annotation { "Feature Type Name" : "Feature", "Feature Type Description" : "" }
export const myFeature = defineFeature(function(context is Context, id is Id, definition is map)
    precondition{}
    {
        {
            var Q0;
            Q0=qCreatedBy(makeId("Top.planeOp"),FACE);
            var sketch = newSketch(context, id + "F0", { "sketchPlane" : qUnion([Q0])});
            skLineSegment(sketch, "E0.bottom", {"start": v(-100, -37.5) * mm, "end": v(100, -37.5) * mm, "construction": true});
            skLineSegment(sketch, "E0.top", {"start": v(-100, 37.5) * mm, "end": v(100, 37.5) * mm, "construction": true});
            skLineSegment(sketch, "E0.left", {"start": v(-100, -37.5) * mm, "end": v(-100, 37.5) * mm, "construction": true});
            skLineSegment(sketch, "E0.right", {"start": v(100, -37.5) * mm, "end": v(100, 37.5) * mm, "construction": true});
            skPoint(sketch, "E0.middle", {"position": v(0, 0) * mm});
            skLineSegment(sketch, "E1.bottom", {"start": v(-70, -15.23) * mm, "end": v(70, -15.23) * mm});
            skLineSegment(sketch, "E1.top", {"start": v(-70, 15.23) * mm, "end": v(70, 15.23) * mm});
            skLineSegment(sketch, "E1.left", {"start": v(-70, -15.23) * mm, "end": v(-70, 15.23) * mm});
            skLineSegment(sketch, "E1.right", {"start": v(70, -15.23) * mm, "end": v(70, 15.23) * mm});
            skLineSegment(sketch, "E2", {"start": v(-70, 0) * mm, "end": v(-95, 0) * mm, "construction": true});
            skLineSegment(sketch, "E3", {"start": v(-95, 0) * mm, "end": v(-70, 15.23) * mm});
            skLineSegment(sketch, "E4", {"start": v(-95, 0) * mm, "end": v(-70, -15.23) * mm});
            skLineSegment(sketch, "E5", {"start": v(70, 15.23) * mm, "end": v(95, 0) * mm});
            skLineSegment(sketch, "E6", {"start": v(95, 0) * mm, "end": v(70, -15.23) * mm});
            skLineSegment(sketch, "E7", {"start": v(70, 0) * mm, "end": v(95, 0) * mm, "construction": true});
            skSolve(sketch);
        }
        {
            var Q0;
            Q0=qSketchRegion(id+"F0",true);
            extrude(context, id + "F1", {"entities" : qUnion([Q0]), "depth" : 5 * mm, "offsetDistance" : 25 * mm});
        }
        {
            var Q0;
            Q0=makeQuery(id+"F1.opExtrude","SWEPT_EDGE",EDGE,{"disambiguationData":[OSD([sQuery(id+"F0.wireOp",EDGE,"E3"),sQuery(id+"F0.wireOp",EDGE,"E4")])]});
            var Q1;
            Q1=makeQuery(id+"F1.opExtrude","SWEPT_EDGE",EDGE,{"disambiguationData":[OSD([sQuery(id+"F0.wireOp",EDGE,"E5"),sQuery(id+"F0.wireOp",EDGE,"E6")])]});
            fillet(context, id + "F2", {"entities" : qUnion([Q0, Q1]), "radius" : 10 * mm, "tangentPropagation" : true, "allowEdgeOverflow" : false});
        }
        {
            var Q0;
            Q0=makeQuery(id+"F1.opExtrude","SWEPT_EDGE",EDGE,{"disambiguationData":[OSD([sQuery(id+"F0.wireOp",EDGE,"E1.bottom"),sQuery(id+"F0.wireOp",EDGE,"E1.right"),sQuery(id+"F0.wireOp",EDGE,"E6")])]});
            var Q1;
            Q1=makeQuery(id+"F1.opExtrude","SWEPT_EDGE",EDGE,{"disambiguationData":[OSD([sQuery(id+"F0.wireOp",EDGE,"E1.bottom"),sQuery(id+"F0.wireOp",EDGE,"E1.left"),sQuery(id+"F0.wireOp",EDGE,"E4")])]});
            var Q2;
            Q2=makeQuery(id+"F1.opExtrude","SWEPT_EDGE",EDGE,{"disambiguationData":[OSD([sQuery(id+"F0.wireOp",EDGE,"E1.top"),sQuery(id+"F0.wireOp",EDGE,"E1.left"),sQuery(id+"F0.wireOp",EDGE,"E3")])]});
            var Q3;
            Q3=makeQuery(id+"F1.opExtrude","SWEPT_EDGE",EDGE,{"disambiguationData":[OSD([sQuery(id+"F0.wireOp",EDGE,"E1.top"),sQuery(id+"F0.wireOp",EDGE,"E1.right"),sQuery(id+"F0.wireOp",EDGE,"E5")])]});
            fillet(context, id + "F3", {"entities" : qUnion([Q0, Q1, Q2, Q3]), "radius" : 10 * mm, "tangentPropagation" : true, "allowEdgeOverflow" : false});
        }
        {
            var Q0;
            Q0=makeQuery(id+"F1.opExtrude","CAP_FACE",FACE,{"disambiguationData":[OSD([sQuery(id+"F0.wireOp",EDGE,"E1.bottom"),sQuery(id+"F0.wireOp",EDGE,"E1.top"),sQuery(id+"F0.wireOp",EDGE,"E3"),sQuery(id+"F0.wireOp",EDGE,"E4"),sQuery(id+"F0.wireOp",EDGE,"E5"),sQuery(id+"F0.wireOp",EDGE,"E6")])],"isStart":false});
            var sketch = newSketch(context, id + "F4", { "sketchPlane" : qUnion([Q0])});
            skText(sketch, "E8", { "text": "Miss Loveday", "fontName": "OpenSans-BoldItalic.ttf"});
            const initialGuessF4  = {"E8": [-0.05, -0.00564, 1, 0, 0.01129]};
            skSetInitialGuess(sketch, initialGuessF4);
            skSolve(sketch);
        }
        {
            var Q0;
            Q0=qSketchRegion(id+"F4",true);
            extrude(context, id + "F5", {"entities" : qUnion([Q0]), "operationType" : NewBodyOperationType.ADD, "depth" : 3 * mm, "offsetDistance" : 25 * mm});
        }
        {
            var Q0;
            {var subQ0=sQuery(id+"F0.wireOp",EDGE,"E5");var subQ2=sQuery(id+"F0.wireOp",EDGE,"E1.top");var subQ3=sQuery(id+"F0.wireOp",EDGE,"E3");var subQ5=sQuery(id+"F0.wireOp",EDGE,"E4");var subQ6=sQuery(id+"F0.wireOp",EDGE,"E6");var subQ7=sQuery(id+"F0.wireOp",EDGE,"E1.bottom");Q0=makeQuery(id+"F5.boolean.opBoolean","SPLIT",FACE,{"disambiguationData":[TD([makeQuery(id+"F1.opExtrude","SWEPT_FACE",FACE,{"disambiguationData":[OSD([subQ7])]})])],"derivedFrom":makeQuery(id+"F1.opExtrude","CAP_FACE",FACE,{"disambiguationData":[OSD([subQ7,subQ2,subQ3,subQ5,subQ0,subQ6])],"isStart":false})});}
            var sketch = newSketch(context, id + "F6", { "sketchPlane" : qUnion([Q0])});
            skPoint(sketch, "E9", {"position": v(-75.78, 0) * mm});
            skPoint(sketch, "E10", {"position": v(75.78, 0) * mm});
            skSolve(sketch);
        }
        {
            var Q0;
            Q0=sQuery(id+"F6.wireOp",VERTEX,"E10");
            var Q1;
            Q1=sQuery(id+"F6.wireOp",VERTEX,"E9");
            var Q2;
            Q2=makeQuery(id+"F1.opExtrude","SWEPT_BODY",BODY,{"disambiguationData":[OSD([sQuery(id+"F0.wireOp",EDGE,"E1.bottom"),sQuery(id+"F0.wireOp",EDGE,"E1.top"),sQuery(id+"F0.wireOp",EDGE,"E3"),sQuery(id+"F0.wireOp",EDGE,"E4"),sQuery(id+"F0.wireOp",EDGE,"E5"),sQuery(id+"F0.wireOp",EDGE,"E6")])]});
            hole(context, id + "F7", {"style" : HoleStyle.SIMPLE, "endStyle" : HoleEndStyle.THROUGH, "standardTappedOrClearance" : lookupTablePath({ "fit" : "Normal", "standard" : "ISO", "size" : "M5", "type" : "Clearance" }), "standardBlindInLast" : lookupTablePath({ "fit" : "Normal", "standard" : "ISO", "size" : "M5", "type" : "Clearance" }), "holeDiameter" : 5.5 * mm, "majorDiameter" : 5 * mm, "isTappedThrough" : true, "tappedDepth" : 12 * mm, "tapClearance" : 3, "locations" : qUnion([Q0, Q1]), "scope" : qUnion([Q2])});
        }
        {
            var Q0;
            {var subQ0=sQuery(id+"F0.wireOp",EDGE,"E5");var subQ2=sQuery(id+"F0.wireOp",EDGE,"E1.top");var subQ3=sQuery(id+"F0.wireOp",EDGE,"E3");var subQ5=sQuery(id+"F0.wireOp",EDGE,"E4");var subQ6=sQuery(id+"F0.wireOp",EDGE,"E6");var subQ7=sQuery(id+"F0.wireOp",EDGE,"E1.bottom");Q0=makeQuery(id+"F5.boolean.opBoolean","SPLIT",FACE,{"disambiguationData":[TD([makeQuery(id+"F1.opExtrude","SWEPT_FACE",FACE,{"disambiguationData":[OSD([subQ7])]})])],"derivedFrom":makeQuery(id+"F1.opExtrude","CAP_FACE",FACE,{"disambiguationData":[OSD([subQ7,subQ2,subQ3,subQ5,subQ0,subQ6])],"isStart":false})});}
            var sketch = newSketch(context, id + "F8", { "sketchPlane" : qUnion([Q0])});
            skLineSegment(sketch, "E11.bottom", {"start": v(-69.8, 10) * mm, "end": v(-49.8, 10) * mm, "construction": true});
            skLineSegment(sketch, "E11.top", {"start": v(-69.8, -10) * mm, "end": v(-49.8, -10) * mm, "construction": true});
            skLineSegment(sketch, "E11.left", {"start": v(-69.8, 10) * mm, "end": v(-69.8, -10) * mm, "construction": true});
            skLineSegment(sketch, "E11.right", {"start": v(-49.8, 10) * mm, "end": v(-49.8, -10) * mm, "construction": true});
            skLineSegment(sketch, "E12", {"start": v(-69.8, -10) * mm, "end": v(-49.8, 10) * mm, "construction": true});
            skLineSegment(sketch, "E13", {"start": v(-75.78, 0) * mm, "end": v(-59.8, 0) * mm, "construction": true});
            skLineSegment(sketch, "E14", {"start": v(-64.45, -8.4) * mm, "end": v(-65.16, -7.74) * mm});
            skLineSegment(sketch, "E15", {"start": v(-65.16, -7.74) * mm, "end": v(-65.7, -7.23) * mm});
            skLineSegment(sketch, "E16", {"start": v(-65.7, -7.23) * mm, "end": v(-66.13, -6.83) * mm});
            skLineSegment(sketch, "E17", {"start": v(-66.13, -6.83) * mm, "end": v(-66.45, -6.52) * mm});
            skLineSegment(sketch, "E18", {"start": v(-66.45, -6.52) * mm, "end": v(-66.69, -6.26) * mm});
            skLineSegment(sketch, "E19", {"start": v(-66.69, -6.26) * mm, "end": v(-66.87, -6.05) * mm});
            skLineSegment(sketch, "E20", {"start": v(-66.87, -6.05) * mm, "end": v(-67.03, -5.85) * mm});
            skLineSegment(sketch, "E21", {"start": v(-67.03, -5.85) * mm, "end": v(-67.17, -5.64) * mm});
            skLineSegment(sketch, "E22", {"start": v(-67.17, -5.64) * mm, "end": v(-67.67, -4.76) * mm});
            skLineSegment(sketch, "E23", {"start": v(-67.67, -4.76) * mm, "end": v(-67.96, -3.88) * mm});
            skLineSegment(sketch, "E24", {"start": v(-67.96, -3.88) * mm, "end": v(-68.07, -3.03) * mm});
            skLineSegment(sketch, "E25", {"start": v(-68.07, -3.03) * mm, "end": v(-67.98, -2.23) * mm});
            skLineSegment(sketch, "E26", {"start": v(-67.98, -2.23) * mm, "end": v(-67.72, -1.5) * mm});
            skLineSegment(sketch, "E27", {"start": v(-67.72, -1.5) * mm, "end": v(-67.28, -0.88) * mm});
            skLineSegment(sketch, "E28", {"start": v(-67.28, -0.88) * mm, "end": v(-66.67, -0.38) * mm});
            skLineSegment(sketch, "E29", {"start": v(-66.67, -0.38) * mm, "end": v(-65.9, -0.02) * mm});
            skLineSegment(sketch, "E30", {"start": v(-65.9, -0.02) * mm, "end": v(-65.77, 0.01) * mm});
            skLineSegment(sketch, "E31", {"start": v(-65.77, 0.01) * mm, "end": v(-65.52, 0.08) * mm});
            skLineSegment(sketch, "E32", {"start": v(-65.52, 0.08) * mm, "end": v(-65.16, 0.17) * mm});
            skLineSegment(sketch, "E33", {"start": v(-65.16, 0.17) * mm, "end": v(-64.71, 0.27) * mm});
            skLineSegment(sketch, "E34", {"start": v(-64.71, 0.27) * mm, "end": v(-64.18, 0.4) * mm});
            skLineSegment(sketch, "E35", {"start": v(-64.18, 0.4) * mm, "end": v(-63.6, 0.54) * mm});
            skLineSegment(sketch, "E36", {"start": v(-63.6, 0.54) * mm, "end": v(-62.95, 0.7) * mm});
            skLineSegment(sketch, "E37", {"start": v(-62.95, 0.7) * mm, "end": v(-62.28, 0.85) * mm});
            skLineSegment(sketch, "E38", {"start": v(-62.28, 0.85) * mm, "end": v(-58.96, 1.63) * mm});
            skLineSegment(sketch, "E39", {"start": v(-58.96, 1.63) * mm, "end": v(-57.57, 4.57) * mm});
            skLineSegment(sketch, "E40", {"start": v(-57.57, 4.57) * mm, "end": v(-57.23, 5.28) * mm});
            skLineSegment(sketch, "E41", {"start": v(-57.23, 5.28) * mm, "end": v(-56.93, 5.9) * mm});
            skLineSegment(sketch, "E42", {"start": v(-56.93, 5.9) * mm, "end": v(-56.68, 6.43) * mm});
            skLineSegment(sketch, "E43", {"start": v(-56.68, 6.43) * mm, "end": v(-56.46, 6.87) * mm});
            skLineSegment(sketch, "E44", {"start": v(-56.46, 6.87) * mm, "end": v(-56.28, 7.21) * mm});
            skLineSegment(sketch, "E45", {"start": v(-56.28, 7.21) * mm, "end": v(-56.14, 7.48) * mm});
            skLineSegment(sketch, "E46", {"start": v(-56.14, 7.48) * mm, "end": v(-56.03, 7.67) * mm});
            skLineSegment(sketch, "E47", {"start": v(-56.03, 7.67) * mm, "end": v(-55.96, 7.77) * mm});
            skLineSegment(sketch, "E48", {"start": v(-55.96, 7.77) * mm, "end": v(-55.72, 8) * mm});
            skLineSegment(sketch, "E49", {"start": v(-55.72, 8) * mm, "end": v(-55.44, 8.21) * mm});
            skLineSegment(sketch, "E50", {"start": v(-55.44, 8.21) * mm, "end": v(-55.13, 8.38) * mm});
            skLineSegment(sketch, "E51", {"start": v(-55.13, 8.38) * mm, "end": v(-54.82, 8.49) * mm});
            skLineSegment(sketch, "E52", {"start": v(-54.82, 8.49) * mm, "end": v(-54.42, 8.52) * mm});
            skLineSegment(sketch, "E53", {"start": v(-54.42, 8.52) * mm, "end": v(-53.98, 8.45) * mm});
            skLineSegment(sketch, "E54", {"start": v(-53.98, 8.45) * mm, "end": v(-53.56, 8.28) * mm});
            skLineSegment(sketch, "E55", {"start": v(-53.56, 8.28) * mm, "end": v(-53.2, 8.03) * mm});
            skLineSegment(sketch, "E56", {"start": v(-53.2, 8.03) * mm, "end": v(-52.9, 7.87) * mm});
            skLineSegment(sketch, "E57", {"start": v(-52.9, 7.87) * mm, "end": v(-52.3, 7.7) * mm});
            skLineSegment(sketch, "E58", {"start": v(-52.3, 7.7) * mm, "end": v(-52.01, 7.62) * mm});
            skLineSegment(sketch, "E59", {"start": v(-52.01, 7.62) * mm, "end": v(-51.76, 7.55) * mm});
            skLineSegment(sketch, "E60", {"start": v(-51.76, 7.55) * mm, "end": v(-51.58, 7.48) * mm});
            skLineSegment(sketch, "E61", {"start": v(-51.58, 7.48) * mm, "end": v(-51.5, 7.43) * mm});
            skLineSegment(sketch, "E62", {"start": v(-51.5, 7.43) * mm, "end": v(-51.45, 7.33) * mm});
            skLineSegment(sketch, "E63", {"start": v(-51.45, 7.33) * mm, "end": v(-51.45, 7.18) * mm});
            skLineSegment(sketch, "E64", {"start": v(-51.45, 7.18) * mm, "end": v(-51.5, 6.96) * mm});
            skLineSegment(sketch, "E65", {"start": v(-51.5, 6.96) * mm, "end": v(-51.58, 6.65) * mm});
            skLineSegment(sketch, "E66", {"start": v(-51.58, 6.65) * mm, "end": v(-51.67, 6.36) * mm});
            skLineSegment(sketch, "E67", {"start": v(-51.67, 6.36) * mm, "end": v(-52.71, 5.74) * mm});
            skLineSegment(sketch, "E68", {"start": v(-52.71, 5.74) * mm, "end": v(-53.76, 5.12) * mm});
            skLineSegment(sketch, "E69", {"start": v(-53.76, 5.12) * mm, "end": v(-53.76, 2.41) * mm});
            skLineSegment(sketch, "E70", {"start": v(-53.76, 2.41) * mm, "end": v(-53.77, 1.3) * mm});
            skLineSegment(sketch, "E71", {"start": v(-53.77, 1.3) * mm, "end": v(-53.78, 0.33) * mm});
            skLineSegment(sketch, "E72", {"start": v(-53.78, 0.33) * mm, "end": v(-53.8, -0.39) * mm});
            skLineSegment(sketch, "E73", {"start": v(-53.8, -0.39) * mm, "end": v(-53.82, -0.79) * mm});
            skLineSegment(sketch, "E74", {"start": v(-53.82, -0.79) * mm, "end": v(-53.9, -1.32) * mm});
            skLineSegment(sketch, "E75", {"start": v(-53.9, -1.32) * mm, "end": v(-54.05, -1.87) * mm});
            skLineSegment(sketch, "E76", {"start": v(-54.05, -1.87) * mm, "end": v(-54.22, -2.41) * mm});
            skLineSegment(sketch, "E77", {"start": v(-54.22, -2.41) * mm, "end": v(-54.42, -2.88) * mm});
            skLineSegment(sketch, "E78", {"start": v(-54.42, -2.88) * mm, "end": v(-54.5, -3.02) * mm});
            skLineSegment(sketch, "E79", {"start": v(-54.5, -3.02) * mm, "end": v(-54.54, -3.13) * mm});
            skLineSegment(sketch, "E80", {"start": v(-54.54, -3.13) * mm, "end": v(-54.58, -3.22) * mm});
            skLineSegment(sketch, "E81", {"start": v(-54.58, -3.22) * mm, "end": v(-54.6, -3.29) * mm});
            skLineSegment(sketch, "E82", {"start": v(-54.6, -3.29) * mm, "end": v(-54.6, -3.34) * mm});
            skLineSegment(sketch, "E83", {"start": v(-54.6, -3.34) * mm, "end": v(-54.6, -3.39) * mm});
            skLineSegment(sketch, "E84", {"start": v(-54.6, -3.39) * mm, "end": v(-54.58, -3.43) * mm});
            skLineSegment(sketch, "E85", {"start": v(-54.58, -3.43) * mm, "end": v(-54.55, -3.49) * mm});
            skLineSegment(sketch, "E86", {"start": v(-54.55, -3.49) * mm, "end": v(-54.4, -3.8) * mm});
            skLineSegment(sketch, "E87", {"start": v(-54.4, -3.8) * mm, "end": v(-54.3, -4.08) * mm});
            skLineSegment(sketch, "E88", {"start": v(-54.3, -4.08) * mm, "end": v(-54.24, -4.37) * mm});
            skLineSegment(sketch, "E89", {"start": v(-54.24, -4.37) * mm, "end": v(-54.23, -4.7) * mm});
            skLineSegment(sketch, "E90", {"start": v(-54.23, -4.7) * mm, "end": v(-54.23, -4.96) * mm});
            skLineSegment(sketch, "E91", {"start": v(-54.23, -4.96) * mm, "end": v(-54.26, -5.2) * mm});
            skLineSegment(sketch, "E92", {"start": v(-54.26, -5.2) * mm, "end": v(-54.34, -5.42) * mm});
            skLineSegment(sketch, "E93", {"start": v(-54.34, -5.42) * mm, "end": v(-54.46, -5.67) * mm});
            skLineSegment(sketch, "E94", {"start": v(-54.46, -5.67) * mm, "end": v(-54.65, -5.97) * mm});
            skLineSegment(sketch, "E95", {"start": v(-54.65, -5.97) * mm, "end": v(-54.92, -6.33) * mm});
            skLineSegment(sketch, "E96", {"start": v(-54.92, -6.33) * mm, "end": v(-55.29, -6.8) * mm});
            skLineSegment(sketch, "E97", {"start": v(-55.29, -6.8) * mm, "end": v(-55.77, -7.37) * mm});
            skLineSegment(sketch, "E98", {"start": v(-55.77, -7.37) * mm, "end": v(-56.09, -7.76) * mm});
            skLineSegment(sketch, "E99", {"start": v(-56.09, -7.76) * mm, "end": v(-56.35, -8.07) * mm});
            skLineSegment(sketch, "E100", {"start": v(-56.35, -8.07) * mm, "end": v(-56.57, -8.33) * mm});
            skLineSegment(sketch, "E101", {"start": v(-56.57, -8.33) * mm, "end": v(-56.75, -8.53) * mm});
            skLineSegment(sketch, "E102", {"start": v(-56.75, -8.53) * mm, "end": v(-56.89, -8.67) * mm});
            skLineSegment(sketch, "E103", {"start": v(-56.89, -8.67) * mm, "end": v(-57, -8.77) * mm});
            skLineSegment(sketch, "E104", {"start": v(-57, -8.77) * mm, "end": v(-57.07, -8.82) * mm});
            skLineSegment(sketch, "E105", {"start": v(-57.07, -8.82) * mm, "end": v(-57.11, -8.84) * mm});
            skLineSegment(sketch, "E106", {"start": v(-57.11, -8.84) * mm, "end": v(-57.23, -8.8) * mm});
            skLineSegment(sketch, "E107", {"start": v(-57.23, -8.8) * mm, "end": v(-57.34, -8.72) * mm});
            skLineSegment(sketch, "E108", {"start": v(-57.34, -8.72) * mm, "end": v(-57.43, -8.61) * mm});
            skLineSegment(sketch, "E109", {"start": v(-57.43, -8.61) * mm, "end": v(-57.46, -8.5) * mm});
            skLineSegment(sketch, "E110", {"start": v(-57.46, -8.5) * mm, "end": v(-57.44, -8.36) * mm});
            skLineSegment(sketch, "E111", {"start": v(-57.44, -8.36) * mm, "end": v(-57.4, -8.04) * mm});
            skLineSegment(sketch, "E112", {"start": v(-57.4, -8.04) * mm, "end": v(-57.32, -7.58) * mm});
            skLineSegment(sketch, "E113", {"start": v(-57.32, -7.58) * mm, "end": v(-57.22, -7.02) * mm});
            skLineSegment(sketch, "E114", {"start": v(-57.22, -7.02) * mm, "end": v(-57.13, -6.48) * mm});
            skLineSegment(sketch, "E115", {"start": v(-57.13, -6.48) * mm, "end": v(-57.07, -6.03) * mm});
            skLineSegment(sketch, "E116", {"start": v(-57.07, -6.03) * mm, "end": v(-57.03, -5.72) * mm});
            skLineSegment(sketch, "E117", {"start": v(-57.03, -5.72) * mm, "end": v(-57.03, -5.6) * mm});
            skLineSegment(sketch, "E118", {"start": v(-57.03, -5.6) * mm, "end": v(-57.08, -5.6) * mm});
            skLineSegment(sketch, "E119", {"start": v(-57.08, -5.6) * mm, "end": v(-57.17, -5.63) * mm});
            skLineSegment(sketch, "E120", {"start": v(-57.17, -5.63) * mm, "end": v(-57.3, -5.66) * mm});
            skLineSegment(sketch, "E121", {"start": v(-57.3, -5.66) * mm, "end": v(-57.44, -5.71) * mm});
            skLineSegment(sketch, "E122", {"start": v(-57.44, -5.71) * mm, "end": v(-57.69, -5.8) * mm});
            skLineSegment(sketch, "E123", {"start": v(-57.69, -5.8) * mm, "end": v(-57.93, -5.85) * mm});
            skLineSegment(sketch, "E124", {"start": v(-57.93, -5.85) * mm, "end": v(-58.2, -5.9) * mm});
            skLineSegment(sketch, "E125", {"start": v(-58.2, -5.9) * mm, "end": v(-58.55, -5.93) * mm});
            skLineSegment(sketch, "E126", {"start": v(-58.55, -5.93) * mm, "end": v(-58.99, -5.95) * mm});
            skLineSegment(sketch, "E127", {"start": v(-58.99, -5.95) * mm, "end": v(-59.55, -5.96) * mm});
            skLineSegment(sketch, "E128", {"start": v(-59.55, -5.96) * mm, "end": v(-60.28, -5.97) * mm});
            skLineSegment(sketch, "E129", {"start": v(-60.28, -5.97) * mm, "end": v(-61.2, -5.97) * mm});
            skLineSegment(sketch, "E130", {"start": v(-61.2, -5.97) * mm, "end": v(-63.87, -5.97) * mm});
            skLineSegment(sketch, "E131", {"start": v(-63.87, -5.97) * mm, "end": v(-63.5, -6.4) * mm});
            skLineSegment(sketch, "E132", {"start": v(-63.5, -6.4) * mm, "end": v(-63.12, -6.96) * mm});
            skLineSegment(sketch, "E133", {"start": v(-63.12, -6.96) * mm, "end": v(-62.83, -7.61) * mm});
            skLineSegment(sketch, "E134", {"start": v(-62.83, -7.61) * mm, "end": v(-62.64, -8.31) * mm});
            skLineSegment(sketch, "E135", {"start": v(-62.64, -8.31) * mm, "end": v(-62.58, -9.03) * mm});
            skLineSegment(sketch, "E136", {"start": v(-62.58, -9.03) * mm, "end": v(-62.6, -9.34) * mm});
            skLineSegment(sketch, "E137", {"start": v(-62.6, -9.34) * mm, "end": v(-62.64, -9.57) * mm});
            skLineSegment(sketch, "E138", {"start": v(-62.64, -9.57) * mm, "end": v(-62.72, -9.72) * mm});
            skLineSegment(sketch, "E139", {"start": v(-62.72, -9.72) * mm, "end": v(-62.82, -9.78) * mm});
            skLineSegment(sketch, "E140", {"start": v(-62.82, -9.78) * mm, "end": v(-62.97, -9.7) * mm});
            skLineSegment(sketch, "E141", {"start": v(-62.97, -9.7) * mm, "end": v(-63.3, -9.42) * mm});
            skLineSegment(sketch, "E142", {"start": v(-63.3, -9.42) * mm, "end": v(-63.8, -8.98) * mm});
            skLineSegment(sketch, "E143", {"start": v(-63.8, -8.98) * mm, "end": v(-64.45, -8.4) * mm});
            skCircle(sketch, "E144", {"center": v(-54.26, 7.57) * mm, "radius": 0.28 * mm});
            skSolve(sketch);
        }
        {
            var Q0;
            Q0=makeQuery(id+"F8.imprint","IMPRINT",FACE,{"disambiguationData":[TD([[makeQuery(id+"F8.imprint","IMPRINT",EDGE,{"derivedFrom":sQuery(id+"F8.wireOp",EDGE,"E14")}),-1.0]])]});
            extrude(context, id + "F9", {"entities" : qUnion([Q0]), "operationType" : NewBodyOperationType.ADD, "depth" : 3 * mm, "offsetDistance" : 25 * mm});
        }
        {
            var Q0;
            {var subQ44=sQuery(id+"F0.wireOp",EDGE,"E5");var subQ46=sQuery(id+"F0.wireOp",EDGE,"E1.top");var subQ49=sQuery(id+"F0.wireOp",EDGE,"E3");var subQ55=sQuery(id+"F0.wireOp",EDGE,"E6");var subQ56=sQuery(id+"F0.wireOp",EDGE,"E1.bottom");var subQ63=sQuery(id+"F0.wireOp",EDGE,"E4");var subQ74=makeQuery(id+"F1.opExtrude","SWEPT_FACE",FACE,{"disambiguationData":[OSD([subQ56])]});Q0=makeQuery(id+"F9.boolean.opBoolean","SPLIT",FACE,{"disambiguationData":[TD([subQ74])],"derivedFrom":makeQuery(id+"F5.boolean.opBoolean","SPLIT",FACE,{"disambiguationData":[TD([subQ74])],"derivedFrom":makeQuery(id+"F1.opExtrude","CAP_FACE",FACE,{"disambiguationData":[OSD([subQ56,subQ46,subQ49,subQ63,subQ44,subQ55])],"isStart":false})})});}
            var sketch = newSketch(context, id + "F10", { "sketchPlane" : qUnion([Q0])});
            skLineSegment(sketch, "E145", {"start": v(59.13, -6.81) * mm, "end": v(59.15, -6.82) * mm});
            skLineSegment(sketch, "E146", {"start": v(59.15, -6.82) * mm, "end": v(59.17, -6.84) * mm});
            skLineSegment(sketch, "E147", {"start": v(59.17, -6.84) * mm, "end": v(59.2, -6.85) * mm});
            skLineSegment(sketch, "E148", {"start": v(59.2, -6.85) * mm, "end": v(59.25, -6.86) * mm});
            skLineSegment(sketch, "E149", {"start": v(59.25, -6.86) * mm, "end": v(59.3, -6.87) * mm});
            skLineSegment(sketch, "E150", {"start": v(59.3, -6.87) * mm, "end": v(59.61, -6.87) * mm});
            skLineSegment(sketch, "E151", {"start": v(59.61, -6.87) * mm, "end": v(59.92, -6.87) * mm});
            skLineSegment(sketch, "E152", {"start": v(59.92, -6.87) * mm, "end": v(59.96, -6.85) * mm});
            skLineSegment(sketch, "E153", {"start": v(59.96, -6.85) * mm, "end": v(59.98, -6.83) * mm});
            skLineSegment(sketch, "E154", {"start": v(59.98, -6.83) * mm, "end": v(60.01, -6.8) * mm});
            skLineSegment(sketch, "E155", {"start": v(60.01, -6.8) * mm, "end": v(60.04, -6.77) * mm});
            skLineSegment(sketch, "E156", {"start": v(60.04, -6.77) * mm, "end": v(60.07, -6.71) * mm});
            skLineSegment(sketch, "E157", {"start": v(60.07, -6.71) * mm, "end": v(60.22, -6.46) * mm});
            skLineSegment(sketch, "E158", {"start": v(60.22, -6.46) * mm, "end": v(60.25, -6.42) * mm});
            skLineSegment(sketch, "E159", {"start": v(60.25, -6.42) * mm, "end": v(60.27, -6.4) * mm});
            skLineSegment(sketch, "E160", {"start": v(60.27, -6.4) * mm, "end": v(60.3, -6.38) * mm});
            skLineSegment(sketch, "E161", {"start": v(60.3, -6.38) * mm, "end": v(60.3, -6.4) * mm});
            skLineSegment(sketch, "E162", {"start": v(60.3, -6.4) * mm, "end": v(60.33, -6.41) * mm});
            skLineSegment(sketch, "E163", {"start": v(60.33, -6.41) * mm, "end": v(60.34, -6.42) * mm});
            skLineSegment(sketch, "E164", {"start": v(60.34, -6.42) * mm, "end": v(60.35, -6.42) * mm});
            skLineSegment(sketch, "E165", {"start": v(60.35, -6.42) * mm, "end": v(60.35, -6.43) * mm});
            skLineSegment(sketch, "E166", {"start": v(60.35, -6.43) * mm, "end": v(60.36, -6.43) * mm});
            skLineSegment(sketch, "E167", {"start": v(60.36, -6.43) * mm, "end": v(60.37, -6.43) * mm});
            skLineSegment(sketch, "E168", {"start": v(60.37, -6.43) * mm, "end": v(60.37, -6.43) * mm});
            skLineSegment(sketch, "E169", {"start": v(60.37, -6.43) * mm, "end": v(60.38, -6.43) * mm});
            skLineSegment(sketch, "E170", {"start": v(60.38, -6.43) * mm, "end": v(60.38, -6.43) * mm});
            skLineSegment(sketch, "E171", {"start": v(60.38, -6.43) * mm, "end": v(60.39, -6.42) * mm});
            skLineSegment(sketch, "E172", {"start": v(60.39, -6.42) * mm, "end": v(60.4, -6.42) * mm});
            skLineSegment(sketch, "E173", {"start": v(60.4, -6.42) * mm, "end": v(60.41, -6.41) * mm});
            skLineSegment(sketch, "E174", {"start": v(60.41, -6.41) * mm, "end": v(60.43, -6.4) * mm});
            skLineSegment(sketch, "E175", {"start": v(60.43, -6.4) * mm, "end": v(60.48, -6.35) * mm});
            skLineSegment(sketch, "E176", {"start": v(60.48, -6.35) * mm, "end": v(60.5, -6.34) * mm});
            skLineSegment(sketch, "E177", {"start": v(60.5, -6.34) * mm, "end": v(60.5, -6.34) * mm});
            skLineSegment(sketch, "E178", {"start": v(60.5, -6.34) * mm, "end": v(60.51, -6.33) * mm});
            skLineSegment(sketch, "E179", {"start": v(60.51, -6.33) * mm, "end": v(60.52, -6.33) * mm});
            skLineSegment(sketch, "E180", {"start": v(60.52, -6.33) * mm, "end": v(60.53, -6.33) * mm});
            skLineSegment(sketch, "E181", {"start": v(60.53, -6.33) * mm, "end": v(60.53, -6.34) * mm});
            skLineSegment(sketch, "E182", {"start": v(60.53, -6.34) * mm, "end": v(60.54, -6.34) * mm});
            skLineSegment(sketch, "E183", {"start": v(60.54, -6.34) * mm, "end": v(60.55, -6.34) * mm});
            skLineSegment(sketch, "E184", {"start": v(60.55, -6.34) * mm, "end": v(60.55, -6.34) * mm});
            skLineSegment(sketch, "E185", {"start": v(60.55, -6.34) * mm, "end": v(60.57, -6.35) * mm});
            skLineSegment(sketch, "E186", {"start": v(60.57, -6.35) * mm, "end": v(60.58, -6.36) * mm});
            skLineSegment(sketch, "E187", {"start": v(60.58, -6.36) * mm, "end": v(60.6, -6.38) * mm});
            skLineSegment(sketch, "E188", {"start": v(60.6, -6.38) * mm, "end": v(60.6, -6.33) * mm});
            skLineSegment(sketch, "E189", {"start": v(60.6, -6.33) * mm, "end": v(60.6, -6.29) * mm});
            skLineSegment(sketch, "E190", {"start": v(60.6, -6.29) * mm, "end": v(60.62, -6.25) * mm});
            skLineSegment(sketch, "E191", {"start": v(60.62, -6.25) * mm, "end": v(60.64, -6.2) * mm});
            skLineSegment(sketch, "E192", {"start": v(60.64, -6.2) * mm, "end": v(60.67, -6.14) * mm});
            skLineSegment(sketch, "E193", {"start": v(60.67, -6.14) * mm, "end": v(60.75, -5.98) * mm});
            skLineSegment(sketch, "E194", {"start": v(60.75, -5.98) * mm, "end": v(60.77, -5.93) * mm});
            skLineSegment(sketch, "E195", {"start": v(60.77, -5.93) * mm, "end": v(60.78, -5.9) * mm});
            skLineSegment(sketch, "E196", {"start": v(60.78, -5.9) * mm, "end": v(60.79, -5.85) * mm});
            skLineSegment(sketch, "E197", {"start": v(60.79, -5.85) * mm, "end": v(60.8, -5.8) * mm});
            skLineSegment(sketch, "E198", {"start": v(60.8, -5.8) * mm, "end": v(60.8, -5.76) * mm});
            skLineSegment(sketch, "E199", {"start": v(60.8, -5.76) * mm, "end": v(60.78, -5.7) * mm});
            skLineSegment(sketch, "E200", {"start": v(60.78, -5.7) * mm, "end": v(60.82, -5.7) * mm});
            skLineSegment(sketch, "E201", {"start": v(60.82, -5.7) * mm, "end": v(60.85, -5.68) * mm});
            skLineSegment(sketch, "E202", {"start": v(60.85, -5.68) * mm, "end": v(60.88, -5.66) * mm});
            skLineSegment(sketch, "E203", {"start": v(60.88, -5.66) * mm, "end": v(60.9, -5.64) * mm});
            skLineSegment(sketch, "E204", {"start": v(60.9, -5.64) * mm, "end": v(60.94, -5.6) * mm});
            skLineSegment(sketch, "E205", {"start": v(60.94, -5.6) * mm, "end": v(61.08, -5.44) * mm});
            skLineSegment(sketch, "E206", {"start": v(61.08, -5.44) * mm, "end": v(61.21, -5.28) * mm});
            skLineSegment(sketch, "E207", {"start": v(61.21, -5.28) * mm, "end": v(61.22, -5.27) * mm});
            skLineSegment(sketch, "E208", {"start": v(61.22, -5.27) * mm, "end": v(61.22, -5.27) * mm});
            skLineSegment(sketch, "E209", {"start": v(61.22, -5.27) * mm, "end": v(61.23, -5.26) * mm});
            skLineSegment(sketch, "E210", {"start": v(61.23, -5.26) * mm, "end": v(61.25, -5.26) * mm});
            skLineSegment(sketch, "E211", {"start": v(61.25, -5.26) * mm, "end": v(61.27, -5.25) * mm});
            skLineSegment(sketch, "E212", {"start": v(61.27, -5.25) * mm, "end": v(61.38, -5.23) * mm});
            skLineSegment(sketch, "E213", {"start": v(61.38, -5.23) * mm, "end": v(61.39, -5.22) * mm});
            skLineSegment(sketch, "E214", {"start": v(61.39, -5.22) * mm, "end": v(61.4, -5.22) * mm});
            skLineSegment(sketch, "E215", {"start": v(61.4, -5.22) * mm, "end": v(61.4, -5.21) * mm});
            skLineSegment(sketch, "E216", {"start": v(61.4, -5.21) * mm, "end": v(61.46, -5.16) * mm});
            skLineSegment(sketch, "E217", {"start": v(61.46, -5.16) * mm, "end": v(61.52, -5.1) * mm});
            skLineSegment(sketch, "E218", {"start": v(61.52, -5.1) * mm, "end": v(61.57, -5.03) * mm});
            skLineSegment(sketch, "E219", {"start": v(61.57, -5.03) * mm, "end": v(61.61, -4.97) * mm});
            skLineSegment(sketch, "E220", {"start": v(61.61, -4.97) * mm, "end": v(61.64, -4.9) * mm});
            skLineSegment(sketch, "E221", {"start": v(61.64, -4.9) * mm, "end": v(61.66, -4.85) * mm});
            skLineSegment(sketch, "E222", {"start": v(61.66, -4.85) * mm, "end": v(61.67, -4.8) * mm});
            skLineSegment(sketch, "E223", {"start": v(61.67, -4.8) * mm, "end": v(61.68, -4.73) * mm});
            skLineSegment(sketch, "E224", {"start": v(61.68, -4.73) * mm, "end": v(61.68, -4.65) * mm});
            skLineSegment(sketch, "E225", {"start": v(61.68, -4.65) * mm, "end": v(61.63, -4.2) * mm});
            skLineSegment(sketch, "E226", {"start": v(61.63, -4.2) * mm, "end": v(61.63, -4.12) * mm});
            skLineSegment(sketch, "E227", {"start": v(61.63, -4.12) * mm, "end": v(61.64, -4.05) * mm});
            skLineSegment(sketch, "E228", {"start": v(61.64, -4.05) * mm, "end": v(61.7, -4.15) * mm});
            skLineSegment(sketch, "E229", {"start": v(61.7, -4.15) * mm, "end": v(61.75, -4.25) * mm});
            skLineSegment(sketch, "E230", {"start": v(61.75, -4.25) * mm, "end": v(61.79, -4.37) * mm});
            skLineSegment(sketch, "E231", {"start": v(61.79, -4.37) * mm, "end": v(61.81, -4.5) * mm});
            skLineSegment(sketch, "E232", {"start": v(61.81, -4.5) * mm, "end": v(61.83, -4.63) * mm});
            skLineSegment(sketch, "E233", {"start": v(61.83, -4.63) * mm, "end": v(61.84, -4.78) * mm});
            skLineSegment(sketch, "E234", {"start": v(61.84, -4.78) * mm, "end": v(61.83, -4.97) * mm});
            skLineSegment(sketch, "E235", {"start": v(61.83, -4.97) * mm, "end": v(61.7, -5.08) * mm});
            skLineSegment(sketch, "E236", {"start": v(61.7, -5.08) * mm, "end": v(61.54, -5.27) * mm});
            skLineSegment(sketch, "E237", {"start": v(61.54, -5.27) * mm, "end": v(61.25, -5.64) * mm});
            skLineSegment(sketch, "E238", {"start": v(61.25, -5.64) * mm, "end": v(60.9, -6.01) * mm});
            skLineSegment(sketch, "E239", {"start": v(60.9, -6.01) * mm, "end": v(60.92, -6.1) * mm});
            skLineSegment(sketch, "E240", {"start": v(60.92, -6.1) * mm, "end": v(60.92, -6.18) * mm});
            skLineSegment(sketch, "E241", {"start": v(60.92, -6.18) * mm, "end": v(60.92, -6.24) * mm});
            skLineSegment(sketch, "E242", {"start": v(60.92, -6.24) * mm, "end": v(60.9, -6.3) * mm});
            skLineSegment(sketch, "E243", {"start": v(60.9, -6.3) * mm, "end": v(60.89, -6.38) * mm});
            skLineSegment(sketch, "E244", {"start": v(60.89, -6.38) * mm, "end": v(60.8, -6.64) * mm});
            skLineSegment(sketch, "E245", {"start": v(60.8, -6.64) * mm, "end": v(60.79, -6.7) * mm});
            skLineSegment(sketch, "E246", {"start": v(60.79, -6.7) * mm, "end": v(60.78, -6.76) * mm});
            skLineSegment(sketch, "E247", {"start": v(60.78, -6.76) * mm, "end": v(60.78, -6.81) * mm});
            skLineSegment(sketch, "E248", {"start": v(60.78, -6.81) * mm, "end": v(60.8, -6.82) * mm});
            skLineSegment(sketch, "E249", {"start": v(60.8, -6.82) * mm, "end": v(60.82, -6.84) * mm});
            skLineSegment(sketch, "E250", {"start": v(60.82, -6.84) * mm, "end": v(60.84, -6.84) * mm});
            skLineSegment(sketch, "E251", {"start": v(60.84, -6.84) * mm, "end": v(60.87, -6.86) * mm});
            skLineSegment(sketch, "E252", {"start": v(60.87, -6.86) * mm, "end": v(60.9, -6.86) * mm});
            skLineSegment(sketch, "E253", {"start": v(60.9, -6.86) * mm, "end": v(60.96, -6.87) * mm});
            skLineSegment(sketch, "E254", {"start": v(60.96, -6.87) * mm, "end": v(61.2, -6.87) * mm});
            skLineSegment(sketch, "E255", {"start": v(61.2, -6.87) * mm, "end": v(61.46, -6.87) * mm});
            skLineSegment(sketch, "E256", {"start": v(61.46, -6.87) * mm, "end": v(61.46, -6.86) * mm});
            skLineSegment(sketch, "E257", {"start": v(61.46, -6.86) * mm, "end": v(61.47, -6.85) * mm});
            skLineSegment(sketch, "E258", {"start": v(61.47, -6.85) * mm, "end": v(61.47, -6.84) * mm});
            skLineSegment(sketch, "E259", {"start": v(61.47, -6.84) * mm, "end": v(61.48, -6.84) * mm});
            skLineSegment(sketch, "E260", {"start": v(61.48, -6.84) * mm, "end": v(61.48, -6.83) * mm});
            skLineSegment(sketch, "E261", {"start": v(61.48, -6.83) * mm, "end": v(61.49, -6.83) * mm});
            skLineSegment(sketch, "E262", {"start": v(61.49, -6.83) * mm, "end": v(61.5, -6.82) * mm});
            skLineSegment(sketch, "E263", {"start": v(61.5, -6.82) * mm, "end": v(61.5, -6.82) * mm});
            skLineSegment(sketch, "E264", {"start": v(61.5, -6.82) * mm, "end": v(61.51, -6.82) * mm});
            skLineSegment(sketch, "E265", {"start": v(61.51, -6.82) * mm, "end": v(61.52, -6.81) * mm});
            skLineSegment(sketch, "E266", {"start": v(61.52, -6.81) * mm, "end": v(61.53, -6.81) * mm});
            skLineSegment(sketch, "E267", {"start": v(61.53, -6.81) * mm, "end": v(61.54, -6.8) * mm});
            skLineSegment(sketch, "E268", {"start": v(61.54, -6.8) * mm, "end": v(61.56, -6.8) * mm});
            skLineSegment(sketch, "E269", {"start": v(61.56, -6.8) * mm, "end": v(61.58, -6.81) * mm});
            skLineSegment(sketch, "E270", {"start": v(61.58, -6.81) * mm, "end": v(61.6, -6.76) * mm});
            skLineSegment(sketch, "E271", {"start": v(61.6, -6.76) * mm, "end": v(61.61, -6.7) * mm});
            skLineSegment(sketch, "E272", {"start": v(61.61, -6.7) * mm, "end": v(61.64, -6.67) * mm});
            skLineSegment(sketch, "E273", {"start": v(61.64, -6.67) * mm, "end": v(61.66, -6.63) * mm});
            skLineSegment(sketch, "E274", {"start": v(61.66, -6.63) * mm, "end": v(61.7, -6.58) * mm});
            skLineSegment(sketch, "E275", {"start": v(61.7, -6.58) * mm, "end": v(61.93, -6.36) * mm});
            skLineSegment(sketch, "E276", {"start": v(61.93, -6.36) * mm, "end": v(61.95, -6.32) * mm});
            skLineSegment(sketch, "E277", {"start": v(61.95, -6.32) * mm, "end": v(61.98, -6.28) * mm});
            skLineSegment(sketch, "E278", {"start": v(61.98, -6.28) * mm, "end": v(62, -6.23) * mm});
            skLineSegment(sketch, "E279", {"start": v(62, -6.23) * mm, "end": v(62, -6.2) * mm});
            skLineSegment(sketch, "E280", {"start": v(62, -6.2) * mm, "end": v(62.01, -6.14) * mm});
            skLineSegment(sketch, "E281", {"start": v(62.01, -6.14) * mm, "end": v(62.2, -6.14) * mm});
            skLineSegment(sketch, "E282", {"start": v(62.2, -6.14) * mm, "end": v(62.2, -6) * mm});
            skLineSegment(sketch, "E283", {"start": v(62.2, -6) * mm, "end": v(62.23, -5.75) * mm});
            skLineSegment(sketch, "E284", {"start": v(62.23, -5.75) * mm, "end": v(62.27, -5.43) * mm});
            skLineSegment(sketch, "E285", {"start": v(62.27, -5.43) * mm, "end": v(62.27, -5.3) * mm});
            skLineSegment(sketch, "E286", {"start": v(62.27, -5.3) * mm, "end": v(62.26, -5.15) * mm});
            skLineSegment(sketch, "E287", {"start": v(62.26, -5.15) * mm, "end": v(62.3, -5.11) * mm});
            skLineSegment(sketch, "E288", {"start": v(62.3, -5.11) * mm, "end": v(62.34, -5.07) * mm});
            skLineSegment(sketch, "E289", {"start": v(62.34, -5.07) * mm, "end": v(62.41, -5.01) * mm});
            skLineSegment(sketch, "E290", {"start": v(62.41, -5.01) * mm, "end": v(62.65, -4.84) * mm});
            skLineSegment(sketch, "E291", {"start": v(62.65, -4.84) * mm, "end": v(62.7, -4.8) * mm});
            skLineSegment(sketch, "E292", {"start": v(62.7, -4.8) * mm, "end": v(62.72, -4.77) * mm});
            skLineSegment(sketch, "E293", {"start": v(62.72, -4.77) * mm, "end": v(62.75, -4.72) * mm});
            skLineSegment(sketch, "E294", {"start": v(62.75, -4.72) * mm, "end": v(62.75, -4.7) * mm});
            skLineSegment(sketch, "E295", {"start": v(62.75, -4.7) * mm, "end": v(62.74, -4.66) * mm});
            skLineSegment(sketch, "E296", {"start": v(62.74, -4.66) * mm, "end": v(62.73, -4.62) * mm});
            skLineSegment(sketch, "E297", {"start": v(62.73, -4.62) * mm, "end": v(62.71, -4.56) * mm});
            skLineSegment(sketch, "E298", {"start": v(62.71, -4.56) * mm, "end": v(62.58, -4.25) * mm});
            skLineSegment(sketch, "E299", {"start": v(62.58, -4.25) * mm, "end": v(62.57, -4.22) * mm});
            skLineSegment(sketch, "E300", {"start": v(62.57, -4.22) * mm, "end": v(62.57, -4.17) * mm});
            skLineSegment(sketch, "E301", {"start": v(62.57, -4.17) * mm, "end": v(62.56, -4.05) * mm});
            skLineSegment(sketch, "E302", {"start": v(62.56, -4.05) * mm, "end": v(62.56, -3.94) * mm});
            skLineSegment(sketch, "E303", {"start": v(62.56, -3.94) * mm, "end": v(62.58, -3.83) * mm});
            skLineSegment(sketch, "E304", {"start": v(62.58, -3.83) * mm, "end": v(62.6, -3.74) * mm});
            skLineSegment(sketch, "E305", {"start": v(62.6, -3.74) * mm, "end": v(62.64, -3.62) * mm});
            skLineSegment(sketch, "E306", {"start": v(62.64, -3.62) * mm, "end": v(62.7, -3.5) * mm});
            skLineSegment(sketch, "E307", {"start": v(62.7, -3.5) * mm, "end": v(62.82, -3.3) * mm});
            skLineSegment(sketch, "E308", {"start": v(62.82, -3.3) * mm, "end": v(62.93, -3.13) * mm});
            skLineSegment(sketch, "E309", {"start": v(62.93, -3.13) * mm, "end": v(63.13, -2.75) * mm});
            skLineSegment(sketch, "E310", {"start": v(63.13, -2.75) * mm, "end": v(63.23, -2.5) * mm});
            skLineSegment(sketch, "E311", {"start": v(63.23, -2.5) * mm, "end": v(63.27, -2.39) * mm});
            skLineSegment(sketch, "E312", {"start": v(63.27, -2.39) * mm, "end": v(63.3, -2.27) * mm});
            skLineSegment(sketch, "E313", {"start": v(63.3, -2.27) * mm, "end": v(63.32, -2.17) * mm});
            skLineSegment(sketch, "E314", {"start": v(63.32, -2.17) * mm, "end": v(63.33, -2.01) * mm});
            skLineSegment(sketch, "E315", {"start": v(63.33, -2.01) * mm, "end": v(63.34, -1.63) * mm});
            skLineSegment(sketch, "E316", {"start": v(63.34, -1.63) * mm, "end": v(63.35, -1.58) * mm});
            skLineSegment(sketch, "E317", {"start": v(63.35, -1.58) * mm, "end": v(63.35, -1.56) * mm});
            skLineSegment(sketch, "E318", {"start": v(63.35, -1.56) * mm, "end": v(63.36, -1.53) * mm});
            skLineSegment(sketch, "E319", {"start": v(63.36, -1.53) * mm, "end": v(63.39, -1.48) * mm});
            skLineSegment(sketch, "E320", {"start": v(63.39, -1.48) * mm, "end": v(63.43, -1.4) * mm});
            skLineSegment(sketch, "E321", {"start": v(63.43, -1.4) * mm, "end": v(63.48, -1.34) * mm});
            skLineSegment(sketch, "E322", {"start": v(63.48, -1.34) * mm, "end": v(63.54, -1.27) * mm});
            skLineSegment(sketch, "E323", {"start": v(63.54, -1.27) * mm, "end": v(63.62, -1.2) * mm});
            skLineSegment(sketch, "E324", {"start": v(63.62, -1.2) * mm, "end": v(63.72, -1.12) * mm});
            skLineSegment(sketch, "E325", {"start": v(63.72, -1.12) * mm, "end": v(63.83, -1.04) * mm});
            skLineSegment(sketch, "E326", {"start": v(63.83, -1.04) * mm, "end": v(63.97, -0.97) * mm});
            skLineSegment(sketch, "E327", {"start": v(63.97, -0.97) * mm, "end": v(64.1, -0.92) * mm});
            skLineSegment(sketch, "E328", {"start": v(64.1, -0.92) * mm, "end": v(64.15, -0.93) * mm});
            skLineSegment(sketch, "E329", {"start": v(64.15, -0.93) * mm, "end": v(64.19, -0.95) * mm});
            skLineSegment(sketch, "E330", {"start": v(64.19, -0.95) * mm, "end": v(64.22, -0.98) * mm});
            skLineSegment(sketch, "E331", {"start": v(64.22, -0.98) * mm, "end": v(64.26, -1) * mm});
            skLineSegment(sketch, "E332", {"start": v(64.26, -1) * mm, "end": v(64.29, -1.04) * mm});
            skLineSegment(sketch, "E333", {"start": v(64.29, -1.04) * mm, "end": v(64.32, -1.1) * mm});
            skLineSegment(sketch, "E334", {"start": v(64.32, -1.1) * mm, "end": v(64.36, -1.16) * mm});
            skLineSegment(sketch, "E335", {"start": v(64.36, -1.16) * mm, "end": v(64.43, -1.3) * mm});
            skLineSegment(sketch, "E336", {"start": v(64.43, -1.3) * mm, "end": v(64.48, -1.42) * mm});
            skLineSegment(sketch, "E337", {"start": v(64.48, -1.42) * mm, "end": v(64.53, -1.53) * mm});
            skLineSegment(sketch, "E338", {"start": v(64.53, -1.53) * mm, "end": v(64.55, -1.46) * mm});
            skLineSegment(sketch, "E339", {"start": v(64.55, -1.46) * mm, "end": v(64.58, -1.34) * mm});
            skLineSegment(sketch, "E340", {"start": v(64.58, -1.34) * mm, "end": v(64.65, -0.95) * mm});
            skLineSegment(sketch, "E341", {"start": v(64.65, -0.95) * mm, "end": v(64.67, -0.88) * mm});
            skLineSegment(sketch, "E342", {"start": v(64.67, -0.88) * mm, "end": v(64.69, -0.84) * mm});
            skLineSegment(sketch, "E343", {"start": v(64.69, -0.84) * mm, "end": v(64.72, -0.8) * mm});
            skLineSegment(sketch, "E344", {"start": v(64.72, -0.8) * mm, "end": v(65.15, -0.8) * mm});
            skLineSegment(sketch, "E345", {"start": v(65.15, -0.8) * mm, "end": v(65.27, -0.91) * mm});
            skLineSegment(sketch, "E346", {"start": v(65.27, -0.91) * mm, "end": v(65.6, -1.23) * mm});
            skLineSegment(sketch, "E347", {"start": v(65.6, -1.23) * mm, "end": v(65.65, -1.28) * mm});
            skLineSegment(sketch, "E348", {"start": v(65.65, -1.28) * mm, "end": v(65.7, -1.34) * mm});
            skLineSegment(sketch, "E349", {"start": v(65.7, -1.34) * mm, "end": v(65.75, -1.35) * mm});
            skLineSegment(sketch, "E350", {"start": v(65.75, -1.35) * mm, "end": v(66.13, -1.41) * mm});
            skLineSegment(sketch, "E351", {"start": v(66.13, -1.41) * mm, "end": v(66.19, -1.41) * mm});
            skLineSegment(sketch, "E352", {"start": v(66.19, -1.41) * mm, "end": v(66.23, -1.4) * mm});
            skLineSegment(sketch, "E353", {"start": v(66.23, -1.4) * mm, "end": v(66.26, -1.4) * mm});
            skLineSegment(sketch, "E354", {"start": v(66.26, -1.4) * mm, "end": v(66.28, -1.4) * mm});
            skLineSegment(sketch, "E355", {"start": v(66.28, -1.4) * mm, "end": v(66.3, -1.38) * mm});
            skLineSegment(sketch, "E356", {"start": v(66.3, -1.38) * mm, "end": v(66.32, -1.36) * mm});
            skLineSegment(sketch, "E357", {"start": v(66.32, -1.36) * mm, "end": v(66.34, -1.35) * mm});
            skLineSegment(sketch, "E358", {"start": v(66.34, -1.35) * mm, "end": v(66.36, -1.32) * mm});
            skLineSegment(sketch, "E359", {"start": v(66.36, -1.32) * mm, "end": v(66.36, -1.31) * mm});
            skLineSegment(sketch, "E360", {"start": v(66.36, -1.31) * mm, "end": v(66.37, -1.28) * mm});
            skLineSegment(sketch, "E361", {"start": v(66.37, -1.28) * mm, "end": v(66.23, -1.28) * mm});
            skLineSegment(sketch, "E362", {"start": v(66.23, -1.28) * mm, "end": v(66.14, -1.27) * mm});
            skLineSegment(sketch, "E363", {"start": v(66.14, -1.27) * mm, "end": v(66.08, -1.26) * mm});
            skLineSegment(sketch, "E364", {"start": v(66.08, -1.26) * mm, "end": v(66.03, -1.24) * mm});
            skLineSegment(sketch, "E365", {"start": v(66.03, -1.24) * mm, "end": v(65.99, -1.23) * mm});
            skLineSegment(sketch, "E366", {"start": v(65.99, -1.23) * mm, "end": v(65.95, -1.2) * mm});
            skLineSegment(sketch, "E367", {"start": v(65.95, -1.2) * mm, "end": v(65.93, -1.2) * mm});
            skLineSegment(sketch, "E368", {"start": v(65.93, -1.2) * mm, "end": v(65.91, -1.17) * mm});
            skLineSegment(sketch, "E369", {"start": v(65.91, -1.17) * mm, "end": v(65.9, -1.16) * mm});
            skLineSegment(sketch, "E370", {"start": v(65.9, -1.16) * mm, "end": v(65.88, -1.14) * mm});
            skLineSegment(sketch, "E371", {"start": v(65.88, -1.14) * mm, "end": v(65.86, -1.11) * mm});
            skLineSegment(sketch, "E372", {"start": v(65.86, -1.11) * mm, "end": v(65.85, -1.09) * mm});
            skLineSegment(sketch, "E373", {"start": v(65.85, -1.09) * mm, "end": v(65.84, -1.06) * mm});
            skLineSegment(sketch, "E374", {"start": v(65.84, -1.06) * mm, "end": v(65.83, -1.03) * mm});
            skLineSegment(sketch, "E375", {"start": v(65.83, -1.03) * mm, "end": v(65.82, -0.99) * mm});
            skLineSegment(sketch, "E376", {"start": v(65.82, -0.99) * mm, "end": v(65.82, -0.95) * mm});
            skLineSegment(sketch, "E377", {"start": v(65.82, -0.95) * mm, "end": v(65.82, -0.92) * mm});
            skLineSegment(sketch, "E378", {"start": v(65.82, -0.92) * mm, "end": v(65.88, -0.92) * mm});
            skLineSegment(sketch, "E379", {"start": v(65.88, -0.92) * mm, "end": v(65.93, -0.93) * mm});
            skLineSegment(sketch, "E380", {"start": v(65.93, -0.93) * mm, "end": v(66, -0.95) * mm});
            skLineSegment(sketch, "E381", {"start": v(66, -0.95) * mm, "end": v(66.05, -0.98) * mm});
            skLineSegment(sketch, "E382", {"start": v(66.05, -0.98) * mm, "end": v(66.13, -1.02) * mm});
            skLineSegment(sketch, "E383", {"start": v(66.13, -1.02) * mm, "end": v(66.35, -1.16) * mm});
            skLineSegment(sketch, "E384", {"start": v(66.35, -1.16) * mm, "end": v(66.4, -1.19) * mm});
            skLineSegment(sketch, "E385", {"start": v(66.4, -1.19) * mm, "end": v(66.47, -1.2) * mm});
            skLineSegment(sketch, "E386", {"start": v(66.47, -1.2) * mm, "end": v(66.5, -1.21) * mm});
            skLineSegment(sketch, "E387", {"start": v(66.5, -1.21) * mm, "end": v(66.56, -1.22) * mm});
            skLineSegment(sketch, "E388", {"start": v(66.56, -1.22) * mm, "end": v(66.57, -1.22) * mm});
            skLineSegment(sketch, "E389", {"start": v(66.57, -1.22) * mm, "end": v(66.57, -1.22) * mm});
            skLineSegment(sketch, "E390", {"start": v(66.57, -1.22) * mm, "end": v(66.58, -1.22) * mm});
            skLineSegment(sketch, "E391", {"start": v(66.58, -1.22) * mm, "end": v(66.58, -1.21) * mm});
            skLineSegment(sketch, "E392", {"start": v(66.58, -1.21) * mm, "end": v(66.59, -1.21) * mm});
            skLineSegment(sketch, "E393", {"start": v(66.59, -1.21) * mm, "end": v(66.6, -1.2) * mm});
            skLineSegment(sketch, "E394", {"start": v(66.6, -1.2) * mm, "end": v(66.6, -1.2) * mm});
            skLineSegment(sketch, "E395", {"start": v(66.6, -1.2) * mm, "end": v(66.6, -1.19) * mm});
            skLineSegment(sketch, "E396", {"start": v(66.6, -1.19) * mm, "end": v(66.61, -1.18) * mm});
            skLineSegment(sketch, "E397", {"start": v(66.61, -1.18) * mm, "end": v(66.62, -1.16) * mm});
            skLineSegment(sketch, "E398", {"start": v(66.62, -1.16) * mm, "end": v(66.62, -1.14) * mm});
            skLineSegment(sketch, "E399", {"start": v(66.62, -1.14) * mm, "end": v(66.64, -1.03) * mm});
            skLineSegment(sketch, "E400", {"start": v(66.64, -1.03) * mm, "end": v(66.65, -1.02) * mm});
            skLineSegment(sketch, "E401", {"start": v(66.65, -1.02) * mm, "end": v(66.65, -1) * mm});
            skLineSegment(sketch, "E402", {"start": v(66.65, -1) * mm, "end": v(66.66, -1) * mm});
            skLineSegment(sketch, "E403", {"start": v(66.66, -1) * mm, "end": v(66.67, -1) * mm});
            skLineSegment(sketch, "E404", {"start": v(66.67, -1) * mm, "end": v(66.67, -1) * mm});
            skLineSegment(sketch, "E405", {"start": v(66.67, -1) * mm, "end": v(66.67, -0.99) * mm});
            skLineSegment(sketch, "E406", {"start": v(66.67, -0.99) * mm, "end": v(66.68, -0.98) * mm});
            skLineSegment(sketch, "E407", {"start": v(66.68, -0.98) * mm, "end": v(66.69, -0.98) * mm});
            skLineSegment(sketch, "E408", {"start": v(66.69, -0.98) * mm, "end": v(66.7, -0.98) * mm});
            skLineSegment(sketch, "E409", {"start": v(66.7, -0.98) * mm, "end": v(66.7, -0.98) * mm});
            skLineSegment(sketch, "E410", {"start": v(66.7, -0.98) * mm, "end": v(66.71, -0.97) * mm});
            skLineSegment(sketch, "E411", {"start": v(66.71, -0.97) * mm, "end": v(66.72, -0.97) * mm});
            skLineSegment(sketch, "E412", {"start": v(66.72, -0.97) * mm, "end": v(66.74, -0.98) * mm});
            skLineSegment(sketch, "E413", {"start": v(66.74, -0.98) * mm, "end": v(67.42, -0.55) * mm});
            skLineSegment(sketch, "E414", {"start": v(67.42, -0.55) * mm, "end": v(67.84, -0.31) * mm});
            skLineSegment(sketch, "E415", {"start": v(67.84, -0.31) * mm, "end": v(67.89, -0.27) * mm});
            skLineSegment(sketch, "E416", {"start": v(67.89, -0.27) * mm, "end": v(67.93, -0.23) * mm});
            skLineSegment(sketch, "E417", {"start": v(67.93, -0.23) * mm, "end": v(67.96, -0.19) * mm});
            skLineSegment(sketch, "E418", {"start": v(67.96, -0.19) * mm, "end": v(67.98, -0.15) * mm});
            skLineSegment(sketch, "E419", {"start": v(67.98, -0.15) * mm, "end": v(68, -0.1) * mm});
            skLineSegment(sketch, "E420", {"start": v(68, -0.1) * mm, "end": v(68.02, -0.07) * mm});
            skLineSegment(sketch, "E421", {"start": v(68.02, -0.07) * mm, "end": v(68.03, -0.03) * mm});
            skLineSegment(sketch, "E422", {"start": v(68.03, -0.03) * mm, "end": v(68.03, 0) * mm});
            skLineSegment(sketch, "E423", {"start": v(68.03, 0) * mm, "end": v(67.98, 0.03) * mm});
            skLineSegment(sketch, "E424", {"start": v(67.98, 0.03) * mm, "end": v(67.92, 0.05) * mm});
            skLineSegment(sketch, "E425", {"start": v(67.92, 0.05) * mm, "end": v(67.86, 0.07) * mm});
            skLineSegment(sketch, "E426", {"start": v(67.86, 0.07) * mm, "end": v(67.76, 0.08) * mm});
            skLineSegment(sketch, "E427", {"start": v(67.76, 0.08) * mm, "end": v(67.62, 0.08) * mm});
            skLineSegment(sketch, "E428", {"start": v(67.62, 0.08) * mm, "end": v(67.38, 0.05) * mm});
            skLineSegment(sketch, "E429", {"start": v(67.38, 0.05) * mm, "end": v(66.89, 0) * mm});
            skLineSegment(sketch, "E430", {"start": v(66.89, 0) * mm, "end": v(66.76, 0) * mm});
            skLineSegment(sketch, "E431", {"start": v(66.76, 0) * mm, "end": v(66.67, 0.01) * mm});
            skLineSegment(sketch, "E432", {"start": v(66.67, 0.01) * mm, "end": v(66.6, 0.03) * mm});
            skLineSegment(sketch, "E433", {"start": v(66.6, 0.03) * mm, "end": v(66.56, 0.05) * mm});
            skLineSegment(sketch, "E434", {"start": v(66.56, 0.05) * mm, "end": v(66.5, 0.08) * mm});
            skLineSegment(sketch, "E435", {"start": v(66.5, 0.08) * mm, "end": v(66.48, 0.1) * mm});
            skLineSegment(sketch, "E436", {"start": v(66.48, 0.1) * mm, "end": v(66.43, 0.13) * mm});
            skLineSegment(sketch, "E437", {"start": v(66.43, 0.13) * mm, "end": v(66.46, 0.16) * mm});
            skLineSegment(sketch, "E438", {"start": v(66.46, 0.16) * mm, "end": v(66.48, 0.2) * mm});
            skLineSegment(sketch, "E439", {"start": v(66.48, 0.2) * mm, "end": v(66.52, 0.23) * mm});
            skLineSegment(sketch, "E440", {"start": v(66.52, 0.23) * mm, "end": v(66.57, 0.27) * mm});
            skLineSegment(sketch, "E441", {"start": v(66.57, 0.27) * mm, "end": v(66.84, 0.46) * mm});
            skLineSegment(sketch, "E442", {"start": v(66.84, 0.46) * mm, "end": v(66.88, 0.5) * mm});
            skLineSegment(sketch, "E443", {"start": v(66.88, 0.5) * mm, "end": v(66.9, 0.53) * mm});
            skLineSegment(sketch, "E444", {"start": v(66.9, 0.53) * mm, "end": v(66.93, 0.56) * mm});
            skLineSegment(sketch, "E445", {"start": v(66.93, 0.56) * mm, "end": v(66.63, 0.52) * mm});
            skLineSegment(sketch, "E446", {"start": v(66.63, 0.52) * mm, "end": v(66.3, 0.51) * mm});
            skLineSegment(sketch, "E447", {"start": v(66.3, 0.51) * mm, "end": v(64.9, 0.57) * mm});
            skLineSegment(sketch, "E448", {"start": v(64.9, 0.57) * mm, "end": v(64.72, 0.55) * mm});
            skLineSegment(sketch, "E449", {"start": v(64.72, 0.55) * mm, "end": v(64.6, 0.52) * mm});
            skLineSegment(sketch, "E450", {"start": v(64.6, 0.52) * mm, "end": v(64.52, 0.5) * mm});
            skLineSegment(sketch, "E451", {"start": v(64.52, 0.5) * mm, "end": v(64.4, 0.44) * mm});
            skLineSegment(sketch, "E452", {"start": v(64.4, 0.44) * mm, "end": v(64.29, 0.36) * mm});
            skLineSegment(sketch, "E453", {"start": v(64.29, 0.36) * mm, "end": v(64.15, 0.25) * mm});
            skLineSegment(sketch, "E454", {"start": v(64.15, 0.25) * mm, "end": v(63.53, -0.32) * mm});
            skLineSegment(sketch, "E455", {"start": v(63.53, -0.32) * mm, "end": v(63.46, -0.37) * mm});
            skLineSegment(sketch, "E456", {"start": v(63.46, -0.37) * mm, "end": v(63.36, -0.42) * mm});
            skLineSegment(sketch, "E457", {"start": v(63.36, -0.42) * mm, "end": v(63.3, -0.28) * mm});
            skLineSegment(sketch, "E458", {"start": v(63.3, -0.28) * mm, "end": v(63.24, -0.16) * mm});
            skLineSegment(sketch, "E459", {"start": v(63.24, -0.16) * mm, "end": v(63.16, -0.04) * mm});
            skLineSegment(sketch, "E460", {"start": v(63.16, -0.04) * mm, "end": v(63.06, 0.06) * mm});
            skLineSegment(sketch, "E461", {"start": v(63.06, 0.06) * mm, "end": v(62.91, 0.2) * mm});
            skLineSegment(sketch, "E462", {"start": v(62.91, 0.2) * mm, "end": v(62.74, 0.33) * mm});
            skLineSegment(sketch, "E463", {"start": v(62.74, 0.33) * mm, "end": v(62.43, 0.51) * mm});
            skLineSegment(sketch, "E464", {"start": v(62.43, 0.51) * mm, "end": v(61.54, 1) * mm});
            skLineSegment(sketch, "E465", {"start": v(61.54, 1) * mm, "end": v(61.37, 1.12) * mm});
            skLineSegment(sketch, "E466", {"start": v(61.37, 1.12) * mm, "end": v(61.21, 1.26) * mm});
            skLineSegment(sketch, "E467", {"start": v(61.21, 1.26) * mm, "end": v(61.12, 1.36) * mm});
            skLineSegment(sketch, "E468", {"start": v(61.12, 1.36) * mm, "end": v(61.04, 1.48) * mm});
            skLineSegment(sketch, "E469", {"start": v(61.04, 1.48) * mm, "end": v(60.97, 1.6) * mm});
            skLineSegment(sketch, "E470", {"start": v(60.97, 1.6) * mm, "end": v(60.9, 1.74) * mm});
            skLineSegment(sketch, "E471", {"start": v(60.9, 1.74) * mm, "end": v(60.88, 1.81) * mm});
            skLineSegment(sketch, "E472", {"start": v(60.88, 1.81) * mm, "end": v(60.85, 1.97) * mm});
            skLineSegment(sketch, "E473", {"start": v(60.85, 1.97) * mm, "end": v(60.89, 2.05) * mm});
            skLineSegment(sketch, "E474", {"start": v(60.89, 2.05) * mm, "end": v(60.9, 2.08) * mm});
            skLineSegment(sketch, "E475", {"start": v(60.9, 2.08) * mm, "end": v(60.93, 2.1) * mm});
            skLineSegment(sketch, "E476", {"start": v(60.93, 2.1) * mm, "end": v(60.94, 2.11) * mm});
            skLineSegment(sketch, "E477", {"start": v(60.94, 2.11) * mm, "end": v(60.96, 2.12) * mm});
            skLineSegment(sketch, "E478", {"start": v(60.96, 2.12) * mm, "end": v(60.98, 2.13) * mm});
            skLineSegment(sketch, "E479", {"start": v(60.98, 2.13) * mm, "end": v(61, 2.14) * mm});
            skLineSegment(sketch, "E480", {"start": v(61, 2.14) * mm, "end": v(61.02, 2.15) * mm});
            skLineSegment(sketch, "E481", {"start": v(61.02, 2.15) * mm, "end": v(61.04, 2.16) * mm});
            skLineSegment(sketch, "E482", {"start": v(61.04, 2.16) * mm, "end": v(61.07, 2.16) * mm});
            skLineSegment(sketch, "E483", {"start": v(61.07, 2.16) * mm, "end": v(61.1, 2.16) * mm});
            skLineSegment(sketch, "E484", {"start": v(61.1, 2.16) * mm, "end": v(61.12, 2.16) * mm});
            skLineSegment(sketch, "E485", {"start": v(61.12, 2.16) * mm, "end": v(61.15, 2.16) * mm});
            skLineSegment(sketch, "E486", {"start": v(61.15, 2.16) * mm, "end": v(61.16, 2.17) * mm});
            skLineSegment(sketch, "E487", {"start": v(61.16, 2.17) * mm, "end": v(61.17, 2.2) * mm});
            skLineSegment(sketch, "E488", {"start": v(61.17, 2.2) * mm, "end": v(61.17, 2.21) * mm});
            skLineSegment(sketch, "E489", {"start": v(61.17, 2.21) * mm, "end": v(61.17, 2.23) * mm});
            skLineSegment(sketch, "E490", {"start": v(61.17, 2.23) * mm, "end": v(61.17, 2.25) * mm});
            skLineSegment(sketch, "E491", {"start": v(61.17, 2.25) * mm, "end": v(61.17, 2.27) * mm});
            skLineSegment(sketch, "E492", {"start": v(61.17, 2.27) * mm, "end": v(61.16, 2.3) * mm});
            skLineSegment(sketch, "E493", {"start": v(61.16, 2.3) * mm, "end": v(61.15, 2.33) * mm});
            skLineSegment(sketch, "E494", {"start": v(61.15, 2.33) * mm, "end": v(61.1, 2.42) * mm});
            skLineSegment(sketch, "E495", {"start": v(61.1, 2.42) * mm, "end": v(61.1, 2.43) * mm});
            skLineSegment(sketch, "E496", {"start": v(61.1, 2.43) * mm, "end": v(61.1, 2.43) * mm});
            skLineSegment(sketch, "E497", {"start": v(61.1, 2.43) * mm, "end": v(61.1, 2.44) * mm});
            skLineSegment(sketch, "E498", {"start": v(61.1, 2.44) * mm, "end": v(61.1, 2.44) * mm});
            skLineSegment(sketch, "E499", {"start": v(61.1, 2.44) * mm, "end": v(61.1, 2.45) * mm});
            skLineSegment(sketch, "E500", {"start": v(61.1, 2.45) * mm, "end": v(61.11, 2.45) * mm});
            skLineSegment(sketch, "E501", {"start": v(61.11, 2.45) * mm, "end": v(61.11, 2.45) * mm});
            skLineSegment(sketch, "E502", {"start": v(61.11, 2.45) * mm, "end": v(61.12, 2.45) * mm});
            skLineSegment(sketch, "E503", {"start": v(61.12, 2.45) * mm, "end": v(61.12, 2.46) * mm});
            skLineSegment(sketch, "E504", {"start": v(61.12, 2.46) * mm, "end": v(61.13, 2.46) * mm});
            skLineSegment(sketch, "E505", {"start": v(61.13, 2.46) * mm, "end": v(61.13, 2.46) * mm});
            skLineSegment(sketch, "E506", {"start": v(61.13, 2.46) * mm, "end": v(61.14, 2.46) * mm});
            skLineSegment(sketch, "E507", {"start": v(61.14, 2.46) * mm, "end": v(61.15, 2.46) * mm});
            skLineSegment(sketch, "E508", {"start": v(61.15, 2.46) * mm, "end": v(61.17, 2.46) * mm});
            skLineSegment(sketch, "E509", {"start": v(61.17, 2.46) * mm, "end": v(61.2, 2.46) * mm});
            skLineSegment(sketch, "E510", {"start": v(61.2, 2.46) * mm, "end": v(61.2, 2.46) * mm});
            skLineSegment(sketch, "E511", {"start": v(61.2, 2.46) * mm, "end": v(61.22, 2.46) * mm});
            skLineSegment(sketch, "E512", {"start": v(61.22, 2.46) * mm, "end": v(61.24, 2.45) * mm});
            skLineSegment(sketch, "E513", {"start": v(61.24, 2.45) * mm, "end": v(61.26, 2.44) * mm});
            skLineSegment(sketch, "E514", {"start": v(61.26, 2.44) * mm, "end": v(61.32, 2.41) * mm});
            skLineSegment(sketch, "E515", {"start": v(61.32, 2.41) * mm, "end": v(61.34, 2.4) * mm});
            skLineSegment(sketch, "E516", {"start": v(61.34, 2.4) * mm, "end": v(61.36, 2.4) * mm});
            skLineSegment(sketch, "E517", {"start": v(61.36, 2.4) * mm, "end": v(61.37, 2.4) * mm});
            skLineSegment(sketch, "E518", {"start": v(61.37, 2.4) * mm, "end": v(61.39, 2.4) * mm});
            skLineSegment(sketch, "E519", {"start": v(61.39, 2.4) * mm, "end": v(61.4, 2.4) * mm});
            skLineSegment(sketch, "E520", {"start": v(61.4, 2.4) * mm, "end": v(61.47, 2.66) * mm});
            skLineSegment(sketch, "E521", {"start": v(61.47, 2.66) * mm, "end": v(61.49, 2.7) * mm});
            skLineSegment(sketch, "E522", {"start": v(61.49, 2.7) * mm, "end": v(61.5, 2.73) * mm});
            skLineSegment(sketch, "E523", {"start": v(61.5, 2.73) * mm, "end": v(61.52, 2.75) * mm});
            skLineSegment(sketch, "E524", {"start": v(61.52, 2.75) * mm, "end": v(61.53, 2.77) * mm});
            skLineSegment(sketch, "E525", {"start": v(61.53, 2.77) * mm, "end": v(61.55, 2.78) * mm});
            skLineSegment(sketch, "E526", {"start": v(61.55, 2.78) * mm, "end": v(61.57, 2.8) * mm});
            skLineSegment(sketch, "E527", {"start": v(61.57, 2.8) * mm, "end": v(61.59, 2.8) * mm});
            skLineSegment(sketch, "E528", {"start": v(61.59, 2.8) * mm, "end": v(61.6, 2.81) * mm});
            skLineSegment(sketch, "E529", {"start": v(61.6, 2.81) * mm, "end": v(61.63, 2.82) * mm});
            skLineSegment(sketch, "E530", {"start": v(61.63, 2.82) * mm, "end": v(61.65, 2.83) * mm});
            skLineSegment(sketch, "E531", {"start": v(61.65, 2.83) * mm, "end": v(61.68, 2.83) * mm});
            skLineSegment(sketch, "E532", {"start": v(61.68, 2.83) * mm, "end": v(61.7, 2.83) * mm});
            skLineSegment(sketch, "E533", {"start": v(61.7, 2.83) * mm, "end": v(61.67, 2.97) * mm});
            skLineSegment(sketch, "E534", {"start": v(61.67, 2.97) * mm, "end": v(61.67, 2.98) * mm});
            skLineSegment(sketch, "E535", {"start": v(61.67, 2.98) * mm, "end": v(61.67, 3) * mm});
            skLineSegment(sketch, "E536", {"start": v(61.67, 3) * mm, "end": v(61.68, 3.05) * mm});
            skLineSegment(sketch, "E537", {"start": v(61.68, 3.05) * mm, "end": v(61.7, 3.14) * mm});
            skLineSegment(sketch, "E538", {"start": v(61.7, 3.14) * mm, "end": v(61.73, 3.14) * mm});
            skLineSegment(sketch, "E539", {"start": v(61.73, 3.14) * mm, "end": v(61.74, 3.14) * mm});
            skLineSegment(sketch, "E540", {"start": v(61.74, 3.14) * mm, "end": v(61.76, 3.14) * mm});
            skLineSegment(sketch, "E541", {"start": v(61.76, 3.14) * mm, "end": v(61.78, 3.13) * mm});
            skLineSegment(sketch, "E542", {"start": v(61.78, 3.13) * mm, "end": v(61.8, 3.13) * mm});
            skLineSegment(sketch, "E543", {"start": v(61.8, 3.13) * mm, "end": v(61.81, 3.12) * mm});
            skLineSegment(sketch, "E544", {"start": v(61.81, 3.12) * mm, "end": v(61.88, 3.09) * mm});
            skLineSegment(sketch, "E545", {"start": v(61.88, 3.09) * mm, "end": v(61.9, 3.08) * mm});
            skLineSegment(sketch, "E546", {"start": v(61.9, 3.08) * mm, "end": v(61.9, 3.08) * mm});
            skLineSegment(sketch, "E547", {"start": v(61.9, 3.08) * mm, "end": v(61.93, 3.08) * mm});
            skLineSegment(sketch, "E548", {"start": v(61.93, 3.08) * mm, "end": v(61.94, 3.08) * mm});
            skLineSegment(sketch, "E549", {"start": v(61.94, 3.08) * mm, "end": v(61.95, 3.08) * mm});
            skLineSegment(sketch, "E550", {"start": v(61.95, 3.08) * mm, "end": v(61.96, 3.14) * mm});
            skLineSegment(sketch, "E551", {"start": v(61.96, 3.14) * mm, "end": v(61.97, 3.2) * mm});
            skLineSegment(sketch, "E552", {"start": v(61.97, 3.2) * mm, "end": v(61.97, 3.25) * mm});
            skLineSegment(sketch, "E553", {"start": v(61.97, 3.25) * mm, "end": v(61.96, 3.3) * mm});
            skLineSegment(sketch, "E554", {"start": v(61.96, 3.3) * mm, "end": v(61.94, 3.36) * mm});
            skLineSegment(sketch, "E555", {"start": v(61.94, 3.36) * mm, "end": v(61.9, 3.47) * mm});
            skLineSegment(sketch, "E556", {"start": v(61.9, 3.47) * mm, "end": v(61.86, 3.6) * mm});
            skLineSegment(sketch, "E557", {"start": v(61.86, 3.6) * mm, "end": v(61.85, 3.64) * mm});
            skLineSegment(sketch, "E558", {"start": v(61.85, 3.64) * mm, "end": v(61.85, 3.68) * mm});
            skLineSegment(sketch, "E559", {"start": v(61.85, 3.68) * mm, "end": v(61.85, 3.7) * mm});
            skLineSegment(sketch, "E560", {"start": v(61.85, 3.7) * mm, "end": v(61.85, 3.73) * mm});
            skLineSegment(sketch, "E561", {"start": v(61.85, 3.73) * mm, "end": v(61.86, 3.75) * mm});
            skLineSegment(sketch, "E562", {"start": v(61.86, 3.75) * mm, "end": v(61.87, 3.78) * mm});
            skLineSegment(sketch, "E563", {"start": v(61.87, 3.78) * mm, "end": v(61.87, 3.79) * mm});
            skLineSegment(sketch, "E564", {"start": v(61.87, 3.79) * mm, "end": v(61.9, 3.81) * mm});
            skLineSegment(sketch, "E565", {"start": v(61.9, 3.81) * mm, "end": v(61.93, 3.81) * mm});
            skLineSegment(sketch, "E566", {"start": v(61.93, 3.81) * mm, "end": v(61.98, 3.8) * mm});
            skLineSegment(sketch, "E567", {"start": v(61.98, 3.8) * mm, "end": v(62.03, 3.79) * mm});
            skLineSegment(sketch, "E568", {"start": v(62.03, 3.79) * mm, "end": v(62.23, 3.7) * mm});
            skLineSegment(sketch, "E569", {"start": v(62.23, 3.7) * mm, "end": v(62.27, 3.7) * mm});
            skLineSegment(sketch, "E570", {"start": v(62.27, 3.7) * mm, "end": v(62.32, 3.7) * mm});
            skLineSegment(sketch, "E571", {"start": v(62.32, 3.7) * mm, "end": v(62.3, 3.8) * mm});
            skLineSegment(sketch, "E572", {"start": v(62.3, 3.8) * mm, "end": v(62.3, 3.9) * mm});
            skLineSegment(sketch, "E573", {"start": v(62.3, 3.9) * mm, "end": v(62.26, 4.02) * mm});
            skLineSegment(sketch, "E574", {"start": v(62.26, 4.02) * mm, "end": v(62.2, 4.18) * mm});
            skLineSegment(sketch, "E575", {"start": v(62.2, 4.18) * mm, "end": v(62.1, 4.38) * mm});
            skLineSegment(sketch, "E576", {"start": v(62.1, 4.38) * mm, "end": v(62.01, 4.61) * mm});
            skLineSegment(sketch, "E577", {"start": v(62.01, 4.61) * mm, "end": v(62.1, 4.67) * mm});
            skLineSegment(sketch, "E578", {"start": v(62.1, 4.67) * mm, "end": v(62.12, 4.7) * mm});
            skLineSegment(sketch, "E579", {"start": v(62.12, 4.7) * mm, "end": v(62.14, 4.7) * mm});
            skLineSegment(sketch, "E580", {"start": v(62.14, 4.7) * mm, "end": v(62.14, 4.72) * mm});
            skLineSegment(sketch, "E581", {"start": v(62.14, 4.72) * mm, "end": v(62.15, 4.73) * mm});
            skLineSegment(sketch, "E582", {"start": v(62.15, 4.73) * mm, "end": v(62.15, 4.74) * mm});
            skLineSegment(sketch, "E583", {"start": v(62.15, 4.74) * mm, "end": v(62.15, 4.75) * mm});
            skLineSegment(sketch, "E584", {"start": v(62.15, 4.75) * mm, "end": v(62.16, 4.76) * mm});
            skLineSegment(sketch, "E585", {"start": v(62.16, 4.76) * mm, "end": v(62.15, 4.77) * mm});
            skLineSegment(sketch, "E586", {"start": v(62.15, 4.77) * mm, "end": v(62.15, 4.79) * mm});
            skLineSegment(sketch, "E587", {"start": v(62.15, 4.79) * mm, "end": v(62.15, 4.8) * mm});
            skLineSegment(sketch, "E588", {"start": v(62.15, 4.8) * mm, "end": v(62.12, 4.88) * mm});
            skLineSegment(sketch, "E589", {"start": v(62.12, 4.88) * mm, "end": v(62.07, 4.98) * mm});
            skLineSegment(sketch, "E590", {"start": v(62.07, 4.98) * mm, "end": v(62.16, 5.01) * mm});
            skLineSegment(sketch, "E591", {"start": v(62.16, 5.01) * mm, "end": v(62.22, 5.04) * mm});
            skLineSegment(sketch, "E592", {"start": v(62.22, 5.04) * mm, "end": v(62.27, 5.07) * mm});
            skLineSegment(sketch, "E593", {"start": v(62.27, 5.07) * mm, "end": v(62.3, 5.1) * mm});
            skLineSegment(sketch, "E594", {"start": v(62.3, 5.1) * mm, "end": v(62.34, 5.13) * mm});
            skLineSegment(sketch, "E595", {"start": v(62.34, 5.13) * mm, "end": v(62.36, 5.16) * mm});
            skLineSegment(sketch, "E596", {"start": v(62.36, 5.16) * mm, "end": v(62.38, 5.18) * mm});
            skLineSegment(sketch, "E597", {"start": v(62.38, 5.18) * mm, "end": v(62.4, 5.22) * mm});
            skLineSegment(sketch, "E598", {"start": v(62.4, 5.22) * mm, "end": v(62.41, 5.25) * mm});
            skLineSegment(sketch, "E599", {"start": v(62.41, 5.25) * mm, "end": v(62.43, 5.29) * mm});
            skLineSegment(sketch, "E600", {"start": v(62.43, 5.29) * mm, "end": v(62.43, 5.32) * mm});
            skLineSegment(sketch, "E601", {"start": v(62.43, 5.32) * mm, "end": v(62.44, 5.37) * mm});
            skLineSegment(sketch, "E602", {"start": v(62.44, 5.37) * mm, "end": v(62.44, 5.41) * mm});
            skLineSegment(sketch, "E603", {"start": v(62.44, 5.41) * mm, "end": v(62.2, 5.41) * mm});
            skLineSegment(sketch, "E604", {"start": v(62.2, 5.41) * mm, "end": v(62.13, 5.42) * mm});
            skLineSegment(sketch, "E605", {"start": v(62.13, 5.42) * mm, "end": v(62.1, 5.43) * mm});
            skLineSegment(sketch, "E606", {"start": v(62.1, 5.43) * mm, "end": v(62.06, 5.44) * mm});
            skLineSegment(sketch, "E607", {"start": v(62.06, 5.44) * mm, "end": v(62.04, 5.45) * mm});
            skLineSegment(sketch, "E608", {"start": v(62.04, 5.45) * mm, "end": v(62.01, 5.46) * mm});
            skLineSegment(sketch, "E609", {"start": v(62.01, 5.46) * mm, "end": v(62, 5.47) * mm});
            skLineSegment(sketch, "E610", {"start": v(62, 5.47) * mm, "end": v(61.99, 5.48) * mm});
            skLineSegment(sketch, "E611", {"start": v(61.99, 5.48) * mm, "end": v(61.97, 5.5) * mm});
            skLineSegment(sketch, "E612", {"start": v(61.97, 5.5) * mm, "end": v(61.96, 5.51) * mm});
            skLineSegment(sketch, "E613", {"start": v(61.96, 5.51) * mm, "end": v(61.96, 5.52) * mm});
            skLineSegment(sketch, "E614", {"start": v(61.96, 5.52) * mm, "end": v(61.95, 5.53) * mm});
            skLineSegment(sketch, "E615", {"start": v(61.95, 5.53) * mm, "end": v(61.97, 5.72) * mm});
            skLineSegment(sketch, "E616", {"start": v(61.97, 5.72) * mm, "end": v(61.98, 5.82) * mm});
            skLineSegment(sketch, "E617", {"start": v(61.98, 5.82) * mm, "end": v(61.98, 5.87) * mm});
            skLineSegment(sketch, "E618", {"start": v(61.98, 5.87) * mm, "end": v(61.97, 5.94) * mm});
            skLineSegment(sketch, "E619", {"start": v(61.97, 5.94) * mm, "end": v(61.95, 6.03) * mm});
            skLineSegment(sketch, "E620", {"start": v(61.95, 6.03) * mm, "end": v(62.01, 6.03) * mm});
            skLineSegment(sketch, "E621", {"start": v(62.01, 6.03) * mm, "end": v(62.05, 6.04) * mm});
            skLineSegment(sketch, "E622", {"start": v(62.05, 6.04) * mm, "end": v(62.09, 6.05) * mm});
            skLineSegment(sketch, "E623", {"start": v(62.09, 6.05) * mm, "end": v(62.11, 6.06) * mm});
            skLineSegment(sketch, "E624", {"start": v(62.11, 6.06) * mm, "end": v(62.13, 6.07) * mm});
            skLineSegment(sketch, "E625", {"start": v(62.13, 6.07) * mm, "end": v(62.15, 6.09) * mm});
            skLineSegment(sketch, "E626", {"start": v(62.15, 6.09) * mm, "end": v(62.16, 6.1) * mm});
            skLineSegment(sketch, "E627", {"start": v(62.16, 6.1) * mm, "end": v(62.17, 6.11) * mm});
            skLineSegment(sketch, "E628", {"start": v(62.17, 6.11) * mm, "end": v(62.18, 6.12) * mm});
            skLineSegment(sketch, "E629", {"start": v(62.18, 6.12) * mm, "end": v(62.19, 6.13) * mm});
            skLineSegment(sketch, "E630", {"start": v(62.19, 6.13) * mm, "end": v(62.2, 6.15) * mm});
            skLineSegment(sketch, "E631", {"start": v(62.2, 6.15) * mm, "end": v(62.14, 6.17) * mm});
            skLineSegment(sketch, "E632", {"start": v(62.14, 6.17) * mm, "end": v(62.06, 6.2) * mm});
            skLineSegment(sketch, "E633", {"start": v(62.06, 6.2) * mm, "end": v(61.91, 6.24) * mm});
            skLineSegment(sketch, "E634", {"start": v(61.91, 6.24) * mm, "end": v(61.56, 6.32) * mm});
            skLineSegment(sketch, "E635", {"start": v(61.56, 6.32) * mm, "end": v(61.48, 6.35) * mm});
            skLineSegment(sketch, "E636", {"start": v(61.48, 6.35) * mm, "end": v(61.44, 6.37) * mm});
            skLineSegment(sketch, "E637", {"start": v(61.44, 6.37) * mm, "end": v(61.4, 6.4) * mm});
            skLineSegment(sketch, "E638", {"start": v(61.4, 6.4) * mm, "end": v(61.4, 6.42) * mm});
            skLineSegment(sketch, "E639", {"start": v(61.4, 6.42) * mm, "end": v(61.39, 6.44) * mm});
            skLineSegment(sketch, "E640", {"start": v(61.39, 6.44) * mm, "end": v(61.39, 6.46) * mm});
            skLineSegment(sketch, "E641", {"start": v(61.39, 6.46) * mm, "end": v(61.39, 6.49) * mm});
            skLineSegment(sketch, "E642", {"start": v(61.39, 6.49) * mm, "end": v(61.4, 6.52) * mm});
            skLineSegment(sketch, "E643", {"start": v(61.4, 6.52) * mm, "end": v(61.4, 6.57) * mm});
            skLineSegment(sketch, "E644", {"start": v(61.4, 6.57) * mm, "end": v(61.46, 6.74) * mm});
            skLineSegment(sketch, "E645", {"start": v(61.46, 6.74) * mm, "end": v(61.47, 6.76) * mm});
            skLineSegment(sketch, "E646", {"start": v(61.47, 6.76) * mm, "end": v(61.47, 6.78) * mm});
            skLineSegment(sketch, "E647", {"start": v(61.47, 6.78) * mm, "end": v(61.47, 6.8) * mm});
            skLineSegment(sketch, "E648", {"start": v(61.47, 6.8) * mm, "end": v(61.46, 6.8) * mm});
            skLineSegment(sketch, "E649", {"start": v(61.46, 6.8) * mm, "end": v(61.46, 6.83) * mm});
            skLineSegment(sketch, "E650", {"start": v(61.46, 6.83) * mm, "end": v(61.45, 6.84) * mm});
            skLineSegment(sketch, "E651", {"start": v(61.45, 6.84) * mm, "end": v(61.44, 6.86) * mm});
            skLineSegment(sketch, "E652", {"start": v(61.44, 6.86) * mm, "end": v(61.42, 6.87) * mm});
            skLineSegment(sketch, "E653", {"start": v(61.42, 6.87) * mm, "end": v(61.4, 6.89) * mm});
            skLineSegment(sketch, "E654", {"start": v(61.4, 6.89) * mm, "end": v(61.37, 6.87) * mm});
            skLineSegment(sketch, "E655", {"start": v(61.37, 6.87) * mm, "end": v(61.24, 6.75) * mm});
            skLineSegment(sketch, "E656", {"start": v(61.24, 6.75) * mm, "end": v(61.23, 6.74) * mm});
            skLineSegment(sketch, "E657", {"start": v(61.23, 6.74) * mm, "end": v(61.2, 6.73) * mm});
            skLineSegment(sketch, "E658", {"start": v(61.2, 6.73) * mm, "end": v(61.2, 6.72) * mm});
            skLineSegment(sketch, "E659", {"start": v(61.2, 6.72) * mm, "end": v(61.18, 6.72) * mm});
            skLineSegment(sketch, "E660", {"start": v(61.18, 6.72) * mm, "end": v(61.17, 6.72) * mm});
            skLineSegment(sketch, "E661", {"start": v(61.17, 6.72) * mm, "end": v(61.16, 6.72) * mm});
            skLineSegment(sketch, "E662", {"start": v(61.16, 6.72) * mm, "end": v(61.14, 6.73) * mm});
            skLineSegment(sketch, "E663", {"start": v(61.14, 6.73) * mm, "end": v(61.13, 6.73) * mm});
            skLineSegment(sketch, "E664", {"start": v(61.13, 6.73) * mm, "end": v(61.12, 6.74) * mm});
            skLineSegment(sketch, "E665", {"start": v(61.12, 6.74) * mm, "end": v(61.1, 6.75) * mm});
            skLineSegment(sketch, "E666", {"start": v(61.1, 6.75) * mm, "end": v(61.1, 6.76) * mm});
            skLineSegment(sketch, "E667", {"start": v(61.1, 6.76) * mm, "end": v(61.09, 6.83) * mm});
            skLineSegment(sketch, "E668", {"start": v(61.09, 6.83) * mm, "end": v(61.08, 6.9) * mm});
            skLineSegment(sketch, "E669", {"start": v(61.08, 6.9) * mm, "end": v(61.06, 6.98) * mm});
            skLineSegment(sketch, "E670", {"start": v(61.06, 6.98) * mm, "end": v(60.98, 7.24) * mm});
            skLineSegment(sketch, "E671", {"start": v(60.98, 7.24) * mm, "end": v(60.97, 7.3) * mm});
            skLineSegment(sketch, "E672", {"start": v(60.97, 7.3) * mm, "end": v(60.97, 7.38) * mm});
            skLineSegment(sketch, "E673", {"start": v(60.97, 7.38) * mm, "end": v(60.95, 7.38) * mm});
            skLineSegment(sketch, "E674", {"start": v(60.95, 7.38) * mm, "end": v(60.93, 7.38) * mm});
            skLineSegment(sketch, "E675", {"start": v(60.93, 7.38) * mm, "end": v(60.91, 7.38) * mm});
            skLineSegment(sketch, "E676", {"start": v(60.91, 7.38) * mm, "end": v(60.9, 7.38) * mm});
            skLineSegment(sketch, "E677", {"start": v(60.9, 7.38) * mm, "end": v(60.89, 7.38) * mm});
            skLineSegment(sketch, "E678", {"start": v(60.89, 7.38) * mm, "end": v(60.88, 7.38) * mm});
            skLineSegment(sketch, "E679", {"start": v(60.88, 7.38) * mm, "end": v(60.88, 7.37) * mm});
            skLineSegment(sketch, "E680", {"start": v(60.88, 7.37) * mm, "end": v(60.87, 7.37) * mm});
            skLineSegment(sketch, "E681", {"start": v(60.87, 7.37) * mm, "end": v(60.87, 7.37) * mm});
            skLineSegment(sketch, "E682", {"start": v(60.87, 7.37) * mm, "end": v(60.86, 7.36) * mm});
            skLineSegment(sketch, "E683", {"start": v(60.86, 7.36) * mm, "end": v(60.85, 7.35) * mm});
            skLineSegment(sketch, "E684", {"start": v(60.85, 7.35) * mm, "end": v(60.85, 7.34) * mm});
            skLineSegment(sketch, "E685", {"start": v(60.85, 7.34) * mm, "end": v(60.84, 7.32) * mm});
            skLineSegment(sketch, "E686", {"start": v(60.84, 7.32) * mm, "end": v(60.81, 7.24) * mm});
            skLineSegment(sketch, "E687", {"start": v(60.81, 7.24) * mm, "end": v(60.8, 7.23) * mm});
            skLineSegment(sketch, "E688", {"start": v(60.8, 7.23) * mm, "end": v(60.8, 7.22) * mm});
            skLineSegment(sketch, "E689", {"start": v(60.8, 7.22) * mm, "end": v(60.8, 7.2) * mm});
            skLineSegment(sketch, "E690", {"start": v(60.8, 7.2) * mm, "end": v(60.79, 7.2) * mm});
            skLineSegment(sketch, "E691", {"start": v(60.79, 7.2) * mm, "end": v(60.78, 7.2) * mm});
            skLineSegment(sketch, "E692", {"start": v(60.78, 7.2) * mm, "end": v(60.78, 7.2) * mm});
            skLineSegment(sketch, "E693", {"start": v(60.78, 7.2) * mm, "end": v(60.77, 7.2) * mm});
            skLineSegment(sketch, "E694", {"start": v(60.77, 7.2) * mm, "end": v(60.76, 7.2) * mm});
            skLineSegment(sketch, "E695", {"start": v(60.76, 7.2) * mm, "end": v(60.76, 7.2) * mm});
            skLineSegment(sketch, "E696", {"start": v(60.76, 7.2) * mm, "end": v(60.74, 7.2) * mm});
            skLineSegment(sketch, "E697", {"start": v(60.74, 7.2) * mm, "end": v(60.72, 7.2) * mm});
            skLineSegment(sketch, "E698", {"start": v(60.72, 7.2) * mm, "end": v(60.5, 7.2) * mm});
            skLineSegment(sketch, "E699", {"start": v(60.5, 7.2) * mm, "end": v(60.46, 7.2) * mm});
            skLineSegment(sketch, "E700", {"start": v(60.46, 7.2) * mm, "end": v(60.44, 7.2) * mm});
            skLineSegment(sketch, "E701", {"start": v(60.44, 7.2) * mm, "end": v(60.42, 7.21) * mm});
            skLineSegment(sketch, "E702", {"start": v(60.42, 7.21) * mm, "end": v(60.4, 7.22) * mm});
            skLineSegment(sketch, "E703", {"start": v(60.4, 7.22) * mm, "end": v(60.4, 7.23) * mm});
            skLineSegment(sketch, "E704", {"start": v(60.4, 7.23) * mm, "end": v(60.38, 7.24) * mm});
            skLineSegment(sketch, "E705", {"start": v(60.38, 7.24) * mm, "end": v(60.38, 7.25) * mm});
            skLineSegment(sketch, "E706", {"start": v(60.38, 7.25) * mm, "end": v(60.37, 7.26) * mm});
            skLineSegment(sketch, "E707", {"start": v(60.37, 7.26) * mm, "end": v(60.36, 7.27) * mm});
            skLineSegment(sketch, "E708", {"start": v(60.36, 7.27) * mm, "end": v(60.36, 7.29) * mm});
            skLineSegment(sketch, "E709", {"start": v(60.36, 7.29) * mm, "end": v(60.36, 7.3) * mm});
            skLineSegment(sketch, "E710", {"start": v(60.36, 7.3) * mm, "end": v(60.35, 7.32) * mm});
            skLineSegment(sketch, "E711", {"start": v(60.35, 7.32) * mm, "end": v(60.35, 7.34) * mm});
            skLineSegment(sketch, "E712", {"start": v(60.35, 7.34) * mm, "end": v(60.34, 7.36) * mm});
            skLineSegment(sketch, "E713", {"start": v(60.34, 7.36) * mm, "end": v(60.34, 7.38) * mm});
            skLineSegment(sketch, "E714", {"start": v(60.34, 7.38) * mm, "end": v(60.34, 7.39) * mm});
            skLineSegment(sketch, "E715", {"start": v(60.34, 7.39) * mm, "end": v(60.34, 7.4) * mm});
            skLineSegment(sketch, "E716", {"start": v(60.34, 7.4) * mm, "end": v(60.34, 7.4) * mm});
            skLineSegment(sketch, "E717", {"start": v(60.34, 7.4) * mm, "end": v(60.35, 7.4) * mm});
            skLineSegment(sketch, "E718", {"start": v(60.35, 7.4) * mm, "end": v(60.35, 7.41) * mm});
            skLineSegment(sketch, "E719", {"start": v(60.35, 7.41) * mm, "end": v(60.36, 7.42) * mm});
            skLineSegment(sketch, "E720", {"start": v(60.36, 7.42) * mm, "end": v(60.36, 7.42) * mm});
            skLineSegment(sketch, "E721", {"start": v(60.36, 7.42) * mm, "end": v(60.37, 7.42) * mm});
            skLineSegment(sketch, "E722", {"start": v(60.37, 7.42) * mm, "end": v(60.37, 7.43) * mm});
            skLineSegment(sketch, "E723", {"start": v(60.37, 7.43) * mm, "end": v(60.38, 7.43) * mm});
            skLineSegment(sketch, "E724", {"start": v(60.38, 7.43) * mm, "end": v(60.4, 7.43) * mm});
            skLineSegment(sketch, "E725", {"start": v(60.4, 7.43) * mm, "end": v(60.43, 7.44) * mm});
            skLineSegment(sketch, "E726", {"start": v(60.43, 7.44) * mm, "end": v(60.5, 7.44) * mm});
            skLineSegment(sketch, "E727", {"start": v(60.5, 7.44) * mm, "end": v(60.5, 7.44) * mm});
            skLineSegment(sketch, "E728", {"start": v(60.5, 7.44) * mm, "end": v(60.52, 7.45) * mm});
            skLineSegment(sketch, "E729", {"start": v(60.52, 7.45) * mm, "end": v(60.53, 7.45) * mm});
            skLineSegment(sketch, "E730", {"start": v(60.53, 7.45) * mm, "end": v(60.53, 7.45) * mm});
            skLineSegment(sketch, "E731", {"start": v(60.53, 7.45) * mm, "end": v(60.54, 7.46) * mm});
            skLineSegment(sketch, "E732", {"start": v(60.54, 7.46) * mm, "end": v(60.54, 7.46) * mm});
            skLineSegment(sketch, "E733", {"start": v(60.54, 7.46) * mm, "end": v(60.55, 7.47) * mm});
            skLineSegment(sketch, "E734", {"start": v(60.55, 7.47) * mm, "end": v(60.55, 7.47) * mm});
            skLineSegment(sketch, "E735", {"start": v(60.55, 7.47) * mm, "end": v(60.55, 7.48) * mm});
            skLineSegment(sketch, "E736", {"start": v(60.55, 7.48) * mm, "end": v(60.55, 7.49) * mm});
            skLineSegment(sketch, "E737", {"start": v(60.55, 7.49) * mm, "end": v(60.55, 7.5) * mm});
            skLineSegment(sketch, "E738", {"start": v(60.55, 7.5) * mm, "end": v(60.55, 7.5) * mm});
            skLineSegment(sketch, "E739", {"start": v(60.55, 7.5) * mm, "end": v(60.55, 7.52) * mm});
            skLineSegment(sketch, "E740", {"start": v(60.55, 7.52) * mm, "end": v(60.55, 7.53) * mm});
            skLineSegment(sketch, "E741", {"start": v(60.55, 7.53) * mm, "end": v(60.54, 7.56) * mm});
            skLineSegment(sketch, "E742", {"start": v(60.54, 7.56) * mm, "end": v(60.53, 7.57) * mm});
            skLineSegment(sketch, "E743", {"start": v(60.53, 7.57) * mm, "end": v(60.53, 7.58) * mm});
            skLineSegment(sketch, "E744", {"start": v(60.53, 7.58) * mm, "end": v(60.52, 7.59) * mm});
            skLineSegment(sketch, "E745", {"start": v(60.52, 7.59) * mm, "end": v(60.51, 7.6) * mm});
            skLineSegment(sketch, "E746", {"start": v(60.51, 7.6) * mm, "end": v(60.5, 7.6) * mm});
            skLineSegment(sketch, "E747", {"start": v(60.5, 7.6) * mm, "end": v(60.5, 7.6) * mm});
            skLineSegment(sketch, "E748", {"start": v(60.5, 7.6) * mm, "end": v(60.47, 7.61) * mm});
            skLineSegment(sketch, "E749", {"start": v(60.47, 7.61) * mm, "end": v(60.45, 7.62) * mm});
            skLineSegment(sketch, "E750", {"start": v(60.45, 7.62) * mm, "end": v(60.4, 7.62) * mm});
            skLineSegment(sketch, "E751", {"start": v(60.4, 7.62) * mm, "end": v(60.33, 7.62) * mm});
            skLineSegment(sketch, "E752", {"start": v(60.33, 7.62) * mm, "end": v(60.17, 7.62) * mm});
            skLineSegment(sketch, "E753", {"start": v(60.17, 7.62) * mm, "end": v(60.13, 7.62) * mm});
            skLineSegment(sketch, "E754", {"start": v(60.13, 7.62) * mm, "end": v(60.1, 7.63) * mm});
            skLineSegment(sketch, "E755", {"start": v(60.1, 7.63) * mm, "end": v(60.08, 7.64) * mm});
            skLineSegment(sketch, "E756", {"start": v(60.08, 7.64) * mm, "end": v(60.07, 7.64) * mm});
            skLineSegment(sketch, "E757", {"start": v(60.07, 7.64) * mm, "end": v(60.07, 7.65) * mm});
            skLineSegment(sketch, "E758", {"start": v(60.07, 7.65) * mm, "end": v(60.06, 7.66) * mm});
            skLineSegment(sketch, "E759", {"start": v(60.06, 7.66) * mm, "end": v(60.05, 7.66) * mm});
            skLineSegment(sketch, "E760", {"start": v(60.05, 7.66) * mm, "end": v(60.05, 7.67) * mm});
            skLineSegment(sketch, "E761", {"start": v(60.05, 7.67) * mm, "end": v(60.04, 7.68) * mm});
            skLineSegment(sketch, "E762", {"start": v(60.04, 7.68) * mm, "end": v(60.04, 7.7) * mm});
            skLineSegment(sketch, "E763", {"start": v(60.04, 7.7) * mm, "end": v(60.04, 7.7) * mm});
            skLineSegment(sketch, "E764", {"start": v(60.04, 7.7) * mm, "end": v(60.03, 7.72) * mm});
            skLineSegment(sketch, "E765", {"start": v(60.03, 7.72) * mm, "end": v(60.04, 7.75) * mm});
            skLineSegment(sketch, "E766", {"start": v(60.04, 7.75) * mm, "end": v(60.04, 7.77) * mm});
            skLineSegment(sketch, "E767", {"start": v(60.04, 7.77) * mm, "end": v(60.05, 7.8) * mm});
            skLineSegment(sketch, "E768", {"start": v(60.05, 7.8) * mm, "end": v(60.02, 7.8) * mm});
            skLineSegment(sketch, "E769", {"start": v(60.02, 7.8) * mm, "end": v(60, 7.8) * mm});
            skLineSegment(sketch, "E770", {"start": v(60, 7.8) * mm, "end": v(59.98, 7.8) * mm});
            skLineSegment(sketch, "E771", {"start": v(59.98, 7.8) * mm, "end": v(59.96, 7.8) * mm});
            skLineSegment(sketch, "E772", {"start": v(59.96, 7.8) * mm, "end": v(59.94, 7.8) * mm});
            skLineSegment(sketch, "E773", {"start": v(59.94, 7.8) * mm, "end": v(59.93, 7.78) * mm});
            skLineSegment(sketch, "E774", {"start": v(59.93, 7.78) * mm, "end": v(59.91, 7.77) * mm});
            skLineSegment(sketch, "E775", {"start": v(59.91, 7.77) * mm, "end": v(59.9, 7.75) * mm});
            skLineSegment(sketch, "E776", {"start": v(59.9, 7.75) * mm, "end": v(59.86, 7.72) * mm});
            skLineSegment(sketch, "E777", {"start": v(59.86, 7.72) * mm, "end": v(59.82, 7.67) * mm});
            skLineSegment(sketch, "E778", {"start": v(59.82, 7.67) * mm, "end": v(59.8, 7.65) * mm});
            skLineSegment(sketch, "E779", {"start": v(59.8, 7.65) * mm, "end": v(59.79, 7.64) * mm});
            skLineSegment(sketch, "E780", {"start": v(59.79, 7.64) * mm, "end": v(59.77, 7.63) * mm});
            skLineSegment(sketch, "E781", {"start": v(59.77, 7.63) * mm, "end": v(59.75, 7.62) * mm});
            skLineSegment(sketch, "E782", {"start": v(59.75, 7.62) * mm, "end": v(59.73, 7.62) * mm});
            skLineSegment(sketch, "E783", {"start": v(59.73, 7.62) * mm, "end": v(59.71, 7.61) * mm});
            skLineSegment(sketch, "E784", {"start": v(59.71, 7.61) * mm, "end": v(59.69, 7.61) * mm});
            skLineSegment(sketch, "E785", {"start": v(59.69, 7.61) * mm, "end": v(59.66, 7.61) * mm});
            skLineSegment(sketch, "E786", {"start": v(59.66, 7.61) * mm, "end": v(59.62, 7.62) * mm});
            skLineSegment(sketch, "E787", {"start": v(59.62, 7.62) * mm, "end": v(59.61, 7.64) * mm});
            skLineSegment(sketch, "E788", {"start": v(59.61, 7.64) * mm, "end": v(59.6, 7.65) * mm});
            skLineSegment(sketch, "E789", {"start": v(59.6, 7.65) * mm, "end": v(59.6, 7.66) * mm});
            skLineSegment(sketch, "E790", {"start": v(59.6, 7.66) * mm, "end": v(59.6, 7.67) * mm});
            skLineSegment(sketch, "E791", {"start": v(59.6, 7.67) * mm, "end": v(59.59, 7.69) * mm});
            skLineSegment(sketch, "E792", {"start": v(59.59, 7.69) * mm, "end": v(59.57, 7.7) * mm});
            skLineSegment(sketch, "E793", {"start": v(59.57, 7.7) * mm, "end": v(59.52, 7.75) * mm});
            skLineSegment(sketch, "E794", {"start": v(59.52, 7.75) * mm, "end": v(59.51, 7.77) * mm});
            skLineSegment(sketch, "E795", {"start": v(59.51, 7.77) * mm, "end": v(59.5, 7.78) * mm});
            skLineSegment(sketch, "E796", {"start": v(59.5, 7.78) * mm, "end": v(59.5, 7.8) * mm});
            skLineSegment(sketch, "E797", {"start": v(59.5, 7.8) * mm, "end": v(59.5, 7.8) * mm});
            skLineSegment(sketch, "E798", {"start": v(59.5, 7.8) * mm, "end": v(59.5, 7.84) * mm});
            skLineSegment(sketch, "E799", {"start": v(59.5, 7.84) * mm, "end": v(59.5, 7.87) * mm});
            skLineSegment(sketch, "E800", {"start": v(59.5, 7.87) * mm, "end": v(59.51, 7.9) * mm});
            skLineSegment(sketch, "E801", {"start": v(59.51, 7.9) * mm, "end": v(59.52, 7.93) * mm});
            skLineSegment(sketch, "E802", {"start": v(59.52, 7.93) * mm, "end": v(59.54, 7.95) * mm});
            skLineSegment(sketch, "E803", {"start": v(59.54, 7.95) * mm, "end": v(59.56, 7.98) * mm});
            skLineSegment(sketch, "E804", {"start": v(59.56, 7.98) * mm, "end": v(59.64, 8.08) * mm});
            skLineSegment(sketch, "E805", {"start": v(59.64, 8.08) * mm, "end": v(59.65, 8.1) * mm});
            skLineSegment(sketch, "E806", {"start": v(59.65, 8.1) * mm, "end": v(59.67, 8.13) * mm});
            skLineSegment(sketch, "E807", {"start": v(59.67, 8.13) * mm, "end": v(59.67, 8.16) * mm});
            skLineSegment(sketch, "E808", {"start": v(59.67, 8.16) * mm, "end": v(59.68, 8.19) * mm});
            skLineSegment(sketch, "E809", {"start": v(59.68, 8.19) * mm, "end": v(59.68, 8.21) * mm});
            skLineSegment(sketch, "E810", {"start": v(59.68, 8.21) * mm, "end": v(59.68, 8.24) * mm});
            skLineSegment(sketch, "E811", {"start": v(59.68, 8.24) * mm, "end": v(59.6, 8.22) * mm});
            skLineSegment(sketch, "E812", {"start": v(59.6, 8.22) * mm, "end": v(59.52, 8.2) * mm});
            skLineSegment(sketch, "E813", {"start": v(59.52, 8.2) * mm, "end": v(59.45, 8.16) * mm});
            skLineSegment(sketch, "E814", {"start": v(59.45, 8.16) * mm, "end": v(59.36, 8.1) * mm});
            skLineSegment(sketch, "E815", {"start": v(59.36, 8.1) * mm, "end": v(59.26, 8.03) * mm});
            skLineSegment(sketch, "E816", {"start": v(59.26, 8.03) * mm, "end": v(58.92, 7.76) * mm});
            skLineSegment(sketch, "E817", {"start": v(58.92, 7.76) * mm, "end": v(58.83, 7.7) * mm});
            skLineSegment(sketch, "E818", {"start": v(58.83, 7.7) * mm, "end": v(58.76, 7.67) * mm});
            skLineSegment(sketch, "E819", {"start": v(58.76, 7.67) * mm, "end": v(58.69, 7.65) * mm});
            skLineSegment(sketch, "E820", {"start": v(58.69, 7.65) * mm, "end": v(58.63, 7.63) * mm});
            skLineSegment(sketch, "E821", {"start": v(58.63, 7.63) * mm, "end": v(58.57, 7.62) * mm});
            skLineSegment(sketch, "E822", {"start": v(58.57, 7.62) * mm, "end": v(58.57, 7.9) * mm});
            skLineSegment(sketch, "E823", {"start": v(58.57, 7.9) * mm, "end": v(58.58, 7.94) * mm});
            skLineSegment(sketch, "E824", {"start": v(58.58, 7.94) * mm, "end": v(58.59, 7.97) * mm});
            skLineSegment(sketch, "E825", {"start": v(58.59, 7.97) * mm, "end": v(58.6, 8) * mm});
            skLineSegment(sketch, "E826", {"start": v(58.6, 8) * mm, "end": v(58.6, 8.01) * mm});
            skLineSegment(sketch, "E827", {"start": v(58.6, 8.01) * mm, "end": v(58.62, 8.03) * mm});
            skLineSegment(sketch, "E828", {"start": v(58.62, 8.03) * mm, "end": v(58.63, 8.04) * mm});
            skLineSegment(sketch, "E829", {"start": v(58.63, 8.04) * mm, "end": v(58.63, 8.05) * mm});
            skLineSegment(sketch, "E830", {"start": v(58.63, 8.05) * mm, "end": v(58.6, 8.05) * mm});
            skLineSegment(sketch, "E831", {"start": v(58.6, 8.05) * mm, "end": v(58.58, 8.04) * mm});
            skLineSegment(sketch, "E832", {"start": v(58.58, 8.04) * mm, "end": v(58.55, 8.04) * mm});
            skLineSegment(sketch, "E833", {"start": v(58.55, 8.04) * mm, "end": v(58.53, 8.03) * mm});
            skLineSegment(sketch, "E834", {"start": v(58.53, 8.03) * mm, "end": v(58.5, 8.01) * mm});
            skLineSegment(sketch, "E835", {"start": v(58.5, 8.01) * mm, "end": v(58.48, 8) * mm});
            skLineSegment(sketch, "E836", {"start": v(58.48, 8) * mm, "end": v(58.45, 7.97) * mm});
            skLineSegment(sketch, "E837", {"start": v(58.45, 7.97) * mm, "end": v(58.4, 7.92) * mm});
            skLineSegment(sketch, "E838", {"start": v(58.4, 7.92) * mm, "end": v(58.31, 7.81) * mm});
            skLineSegment(sketch, "E839", {"start": v(58.31, 7.81) * mm, "end": v(58.3, 7.8) * mm});
            skLineSegment(sketch, "E840", {"start": v(58.3, 7.8) * mm, "end": v(58.28, 7.8) * mm});
            skLineSegment(sketch, "E841", {"start": v(58.28, 7.8) * mm, "end": v(58.27, 7.79) * mm});
            skLineSegment(sketch, "E842", {"start": v(58.27, 7.79) * mm, "end": v(58.27, 7.78) * mm});
            skLineSegment(sketch, "E843", {"start": v(58.27, 7.78) * mm, "end": v(58.26, 7.78) * mm});
            skLineSegment(sketch, "E844", {"start": v(58.26, 7.78) * mm, "end": v(58.25, 7.78) * mm});
            skLineSegment(sketch, "E845", {"start": v(58.25, 7.78) * mm, "end": v(58.25, 7.78) * mm});
            skLineSegment(sketch, "E846", {"start": v(58.25, 7.78) * mm, "end": v(58.24, 7.78) * mm});
            skLineSegment(sketch, "E847", {"start": v(58.24, 7.78) * mm, "end": v(58.23, 7.79) * mm});
            skLineSegment(sketch, "E848", {"start": v(58.23, 7.79) * mm, "end": v(58.23, 7.79) * mm});
            skLineSegment(sketch, "E849", {"start": v(58.23, 7.79) * mm, "end": v(58.22, 7.8) * mm});
            skLineSegment(sketch, "E850", {"start": v(58.22, 7.8) * mm, "end": v(58.21, 7.8) * mm});
            skLineSegment(sketch, "E851", {"start": v(58.21, 7.8) * mm, "end": v(58.2, 7.8) * mm});
            skLineSegment(sketch, "E852", {"start": v(58.2, 7.8) * mm, "end": v(58.16, 7.85) * mm});
            skLineSegment(sketch, "E853", {"start": v(58.16, 7.85) * mm, "end": v(58.1, 7.9) * mm});
            skLineSegment(sketch, "E854", {"start": v(58.1, 7.9) * mm, "end": v(58, 7.95) * mm});
            skLineSegment(sketch, "E855", {"start": v(58, 7.95) * mm, "end": v(57.88, 8.02) * mm});
            skLineSegment(sketch, "E856", {"start": v(57.88, 8.02) * mm, "end": v(57.86, 8.03) * mm});
            skLineSegment(sketch, "E857", {"start": v(57.86, 8.03) * mm, "end": v(57.84, 8.05) * mm});
            skLineSegment(sketch, "E858", {"start": v(57.84, 8.05) * mm, "end": v(57.63, 8.25) * mm});
            skLineSegment(sketch, "E859", {"start": v(57.63, 8.25) * mm, "end": v(57.2, 8.74) * mm});
            skLineSegment(sketch, "E860", {"start": v(57.2, 8.74) * mm, "end": v(56.85, 9.1) * mm});
            skLineSegment(sketch, "E861", {"start": v(56.85, 9.1) * mm, "end": v(56.84, 9.1) * mm});
            skLineSegment(sketch, "E862", {"start": v(56.84, 9.1) * mm, "end": v(56.8, 9.12) * mm});
            skLineSegment(sketch, "E863", {"start": v(56.8, 9.12) * mm, "end": v(56.75, 9.15) * mm});
            skLineSegment(sketch, "E864", {"start": v(56.75, 9.15) * mm, "end": v(56.7, 9.17) * mm});
            skLineSegment(sketch, "E865", {"start": v(56.7, 9.17) * mm, "end": v(56.68, 9.17) * mm});
            skLineSegment(sketch, "E866", {"start": v(56.68, 9.17) * mm, "end": v(56.66, 9.17) * mm});
            skLineSegment(sketch, "E867", {"start": v(56.66, 9.17) * mm, "end": v(56.64, 9.17) * mm});
            skLineSegment(sketch, "E868", {"start": v(56.64, 9.17) * mm, "end": v(56.63, 9.17) * mm});
            skLineSegment(sketch, "E869", {"start": v(56.63, 9.17) * mm, "end": v(56.63, 9.17) * mm});
            skLineSegment(sketch, "E870", {"start": v(56.63, 9.17) * mm, "end": v(56.62, 9.17) * mm});
            skLineSegment(sketch, "E871", {"start": v(56.62, 9.17) * mm, "end": v(56.62, 9.17) * mm});
            skLineSegment(sketch, "E872", {"start": v(56.62, 9.17) * mm, "end": v(56.61, 9.16) * mm});
            skLineSegment(sketch, "E873", {"start": v(56.61, 9.16) * mm, "end": v(56.61, 9.16) * mm});
            skLineSegment(sketch, "E874", {"start": v(56.61, 9.16) * mm, "end": v(56.6, 9.16) * mm});
            skLineSegment(sketch, "E875", {"start": v(56.6, 9.16) * mm, "end": v(57.24, 8.29) * mm});
            skLineSegment(sketch, "E876", {"start": v(57.24, 8.29) * mm, "end": v(57.84, 7.38) * mm});
            skLineSegment(sketch, "E877", {"start": v(57.84, 7.38) * mm, "end": v(57.82, 7.35) * mm});
            skLineSegment(sketch, "E878", {"start": v(57.82, 7.35) * mm, "end": v(57.8, 7.32) * mm});
            skLineSegment(sketch, "E879", {"start": v(57.8, 7.32) * mm, "end": v(57.79, 7.3) * mm});
            skLineSegment(sketch, "E880", {"start": v(57.79, 7.3) * mm, "end": v(57.77, 7.27) * mm});
            skLineSegment(sketch, "E881", {"start": v(57.77, 7.27) * mm, "end": v(57.75, 7.25) * mm});
            skLineSegment(sketch, "E882", {"start": v(57.75, 7.25) * mm, "end": v(57.73, 7.23) * mm});
            skLineSegment(sketch, "E883", {"start": v(57.73, 7.23) * mm, "end": v(57.7, 7.22) * mm});
            skLineSegment(sketch, "E884", {"start": v(57.7, 7.22) * mm, "end": v(57.68, 7.2) * mm});
            skLineSegment(sketch, "E885", {"start": v(57.68, 7.2) * mm, "end": v(57.65, 7.2) * mm});
            skLineSegment(sketch, "E886", {"start": v(57.65, 7.2) * mm, "end": v(57.67, 7.17) * mm});
            skLineSegment(sketch, "E887", {"start": v(57.67, 7.17) * mm, "end": v(57.69, 7.14) * mm});
            skLineSegment(sketch, "E888", {"start": v(57.69, 7.14) * mm, "end": v(57.7, 7.12) * mm});
            skLineSegment(sketch, "E889", {"start": v(57.7, 7.12) * mm, "end": v(57.7, 7.1) * mm});
            skLineSegment(sketch, "E890", {"start": v(57.7, 7.1) * mm, "end": v(57.7, 7.07) * mm});
            skLineSegment(sketch, "E891", {"start": v(57.7, 7.07) * mm, "end": v(57.7, 7.05) * mm});
            skLineSegment(sketch, "E892", {"start": v(57.7, 7.05) * mm, "end": v(57.7, 7.03) * mm});
            skLineSegment(sketch, "E893", {"start": v(57.7, 7.03) * mm, "end": v(57.69, 7.01) * mm});
            skLineSegment(sketch, "E894", {"start": v(57.69, 7.01) * mm, "end": v(57.67, 6.98) * mm});
            skLineSegment(sketch, "E895", {"start": v(57.67, 6.98) * mm, "end": v(57.64, 6.94) * mm});
            skLineSegment(sketch, "E896", {"start": v(57.64, 6.94) * mm, "end": v(57.57, 6.84) * mm});
            skLineSegment(sketch, "E897", {"start": v(57.57, 6.84) * mm, "end": v(57.56, 6.82) * mm});
            skLineSegment(sketch, "E898", {"start": v(57.56, 6.82) * mm, "end": v(57.56, 6.8) * mm});
            skLineSegment(sketch, "E899", {"start": v(57.56, 6.8) * mm, "end": v(57.55, 6.79) * mm});
            skLineSegment(sketch, "E900", {"start": v(57.55, 6.79) * mm, "end": v(57.55, 6.78) * mm});
            skLineSegment(sketch, "E901", {"start": v(57.55, 6.78) * mm, "end": v(57.55, 6.77) * mm});
            skLineSegment(sketch, "E902", {"start": v(57.55, 6.77) * mm, "end": v(57.55, 6.76) * mm});
            skLineSegment(sketch, "E903", {"start": v(57.55, 6.76) * mm, "end": v(57.55, 6.75) * mm});
            skLineSegment(sketch, "E904", {"start": v(57.55, 6.75) * mm, "end": v(57.56, 6.75) * mm});
            skLineSegment(sketch, "E905", {"start": v(57.56, 6.75) * mm, "end": v(57.56, 6.74) * mm});
            skLineSegment(sketch, "E906", {"start": v(57.56, 6.74) * mm, "end": v(57.57, 6.73) * mm});
            skLineSegment(sketch, "E907", {"start": v(57.57, 6.73) * mm, "end": v(57.57, 6.72) * mm});
            skLineSegment(sketch, "E908", {"start": v(57.57, 6.72) * mm, "end": v(57.6, 6.7) * mm});
            skLineSegment(sketch, "E909", {"start": v(57.6, 6.7) * mm, "end": v(57.6, 6.7) * mm});
            skLineSegment(sketch, "E910", {"start": v(57.6, 6.7) * mm, "end": v(57.6, 6.72) * mm});
            skLineSegment(sketch, "E911", {"start": v(57.6, 6.72) * mm, "end": v(57.6, 6.72) * mm});
            skLineSegment(sketch, "E912", {"start": v(57.6, 6.72) * mm, "end": v(57.6, 6.73) * mm});
            skLineSegment(sketch, "E913", {"start": v(57.6, 6.73) * mm, "end": v(57.6, 6.74) * mm});
            skLineSegment(sketch, "E914", {"start": v(57.6, 6.74) * mm, "end": v(57.61, 6.74) * mm});
            skLineSegment(sketch, "E915", {"start": v(57.61, 6.74) * mm, "end": v(57.62, 6.74) * mm});
            skLineSegment(sketch, "E916", {"start": v(57.62, 6.74) * mm, "end": v(57.62, 6.75) * mm});
            skLineSegment(sketch, "E917", {"start": v(57.62, 6.75) * mm, "end": v(57.63, 6.75) * mm});
            skLineSegment(sketch, "E918", {"start": v(57.63, 6.75) * mm, "end": v(57.64, 6.76) * mm});
            skLineSegment(sketch, "E919", {"start": v(57.64, 6.76) * mm, "end": v(57.65, 6.76) * mm});
            skLineSegment(sketch, "E920", {"start": v(57.65, 6.76) * mm, "end": v(57.67, 6.76) * mm});
            skLineSegment(sketch, "E921", {"start": v(57.67, 6.76) * mm, "end": v(57.7, 6.76) * mm});
            skLineSegment(sketch, "E922", {"start": v(57.7, 6.76) * mm, "end": v(57.73, 6.76) * mm});
            skLineSegment(sketch, "E923", {"start": v(57.73, 6.76) * mm, "end": v(57.77, 6.76) * mm});
            skLineSegment(sketch, "E924", {"start": v(57.77, 6.76) * mm, "end": v(57.73, 6.7) * mm});
            skLineSegment(sketch, "E925", {"start": v(57.73, 6.7) * mm, "end": v(57.72, 6.67) * mm});
            skLineSegment(sketch, "E926", {"start": v(57.72, 6.67) * mm, "end": v(57.72, 6.65) * mm});
            skLineSegment(sketch, "E927", {"start": v(57.72, 6.65) * mm, "end": v(57.72, 6.64) * mm});
            skLineSegment(sketch, "E928", {"start": v(57.72, 6.64) * mm, "end": v(57.72, 6.64) * mm});
            skLineSegment(sketch, "E929", {"start": v(57.72, 6.64) * mm, "end": v(57.72, 6.63) * mm});
            skLineSegment(sketch, "E930", {"start": v(57.72, 6.63) * mm, "end": v(57.72, 6.63) * mm});
            skLineSegment(sketch, "E931", {"start": v(57.72, 6.63) * mm, "end": v(57.73, 6.62) * mm});
            skLineSegment(sketch, "E932", {"start": v(57.73, 6.62) * mm, "end": v(57.73, 6.62) * mm});
            skLineSegment(sketch, "E933", {"start": v(57.73, 6.62) * mm, "end": v(57.74, 6.62) * mm});
            skLineSegment(sketch, "E934", {"start": v(57.74, 6.62) * mm, "end": v(57.76, 6.62) * mm});
            skLineSegment(sketch, "E935", {"start": v(57.76, 6.62) * mm, "end": v(57.81, 6.62) * mm});
            skLineSegment(sketch, "E936", {"start": v(57.81, 6.62) * mm, "end": v(57.83, 6.62) * mm});
            skLineSegment(sketch, "E937", {"start": v(57.83, 6.62) * mm, "end": v(57.85, 6.62) * mm});
            skLineSegment(sketch, "E938", {"start": v(57.85, 6.62) * mm, "end": v(57.86, 6.61) * mm});
            skLineSegment(sketch, "E939", {"start": v(57.86, 6.61) * mm, "end": v(57.87, 6.6) * mm});
            skLineSegment(sketch, "E940", {"start": v(57.87, 6.6) * mm, "end": v(57.88, 6.6) * mm});
            skLineSegment(sketch, "E941", {"start": v(57.88, 6.6) * mm, "end": v(57.89, 6.6) * mm});
            skLineSegment(sketch, "E942", {"start": v(57.89, 6.6) * mm, "end": v(57.9, 6.58) * mm});
            skLineSegment(sketch, "E943", {"start": v(57.9, 6.58) * mm, "end": v(57.88, 6.48) * mm});
            skLineSegment(sketch, "E944", {"start": v(57.88, 6.48) * mm, "end": v(57.85, 6.39) * mm});
            skLineSegment(sketch, "E945", {"start": v(57.85, 6.39) * mm, "end": v(57.82, 6.3) * mm});
            skLineSegment(sketch, "E946", {"start": v(57.82, 6.3) * mm, "end": v(57.76, 6.2) * mm});
            skLineSegment(sketch, "E947", {"start": v(57.76, 6.2) * mm, "end": v(57.67, 6.06) * mm});
            skLineSegment(sketch, "E948", {"start": v(57.67, 6.06) * mm, "end": v(57.42, 5.72) * mm});
            skLineSegment(sketch, "E949", {"start": v(57.42, 5.72) * mm, "end": v(57.37, 5.61) * mm});
            skLineSegment(sketch, "E950", {"start": v(57.37, 5.61) * mm, "end": v(57.34, 5.53) * mm});
            skLineSegment(sketch, "E951", {"start": v(57.34, 5.53) * mm, "end": v(57.31, 5.44) * mm});
            skLineSegment(sketch, "E952", {"start": v(57.31, 5.44) * mm, "end": v(57.3, 5.34) * mm});
            skLineSegment(sketch, "E953", {"start": v(57.3, 5.34) * mm, "end": v(57.28, 5.23) * mm});
            skLineSegment(sketch, "E954", {"start": v(57.28, 5.23) * mm, "end": v(57.36, 5.14) * mm});
            skLineSegment(sketch, "E955", {"start": v(57.36, 5.14) * mm, "end": v(57.6, 4.86) * mm});
            skLineSegment(sketch, "E956", {"start": v(57.6, 4.86) * mm, "end": v(57.66, 4.81) * mm});
            skLineSegment(sketch, "E957", {"start": v(57.66, 4.81) * mm, "end": v(57.7, 4.77) * mm});
            skLineSegment(sketch, "E958", {"start": v(57.7, 4.77) * mm, "end": v(57.76, 4.74) * mm});
            skLineSegment(sketch, "E959", {"start": v(57.76, 4.74) * mm, "end": v(57.82, 4.72) * mm});
            skLineSegment(sketch, "E960", {"start": v(57.82, 4.72) * mm, "end": v(57.88, 4.7) * mm});
            skLineSegment(sketch, "E961", {"start": v(57.88, 4.7) * mm, "end": v(57.95, 4.68) * mm});
            skLineSegment(sketch, "E962", {"start": v(57.95, 4.68) * mm, "end": v(58.03, 4.67) * mm});
            skLineSegment(sketch, "E963", {"start": v(58.03, 4.67) * mm, "end": v(58.08, 4.67) * mm});
            skLineSegment(sketch, "E964", {"start": v(58.08, 4.67) * mm, "end": v(58.14, 4.67) * mm});
            skLineSegment(sketch, "E965", {"start": v(58.14, 4.67) * mm, "end": v(58.14, 4.64) * mm});
            skLineSegment(sketch, "E966", {"start": v(58.14, 4.64) * mm, "end": v(58.14, 4.6) * mm});
            skLineSegment(sketch, "E967", {"start": v(58.14, 4.6) * mm, "end": v(58.14, 4.58) * mm});
            skLineSegment(sketch, "E968", {"start": v(58.14, 4.58) * mm, "end": v(58.14, 4.56) * mm});
            skLineSegment(sketch, "E969", {"start": v(58.14, 4.56) * mm, "end": v(58.15, 4.55) * mm});
            skLineSegment(sketch, "E970", {"start": v(58.15, 4.55) * mm, "end": v(58.15, 4.53) * mm});
            skLineSegment(sketch, "E971", {"start": v(58.15, 4.53) * mm, "end": v(58.16, 4.52) * mm});
            skLineSegment(sketch, "E972", {"start": v(58.16, 4.52) * mm, "end": v(58.17, 4.51) * mm});
            skLineSegment(sketch, "E973", {"start": v(58.17, 4.51) * mm, "end": v(58.18, 4.5) * mm});
            skLineSegment(sketch, "E974", {"start": v(58.18, 4.5) * mm, "end": v(58.19, 4.5) * mm});
            skLineSegment(sketch, "E975", {"start": v(58.19, 4.5) * mm, "end": v(58.2, 4.48) * mm});
            skLineSegment(sketch, "E976", {"start": v(58.2, 4.48) * mm, "end": v(58.22, 4.47) * mm});
            skLineSegment(sketch, "E977", {"start": v(58.22, 4.47) * mm, "end": v(58.24, 4.46) * mm});
            skLineSegment(sketch, "E978", {"start": v(58.24, 4.46) * mm, "end": v(58.27, 4.45) * mm});
            skLineSegment(sketch, "E979", {"start": v(58.27, 4.45) * mm, "end": v(58.32, 4.44) * mm});
            skLineSegment(sketch, "E980", {"start": v(58.32, 4.44) * mm, "end": v(58.39, 4.43) * mm});
            skLineSegment(sketch, "E981", {"start": v(58.39, 4.43) * mm, "end": v(58.4, 4.61) * mm});
            skLineSegment(sketch, "E982", {"start": v(58.4, 4.61) * mm, "end": v(58.37, 4.9) * mm});
            skLineSegment(sketch, "E983", {"start": v(58.37, 4.9) * mm, "end": v(58.33, 5.17) * mm});
            skLineSegment(sketch, "E984", {"start": v(58.33, 5.17) * mm, "end": v(58.34, 5.19) * mm});
            skLineSegment(sketch, "E985", {"start": v(58.34, 5.19) * mm, "end": v(58.36, 5.2) * mm});
            skLineSegment(sketch, "E986", {"start": v(58.36, 5.2) * mm, "end": v(58.38, 5.23) * mm});
            skLineSegment(sketch, "E987", {"start": v(58.38, 5.23) * mm, "end": v(58.4, 5.24) * mm});
            skLineSegment(sketch, "E988", {"start": v(58.4, 5.24) * mm, "end": v(58.45, 5.27) * mm});
            skLineSegment(sketch, "E989", {"start": v(58.45, 5.27) * mm, "end": v(58.52, 5.3) * mm});
            skLineSegment(sketch, "E990", {"start": v(58.52, 5.3) * mm, "end": v(58.62, 5.32) * mm});
            skLineSegment(sketch, "E991", {"start": v(58.62, 5.32) * mm, "end": v(58.74, 5.35) * mm});
            skLineSegment(sketch, "E992", {"start": v(58.74, 5.35) * mm, "end": v(58.88, 5.36) * mm});
            skLineSegment(sketch, "E993", {"start": v(58.88, 5.36) * mm, "end": v(59, 5.37) * mm});
            skLineSegment(sketch, "E994", {"start": v(59, 5.37) * mm, "end": v(59.07, 5.36) * mm});
            skLineSegment(sketch, "E995", {"start": v(59.07, 5.36) * mm, "end": v(59.1, 5.36) * mm});
            skLineSegment(sketch, "E996", {"start": v(59.1, 5.36) * mm, "end": v(59.13, 5.35) * mm});
            skLineSegment(sketch, "E997", {"start": v(59.13, 5.35) * mm, "end": v(59, 5.1) * mm});
            skLineSegment(sketch, "E998", {"start": v(59, 5.1) * mm, "end": v(58.75, 4.72) * mm});
            skLineSegment(sketch, "E999", {"start": v(58.75, 4.72) * mm, "end": v(58.3, 4.05) * mm});
            skLineSegment(sketch, "E1000", {"start": v(58.3, 4.05) * mm, "end": v(58.17, 3.8) * mm});
            skLineSegment(sketch, "E1001", {"start": v(58.17, 3.8) * mm, "end": v(58.09, 3.57) * mm});
            skLineSegment(sketch, "E1002", {"start": v(58.09, 3.57) * mm, "end": v(58.06, 3.47) * mm});
            skLineSegment(sketch, "E1003", {"start": v(58.06, 3.47) * mm, "end": v(58.02, 3.32) * mm});
            skLineSegment(sketch, "E1004", {"start": v(58.02, 3.32) * mm, "end": v(57.96, 3.28) * mm});
            skLineSegment(sketch, "E1005", {"start": v(57.96, 3.28) * mm, "end": v(57.9, 3.23) * mm});
            skLineSegment(sketch, "E1006", {"start": v(57.9, 3.23) * mm, "end": v(57.84, 3.16) * mm});
            skLineSegment(sketch, "E1007", {"start": v(57.84, 3.16) * mm, "end": v(57.78, 3.08) * mm});
            skLineSegment(sketch, "E1008", {"start": v(57.78, 3.08) * mm, "end": v(57.7, 2.96) * mm});
            skLineSegment(sketch, "E1009", {"start": v(57.7, 2.96) * mm, "end": v(57.53, 2.63) * mm});
            skLineSegment(sketch, "E1010", {"start": v(57.53, 2.63) * mm, "end": v(57.34, 2.34) * mm});
            skLineSegment(sketch, "E1011", {"start": v(57.34, 2.34) * mm, "end": v(56.17, 3.18) * mm});
            skLineSegment(sketch, "E1012", {"start": v(56.17, 3.18) * mm, "end": v(56.04, 3.25) * mm});
            skLineSegment(sketch, "E1013", {"start": v(56.04, 3.25) * mm, "end": v(55.87, 3.32) * mm});
            skLineSegment(sketch, "E1014", {"start": v(55.87, 3.32) * mm, "end": v(55.83, 3.31) * mm});
            skLineSegment(sketch, "E1015", {"start": v(55.83, 3.31) * mm, "end": v(55.8, 3.3) * mm});
            skLineSegment(sketch, "E1016", {"start": v(55.8, 3.3) * mm, "end": v(55.77, 3.28) * mm});
            skLineSegment(sketch, "E1017", {"start": v(55.77, 3.28) * mm, "end": v(55.73, 3.26) * mm});
            skLineSegment(sketch, "E1018", {"start": v(55.73, 3.26) * mm, "end": v(55.67, 3.2) * mm});
            skLineSegment(sketch, "E1019", {"start": v(55.67, 3.2) * mm, "end": v(55.56, 3.12) * mm});
            skLineSegment(sketch, "E1020", {"start": v(55.56, 3.12) * mm, "end": v(55.53, 3.1) * mm});
            skLineSegment(sketch, "E1021", {"start": v(55.53, 3.1) * mm, "end": v(55.5, 3.08) * mm});
            skLineSegment(sketch, "E1022", {"start": v(55.5, 3.08) * mm, "end": v(55.53, 1.66) * mm});
            skLineSegment(sketch, "E1023", {"start": v(55.53, 1.66) * mm, "end": v(55.63, 0.31) * mm});
            skLineSegment(sketch, "E1024", {"start": v(55.63, 0.31) * mm, "end": v(55.73, 0.27) * mm});
            skLineSegment(sketch, "E1025", {"start": v(55.73, 0.27) * mm, "end": v(55.82, 0.21) * mm});
            skLineSegment(sketch, "E1026", {"start": v(55.82, 0.21) * mm, "end": v(55.9, 0.15) * mm});
            skLineSegment(sketch, "E1027", {"start": v(55.9, 0.15) * mm, "end": v(55.98, 0.08) * mm});
            skLineSegment(sketch, "E1028", {"start": v(55.98, 0.08) * mm, "end": v(56.05, 0) * mm});
            skLineSegment(sketch, "E1029", {"start": v(56.05, 0) * mm, "end": v(56.12, -0.08) * mm});
            skLineSegment(sketch, "E1030", {"start": v(56.12, -0.08) * mm, "end": v(56.17, -0.17) * mm});
            skLineSegment(sketch, "E1031", {"start": v(56.17, -0.17) * mm, "end": v(56.23, -0.29) * mm});
            skLineSegment(sketch, "E1032", {"start": v(56.23, -0.29) * mm, "end": v(56.26, -0.37) * mm});
            skLineSegment(sketch, "E1033", {"start": v(56.26, -0.37) * mm, "end": v(56.3, -0.49) * mm});
            skLineSegment(sketch, "E1034", {"start": v(56.3, -0.49) * mm, "end": v(56.36, -0.48) * mm});
            skLineSegment(sketch, "E1035", {"start": v(56.36, -0.48) * mm, "end": v(56.42, -0.46) * mm});
            skLineSegment(sketch, "E1036", {"start": v(56.42, -0.46) * mm, "end": v(56.48, -0.43) * mm});
            skLineSegment(sketch, "E1037", {"start": v(56.48, -0.43) * mm, "end": v(56.53, -0.4) * mm});
            skLineSegment(sketch, "E1038", {"start": v(56.53, -0.4) * mm, "end": v(56.57, -0.36) * mm});
            skLineSegment(sketch, "E1039", {"start": v(56.57, -0.36) * mm, "end": v(56.61, -0.31) * mm});
            skLineSegment(sketch, "E1040", {"start": v(56.61, -0.31) * mm, "end": v(56.64, -0.26) * mm});
            skLineSegment(sketch, "E1041", {"start": v(56.64, -0.26) * mm, "end": v(56.68, -0.2) * mm});
            skLineSegment(sketch, "E1042", {"start": v(56.68, -0.2) * mm, "end": v(56.71, -0.11) * mm});
            skLineSegment(sketch, "E1043", {"start": v(56.71, -0.11) * mm, "end": v(56.74, -0.01) * mm});
            skLineSegment(sketch, "E1044", {"start": v(56.74, -0.01) * mm, "end": v(56.76, 0.1) * mm});
            skLineSegment(sketch, "E1045", {"start": v(56.76, 0.1) * mm, "end": v(56.76, 0.2) * mm});
            skLineSegment(sketch, "E1046", {"start": v(56.76, 0.2) * mm, "end": v(56.76, 0.3) * mm});
            skLineSegment(sketch, "E1047", {"start": v(56.76, 0.3) * mm, "end": v(56.75, 0.4) * mm});
            skLineSegment(sketch, "E1048", {"start": v(56.75, 0.4) * mm, "end": v(56.73, 0.5) * mm});
            skLineSegment(sketch, "E1049", {"start": v(56.73, 0.5) * mm, "end": v(56.7, 0.6) * mm});
            skLineSegment(sketch, "E1050", {"start": v(56.7, 0.6) * mm, "end": v(56.68, 0.64) * mm});
            skLineSegment(sketch, "E1051", {"start": v(56.68, 0.64) * mm, "end": v(56.65, 0.7) * mm});
            skLineSegment(sketch, "E1052", {"start": v(56.65, 0.7) * mm, "end": v(56.62, 0.74) * mm});
            skLineSegment(sketch, "E1053", {"start": v(56.62, 0.74) * mm, "end": v(56.58, 0.77) * mm});
            skLineSegment(sketch, "E1054", {"start": v(56.58, 0.77) * mm, "end": v(56.55, 0.8) * mm});
            skLineSegment(sketch, "E1055", {"start": v(56.55, 0.8) * mm, "end": v(56.6, 0.81) * mm});
            skLineSegment(sketch, "E1056", {"start": v(56.6, 0.81) * mm, "end": v(56.65, 0.82) * mm});
            skLineSegment(sketch, "E1057", {"start": v(56.65, 0.82) * mm, "end": v(56.68, 0.83) * mm});
            skLineSegment(sketch, "E1058", {"start": v(56.68, 0.83) * mm, "end": v(56.7, 0.84) * mm});
            skLineSegment(sketch, "E1059", {"start": v(56.7, 0.84) * mm, "end": v(56.73, 0.85) * mm});
            skLineSegment(sketch, "E1060", {"start": v(56.73, 0.85) * mm, "end": v(56.74, 0.87) * mm});
            skLineSegment(sketch, "E1061", {"start": v(56.74, 0.87) * mm, "end": v(56.76, 0.88) * mm});
            skLineSegment(sketch, "E1062", {"start": v(56.76, 0.88) * mm, "end": v(56.77, 0.9) * mm});
            skLineSegment(sketch, "E1063", {"start": v(56.77, 0.9) * mm, "end": v(56.78, 0.9) * mm});
            skLineSegment(sketch, "E1064", {"start": v(56.78, 0.9) * mm, "end": v(56.78, 0.91) * mm});
            skLineSegment(sketch, "E1065", {"start": v(56.78, 0.91) * mm, "end": v(56.8, 0.93) * mm});
            skLineSegment(sketch, "E1066", {"start": v(56.8, 0.93) * mm, "end": v(56.72, 0.96) * mm});
            skLineSegment(sketch, "E1067", {"start": v(56.72, 0.96) * mm, "end": v(56.67, 1) * mm});
            skLineSegment(sketch, "E1068", {"start": v(56.67, 1) * mm, "end": v(56.64, 1.02) * mm});
            skLineSegment(sketch, "E1069", {"start": v(56.64, 1.02) * mm, "end": v(56.62, 1.04) * mm});
            skLineSegment(sketch, "E1070", {"start": v(56.62, 1.04) * mm, "end": v(56.6, 1.06) * mm});
            skLineSegment(sketch, "E1071", {"start": v(56.6, 1.06) * mm, "end": v(56.58, 1.09) * mm});
            skLineSegment(sketch, "E1072", {"start": v(56.58, 1.09) * mm, "end": v(56.57, 1.1) * mm});
            skLineSegment(sketch, "E1073", {"start": v(56.57, 1.1) * mm, "end": v(56.57, 1.12) * mm});
            skLineSegment(sketch, "E1074", {"start": v(56.57, 1.12) * mm, "end": v(56.56, 1.14) * mm});
            skLineSegment(sketch, "E1075", {"start": v(56.56, 1.14) * mm, "end": v(56.56, 1.16) * mm});
            skLineSegment(sketch, "E1076", {"start": v(56.56, 1.16) * mm, "end": v(56.56, 1.18) * mm});
            skLineSegment(sketch, "E1077", {"start": v(56.56, 1.18) * mm, "end": v(56.56, 1.2) * mm});
            skLineSegment(sketch, "E1078", {"start": v(56.56, 1.2) * mm, "end": v(56.56, 1.22) * mm});
            skLineSegment(sketch, "E1079", {"start": v(56.56, 1.22) * mm, "end": v(56.56, 1.25) * mm});
            skLineSegment(sketch, "E1080", {"start": v(56.56, 1.25) * mm, "end": v(56.58, 1.3) * mm});
            skLineSegment(sketch, "E1081", {"start": v(56.58, 1.3) * mm, "end": v(56.59, 1.32) * mm});
            skLineSegment(sketch, "E1082", {"start": v(56.59, 1.32) * mm, "end": v(56.6, 1.36) * mm});
            skLineSegment(sketch, "E1083", {"start": v(56.6, 1.36) * mm, "end": v(56.55, 1.35) * mm});
            skLineSegment(sketch, "E1084", {"start": v(56.55, 1.35) * mm, "end": v(56.5, 1.35) * mm});
            skLineSegment(sketch, "E1085", {"start": v(56.5, 1.35) * mm, "end": v(56.45, 1.35) * mm});
            skLineSegment(sketch, "E1086", {"start": v(56.45, 1.35) * mm, "end": v(56.4, 1.36) * mm});
            skLineSegment(sketch, "E1087", {"start": v(56.4, 1.36) * mm, "end": v(56.36, 1.38) * mm});
            skLineSegment(sketch, "E1088", {"start": v(56.36, 1.38) * mm, "end": v(56.32, 1.4) * mm});
            skLineSegment(sketch, "E1089", {"start": v(56.32, 1.4) * mm, "end": v(56.28, 1.41) * mm});
            skLineSegment(sketch, "E1090", {"start": v(56.28, 1.41) * mm, "end": v(56.24, 1.44) * mm});
            skLineSegment(sketch, "E1091", {"start": v(56.24, 1.44) * mm, "end": v(56.21, 1.47) * mm});
            skLineSegment(sketch, "E1092", {"start": v(56.21, 1.47) * mm, "end": v(56.18, 1.5) * mm});
            skLineSegment(sketch, "E1093", {"start": v(56.18, 1.5) * mm, "end": v(56.15, 1.53) * mm});
            skLineSegment(sketch, "E1094", {"start": v(56.15, 1.53) * mm, "end": v(56.13, 1.57) * mm});
            skLineSegment(sketch, "E1095", {"start": v(56.13, 1.57) * mm, "end": v(56.1, 1.63) * mm});
            skLineSegment(sketch, "E1096", {"start": v(56.1, 1.63) * mm, "end": v(56.07, 1.7) * mm});
            skLineSegment(sketch, "E1097", {"start": v(56.07, 1.7) * mm, "end": v(56.06, 1.76) * mm});
            skLineSegment(sketch, "E1098", {"start": v(56.06, 1.76) * mm, "end": v(56.05, 1.83) * mm});
            skLineSegment(sketch, "E1099", {"start": v(56.05, 1.83) * mm, "end": v(56.05, 1.9) * mm});
            skLineSegment(sketch, "E1100", {"start": v(56.05, 1.9) * mm, "end": v(56.06, 1.97) * mm});
            skLineSegment(sketch, "E1101", {"start": v(56.06, 1.97) * mm, "end": v(56.07, 2.04) * mm});
            skLineSegment(sketch, "E1102", {"start": v(56.07, 2.04) * mm, "end": v(56.09, 2.09) * mm});
            skLineSegment(sketch, "E1103", {"start": v(56.09, 2.09) * mm, "end": v(56.12, 2.16) * mm});
            skLineSegment(sketch, "E1104", {"start": v(56.12, 2.16) * mm, "end": v(56.17, 2.13) * mm});
            skLineSegment(sketch, "E1105", {"start": v(56.17, 2.13) * mm, "end": v(56.21, 2.1) * mm});
            skLineSegment(sketch, "E1106", {"start": v(56.21, 2.1) * mm, "end": v(56.28, 2.06) * mm});
            skLineSegment(sketch, "E1107", {"start": v(56.28, 2.06) * mm, "end": v(56.35, 2) * mm});
            skLineSegment(sketch, "E1108", {"start": v(56.35, 2) * mm, "end": v(56.44, 1.9) * mm});
            skLineSegment(sketch, "E1109", {"start": v(56.44, 1.9) * mm, "end": v(56.54, 1.76) * mm});
            skLineSegment(sketch, "E1110", {"start": v(56.54, 1.76) * mm, "end": v(56.65, 1.58) * mm});
            skLineSegment(sketch, "E1111", {"start": v(56.65, 1.58) * mm, "end": v(56.73, 1.42) * mm});
            skLineSegment(sketch, "E1112", {"start": v(56.73, 1.42) * mm, "end": v(56.74, 1.4) * mm});
            skLineSegment(sketch, "E1113", {"start": v(56.74, 1.4) * mm, "end": v(56.75, 1.4) * mm});
            skLineSegment(sketch, "E1114", {"start": v(56.75, 1.4) * mm, "end": v(56.76, 1.37) * mm});
            skLineSegment(sketch, "E1115", {"start": v(56.76, 1.37) * mm, "end": v(56.8, 1.34) * mm});
            skLineSegment(sketch, "E1116", {"start": v(56.8, 1.34) * mm, "end": v(56.9, 1.25) * mm});
            skLineSegment(sketch, "E1117", {"start": v(56.9, 1.25) * mm, "end": v(56.98, 1.17) * mm});
            skLineSegment(sketch, "E1118", {"start": v(56.98, 1.17) * mm, "end": v(57.06, 1.04) * mm});
            skLineSegment(sketch, "E1119", {"start": v(57.06, 1.04) * mm, "end": v(57.12, 0.92) * mm});
            skLineSegment(sketch, "E1120", {"start": v(57.12, 0.92) * mm, "end": v(57.16, 0.82) * mm});
            skLineSegment(sketch, "E1121", {"start": v(57.16, 0.82) * mm, "end": v(57.2, 0.71) * mm});
            skLineSegment(sketch, "E1122", {"start": v(57.2, 0.71) * mm, "end": v(57.22, 0.59) * mm});
            skLineSegment(sketch, "E1123", {"start": v(57.22, 0.59) * mm, "end": v(57.23, 0.44) * mm});
            skLineSegment(sketch, "E1124", {"start": v(57.23, 0.44) * mm, "end": v(57.23, 0.27) * mm});
            skLineSegment(sketch, "E1125", {"start": v(57.23, 0.27) * mm, "end": v(57.22, 0.07) * mm});
            skLineSegment(sketch, "E1126", {"start": v(57.22, 0.07) * mm, "end": v(57.22, -0.42) * mm});
            skLineSegment(sketch, "E1127", {"start": v(57.22, -0.42) * mm, "end": v(57.33, -0.46) * mm});
            skLineSegment(sketch, "E1128", {"start": v(57.33, -0.46) * mm, "end": v(57.44, -0.5) * mm});
            skLineSegment(sketch, "E1129", {"start": v(57.44, -0.5) * mm, "end": v(57.55, -0.57) * mm});
            skLineSegment(sketch, "E1130", {"start": v(57.55, -0.57) * mm, "end": v(57.74, -0.7) * mm});
            skLineSegment(sketch, "E1131", {"start": v(57.74, -0.7) * mm, "end": v(57.92, -0.84) * mm});
            skLineSegment(sketch, "E1132", {"start": v(57.92, -0.84) * mm, "end": v(58.14, -0.98) * mm});
            skLineSegment(sketch, "E1133", {"start": v(58.14, -0.98) * mm, "end": v(58.2, -0.9) * mm});
            skLineSegment(sketch, "E1134", {"start": v(58.2, -0.9) * mm, "end": v(58.23, -0.82) * mm});
            skLineSegment(sketch, "E1135", {"start": v(58.23, -0.82) * mm, "end": v(58.25, -0.74) * mm});
            skLineSegment(sketch, "E1136", {"start": v(58.25, -0.74) * mm, "end": v(58.27, -0.67) * mm});
            skLineSegment(sketch, "E1137", {"start": v(58.27, -0.67) * mm, "end": v(58.27, -0.6) * mm});
            skLineSegment(sketch, "E1138", {"start": v(58.27, -0.6) * mm, "end": v(58.27, -0.52) * mm});
            skLineSegment(sketch, "E1139", {"start": v(58.27, -0.52) * mm, "end": v(58.26, -0.45) * mm});
            skLineSegment(sketch, "E1140", {"start": v(58.26, -0.45) * mm, "end": v(58.23, -0.34) * mm});
            skLineSegment(sketch, "E1141", {"start": v(58.23, -0.34) * mm, "end": v(58.19, -0.24) * mm});
            skLineSegment(sketch, "E1142", {"start": v(58.19, -0.24) * mm, "end": v(58.1, -0.07) * mm});
            skLineSegment(sketch, "E1143", {"start": v(58.1, -0.07) * mm, "end": v(57.88, 0.36) * mm});
            skLineSegment(sketch, "E1144", {"start": v(57.88, 0.36) * mm, "end": v(57.85, 0.45) * mm});
            skLineSegment(sketch, "E1145", {"start": v(57.85, 0.45) * mm, "end": v(57.83, 0.52) * mm});
            skLineSegment(sketch, "E1146", {"start": v(57.83, 0.52) * mm, "end": v(57.82, 0.58) * mm});
            skLineSegment(sketch, "E1147", {"start": v(57.82, 0.58) * mm, "end": v(57.82, 0.65) * mm});
            skLineSegment(sketch, "E1148", {"start": v(57.82, 0.65) * mm, "end": v(57.82, 0.68) * mm});
            skLineSegment(sketch, "E1149", {"start": v(57.82, 0.68) * mm, "end": v(57.84, 0.74) * mm});
            skLineSegment(sketch, "E1150", {"start": v(57.84, 0.74) * mm, "end": v(57.9, 0.58) * mm});
            skLineSegment(sketch, "E1151", {"start": v(57.9, 0.58) * mm, "end": v(58.01, 0.35) * mm});
            skLineSegment(sketch, "E1152", {"start": v(58.01, 0.35) * mm, "end": v(58.14, 0.13) * mm});
            skLineSegment(sketch, "E1153", {"start": v(58.14, 0.13) * mm, "end": v(58.36, -0.2) * mm});
            skLineSegment(sketch, "E1154", {"start": v(58.36, -0.2) * mm, "end": v(58.47, -0.33) * mm});
            skLineSegment(sketch, "E1155", {"start": v(58.47, -0.33) * mm, "end": v(58.52, -0.38) * mm});
            skLineSegment(sketch, "E1156", {"start": v(58.52, -0.38) * mm, "end": v(58.57, -0.42) * mm});
            skLineSegment(sketch, "E1157", {"start": v(58.57, -0.42) * mm, "end": v(58.66, -0.5) * mm});
            skLineSegment(sketch, "E1158", {"start": v(58.66, -0.5) * mm, "end": v(58.78, -0.57) * mm});
            skLineSegment(sketch, "E1159", {"start": v(58.78, -0.57) * mm, "end": v(59.1, -0.72) * mm});
            skLineSegment(sketch, "E1160", {"start": v(59.1, -0.72) * mm, "end": v(59.43, -0.85) * mm});
            skLineSegment(sketch, "E1161", {"start": v(59.43, -0.85) * mm, "end": v(60.1, -1.08) * mm});
            skLineSegment(sketch, "E1162", {"start": v(60.1, -1.08) * mm, "end": v(60.18, -1.13) * mm});
            skLineSegment(sketch, "E1163", {"start": v(60.18, -1.13) * mm, "end": v(60.25, -1.18) * mm});
            skLineSegment(sketch, "E1164", {"start": v(60.25, -1.18) * mm, "end": v(60.3, -1.22) * mm});
            skLineSegment(sketch, "E1165", {"start": v(60.3, -1.22) * mm, "end": v(60.35, -1.28) * mm});
            skLineSegment(sketch, "E1166", {"start": v(60.35, -1.28) * mm, "end": v(60.33, -1.6) * mm});
            skLineSegment(sketch, "E1167", {"start": v(60.33, -1.6) * mm, "end": v(60.22, -2.4) * mm});
            skLineSegment(sketch, "E1168", {"start": v(60.22, -2.4) * mm, "end": v(60.22, -2.55) * mm});
            skLineSegment(sketch, "E1169", {"start": v(60.22, -2.55) * mm, "end": v(60.23, -2.7) * mm});
            skLineSegment(sketch, "E1170", {"start": v(60.23, -2.7) * mm, "end": v(60.25, -2.78) * mm});
            skLineSegment(sketch, "E1171", {"start": v(60.25, -2.78) * mm, "end": v(60.28, -2.9) * mm});
            skLineSegment(sketch, "E1172", {"start": v(60.28, -2.9) * mm, "end": v(60.41, -3.24) * mm});
            skLineSegment(sketch, "E1173", {"start": v(60.41, -3.24) * mm, "end": v(60.54, -3.56) * mm});
            skLineSegment(sketch, "E1174", {"start": v(60.54, -3.56) * mm, "end": v(60.76, -4.26) * mm});
            skLineSegment(sketch, "E1175", {"start": v(60.76, -4.26) * mm, "end": v(60.78, -4.38) * mm});
            skLineSegment(sketch, "E1176", {"start": v(60.78, -4.38) * mm, "end": v(60.78, -4.42) * mm});
            skLineSegment(sketch, "E1177", {"start": v(60.78, -4.42) * mm, "end": v(60.78, -4.48) * mm});
            skLineSegment(sketch, "E1178", {"start": v(60.78, -4.48) * mm, "end": v(60.78, -4.52) * mm});
            skLineSegment(sketch, "E1179", {"start": v(60.78, -4.52) * mm, "end": v(60.76, -4.6) * mm});
            skLineSegment(sketch, "E1180", {"start": v(60.76, -4.6) * mm, "end": v(60.72, -4.72) * mm});
            skLineSegment(sketch, "E1181", {"start": v(60.72, -4.72) * mm, "end": v(60.66, -4.86) * mm});
            skLineSegment(sketch, "E1182", {"start": v(60.66, -4.86) * mm, "end": v(60.63, -4.92) * mm});
            skLineSegment(sketch, "E1183", {"start": v(60.63, -4.92) * mm, "end": v(60.6, -4.97) * mm});
            skLineSegment(sketch, "E1184", {"start": v(60.6, -4.97) * mm, "end": v(60.55, -5.03) * mm});
            skLineSegment(sketch, "E1185", {"start": v(60.55, -5.03) * mm, "end": v(60.47, -5.12) * mm});
            skLineSegment(sketch, "E1186", {"start": v(60.47, -5.12) * mm, "end": v(60.36, -5.22) * mm});
            skLineSegment(sketch, "E1187", {"start": v(60.36, -5.22) * mm, "end": v(60.16, -5.37) * mm});
            skLineSegment(sketch, "E1188", {"start": v(60.16, -5.37) * mm, "end": v(59.55, -5.78) * mm});
            skLineSegment(sketch, "E1189", {"start": v(59.55, -5.78) * mm, "end": v(59.49, -5.84) * mm});
            skLineSegment(sketch, "E1190", {"start": v(59.49, -5.84) * mm, "end": v(59.43, -5.89) * mm});
            skLineSegment(sketch, "E1191", {"start": v(59.43, -5.89) * mm, "end": v(59.42, -6) * mm});
            skLineSegment(sketch, "E1192", {"start": v(59.42, -6) * mm, "end": v(59.39, -6.12) * mm});
            skLineSegment(sketch, "E1193", {"start": v(59.39, -6.12) * mm, "end": v(59.34, -6.26) * mm});
            skLineSegment(sketch, "E1194", {"start": v(59.34, -6.26) * mm, "end": v(59.23, -6.52) * mm});
            skLineSegment(sketch, "E1195", {"start": v(59.23, -6.52) * mm, "end": v(59.13, -6.81) * mm});
            skSolve(sketch);
        }
        {
            var Q0;
            Q0=makeQuery(id+"F10.imprint","IMPRINT",FACE,{"disambiguationData":[TD([[makeQuery(id+"F10.imprint","IMPRINT",EDGE,{"derivedFrom":sQuery(id+"F10.wireOp",EDGE,"E145")}),1.0]])]});
            var Q1;
            Q1=sQuery(id+"F10.wireOp",EDGE,"8e4e5431-f8d2-4023-bee8-b95039230f97");
            var Q2;
            Q2=sQuery(id+"F10.wireOp",EDGE,"ab72fa93-f650-4509-ac39-0ba806a802c3");
            var Q3;
            Q3=sQuery(id+"F10.wireOp",EDGE,"5d2e7a00-d2c2-4943-82e7-4c8edd39c4cb");
            var Q4;
            Q4=sQuery(id+"F10.wireOp",EDGE,"d968dc84-f706-4830-9098-9e71a2a2a60e");
            var Q5;
            Q5=sQuery(id+"F10.wireOp",EDGE,"adc0322b-878a-4190-a961-88d0935b0660");
            var Q6;
            Q6=sQuery(id+"F10.wireOp",EDGE,"0e7581b4-b756-45fc-9b37-be6843159f94");
            var Q7;
            Q7=sQuery(id+"F10.wireOp",EDGE,"872ca489-3ef3-4481-a2d8-15d1c51bd90b");
            var Q8;
            Q8=sQuery(id+"F10.wireOp",EDGE,"05e501d0-bc73-4acf-8a99-4546b8ad142f");
            var Q9;
            Q9=sQuery(id+"F10.wireOp",EDGE,"3cec0d86-5d45-43ce-b60b-efd9a6d69a5a");
            var Q10;
            Q10=sQuery(id+"F10.wireOp",EDGE,"333f57c5-1dc9-4cee-88d1-507dcf75618c");
            var Q11;
            Q11=sQuery(id+"F10.wireOp",EDGE,"41789a6e-0bb8-41f5-ae9a-325a359c9ba1");
            var Q12;
            Q12=sQuery(id+"F10.wireOp",EDGE,"c7a9d51f-852c-47c6-bbc3-3ad18ec7f413");
            var Q13;
            Q13=sQuery(id+"F10.wireOp",EDGE,"53cad540-78ac-479d-87ef-069fe5849c7e");
            var Q14;
            Q14=sQuery(id+"F10.wireOp",EDGE,"4f748325-43bf-4a79-9f2c-453bdb2e8d04");
            var Q15;
            Q15=sQuery(id+"F10.wireOp",EDGE,"80e42732-c1a3-4011-806f-fab01faeac49");
            var Q16;
            Q16=sQuery(id+"F10.wireOp",EDGE,"540a2608-c707-4028-abc5-a3cdbf899040");
            var Q17;
            Q17=sQuery(id+"F10.wireOp",EDGE,"c901a314-a0b1-4305-8a6d-ba4c44a41dad");
            var Q18;
            Q18=sQuery(id+"F10.wireOp",EDGE,"747ba557-2df8-4450-9e39-173084c475dc");
            var Q19;
            Q19=sQuery(id+"F10.wireOp",EDGE,"e704e5fe-c659-4ab7-b0bd-e81cfb20a1aa");
            var Q20;
            Q20=sQuery(id+"F10.wireOp",EDGE,"771351dd-ebb4-433c-82bb-0a2f5a09a761");
            var Q21;
            Q21=sQuery(id+"F10.wireOp",EDGE,"b3d7c7d0-f799-41b9-b137-0f30f89db80f");
            var Q22;
            Q22=sQuery(id+"F10.wireOp",EDGE,"f70cc862-8381-4b29-9f98-5f1c955f15ea");
            var Q23;
            Q23=sQuery(id+"F10.wireOp",EDGE,"ddc90e05-4ebf-41b4-9c78-a38d3836cac9");
            var Q24;
            Q24=sQuery(id+"F10.wireOp",EDGE,"2286e44a-e15b-487d-b206-34e6be17992b");
            var Q25;
            Q25=sQuery(id+"F10.wireOp",EDGE,"ecf1efde-72e6-4029-abb1-3af63ddc83b6");
            var Q26;
            Q26=sQuery(id+"F10.wireOp",EDGE,"859345e8-0000-43ee-a01a-5d281e56bc84");
            var Q27;
            Q27=sQuery(id+"F10.wireOp",EDGE,"7133f735-2c2a-4bf2-869e-e52457fc8506");
            var Q28;
            Q28=sQuery(id+"F10.wireOp",EDGE,"8c1121ce-8f17-45ce-9840-3f93d3e384c0");
            var Q29;
            Q29=sQuery(id+"F10.wireOp",EDGE,"6822f5d9-39ab-4b21-b631-57b945214bd9");
            var Q30;
            Q30=sQuery(id+"F10.wireOp",EDGE,"e4bf4873-92e7-4184-83ad-42399ced9a52");
            var Q31;
            Q31=sQuery(id+"F10.wireOp",EDGE,"1f4b7e6a-9402-4acf-a2b5-474194112e71");
            var Q32;
            Q32=sQuery(id+"F10.wireOp",EDGE,"a635440b-1e59-47f5-82f0-770e72fc72f8");
            var Q33;
            Q33=sQuery(id+"F10.wireOp",EDGE,"da865da9-e1ea-4b24-b354-4a9b052335ca");
            var Q34;
            Q34=sQuery(id+"F10.wireOp",EDGE,"c1a7a7e4-6e07-4a3a-9456-95d5e6b36e5d");
            var Q35;
            Q35=sQuery(id+"F10.wireOp",EDGE,"bd0f6de0-2f41-437c-acba-cacd5b54fdd9");
            var Q36;
            Q36=sQuery(id+"F10.wireOp",EDGE,"4829f5d4-eb10-49ae-94c0-45313b92bbc0");
            var Q37;
            Q37=sQuery(id+"F10.wireOp",EDGE,"1256b4a6-a41b-44d4-908a-052cba6ff704");
            var Q38;
            Q38=sQuery(id+"F10.wireOp",EDGE,"49b54d45-e4ec-4cc0-8638-c4932b677709");
            var Q39;
            Q39=sQuery(id+"F10.wireOp",EDGE,"9a4702de-283e-49b6-a0c6-f9e28f472279");
            var Q40;
            Q40=sQuery(id+"F10.wireOp",EDGE,"362212b9-132a-4a19-8706-0bb9b06c6703");
            var Q41;
            Q41=sQuery(id+"F10.wireOp",EDGE,"e860148f-0e36-4989-8c0f-d29b0c0da08e");
            var Q42;
            Q42=sQuery(id+"F10.wireOp",EDGE,"15c5c5c1-4ea5-4200-a0b9-a7cf0adfdbb4");
            var Q43;
            Q43=sQuery(id+"F10.wireOp",EDGE,"93e3ac35-a3df-42f2-806f-7a66388cc4d2");
            var Q44;
            Q44=sQuery(id+"F10.wireOp",EDGE,"c9337dcd-4292-4be2-9ad8-dfab00d9c7ab");
            var Q45;
            Q45=sQuery(id+"F10.wireOp",EDGE,"465d7a40-e906-4674-b980-e08c829995c2");
            var Q46;
            Q46=sQuery(id+"F10.wireOp",EDGE,"bbc6056a-c67d-461f-a608-9f48f56e241d");
            var Q47;
            Q47=sQuery(id+"F10.wireOp",EDGE,"62148e4a-db8c-4cfb-9a55-87dccfd902ef");
            var Q48;
            Q48=sQuery(id+"F10.wireOp",EDGE,"dcd0120a-b709-4abd-8bb6-949866050a87");
            var Q49;
            Q49=sQuery(id+"F10.wireOp",EDGE,"1aa76a1e-0b1f-4f0c-89ab-f6031d2bab15");
            var Q50;
            Q50=sQuery(id+"F10.wireOp",EDGE,"1af50b88-ef53-4302-833d-f8b6bc233df2");
            var Q51;
            Q51=sQuery(id+"F10.wireOp",EDGE,"7d1d5136-c233-4f18-8e53-2afcf1cf18f1");
            var Q52;
            Q52=sQuery(id+"F10.wireOp",EDGE,"5d989545-deb0-4df7-a7ca-958f89815fba");
            var Q53;
            Q53=sQuery(id+"F10.wireOp",EDGE,"def644b2-3144-4a55-9adb-edb23288e5bc");
            var Q54;
            Q54=sQuery(id+"F10.wireOp",EDGE,"7f45f4cf-c448-4340-8326-c93af037868a");
            var Q55;
            Q55=sQuery(id+"F10.wireOp",EDGE,"b75f04e2-f7df-44d8-9112-2a2bfc8f97fd");
            var Q56;
            Q56=sQuery(id+"F10.wireOp",EDGE,"7496e540-2947-4971-af14-463123bd32de");
            var Q57;
            Q57=sQuery(id+"F10.wireOp",EDGE,"36fb7368-6702-4131-91e6-f28674ad2f9e");
            var Q58;
            Q58=sQuery(id+"F10.wireOp",EDGE,"5ea34a65-9529-4e34-b46e-9ede96d20ef2");
            var Q59;
            Q59=sQuery(id+"F10.wireOp",EDGE,"af786843-99ac-42cc-a5de-cc6555baf7fe");
            var Q60;
            Q60=sQuery(id+"F10.wireOp",EDGE,"63d0d69e-e67d-4a42-a483-4697770cd02e");
            var Q61;
            Q61=sQuery(id+"F10.wireOp",EDGE,"801f5fd5-5193-4fc6-9d95-5cf1ec6b917e");
            var Q62;
            Q62=sQuery(id+"F10.wireOp",EDGE,"dc60a863-6383-4dcc-bb79-d9fb9e29e59a");
            var Q63;
            Q63=sQuery(id+"F10.wireOp",EDGE,"06213f49-a35d-47dc-8d20-29493abd8a44");
            var Q64;
            Q64=sQuery(id+"F10.wireOp",EDGE,"fdc7bd6d-5b95-43ea-8489-3cc0c5b1cb8f");
            var Q65;
            Q65=sQuery(id+"F10.wireOp",EDGE,"167d71c4-c801-4a36-874c-eba8d89a4e9c");
            var Q66;
            Q66=sQuery(id+"F10.wireOp",EDGE,"b17c9adc-8b5e-416d-a6ee-419ce2417faf");
            var Q67;
            Q67=sQuery(id+"F10.wireOp",EDGE,"b3e8bf2a-caa8-4cae-b91a-e252a554e4b2");
            var Q68;
            Q68=sQuery(id+"F10.wireOp",EDGE,"8b307e6c-b7ec-4ddd-b5b7-5718b4b01d22");
            var Q69;
            Q69=sQuery(id+"F10.wireOp",EDGE,"d1d138f3-a35e-4bab-ab8f-9da51a903f6c");
            var Q70;
            Q70=sQuery(id+"F10.wireOp",EDGE,"6906728f-2b21-425f-b5b4-4f4c7bd0e452");
            var Q71;
            Q71=sQuery(id+"F10.wireOp",EDGE,"7961dc34-8381-4476-9c3c-9cfbfb3fc3e9");
            var Q72;
            Q72=sQuery(id+"F10.wireOp",EDGE,"8bdb1d70-e543-49ce-8066-2739fb9c41ed");
            var Q73;
            Q73=sQuery(id+"F10.wireOp",EDGE,"4fc12161-1949-4bfb-b348-101ab7cc1331");
            var Q74;
            Q74=sQuery(id+"F10.wireOp",EDGE,"e8a0f6d2-2e2d-4d3b-9765-e252bbff16b0");
            var Q75;
            Q75=sQuery(id+"F10.wireOp",EDGE,"e32151ff-2fd4-42e8-a85c-7714f6f8be1b");
            var Q76;
            Q76=sQuery(id+"F10.wireOp",EDGE,"a5710c31-5450-4be6-bfc9-ca40c8cb1581");
            var Q77;
            Q77=sQuery(id+"F10.wireOp",EDGE,"9932f6cd-d8d4-4cb4-bd57-465ab2729135");
            var Q78;
            Q78=sQuery(id+"F10.wireOp",EDGE,"424c79f2-c4a6-4150-a711-495e4acff88e");
            var Q79;
            Q79=sQuery(id+"F10.wireOp",EDGE,"5834b6eb-c1ed-4fb3-a100-05dc2ad4d203");
            var Q80;
            Q80=sQuery(id+"F10.wireOp",EDGE,"9e81256c-863c-49f1-b3e2-d1da7b0ee2a4");
            var Q81;
            Q81=sQuery(id+"F10.wireOp",EDGE,"0690bb8e-710e-4a7b-b886-fbbe730fb5af");
            var Q82;
            Q82=sQuery(id+"F10.wireOp",EDGE,"4e19d80c-979f-4865-872c-3f15c1acfaab");
            var Q83;
            Q83=sQuery(id+"F10.wireOp",EDGE,"d111022e-d9aa-4b87-b3b1-a30a169ec3c3");
            var Q84;
            Q84=sQuery(id+"F10.wireOp",EDGE,"c81f3d32-dda4-4215-aaa1-b8e753175237");
            var Q85;
            Q85=sQuery(id+"F10.wireOp",EDGE,"783faa28-b73b-4fe4-93bf-6d977c636946");
            var Q86;
            Q86=sQuery(id+"F10.wireOp",EDGE,"425f1696-9423-4919-ae23-f874082948e8");
            var Q87;
            Q87=sQuery(id+"F10.wireOp",EDGE,"a7674ac2-0c4a-4899-95d2-af5af0f01331");
            var Q88;
            Q88=sQuery(id+"F10.wireOp",EDGE,"adc5fe5e-21a4-48ba-b540-5fdcaa80fc2e");
            var Q89;
            Q89=sQuery(id+"F10.wireOp",EDGE,"e3d32dd6-1282-41c6-b482-bdd502d7e8e3");
            var Q90;
            Q90=sQuery(id+"F10.wireOp",EDGE,"1d79bf30-f4e2-46ff-8589-c7637c90ca8e");
            var Q91;
            Q91=sQuery(id+"F10.wireOp",EDGE,"6869e9b2-a25e-4e53-bcd8-866756cd547d");
            var Q92;
            Q92=sQuery(id+"F10.wireOp",EDGE,"7cde27e3-0c8a-433e-9dce-c1825596bdc1");
            var Q93;
            Q93=sQuery(id+"F10.wireOp",EDGE,"d124b733-b52f-448d-8465-d3d1446c08ad");
            var Q94;
            Q94=sQuery(id+"F10.wireOp",EDGE,"d4eef421-5af4-47e1-9591-3a32616117ad");
            var Q95;
            Q95=sQuery(id+"F10.wireOp",EDGE,"09bbea71-1eed-4fae-9de6-56c898a2824a");
            var Q96;
            Q96=sQuery(id+"F10.wireOp",EDGE,"0ad23445-4993-485f-be41-5853c68f9add");
            var Q97;
            Q97=sQuery(id+"F10.wireOp",EDGE,"28bfbc76-301d-418c-a8d7-7eef57d6606a");
            var Q98;
            Q98=sQuery(id+"F10.wireOp",EDGE,"adfeb4ad-03a3-49de-b64b-cb6ecb8a4a0c");
            var Q99;
            Q99=sQuery(id+"F10.wireOp",EDGE,"0948c2e0-31bc-4f89-8d69-7a0332ff2310");
            var Q100;
            Q100=sQuery(id+"F10.wireOp",EDGE,"e132f9a6-6db1-406a-a19a-84b3f290ae47");
            var Q101;
            Q101=sQuery(id+"F10.wireOp",EDGE,"c394e027-42cf-45f3-b150-be49d81c8938");
            var Q102;
            Q102=sQuery(id+"F10.wireOp",EDGE,"dc8c3157-b07c-4465-8590-d5f1cc2d8d76");
            var Q103;
            Q103=sQuery(id+"F10.wireOp",EDGE,"749ed87b-479e-4971-9984-371c755362c2");
            var Q104;
            Q104=sQuery(id+"F10.wireOp",EDGE,"50cb4559-859f-4b43-a9a7-eb72ee1dc82d");
            var Q105;
            Q105=sQuery(id+"F10.wireOp",EDGE,"249d6574-bc11-48c0-991c-357709547216");
            var Q106;
            Q106=sQuery(id+"F10.wireOp",EDGE,"2d3feac5-6682-47f6-8b99-efb20688d24f");
            var Q107;
            Q107=sQuery(id+"F10.wireOp",EDGE,"90623c3d-53f9-4fd5-86de-ff987234d853");
            var Q108;
            Q108=sQuery(id+"F10.wireOp",EDGE,"c3e57d6f-8bb4-4f77-bf76-892181773ac1");
            var Q109;
            Q109=sQuery(id+"F10.wireOp",EDGE,"0ad358c8-1f94-4756-875f-7bf0cd9fd3df");
            var Q110;
            Q110=sQuery(id+"F10.wireOp",EDGE,"c40075be-d8ed-43cd-aae6-b9651dbaaa6b");
            var Q111;
            Q111=sQuery(id+"F10.wireOp",EDGE,"cfe18def-6381-495e-ab42-29ec9349a4eb");
            var Q112;
            Q112=sQuery(id+"F10.wireOp",EDGE,"a4617b18-76a1-489b-a0eb-e8a9dd9229a6");
            var Q113;
            Q113=sQuery(id+"F10.wireOp",EDGE,"7b596e2a-ffef-4e7e-a88f-fd8a09f0507d");
            var Q114;
            Q114=sQuery(id+"F10.wireOp",EDGE,"9a624597-d23b-4b2a-b0a3-758a82e16175");
            var Q115;
            Q115=sQuery(id+"F10.wireOp",EDGE,"c810709d-2833-4747-8146-436a168fe515");
            var Q116;
            Q116=sQuery(id+"F10.wireOp",EDGE,"cd6867b1-cffc-4bd7-85b0-ae9c42d78e00");
            var Q117;
            Q117=sQuery(id+"F10.wireOp",EDGE,"cab21d9a-e19b-41e9-8f61-907ef245c6ed");
            var Q118;
            Q118=sQuery(id+"F10.wireOp",EDGE,"61829a57-2e8d-4dc1-b4fe-84b8fd0eaebf");
            var Q119;
            Q119=sQuery(id+"F10.wireOp",EDGE,"806de329-c485-4bae-94c7-a49e3323ac69");
            var Q120;
            Q120=sQuery(id+"F10.wireOp",EDGE,"f97c77e4-91bb-447f-a265-ec96d8046f24");
            var Q121;
            Q121=sQuery(id+"F10.wireOp",EDGE,"d4b1330b-5431-46a0-8f3d-29abf992ec76");
            var Q122;
            Q122=sQuery(id+"F10.wireOp",EDGE,"870f9d06-4ba8-4ac7-94d8-936a90053384");
            var Q123;
            Q123=sQuery(id+"F10.wireOp",EDGE,"0965f9dd-e83d-48c3-ad16-f0117208cb55");
            var Q124;
            Q124=sQuery(id+"F10.wireOp",EDGE,"1d800abb-7a5c-4794-b9af-7f1aa996c91b");
            var Q125;
            Q125=sQuery(id+"F10.wireOp",EDGE,"c114ab53-469b-4555-93f5-bb030b770ef5");
            var Q126;
            Q126=sQuery(id+"F10.wireOp",EDGE,"413c1439-79c0-4cb3-bcc5-fd4351f496b1");
            var Q127;
            Q127=sQuery(id+"F10.wireOp",EDGE,"d2b34768-b4d6-4c93-90cd-fb03d719e45f");
            var Q128;
            Q128=sQuery(id+"F10.wireOp",EDGE,"052473a4-c8b8-479b-bced-d4feee30966a");
            var Q129;
            Q129=sQuery(id+"F10.wireOp",EDGE,"56b34cb0-d6b1-468e-9315-c3af8a8086d2");
            var Q130;
            Q130=sQuery(id+"F10.wireOp",EDGE,"dd1df144-a9e7-4224-83a7-1f087d43766b");
            var Q131;
            Q131=sQuery(id+"F10.wireOp",EDGE,"d30680d9-92d3-4708-b3ca-d0b59e179dee");
            var Q132;
            Q132=sQuery(id+"F10.wireOp",EDGE,"52785b89-3f6a-4297-9161-65f53cc09119");
            var Q133;
            Q133=sQuery(id+"F10.wireOp",EDGE,"d80efb84-ae5c-43f2-9c32-b0763d7e62b2");
            var Q134;
            Q134=sQuery(id+"F10.wireOp",EDGE,"9b4eabe2-30f1-4b4f-9b9e-6f0acc0c09be");
            var Q135;
            Q135=sQuery(id+"F10.wireOp",EDGE,"cf1d31b0-7cc4-47f4-80b7-5054c15d1ff4");
            var Q136;
            Q136=sQuery(id+"F10.wireOp",EDGE,"ebac276a-052d-4481-a70b-3e6cdb59f749");
            var Q137;
            Q137=sQuery(id+"F10.wireOp",EDGE,"ba90dc42-b860-41a1-9a54-c50c96dbc357");
            var Q138;
            Q138=sQuery(id+"F10.wireOp",EDGE,"69cff7fa-fec0-4619-b1e2-fd0dcd0dab27");
            var Q139;
            Q139=sQuery(id+"F10.wireOp",EDGE,"bf84317d-6375-4196-b3a2-4b85f70b5367");
            var Q140;
            Q140=sQuery(id+"F10.wireOp",EDGE,"1a3a63a1-71bb-4b02-a7a5-d7a267083d1e");
            var Q141;
            Q141=sQuery(id+"F10.wireOp",EDGE,"9063a531-0c9d-4897-8cfd-c7cb2c940646");
            var Q142;
            Q142=sQuery(id+"F10.wireOp",EDGE,"ad1955f0-aeb1-4dc6-91e7-428b67e91c39");
            var Q143;
            Q143=sQuery(id+"F10.wireOp",EDGE,"96e5c29e-4026-4c5f-bd03-6add21c7f127");
            var Q144;
            Q144=sQuery(id+"F10.wireOp",EDGE,"55bbeec8-313e-446a-9e3c-ae14eda242af");
            var Q145;
            Q145=sQuery(id+"F10.wireOp",EDGE,"edcd5124-60d0-4414-81dd-2b7a54e640f2");
            var Q146;
            Q146=sQuery(id+"F10.wireOp",EDGE,"a8931339-0f47-4184-aa64-b2c706108204");
            var Q147;
            Q147=sQuery(id+"F10.wireOp",EDGE,"e503c753-b8b8-4876-8040-911c36b0b044");
            var Q148;
            Q148=sQuery(id+"F10.wireOp",EDGE,"1f97d6b6-e2cc-477b-aeb3-8dd8c813d526");
            var Q149;
            Q149=sQuery(id+"F10.wireOp",EDGE,"98d3704e-a17b-4e45-8f87-ede134d574d4");
            var Q150;
            Q150=sQuery(id+"F10.wireOp",EDGE,"3d632d32-96ea-47aa-9aa6-41b2aaaa006c");
            var Q151;
            Q151=sQuery(id+"F10.wireOp",EDGE,"6e0a89a2-e50a-484c-81c7-d576482523fc");
            var Q152;
            Q152=sQuery(id+"F10.wireOp",EDGE,"25fdd307-845b-4d95-a226-b908d6fd6b70");
            var Q153;
            Q153=sQuery(id+"F10.wireOp",EDGE,"6498deb7-8ae7-466c-adf3-2883d758e9a8");
            var Q154;
            Q154=sQuery(id+"F10.wireOp",EDGE,"0edef9e7-944a-47f2-9adc-779749e835ff");
            var Q155;
            Q155=sQuery(id+"F10.wireOp",EDGE,"f222bd6a-4755-4869-9b46-d68b7df5ee5f");
            var Q156;
            Q156=sQuery(id+"F10.wireOp",EDGE,"e6998a49-b252-44d5-a286-9b745af8f78f");
            var Q157;
            Q157=sQuery(id+"F10.wireOp",EDGE,"7c58a330-e7c3-42b3-a9ab-8c2cef3c928a");
            var Q158;
            Q158=sQuery(id+"F10.wireOp",EDGE,"e8609150-9ca2-47d3-ac9e-fbbcc218d45c");
            var Q159;
            Q159=sQuery(id+"F10.wireOp",EDGE,"f7bf79c8-1c58-4234-a39e-fbe515a19918");
            var Q160;
            Q160=sQuery(id+"F10.wireOp",EDGE,"b3f8fdd5-4610-4474-b9d8-3dde55ced9cc");
            var Q161;
            Q161=sQuery(id+"F10.wireOp",EDGE,"9d4b348f-9ffb-4743-8355-04ee43b64a35");
            var Q162;
            Q162=sQuery(id+"F10.wireOp",EDGE,"43ed5d9f-947a-41ad-a216-2225dc6cb40f");
            var Q163;
            Q163=sQuery(id+"F10.wireOp",EDGE,"3a1a4591-f698-4ea8-baec-47b57df3e14f");
            var Q164;
            Q164=sQuery(id+"F10.wireOp",EDGE,"449447c3-45e5-4221-9aab-2fd6c18ba59a");
            var Q165;
            Q165=sQuery(id+"F10.wireOp",EDGE,"f5506bc0-5dc4-49cd-8008-422042e0d3cf");
            var Q166;
            Q166=sQuery(id+"F10.wireOp",EDGE,"acf381b9-2617-4d64-9826-8e1da1543149");
            var Q167;
            Q167=sQuery(id+"F10.wireOp",EDGE,"4a4d12ed-265a-4e73-87e7-ba8a0c389543");
            var Q168;
            Q168=sQuery(id+"F10.wireOp",EDGE,"594692c3-c775-46b3-b791-881fc877c07b");
            var Q169;
            Q169=sQuery(id+"F10.wireOp",EDGE,"763d8f59-a3d3-4d48-ab82-6f9e05e74e97");
            var Q170;
            Q170=sQuery(id+"F10.wireOp",EDGE,"77eb4318-fb7f-463d-98e2-19f80554e273");
            var Q171;
            Q171=sQuery(id+"F10.wireOp",EDGE,"370bb3d5-998a-4bd8-a486-226cef342585");
            var Q172;
            Q172=sQuery(id+"F10.wireOp",EDGE,"b2881d7f-931c-4c8f-933a-6a5c2123ef76");
            var Q173;
            Q173=sQuery(id+"F10.wireOp",EDGE,"fafd9d2e-7256-4496-886b-9e4f6e3798cb");
            var Q174;
            Q174=sQuery(id+"F10.wireOp",EDGE,"f9e7ac58-b3d5-4539-ac3d-3b3561b3a243");
            var Q175;
            Q175=sQuery(id+"F10.wireOp",EDGE,"f0e238f5-c269-41a1-8a84-f071f6061c50");
            var Q176;
            Q176=sQuery(id+"F10.wireOp",EDGE,"a560af03-c3d8-4147-acc2-2a7859bb7bd6");
            var Q177;
            Q177=sQuery(id+"F10.wireOp",EDGE,"63918ebc-1d3d-4878-a4e6-54a4db548b94");
            var Q178;
            Q178=sQuery(id+"F10.wireOp",EDGE,"14c695db-531c-422b-b705-8acf2cab01c0");
            var Q179;
            Q179=sQuery(id+"F10.wireOp",EDGE,"ce814141-6a7e-4dbe-ba96-7e7ee62932b8");
            var Q180;
            Q180=sQuery(id+"F10.wireOp",EDGE,"433b44f7-3698-49a7-a3b1-01b73ba0ea55");
            var Q181;
            Q181=sQuery(id+"F10.wireOp",EDGE,"8b360e2c-a9e5-4fb1-9db0-dcf21e2de09c");
            var Q182;
            Q182=sQuery(id+"F10.wireOp",EDGE,"42c10db8-db21-4382-b5ec-d3b3f05b6791");
            var Q183;
            Q183=sQuery(id+"F10.wireOp",EDGE,"6140afb1-7b83-4934-8b5e-e2b3ac70e168");
            var Q184;
            Q184=sQuery(id+"F10.wireOp",EDGE,"0de9f8e7-d94e-4324-8316-e5803bad7437");
            var Q185;
            Q185=sQuery(id+"F10.wireOp",EDGE,"d40396e8-ada2-4914-a31a-e5168066e89f");
            var Q186;
            Q186=sQuery(id+"F10.wireOp",EDGE,"7dd4e553-4bef-40ac-9d80-88974e0ad07c");
            var Q187;
            Q187=sQuery(id+"F10.wireOp",EDGE,"64a8e8fb-7d16-440d-9b7c-f0a489337029");
            var Q188;
            Q188=sQuery(id+"F10.wireOp",EDGE,"eb2c8c8d-0300-4350-818c-154fcc1c3cd2");
            var Q189;
            Q189=sQuery(id+"F10.wireOp",EDGE,"e7d547c6-8549-4c6c-87c4-e7c6e298a7a3");
            var Q190;
            Q190=sQuery(id+"F10.wireOp",EDGE,"1bb11957-115a-4ef5-bdc5-f7051ba36ea5");
            var Q191;
            Q191=sQuery(id+"F10.wireOp",EDGE,"b12918fe-add8-454d-b468-c17826e3f858");
            var Q192;
            Q192=sQuery(id+"F10.wireOp",EDGE,"c2583ff4-29d1-4fad-b934-5a86f1a2c097");
            var Q193;
            Q193=sQuery(id+"F10.wireOp",EDGE,"f2caff9b-8ca5-4ae8-b4e6-59a9b0c10ea8");
            var Q194;
            Q194=sQuery(id+"F10.wireOp",EDGE,"12bc12d8-e222-4746-82d5-38000534226a");
            var Q195;
            Q195=sQuery(id+"F10.wireOp",EDGE,"b4c40086-658d-4ccd-8940-04271687e46f");
            var Q196;
            Q196=sQuery(id+"F10.wireOp",EDGE,"4264d34e-db6f-4b13-8152-dcef5feb5e5c");
            var Q197;
            Q197=sQuery(id+"F10.wireOp",EDGE,"4149b607-aa2d-4a0c-94ce-07e30b7ec0f8");
            var Q198;
            Q198=sQuery(id+"F10.wireOp",EDGE,"8eb9ea9f-d74f-4669-b3bb-3bb7180f66df");
            var Q199;
            Q199=sQuery(id+"F10.wireOp",EDGE,"f73e7de1-a5bb-48ab-9c6e-69dcfd4ddb6a");
            var Q200;
            Q200=sQuery(id+"F10.wireOp",EDGE,"d7efe644-b619-4301-81ba-a347dd7873e4");
            var Q201;
            Q201=sQuery(id+"F10.wireOp",EDGE,"600c2983-0b4d-4209-a376-483386620958");
            var Q202;
            Q202=sQuery(id+"F10.wireOp",EDGE,"6d54e3d2-9f34-4eed-bfb4-650f7302f3d1");
            var Q203;
            Q203=sQuery(id+"F10.wireOp",EDGE,"a75faa4c-551c-4548-bc4f-ac8c7a0eb176");
            var Q204;
            Q204=sQuery(id+"F10.wireOp",EDGE,"abc1bf03-6883-4757-8d08-67587e35bd54");
            var Q205;
            Q205=sQuery(id+"F10.wireOp",EDGE,"4f2327ce-8560-4cc5-8e90-48cf511006d2");
            var Q206;
            Q206=sQuery(id+"F10.wireOp",EDGE,"5b6f2f5e-72f8-40eb-87fb-6658063f59fb");
            var Q207;
            Q207=sQuery(id+"F10.wireOp",EDGE,"201ab1d5-4dd1-4e2c-84ef-ad0991834a0e");
            var Q208;
            Q208=sQuery(id+"F10.wireOp",EDGE,"ebc79c7d-f340-490c-a758-9cba328a1c4a");
            var Q209;
            Q209=sQuery(id+"F10.wireOp",EDGE,"c675f6bd-d0e9-4799-b06b-dbc20d62dc6f");
            var Q210;
            Q210=sQuery(id+"F10.wireOp",EDGE,"357d4661-8363-4bb9-83bc-90006d1969f7");
            var Q211;
            Q211=sQuery(id+"F10.wireOp",EDGE,"e7a7cec2-a609-4c92-8db5-fcf3cfe969a6");
            var Q212;
            Q212=sQuery(id+"F10.wireOp",EDGE,"ef48feac-1de1-4515-b1fd-48302bb834cd");
            var Q213;
            Q213=sQuery(id+"F10.wireOp",EDGE,"92004bb4-2584-416e-9c3b-cb775e819b9e");
            var Q214;
            Q214=sQuery(id+"F10.wireOp",EDGE,"5cff063e-6fc7-4149-b24f-6bcf5bb2678e");
            var Q215;
            Q215=sQuery(id+"F10.wireOp",EDGE,"f7f37c24-776f-4184-b12d-69703fd858c6");
            var Q216;
            Q216=sQuery(id+"F10.wireOp",EDGE,"5fab448e-e901-44c9-b455-ebbe615f9ca2");
            var Q217;
            Q217=sQuery(id+"F10.wireOp",EDGE,"81d78491-d014-42ba-9ff9-2e39ae4933a4");
            var Q218;
            Q218=sQuery(id+"F10.wireOp",EDGE,"c317f2dd-1e7d-447f-b0a1-1ec63853239b");
            var Q219;
            Q219=sQuery(id+"F10.wireOp",EDGE,"0ef9ccb6-4f88-49ef-b60b-8231c8ec4ff8");
            var Q220;
            Q220=sQuery(id+"F10.wireOp",EDGE,"0490281a-3864-4a6c-a5cb-4a417a9d7d28");
            var Q221;
            Q221=sQuery(id+"F10.wireOp",EDGE,"2c64d125-0dfa-4ab1-8f9b-9531630f2dd2");
            var Q222;
            Q222=sQuery(id+"F10.wireOp",EDGE,"ca0651ef-7621-4754-aa6c-31bc3c2c2fb0");
            var Q223;
            Q223=sQuery(id+"F10.wireOp",EDGE,"9222e894-7f3b-450a-8ecb-764908a5bb7e");
            var Q224;
            Q224=sQuery(id+"F10.wireOp",EDGE,"4a960e95-b003-4d4e-a641-263445ca042b");
            var Q225;
            Q225=sQuery(id+"F10.wireOp",EDGE,"bae39d0a-e8db-472e-8e5b-c1138560a275");
            var Q226;
            Q226=sQuery(id+"F10.wireOp",EDGE,"37e401f9-5738-473a-b4c5-f04447d0c97c");
            var Q227;
            Q227=sQuery(id+"F10.wireOp",EDGE,"9536fc89-47c5-4584-b1ad-33ec0b079858");
            var Q228;
            Q228=sQuery(id+"F10.wireOp",EDGE,"93f45c14-8ca4-44e2-9116-9107ad0b130c");
            var Q229;
            Q229=sQuery(id+"F10.wireOp",EDGE,"0af8d037-e556-4376-8db1-431cd3994be3");
            var Q230;
            Q230=sQuery(id+"F10.wireOp",EDGE,"ff6949e9-5ac6-43ca-8aed-1cdeebfc163b");
            var Q231;
            Q231=sQuery(id+"F10.wireOp",EDGE,"922ccc5b-7931-468a-9f26-4680fc7d449d");
            var Q232;
            Q232=sQuery(id+"F10.wireOp",EDGE,"baf32c88-1bdd-4153-aab9-7232afb2c61d");
            var Q233;
            Q233=sQuery(id+"F10.wireOp",EDGE,"75c6c2e9-fdf5-4625-b61b-3e5dd6476779");
            var Q234;
            Q234=sQuery(id+"F10.wireOp",EDGE,"fce8e757-18f0-46b7-809f-85918f295b19");
            var Q235;
            Q235=sQuery(id+"F10.wireOp",EDGE,"eaeb66a0-76d4-4e79-a684-1732fe1080ef");
            var Q236;
            Q236=sQuery(id+"F10.wireOp",EDGE,"325bfc6a-66ec-4caa-80af-5b21d7dcab06");
            var Q237;
            Q237=sQuery(id+"F10.wireOp",EDGE,"989f6a73-6456-4efc-866e-187c4c93437b");
            var Q238;
            Q238=sQuery(id+"F10.wireOp",EDGE,"fd03001c-b3f8-4b76-b274-16c7c1853164");
            var Q239;
            Q239=sQuery(id+"F10.wireOp",EDGE,"4065e296-53a0-47b9-9627-97001e44fcd8");
            var Q240;
            Q240=sQuery(id+"F10.wireOp",EDGE,"5a579925-a4f7-4072-9b44-e18b79a29461");
            var Q241;
            Q241=sQuery(id+"F10.wireOp",EDGE,"56bda946-ecab-4b3c-a3c3-cbd43588cb84");
            var Q242;
            Q242=sQuery(id+"F10.wireOp",EDGE,"d293cff9-89c8-4e9e-b9bc-8d3ace1b5876");
            var Q243;
            Q243=sQuery(id+"F10.wireOp",EDGE,"c352def9-2813-46bb-aa75-e7978b8e400f");
            var Q244;
            Q244=sQuery(id+"F10.wireOp",EDGE,"41ce34ba-1661-4f14-887a-3bffa1f7fe48");
            var Q245;
            Q245=sQuery(id+"F10.wireOp",EDGE,"cdaf6552-f73b-4b51-9926-3658e6a8a44f");
            var Q246;
            Q246=sQuery(id+"F10.wireOp",EDGE,"4d3d2406-50ed-4cca-89af-da1742fe648c");
            var Q247;
            Q247=sQuery(id+"F10.wireOp",EDGE,"9258e09f-303d-4c2b-a0b1-14c479e2c8bf");
            var Q248;
            Q248=sQuery(id+"F10.wireOp",EDGE,"ef682d6c-415b-4b00-a706-6a7bd6d8850f");
            var Q249;
            Q249=sQuery(id+"F10.wireOp",EDGE,"79fbd732-5cd4-4a54-9184-646966937fa2");
            var Q250;
            Q250=sQuery(id+"F10.wireOp",EDGE,"a40b126d-cdf2-436c-b555-d4de2c43a8bd");
            var Q251;
            Q251=sQuery(id+"F10.wireOp",EDGE,"171dc26a-8079-4fb9-9cd2-8befca55b72d");
            var Q252;
            Q252=sQuery(id+"F10.wireOp",EDGE,"4828fc66-b8f6-477c-9089-8a971f6a542b");
            var Q253;
            Q253=sQuery(id+"F10.wireOp",EDGE,"69465d79-b5a8-4b98-839d-2f85f0c6f511");
            var Q254;
            Q254=sQuery(id+"F10.wireOp",EDGE,"0f8dbe6c-b3eb-42d8-b3e7-d7ea919dab65");
            var Q255;
            Q255=sQuery(id+"F10.wireOp",EDGE,"e5be2a1f-e2ba-4a99-96a9-82583312b343");
            var Q256;
            Q256=sQuery(id+"F10.wireOp",EDGE,"06b7239c-81ee-4ffd-89a3-b894e256d53e");
            var Q257;
            Q257=sQuery(id+"F10.wireOp",EDGE,"ecec0231-90eb-4a60-84fe-323a9f96261e");
            var Q258;
            Q258=sQuery(id+"F10.wireOp",EDGE,"9d85751b-f5f9-495d-bda4-a1e67b538856");
            var Q259;
            Q259=sQuery(id+"F10.wireOp",EDGE,"c6626306-1c9a-48f8-aa66-56fbe9b65e56");
            var Q260;
            Q260=sQuery(id+"F10.wireOp",EDGE,"e72b0cf1-bf0f-4c04-941c-7a3f0eda4ae5");
            var Q261;
            Q261=sQuery(id+"F10.wireOp",EDGE,"daa139e2-b514-44f3-988a-8c45856ffb56");
            var Q262;
            Q262=sQuery(id+"F10.wireOp",EDGE,"9d96ecb1-a4a3-4796-9766-885037c38970");
            var Q263;
            Q263=sQuery(id+"F10.wireOp",EDGE,"4f6bcf02-731c-4948-9184-b1e893aea509");
            var Q264;
            Q264=sQuery(id+"F10.wireOp",EDGE,"7f242780-def7-4159-81fd-7c50c7bdf879");
            var Q265;
            Q265=sQuery(id+"F10.wireOp",EDGE,"f5530c5c-db9b-4719-82bf-28eae5865c5a");
            var Q266;
            Q266=sQuery(id+"F10.wireOp",EDGE,"c177c0a8-4379-404d-aa86-5922abe98214");
            var Q267;
            Q267=sQuery(id+"F10.wireOp",EDGE,"6647b122-23a7-4ed4-b55e-4c25e97d7880");
            var Q268;
            Q268=sQuery(id+"F10.wireOp",EDGE,"4d488502-c593-40be-979e-b0a2439aad28");
            var Q269;
            Q269=sQuery(id+"F10.wireOp",EDGE,"28107bed-2a23-4293-94d3-57b8192512fb");
            var Q270;
            Q270=sQuery(id+"F10.wireOp",EDGE,"f91391b6-2764-4877-adb4-787cd9f235a7");
            var Q271;
            Q271=sQuery(id+"F10.wireOp",EDGE,"a9cfe6ba-e0a5-4400-b7de-30e679ee1e05");
            var Q272;
            Q272=sQuery(id+"F10.wireOp",EDGE,"744e0d3f-31db-420b-b525-4483caa94113");
            var Q273;
            Q273=sQuery(id+"F10.wireOp",EDGE,"f102ee0b-77fe-4cd0-ba9e-b8dbb8271450");
            var Q274;
            Q274=sQuery(id+"F10.wireOp",EDGE,"0553e309-3857-450a-8285-e3b4a7f73f1d");
            var Q275;
            Q275=sQuery(id+"F10.wireOp",EDGE,"8326a867-d5a4-4d4b-ba0e-f77b094d9ae2");
            var Q276;
            Q276=sQuery(id+"F10.wireOp",EDGE,"eea86504-28f0-45c0-9781-feac49c29b12");
            var Q277;
            Q277=sQuery(id+"F10.wireOp",EDGE,"82a3c5bf-1c22-4e74-b6ec-cfc26a98db7c");
            var Q278;
            Q278=sQuery(id+"F10.wireOp",EDGE,"50f0b073-56aa-4bd0-bc4c-cd426b3a5804");
            var Q279;
            Q279=sQuery(id+"F10.wireOp",EDGE,"188f0708-6ad8-4e30-931a-96a145b6c849");
            var Q280;
            Q280=sQuery(id+"F10.wireOp",EDGE,"b2dca776-e706-4c05-abd7-68dd6eeaecdb");
            var Q281;
            Q281=sQuery(id+"F10.wireOp",EDGE,"bde8624f-098a-4564-b4f3-34d068a0ad26");
            var Q282;
            Q282=sQuery(id+"F10.wireOp",EDGE,"ec938cd8-baf9-4008-b5bc-0227ece3a26f");
            var Q283;
            Q283=sQuery(id+"F10.wireOp",EDGE,"0d4d4185-c87f-4846-aefd-28a2f88c2eee");
            var Q284;
            Q284=sQuery(id+"F10.wireOp",EDGE,"f4d1f187-bfcb-4c0e-8270-ee2325faa733");
            var Q285;
            Q285=sQuery(id+"F10.wireOp",EDGE,"77c902b3-1739-4a92-976e-d9b9d5490fbe");
            var Q286;
            Q286=sQuery(id+"F10.wireOp",EDGE,"8d85dd64-1679-43cd-a910-9e901184b805");
            var Q287;
            Q287=sQuery(id+"F10.wireOp",EDGE,"06002bd8-afa3-4cb8-9823-788378265493");
            var Q288;
            Q288=sQuery(id+"F10.wireOp",EDGE,"7b7e0abb-43fe-4636-87f7-f57880e5c6f5");
            var Q289;
            Q289=sQuery(id+"F10.wireOp",EDGE,"768919d0-ccc2-477a-b931-476890e8288d");
            var Q290;
            Q290=sQuery(id+"F10.wireOp",EDGE,"a7d48b52-3375-4cbb-b5fc-3f6d16d4018c");
            var Q291;
            Q291=sQuery(id+"F10.wireOp",EDGE,"ee8244c1-cbdf-4ddb-87ab-55fa2a9bd2cd");
            var Q292;
            Q292=sQuery(id+"F10.wireOp",EDGE,"bdf2db43-151c-4855-ac61-faa3731f1614");
            var Q293;
            Q293=sQuery(id+"F10.wireOp",EDGE,"6ab1e1a4-f920-46fb-a885-df3c68f69326");
            var Q294;
            Q294=sQuery(id+"F10.wireOp",EDGE,"e27f17a5-a131-4cd1-9dd4-c60af44119a9");
            var Q295;
            Q295=sQuery(id+"F10.wireOp",EDGE,"3450fc02-30d8-4eb2-9f28-c7a162962873");
            var Q296;
            Q296=sQuery(id+"F10.wireOp",EDGE,"323ffac5-859e-4ac4-9c75-5d21f2c2fd5d");
            var Q297;
            Q297=sQuery(id+"F10.wireOp",EDGE,"133eec3e-25b0-4d98-9ccb-94d54d8ddee9");
            var Q298;
            Q298=sQuery(id+"F10.wireOp",EDGE,"a0561817-497a-4e0c-9e26-6bf5bd93801b");
            var Q299;
            Q299=sQuery(id+"F10.wireOp",EDGE,"187733ef-1fb7-45dc-a732-8d2a96c67adf");
            var Q300;
            Q300=sQuery(id+"F10.wireOp",EDGE,"17c68dda-2f9e-4577-aed1-77eae8fa3dad");
            var Q301;
            Q301=sQuery(id+"F10.wireOp",EDGE,"7e2d87f3-5ee9-4b5c-9b9d-63321f6194e6");
            var Q302;
            Q302=sQuery(id+"F10.wireOp",EDGE,"8dcf95ee-425a-4054-b676-73eb71b54908");
            var Q303;
            Q303=sQuery(id+"F10.wireOp",EDGE,"add453b1-8450-46cf-ab6d-14e63521945e");
            var Q304;
            Q304=sQuery(id+"F10.wireOp",EDGE,"92e718eb-6da6-46c3-83c0-2ec321db1d80");
            var Q305;
            Q305=sQuery(id+"F10.wireOp",EDGE,"3670785a-375b-4990-9d7f-e385ac92939c");
            var Q306;
            Q306=sQuery(id+"F10.wireOp",EDGE,"3196e757-25b3-4336-9c59-ac48378c6e83");
            var Q307;
            Q307=sQuery(id+"F10.wireOp",EDGE,"9dde04a4-482f-47a1-9ea0-4c67e3512b0a");
            var Q308;
            Q308=sQuery(id+"F10.wireOp",EDGE,"669f532a-daf0-4d90-93b5-8557eececab1");
            var Q309;
            Q309=sQuery(id+"F10.wireOp",EDGE,"1e268a40-daac-4403-9adf-5224eb5ebbb2");
            var Q310;
            Q310=sQuery(id+"F10.wireOp",EDGE,"cea8576b-32fc-41e3-b8d6-8557c24df543");
            var Q311;
            Q311=sQuery(id+"F10.wireOp",EDGE,"92ef1d87-7dfc-41f1-b87c-1c1a9d1b62d0");
            var Q312;
            Q312=sQuery(id+"F10.wireOp",EDGE,"8a273317-0ecd-4b06-9db8-5d3ed4a19800");
            var Q313;
            Q313=sQuery(id+"F10.wireOp",EDGE,"f37ec48c-ec8f-4e0f-ab99-a88cf8c2e57d");
            var Q314;
            Q314=sQuery(id+"F10.wireOp",EDGE,"d5c803c4-f679-4b01-81c6-de0f79854225");
            var Q315;
            Q315=sQuery(id+"F10.wireOp",EDGE,"fc07a523-e902-49bb-95ce-31ebfc07d100");
            var Q316;
            Q316=sQuery(id+"F10.wireOp",EDGE,"02083512-ad49-4e44-b06d-84debe068a44");
            var Q317;
            Q317=sQuery(id+"F10.wireOp",EDGE,"c1b25caf-9485-46d7-b384-fc14495f1107");
            var Q318;
            Q318=sQuery(id+"F10.wireOp",EDGE,"ca4ca1bd-9207-4cf5-9113-7cf25db9952d");
            var Q319;
            Q319=sQuery(id+"F10.wireOp",EDGE,"d733ccee-9211-4335-9fd5-42b7b9db6a31");
            var Q320;
            Q320=sQuery(id+"F10.wireOp",EDGE,"92f43523-86c6-452c-98a9-8ca573f780e7");
            var Q321;
            Q321=sQuery(id+"F10.wireOp",EDGE,"87880a3f-e635-4b5f-bce2-df5596e33566");
            var Q322;
            Q322=sQuery(id+"F10.wireOp",EDGE,"f2cf56fb-0ce4-4019-9b17-d73afc360a92");
            var Q323;
            Q323=sQuery(id+"F10.wireOp",EDGE,"1ac07c45-b79c-4772-9000-7849deba77be");
            var Q324;
            Q324=sQuery(id+"F10.wireOp",EDGE,"d243ca1e-3f59-4edb-84a0-dfdf2c45a8b6");
            var Q325;
            Q325=sQuery(id+"F10.wireOp",EDGE,"886673f9-2161-4555-a754-9497bed1ba93");
            var Q326;
            Q326=sQuery(id+"F10.wireOp",EDGE,"bf5d85fc-d9fc-41d9-91fb-0ae1b08e86fd");
            var Q327;
            Q327=sQuery(id+"F10.wireOp",EDGE,"6efb0b0f-50c5-434d-b7b7-ad9c1960964e");
            var Q328;
            Q328=sQuery(id+"F10.wireOp",EDGE,"6c16b9f6-05f9-456d-90a1-c3d62f790908");
            var Q329;
            Q329=sQuery(id+"F10.wireOp",EDGE,"24e3a223-6fdf-462d-9cb1-ca05091919fa");
            var Q330;
            Q330=sQuery(id+"F10.wireOp",EDGE,"140801d8-f5cc-4b6e-a31b-a8dc08e42335");
            var Q331;
            Q331=sQuery(id+"F10.wireOp",EDGE,"8a458559-c9c8-4ae5-8d62-6cec255c0677");
            var Q332;
            Q332=sQuery(id+"F10.wireOp",EDGE,"3ad68588-ea99-492d-bd76-f7d479b2ef21");
            var Q333;
            Q333=sQuery(id+"F10.wireOp",EDGE,"04169d78-04f6-40ad-9f7a-0d678ec870d6");
            var Q334;
            Q334=sQuery(id+"F10.wireOp",EDGE,"fe57fb12-963e-46f3-bf3b-0071c091ad67");
            var Q335;
            Q335=sQuery(id+"F10.wireOp",EDGE,"24a51efb-0265-46d9-9d12-0961e1406b4d");
            var Q336;
            Q336=sQuery(id+"F10.wireOp",EDGE,"6b937af4-f2a8-492c-ace8-9ae35967f598");
            var Q337;
            Q337=sQuery(id+"F10.wireOp",EDGE,"3d0e6a1f-8431-49f4-b0ea-4c89ac99083e");
            var Q338;
            Q338=sQuery(id+"F10.wireOp",EDGE,"fedad2d9-d42a-4daa-ab47-d48680bbf2b3");
            var Q339;
            Q339=sQuery(id+"F10.wireOp",EDGE,"e64c0731-0a73-445e-856f-3c27fd95678a");
            var Q340;
            Q340=sQuery(id+"F10.wireOp",EDGE,"d3669e0c-879d-4d8d-9f28-0fca23128e6a");
            var Q341;
            Q341=sQuery(id+"F10.wireOp",EDGE,"d9367b24-2e28-445b-b42f-837ae83b3121");
            var Q342;
            Q342=sQuery(id+"F10.wireOp",EDGE,"fb4021bc-fea9-4d77-9629-1cedee9978d9");
            var Q343;
            Q343=sQuery(id+"F10.wireOp",EDGE,"4eaccad3-42ad-4e16-aa55-17653e109192");
            var Q344;
            Q344=sQuery(id+"F10.wireOp",EDGE,"44daf0ca-2204-4766-9b82-30eb1613487c");
            var Q345;
            Q345=sQuery(id+"F10.wireOp",EDGE,"3f024ed0-2669-4504-aca3-8ba75f4e6e10");
            var Q346;
            Q346=sQuery(id+"F10.wireOp",EDGE,"fed6d351-2a99-48ec-ac91-0db49dc99d12");
            var Q347;
            Q347=sQuery(id+"F10.wireOp",EDGE,"a33a7eb8-fcea-4fca-b3f0-5816683bb590");
            var Q348;
            Q348=sQuery(id+"F10.wireOp",EDGE,"3207fc96-acdd-4b65-ae5c-f58f1cfa2694");
            var Q349;
            Q349=sQuery(id+"F10.wireOp",EDGE,"f9e5fa60-33e2-43c2-8f05-0e6c78ea18b5");
            var Q350;
            Q350=sQuery(id+"F10.wireOp",EDGE,"83bdca73-a8b9-4e99-a183-b77e11751452");
            var Q351;
            Q351=sQuery(id+"F10.wireOp",EDGE,"017d1f2a-9635-4ae4-9c6b-1e290e527e16");
            var Q352;
            Q352=sQuery(id+"F10.wireOp",EDGE,"cedeb50f-af90-4477-a2cb-7e9f001b2f06");
            var Q353;
            Q353=sQuery(id+"F10.wireOp",EDGE,"cd93dac9-6ecb-46e6-b692-76c3740377e7");
            var Q354;
            Q354=sQuery(id+"F10.wireOp",EDGE,"8fbf7be4-38ca-4928-a737-0e5b30e29719");
            var Q355;
            Q355=sQuery(id+"F10.wireOp",EDGE,"a3385c98-4899-45b9-8381-55da941e008b");
            var Q356;
            Q356=sQuery(id+"F10.wireOp",EDGE,"c5b2134c-e0fd-4935-adeb-c1dd7d159c5c");
            var Q357;
            Q357=sQuery(id+"F10.wireOp",EDGE,"8e88b1b4-505e-450b-9e56-d515fcce70f5");
            var Q358;
            Q358=sQuery(id+"F10.wireOp",EDGE,"a6814ad7-c5d8-4067-8081-cbb8e66138d7");
            var Q359;
            Q359=sQuery(id+"F10.wireOp",EDGE,"e8677ec1-0b38-4c38-9511-02945689fdf4");
            var Q360;
            Q360=sQuery(id+"F10.wireOp",EDGE,"050ee1f4-8f89-43ec-9a4a-46bb5842b5a2");
            var Q361;
            Q361=sQuery(id+"F10.wireOp",EDGE,"342a888a-383c-4efe-9a8e-63d59e0382ae");
            var Q362;
            Q362=sQuery(id+"F10.wireOp",EDGE,"ba765ed8-5e41-465e-bb04-aabbca1a7aa8");
            var Q363;
            Q363=sQuery(id+"F10.wireOp",EDGE,"fbfa58b2-0b16-4167-9173-a1b2853a2e0d");
            var Q364;
            Q364=sQuery(id+"F10.wireOp",EDGE,"1146dd6d-9a40-42f4-9534-474ac0f0e1a2");
            var Q365;
            Q365=sQuery(id+"F10.wireOp",EDGE,"212dd272-0022-4345-b280-96102cf2d792");
            var Q366;
            Q366=sQuery(id+"F10.wireOp",EDGE,"ee5b470a-6809-47c3-9e0f-d7149dbc5ad7");
            var Q367;
            Q367=sQuery(id+"F10.wireOp",EDGE,"50c89e37-9cd8-4f6b-a884-fede45cc7183");
            var Q368;
            Q368=sQuery(id+"F10.wireOp",EDGE,"bd1bc36e-e8d0-4bfd-99a2-395abce84660");
            var Q369;
            Q369=sQuery(id+"F10.wireOp",EDGE,"745d7747-bf22-4570-9f89-7d5f3f98ff07");
            var Q370;
            Q370=sQuery(id+"F10.wireOp",EDGE,"e4020101-c427-4c2f-9896-bd8c4e7eaf43");
            var Q371;
            Q371=sQuery(id+"F10.wireOp",EDGE,"6c90525c-2bf6-4d94-a79a-2301a0384f58");
            var Q372;
            Q372=sQuery(id+"F10.wireOp",EDGE,"fdeb39eb-33c3-4597-9b30-92b0b184539f");
            var Q373;
            Q373=sQuery(id+"F10.wireOp",EDGE,"734e00bf-02b5-48e7-a62c-b767f0b801c2");
            var Q374;
            Q374=sQuery(id+"F10.wireOp",EDGE,"19a6d2f1-233b-487f-b215-4553fe8709e9");
            var Q375;
            Q375=sQuery(id+"F10.wireOp",EDGE,"14d00903-1140-4bc2-918b-657ab8d0b296");
            var Q376;
            Q376=sQuery(id+"F10.wireOp",EDGE,"444f27a0-10ac-4c50-8ded-22c480a0e3c3");
            var Q377;
            Q377=sQuery(id+"F10.wireOp",EDGE,"35ffab4b-d44c-46d2-b4db-3e7ab0334283");
            var Q378;
            Q378=sQuery(id+"F10.wireOp",EDGE,"d5cf98af-0f0c-46e9-9837-027689de48bb");
            var Q379;
            Q379=sQuery(id+"F10.wireOp",EDGE,"05f733bd-bd4b-402d-8ccb-2ecd80c376d7");
            var Q380;
            Q380=sQuery(id+"F10.wireOp",EDGE,"fe7b308f-00d9-410c-83de-92af5b8e5805");
            var Q381;
            Q381=sQuery(id+"F10.wireOp",EDGE,"6d60d954-4926-4735-a49f-50943ea2754b");
            var Q382;
            Q382=sQuery(id+"F10.wireOp",EDGE,"3c35a9df-1e0b-4e9f-ab8b-83e7419e0223");
            var Q383;
            Q383=sQuery(id+"F10.wireOp",EDGE,"aa329298-48f6-4d55-8c67-4ab2ed07a6aa");
            var Q384;
            Q384=sQuery(id+"F10.wireOp",EDGE,"8d9d3e6e-e8d8-400e-a1a0-2b856044def8");
            var Q385;
            Q385=sQuery(id+"F10.wireOp",EDGE,"c07cedee-c5fb-4bb1-9314-330c55a67f83");
            var Q386;
            Q386=sQuery(id+"F10.wireOp",EDGE,"4e0f9a57-dd4d-411f-aab2-187ce7140778");
            var Q387;
            Q387=sQuery(id+"F10.wireOp",EDGE,"72803e55-9a51-4c9f-9e97-804dc99d3e41");
            var Q388;
            Q388=sQuery(id+"F10.wireOp",EDGE,"44b7fb8c-a0d7-48c3-afe5-c0065c54a8fc");
            var Q389;
            Q389=sQuery(id+"F10.wireOp",EDGE,"f1ee7729-0b19-45c2-9e71-127305813115");
            var Q390;
            Q390=sQuery(id+"F10.wireOp",EDGE,"90fac215-06b3-48f6-861d-4d5a7b06a3eb");
            var Q391;
            Q391=sQuery(id+"F10.wireOp",EDGE,"9374c129-08b7-4a67-b4ca-86c8eb717922");
            var Q392;
            Q392=sQuery(id+"F10.wireOp",EDGE,"887df852-74f6-4231-97df-9fee346d9997");
            var Q393;
            Q393=sQuery(id+"F10.wireOp",EDGE,"d2883814-a574-4c23-86d0-416d83a62767");
            var Q394;
            Q394=sQuery(id+"F10.wireOp",EDGE,"ae814763-e372-45af-bbe4-9f4ea7d3602d");
            var Q395;
            Q395=sQuery(id+"F10.wireOp",EDGE,"a3dd4515-b025-467e-b5c5-75f150bbb7aa");
            var Q396;
            Q396=sQuery(id+"F10.wireOp",EDGE,"f175e870-c9af-44fa-8377-23de070578fe");
            var Q397;
            Q397=sQuery(id+"F10.wireOp",EDGE,"98fb2fe6-2fe4-4f71-8c4d-18dc424215d5");
            var Q398;
            Q398=sQuery(id+"F10.wireOp",EDGE,"0fc870f9-85a3-4a2d-8024-5346f75dcb88");
            var Q399;
            Q399=sQuery(id+"F10.wireOp",EDGE,"ab56d1ab-7a5c-4874-9b7e-0dd770fd2ddc");
            var Q400;
            Q400=sQuery(id+"F10.wireOp",EDGE,"98520d4b-dcb3-4807-ba85-7b716b07b200");
            var Q401;
            Q401=sQuery(id+"F10.wireOp",EDGE,"097f315c-531d-401c-bb75-5b794e35bf87");
            var Q402;
            Q402=sQuery(id+"F10.wireOp",EDGE,"7dc22592-1523-4f82-a328-fe73836fd34a");
            var Q403;
            Q403=sQuery(id+"F10.wireOp",EDGE,"ff3edc13-1aa1-404d-9379-e389ecd9c192");
            var Q404;
            Q404=sQuery(id+"F10.wireOp",EDGE,"2dd27df7-de52-475e-9010-22efea48403a");
            var Q405;
            Q405=sQuery(id+"F10.wireOp",EDGE,"ce9c1b0c-c312-44a7-b5d2-8a107f880a89");
            var Q406;
            Q406=sQuery(id+"F10.wireOp",EDGE,"9e003363-b7ad-4da6-b84b-b34bd807ff4a");
            var Q407;
            Q407=sQuery(id+"F10.wireOp",EDGE,"7a2ad006-4a11-461e-92d9-7faa8caafc67");
            var Q408;
            Q408=sQuery(id+"F10.wireOp",EDGE,"6733319f-1bab-442b-a8a3-302b88c801f3");
            var Q409;
            Q409=sQuery(id+"F10.wireOp",EDGE,"3941893e-e339-4b9a-847c-4b1448e70a35");
            var Q410;
            Q410=sQuery(id+"F10.wireOp",EDGE,"89d098a1-0bf3-4925-af24-d5680b955b33");
            var Q411;
            Q411=sQuery(id+"F10.wireOp",EDGE,"0e80fba6-c32a-44ef-9b4c-396eb60450d0");
            var Q412;
            Q412=sQuery(id+"F10.wireOp",EDGE,"8caacf88-b0e3-4490-97e8-6d780c8970e5");
            var Q413;
            Q413=sQuery(id+"F10.wireOp",EDGE,"d2a79b87-e08c-49f0-95c6-4993f7d21589");
            var Q414;
            Q414=sQuery(id+"F10.wireOp",EDGE,"45d5e2ca-966b-49d1-8230-9571160739b1");
            var Q415;
            Q415=sQuery(id+"F10.wireOp",EDGE,"e21a6b60-c48d-4b56-a07f-892afac9f936");
            var Q416;
            Q416=sQuery(id+"F10.wireOp",EDGE,"f227e947-24b2-434d-92e8-0299b7705ba6");
            var Q417;
            Q417=sQuery(id+"F10.wireOp",EDGE,"6af10e55-1d79-4cc8-8e7a-8cab76354253");
            var Q418;
            Q418=sQuery(id+"F10.wireOp",EDGE,"4a67a7e1-8722-4b02-903f-205cc5169cc4");
            var Q419;
            Q419=sQuery(id+"F10.wireOp",EDGE,"3a223b0f-4003-47dd-99c1-2c45533b6a32");
            var Q420;
            Q420=sQuery(id+"F10.wireOp",EDGE,"edc42945-8484-4a13-855b-11083d5c4a83");
            var Q421;
            Q421=sQuery(id+"F10.wireOp",EDGE,"d1c65916-6ea8-4ea0-a44c-695fd622b66b");
            var Q422;
            Q422=sQuery(id+"F10.wireOp",EDGE,"57dd63d3-b9bb-4c99-a95b-c56d4cb7db9a");
            var Q423;
            Q423=sQuery(id+"F10.wireOp",EDGE,"c0c4d37d-1f9a-4f3c-b464-c580b808f560");
            var Q424;
            Q424=sQuery(id+"F10.wireOp",EDGE,"561110bc-f874-42cd-bcfc-71c71e742015");
            var Q425;
            Q425=sQuery(id+"F10.wireOp",EDGE,"f89e0d01-3019-4dc1-bfa2-2aaefa18b273");
            var Q426;
            Q426=sQuery(id+"F10.wireOp",EDGE,"b9c74ac3-d4f0-4f7b-80e0-4ab733864caa");
            var Q427;
            Q427=sQuery(id+"F10.wireOp",EDGE,"8ea4fe0c-72cd-45fd-aa3a-24b8c2d42119");
            var Q428;
            Q428=sQuery(id+"F10.wireOp",EDGE,"8a413f89-1700-44e7-9a41-2b375c2f9519");
            var Q429;
            Q429=sQuery(id+"F10.wireOp",EDGE,"9fe3aa70-75b4-45cf-9ee8-fd9a8fcaba0f");
            var Q430;
            Q430=sQuery(id+"F10.wireOp",EDGE,"0ac25600-4119-4479-a8ab-ff030470285b");
            var Q431;
            Q431=sQuery(id+"F10.wireOp",EDGE,"769f66e2-30ee-45eb-969c-49400e6a2773");
            var Q432;
            Q432=sQuery(id+"F10.wireOp",EDGE,"37d9bf25-5019-4d3b-8641-9467caaab803");
            var Q433;
            Q433=sQuery(id+"F10.wireOp",EDGE,"4b7776b5-c171-4935-bf04-07e0418e068c");
            var Q434;
            Q434=sQuery(id+"F10.wireOp",EDGE,"4c857365-473d-4796-b1af-d79ec3b2bc06");
            var Q435;
            Q435=sQuery(id+"F10.wireOp",EDGE,"7e186563-2aea-4fd1-b201-4c78b29eca4a");
            var Q436;
            Q436=sQuery(id+"F10.wireOp",EDGE,"be06c734-9cd3-4171-a66e-a151ca12c36f");
            var Q437;
            Q437=sQuery(id+"F10.wireOp",EDGE,"6e88ae0e-6917-4f7a-8394-3e8f769530e2");
            var Q438;
            Q438=sQuery(id+"F10.wireOp",EDGE,"edbea945-944c-47de-8f19-8f24bd748fcf");
            var Q439;
            Q439=sQuery(id+"F10.wireOp",EDGE,"5dc7a44c-bfbc-4f27-93a8-6b3637496290");
            var Q440;
            Q440=sQuery(id+"F10.wireOp",EDGE,"808e925b-5237-4a5b-8e0a-81e24db584c8");
            var Q441;
            Q441=sQuery(id+"F10.wireOp",EDGE,"67599923-2726-4d4e-8018-229450783f0d");
            var Q442;
            Q442=sQuery(id+"F10.wireOp",EDGE,"539ba450-512e-4192-8389-0c9da04558fa");
            var Q443;
            Q443=sQuery(id+"F10.wireOp",EDGE,"92c01da4-9cf6-4e71-b6d2-2aed74522fef");
            var Q444;
            Q444=sQuery(id+"F10.wireOp",EDGE,"f46d4d73-e88c-44df-a13d-d6324d479d13");
            var Q445;
            Q445=sQuery(id+"F10.wireOp",EDGE,"1959e4ef-63cb-44c2-80dd-ca40c382fe4b");
            var Q446;
            Q446=sQuery(id+"F10.wireOp",EDGE,"3a13b1b3-f30e-4865-9396-211ecbb8e657");
            var Q447;
            Q447=sQuery(id+"F10.wireOp",EDGE,"8b38b25c-1b40-4131-8868-0c9bee931546");
            var Q448;
            Q448=sQuery(id+"F10.wireOp",EDGE,"a86105e5-6b42-49a8-8c93-f6d76ff5f8a4");
            var Q449;
            Q449=sQuery(id+"F10.wireOp",EDGE,"5c679a3f-eec2-47c4-b9d2-d22a8eea774f");
            var Q450;
            Q450=sQuery(id+"F10.wireOp",EDGE,"797bcbc6-01dc-4dee-bbd7-c8fbcfcf9852");
            var Q451;
            Q451=sQuery(id+"F10.wireOp",EDGE,"a8d16118-51a8-4131-b966-9d8194ae7a4f");
            var Q452;
            Q452=sQuery(id+"F10.wireOp",EDGE,"78eafcbd-515c-4b5b-8efd-e21e29edfa96");
            var Q453;
            Q453=sQuery(id+"F10.wireOp",EDGE,"b38c62c2-242f-47b1-a2a1-20de4f7ddfce");
            var Q454;
            Q454=sQuery(id+"F10.wireOp",EDGE,"04357bc9-7271-4a1e-9246-cc127225abea");
            var Q455;
            Q455=sQuery(id+"F10.wireOp",EDGE,"00dac6db-ad86-4956-a77e-52c50cce11d3");
            var Q456;
            Q456=sQuery(id+"F10.wireOp",EDGE,"ae0dc8ff-973d-42b2-953f-a44f2a64f232");
            var Q457;
            Q457=sQuery(id+"F10.wireOp",EDGE,"d118b4a2-b8ca-40b6-9244-fdc618959c46");
            var Q458;
            Q458=sQuery(id+"F10.wireOp",EDGE,"b8d007da-6a2e-4652-9c36-4577451f37bb");
            var Q459;
            Q459=sQuery(id+"F10.wireOp",EDGE,"3a388336-8814-4360-8850-dad46675e3c6");
            var Q460;
            Q460=sQuery(id+"F10.wireOp",EDGE,"e54808ad-9ea6-4221-9a68-712acdcc5fc5");
            var Q461;
            Q461=sQuery(id+"F10.wireOp",EDGE,"3322df4e-b9e4-4965-9e45-2f8cd528d8ad");
            var Q462;
            Q462=sQuery(id+"F10.wireOp",EDGE,"49aeeb5f-2ee5-4fdb-96d2-8225cbc7592d");
            var Q463;
            Q463=sQuery(id+"F10.wireOp",EDGE,"87430017-35b2-46ea-85b2-c4b051a13365");
            var Q464;
            Q464=sQuery(id+"F10.wireOp",EDGE,"b0276a6f-22e2-4af0-b559-d13f2e3da09e");
            var Q465;
            Q465=sQuery(id+"F10.wireOp",EDGE,"78c626d3-8a59-413f-bf34-19102c3d151b");
            var Q466;
            Q466=sQuery(id+"F10.wireOp",EDGE,"6cb30f91-1cef-442e-9fde-63886b5c90ce");
            var Q467;
            Q467=sQuery(id+"F10.wireOp",EDGE,"8d3f5f22-5a8f-4189-8a90-267384b546ae");
            var Q468;
            Q468=sQuery(id+"F10.wireOp",EDGE,"44244e7a-2fcd-4b8d-afbc-4d6d491caebb");
            var Q469;
            Q469=sQuery(id+"F10.wireOp",EDGE,"eb7ce1f8-13d5-47e6-b1f4-5aef09e5c070");
            var Q470;
            Q470=sQuery(id+"F10.wireOp",EDGE,"bce7159f-9040-48d8-bcea-bb1d7d555c36");
            var Q471;
            Q471=sQuery(id+"F10.wireOp",EDGE,"df157309-5c80-4a7e-8c3d-52c4104fc144");
            var Q472;
            Q472=sQuery(id+"F10.wireOp",EDGE,"0f3cbd65-73c6-41e4-9c0a-7e6b7cc3c053");
            var Q473;
            Q473=sQuery(id+"F10.wireOp",EDGE,"4ac685f3-76ed-44ec-8971-6ec72e2ba44f");
            var Q474;
            Q474=sQuery(id+"F10.wireOp",EDGE,"2deb96f9-44a5-4048-89ea-8786315dd846");
            var Q475;
            Q475=sQuery(id+"F10.wireOp",EDGE,"949742c0-bd09-4031-a9c9-edbfd95d26c4");
            var Q476;
            Q476=sQuery(id+"F10.wireOp",EDGE,"86d1e86c-f8d4-4549-9348-0c294bc0450c");
            var Q477;
            Q477=sQuery(id+"F10.wireOp",EDGE,"4a8d7c50-9b3f-4ce7-8dcd-324521d0bd77");
            var Q478;
            Q478=sQuery(id+"F10.wireOp",EDGE,"c0ba8412-23cb-4784-93e3-f9b6bab65135");
            var Q479;
            Q479=sQuery(id+"F10.wireOp",EDGE,"896e5910-eb9c-46a9-87d6-135c30f6b168");
            var Q480;
            Q480=sQuery(id+"F10.wireOp",EDGE,"46a165b7-9643-4269-8a5a-a3ac62a990f5");
            var Q481;
            Q481=sQuery(id+"F10.wireOp",EDGE,"0355eed7-3d25-447d-b8e2-184633544540");
            var Q482;
            Q482=sQuery(id+"F10.wireOp",EDGE,"912cafba-7e76-4434-bf87-c8f612c9ab44");
            var Q483;
            Q483=sQuery(id+"F10.wireOp",EDGE,"900b5779-9751-4820-bf74-f911bf486511");
            var Q484;
            Q484=sQuery(id+"F10.wireOp",EDGE,"28c8d3cd-ddce-4ee1-b063-caac32d4bc14");
            var Q485;
            Q485=sQuery(id+"F10.wireOp",EDGE,"3ceb8b52-b1b8-451a-9082-193282b4f9fa");
            var Q486;
            Q486=sQuery(id+"F10.wireOp",EDGE,"808b1534-6217-47e2-8947-0fee40a0e753");
            var Q487;
            Q487=sQuery(id+"F10.wireOp",EDGE,"ac346088-ef35-4658-97c3-86f20733efad");
            var Q488;
            Q488=sQuery(id+"F10.wireOp",EDGE,"2f49fcaa-c157-42d4-91fd-a74b0dc54563");
            var Q489;
            Q489=sQuery(id+"F10.wireOp",EDGE,"1ec4b096-8808-48ec-a7c0-5b51fac3461d");
            var Q490;
            Q490=sQuery(id+"F10.wireOp",EDGE,"b664c184-9020-4e76-9054-7136c51e3f21");
            var Q491;
            Q491=sQuery(id+"F10.wireOp",EDGE,"fddacc92-c4a2-49dc-9008-cfcb68c98b2c");
            var Q492;
            Q492=sQuery(id+"F10.wireOp",EDGE,"f71d9185-7051-4a2b-80cd-90be0ff085ee");
            var Q493;
            Q493=sQuery(id+"F10.wireOp",EDGE,"bb07b7d6-33d2-42fa-a433-0f71a1df8b87");
            var Q494;
            Q494=sQuery(id+"F10.wireOp",EDGE,"41925e9c-b5a5-44cb-9fe9-206e22111a9d");
            var Q495;
            Q495=sQuery(id+"F10.wireOp",EDGE,"1047a54f-313b-4508-9767-1f64a28f939d");
            var Q496;
            Q496=sQuery(id+"F10.wireOp",EDGE,"c5f3759e-fd18-4a89-9c6e-6d9f02268b53");
            var Q497;
            Q497=sQuery(id+"F10.wireOp",EDGE,"d0225aa8-1c8a-4fc1-be64-3f7028a79f4d");
            var Q498;
            Q498=sQuery(id+"F10.wireOp",EDGE,"df1b9b17-b8a2-450e-aac6-6f1cbb81c998");
            var Q499;
            Q499=sQuery(id+"F10.wireOp",EDGE,"52aa3a6b-5a19-4dc5-964d-a3af1a87cfa3");
            var Q500;
            Q500=sQuery(id+"F10.wireOp",EDGE,"b0c66558-0346-4ac8-acb0-034374b17222");
            var Q501;
            Q501=sQuery(id+"F10.wireOp",EDGE,"55d172c5-cb63-412a-82a8-3707b50eb5e4");
            var Q502;
            Q502=sQuery(id+"F10.wireOp",EDGE,"8fb7bd9e-89cd-4d10-8c15-671cf83ac684");
            var Q503;
            Q503=sQuery(id+"F10.wireOp",EDGE,"1284f08e-73c2-4bd2-87ae-b1211d2358b9");
            var Q504;
            Q504=sQuery(id+"F10.wireOp",EDGE,"7d15bdf5-7531-4ddd-8892-264aeb4e5ede");
            var Q505;
            Q505=sQuery(id+"F10.wireOp",EDGE,"7fc2cfa5-d538-4f2a-9079-1ebe3c846ca4");
            var Q506;
            Q506=sQuery(id+"F10.wireOp",EDGE,"37a5801d-bcf9-4d90-9b9a-b3d9a221aeb5");
            var Q507;
            Q507=sQuery(id+"F10.wireOp",EDGE,"866d2c2a-f0c8-465d-9bc9-bb91aa5509e7");
            var Q508;
            Q508=sQuery(id+"F10.wireOp",EDGE,"09389697-1bf2-4768-b044-7954c4dacd78");
            var Q509;
            Q509=sQuery(id+"F10.wireOp",EDGE,"bfc6ab28-d19b-4f43-ae67-ad0fc0d3a546");
            var Q510;
            Q510=sQuery(id+"F10.wireOp",EDGE,"8ad338af-a7ae-4937-8c28-116c65de33e7");
            var Q511;
            Q511=sQuery(id+"F10.wireOp",EDGE,"257c31df-35e6-4f78-822d-8ad4f890f773");
            var Q512;
            Q512=sQuery(id+"F10.wireOp",EDGE,"d656eb35-d10f-4f73-8d7a-aa7b4c858496");
            var Q513;
            Q513=sQuery(id+"F10.wireOp",EDGE,"324b81ab-30b9-4cc8-9478-d9076053f654");
            var Q514;
            Q514=sQuery(id+"F10.wireOp",EDGE,"330ddb74-1b29-4aa5-80e4-4dd477cba626");
            var Q515;
            Q515=sQuery(id+"F10.wireOp",EDGE,"42d4b43c-a24d-400a-a199-ff66a46ca03a");
            var Q516;
            Q516=sQuery(id+"F10.wireOp",EDGE,"f83c3785-6142-42d8-8ee3-12d1380e1cd4");
            var Q517;
            Q517=sQuery(id+"F10.wireOp",EDGE,"6707ccb8-4768-48a7-9ef6-49a42e5356f2");
            var Q518;
            Q518=sQuery(id+"F10.wireOp",EDGE,"56804e22-4b9e-49ca-a564-e41bd4fcfdc8");
            var Q519;
            Q519=sQuery(id+"F10.wireOp",EDGE,"19e92a74-479b-47e5-953e-afa625b90239");
            var Q520;
            Q520=sQuery(id+"F10.wireOp",EDGE,"119c1e8d-e8ca-43d4-a17e-96a52e3885fe");
            var Q521;
            Q521=sQuery(id+"F10.wireOp",EDGE,"dd0c0625-a050-433f-9d24-5489f3401754");
            var Q522;
            Q522=sQuery(id+"F10.wireOp",EDGE,"8ec66915-354d-48dc-b7f6-15809a7d633e");
            var Q523;
            Q523=sQuery(id+"F10.wireOp",EDGE,"044ded7c-a733-482f-8846-a92c7ab35404");
            var Q524;
            Q524=sQuery(id+"F10.wireOp",EDGE,"58c40804-b805-43e1-8857-d80d70033e77");
            var Q525;
            Q525=sQuery(id+"F10.wireOp",EDGE,"ee050726-1398-4dbf-9110-d057c53f16e8");
            var Q526;
            Q526=sQuery(id+"F10.wireOp",EDGE,"5689c8b5-1a98-4093-ab6d-c3a30ca113e9");
            var Q527;
            Q527=sQuery(id+"F10.wireOp",EDGE,"ffa3e259-1c2f-4f7c-8fc4-b2c7639106c2");
            var Q528;
            Q528=sQuery(id+"F10.wireOp",EDGE,"cf996a4d-9ee7-434d-8d76-89a873d462ad");
            var Q529;
            Q529=sQuery(id+"F10.wireOp",EDGE,"dafe8af7-57e2-452d-a930-6fcd1af7097b");
            var Q530;
            Q530=sQuery(id+"F10.wireOp",EDGE,"c374576f-3e51-4000-90bf-b6b7d85a48e5");
            var Q531;
            Q531=sQuery(id+"F10.wireOp",EDGE,"276b85fc-f744-4e8a-8c31-a91ce78365b2");
            var Q532;
            Q532=sQuery(id+"F10.wireOp",EDGE,"5739a0c1-b25a-4e25-b48d-25319f5ea494");
            var Q533;
            Q533=sQuery(id+"F10.wireOp",EDGE,"7b6032c8-acf4-430a-abc3-98ddcb9b9978");
            var Q534;
            Q534=sQuery(id+"F10.wireOp",EDGE,"5b7d17a5-c0dc-44f7-adf0-c03a5c9fd558");
            var Q535;
            Q535=sQuery(id+"F10.wireOp",EDGE,"fd6eadeb-857b-4a2d-9a53-9c5a19799d77");
            var Q536;
            Q536=sQuery(id+"F10.wireOp",EDGE,"3060e947-43b9-41b8-bece-9583681855ae");
            var Q537;
            Q537=sQuery(id+"F10.wireOp",EDGE,"4f5650cc-7d01-4a26-bb42-42b345239fc7");
            var Q538;
            Q538=sQuery(id+"F10.wireOp",EDGE,"13c2ed3f-5e51-49cb-b6f9-cfded2d0c44f");
            var Q539;
            Q539=sQuery(id+"F10.wireOp",EDGE,"84ffbea2-cb14-44a2-a76f-20402e0213f2");
            var Q540;
            Q540=sQuery(id+"F10.wireOp",EDGE,"9c6f34d0-b25c-4240-ab5b-7810f64f2475");
            var Q541;
            Q541=sQuery(id+"F10.wireOp",EDGE,"8a093dcf-4efe-4c22-b05c-75140d92b263");
            var Q542;
            Q542=sQuery(id+"F10.wireOp",EDGE,"66d9c36c-41c6-4bff-87c6-cbab339a227e");
            var Q543;
            Q543=sQuery(id+"F10.wireOp",EDGE,"f87132b3-dac4-4eda-a514-0739513d947b");
            var Q544;
            Q544=sQuery(id+"F10.wireOp",EDGE,"5b61e5bf-ae60-4730-b209-401cbd0acec9");
            var Q545;
            Q545=sQuery(id+"F10.wireOp",EDGE,"a9f67a0b-e06e-456c-a1f6-c8f6c6983ffc");
            var Q546;
            Q546=sQuery(id+"F10.wireOp",EDGE,"15454a51-37d7-4607-ac63-4324172ed939");
            var Q547;
            Q547=sQuery(id+"F10.wireOp",EDGE,"fd0f134f-15eb-419d-85ae-c8182bd056f2");
            var Q548;
            Q548=sQuery(id+"F10.wireOp",EDGE,"c54f583a-9e3a-4c19-96ae-900cf75575d5");
            var Q549;
            Q549=sQuery(id+"F10.wireOp",EDGE,"1bfb64d6-47a5-42ac-89df-ed45d390221e");
            var Q550;
            Q550=sQuery(id+"F10.wireOp",EDGE,"2d167fbd-1fb7-415e-9645-b3f9f30d5ff4");
            var Q551;
            Q551=sQuery(id+"F10.wireOp",EDGE,"6d57964b-a673-4888-ac1d-b2cdd80b73ae");
            var Q552;
            Q552=sQuery(id+"F10.wireOp",EDGE,"b363502f-0179-42c2-ad97-bce162be25f6");
            var Q553;
            Q553=sQuery(id+"F10.wireOp",EDGE,"404d4d3f-4d20-47a8-8296-aab3e8e1fef1");
            var Q554;
            Q554=sQuery(id+"F10.wireOp",EDGE,"e91502b4-8121-4eab-a9d9-081f1cdecef8");
            var Q555;
            Q555=sQuery(id+"F10.wireOp",EDGE,"dc0d9109-d5b8-42d5-b2d7-152964318875");
            var Q556;
            Q556=sQuery(id+"F10.wireOp",EDGE,"411f37c2-bc93-4f0c-8a59-b54b59a7aade");
            var Q557;
            Q557=sQuery(id+"F10.wireOp",EDGE,"e34c1f92-18c6-42e8-9429-5c52b10cfde9");
            var Q558;
            Q558=sQuery(id+"F10.wireOp",EDGE,"ccf0b456-6192-498c-b7f0-f7ea683f1f58");
            var Q559;
            Q559=sQuery(id+"F10.wireOp",EDGE,"380508f7-43a5-4548-8f72-2863f5ec1406");
            var Q560;
            Q560=sQuery(id+"F10.wireOp",EDGE,"1182630c-c513-421b-8f8d-95e10fa9e884");
            var Q561;
            Q561=sQuery(id+"F10.wireOp",EDGE,"133e181c-72a0-4dc0-9b12-9bd119b19eb8");
            var Q562;
            Q562=sQuery(id+"F10.wireOp",EDGE,"4485013b-c1bb-4dd6-952f-ed66792f64ba");
            var Q563;
            Q563=sQuery(id+"F10.wireOp",EDGE,"d51529a5-34f7-4a8d-a333-54630a9d51b1");
            var Q564;
            Q564=sQuery(id+"F10.wireOp",EDGE,"456c88a6-bb49-41af-844c-fbb27e151355");
            var Q565;
            Q565=sQuery(id+"F10.wireOp",EDGE,"638081d3-a48c-4fe7-a9ed-98cfb710e254");
            var Q566;
            Q566=sQuery(id+"F10.wireOp",EDGE,"6ed5600a-3493-4c9e-a156-990ed4755a65");
            var Q567;
            Q567=sQuery(id+"F10.wireOp",EDGE,"17b8bc8a-8bf7-445f-b9fe-f745033125fe");
            var Q568;
            Q568=sQuery(id+"F10.wireOp",EDGE,"f1573831-7747-4047-b17d-ada80df690e2");
            var Q569;
            Q569=sQuery(id+"F10.wireOp",EDGE,"5da69a87-7a78-4879-b69f-ca830ce2aa30");
            var Q570;
            Q570=sQuery(id+"F10.wireOp",EDGE,"6f8bb688-2043-4309-8198-44816ded4d12");
            var Q571;
            Q571=sQuery(id+"F10.wireOp",EDGE,"bd9b65dc-eb84-4040-a9fc-33756a1d34d4");
            var Q572;
            Q572=sQuery(id+"F10.wireOp",EDGE,"083f210d-70b4-4f43-bd3d-907cde6e7d54");
            var Q573;
            Q573=sQuery(id+"F10.wireOp",EDGE,"0884c471-380c-4aa8-82f5-a674b2a7ea67");
            var Q574;
            Q574=sQuery(id+"F10.wireOp",EDGE,"e4e0ae2b-71e1-4125-9ef5-76afbfddd02a");
            var Q575;
            Q575=sQuery(id+"F10.wireOp",EDGE,"bc380bde-b14a-4972-9602-020a332ec3b1");
            var Q576;
            Q576=sQuery(id+"F10.wireOp",EDGE,"8f88af28-225b-42fd-b4ad-0ad9f788c0ca");
            var Q577;
            Q577=sQuery(id+"F10.wireOp",EDGE,"de7134fe-3c58-4d13-8b3d-e83c5ad3a639");
            var Q578;
            Q578=sQuery(id+"F10.wireOp",EDGE,"bc58ef25-e3fd-4b3a-aaec-68ae6cf14535");
            var Q579;
            Q579=sQuery(id+"F10.wireOp",EDGE,"f19eb347-2d49-4bc2-850a-1c2d67b7427f");
            var Q580;
            Q580=sQuery(id+"F10.wireOp",EDGE,"1d1fb251-11da-4fe8-8901-966d300954ac");
            var Q581;
            Q581=sQuery(id+"F10.wireOp",EDGE,"f50edc38-dd64-4767-9548-1a5259b24d26");
            var Q582;
            Q582=sQuery(id+"F10.wireOp",EDGE,"95db7ecf-465b-4149-841a-6c0dd55cde80");
            var Q583;
            Q583=sQuery(id+"F10.wireOp",EDGE,"6db2d9a0-9530-41ef-8502-d0ff85b20f8f");
            var Q584;
            Q584=sQuery(id+"F10.wireOp",EDGE,"3bf9ad4a-711a-4d55-81a0-1a0d5970a24b");
            var Q585;
            Q585=sQuery(id+"F10.wireOp",EDGE,"a9ccd012-45cc-408c-9eaa-1650f2957891");
            var Q586;
            Q586=sQuery(id+"F10.wireOp",EDGE,"72396718-c188-4a3d-b0d0-bc1e58484de6");
            var Q587;
            Q587=sQuery(id+"F10.wireOp",EDGE,"23fbdd4b-1b03-475b-a67a-265a697aa198");
            var Q588;
            Q588=sQuery(id+"F10.wireOp",EDGE,"80e7ea7b-3f12-4347-8e28-d91fa634e30e");
            var Q589;
            Q589=sQuery(id+"F10.wireOp",EDGE,"1db03a7f-3f8b-44ef-be24-021cc6594b38");
            var Q590;
            Q590=sQuery(id+"F10.wireOp",EDGE,"402f89fb-0318-4f20-a3f7-fcf65d7a3bcd");
            var Q591;
            Q591=sQuery(id+"F10.wireOp",EDGE,"affced70-7c6e-4c32-a78e-b600510b6d61");
            var Q592;
            Q592=sQuery(id+"F10.wireOp",EDGE,"eb9a4553-0b91-4069-9685-c46d34d55a77");
            var Q593;
            Q593=sQuery(id+"F10.wireOp",EDGE,"d64673de-86b6-46ed-a726-32545af51c37");
            var Q594;
            Q594=sQuery(id+"F10.wireOp",EDGE,"3d9d07f0-3c80-447c-9437-bbbe2453d3bc");
            var Q595;
            Q595=sQuery(id+"F10.wireOp",EDGE,"f06380e0-0beb-40d3-8359-c287dd21991d");
            var Q596;
            Q596=sQuery(id+"F10.wireOp",EDGE,"4d2fc3f9-3a8c-45b2-97ff-c40358f9befd");
            var Q597;
            Q597=sQuery(id+"F10.wireOp",EDGE,"9c7e3f95-d5c6-4b08-a4cf-d05ff63452d3");
            var Q598;
            Q598=sQuery(id+"F10.wireOp",EDGE,"b81847c9-8e5c-4540-8100-6aeb110f5d79");
            var Q599;
            Q599=sQuery(id+"F10.wireOp",EDGE,"ed43ec12-fc93-45f9-859e-ebd16081836e");
            var Q600;
            Q600=sQuery(id+"F10.wireOp",EDGE,"acbae8d6-968a-4e43-8aad-6e3fdc0958a1");
            var Q601;
            Q601=sQuery(id+"F10.wireOp",EDGE,"1f412e52-b096-4b8d-942d-bcb311c46987");
            var Q602;
            Q602=sQuery(id+"F10.wireOp",EDGE,"3412c646-66fc-4f88-879f-f2bbfb0eec0d");
            var Q603;
            Q603=sQuery(id+"F10.wireOp",EDGE,"8f417bd5-6f56-46c1-ad30-48bd65cd47f1");
            var Q604;
            Q604=sQuery(id+"F10.wireOp",EDGE,"78a661c0-6ab2-4964-ac6d-45e80e6ae2af");
            var Q605;
            Q605=sQuery(id+"F10.wireOp",EDGE,"53dc1618-f40a-47f7-9ee0-b961bcf34d61");
            var Q606;
            Q606=sQuery(id+"F10.wireOp",EDGE,"3f818846-037f-4e1f-ae70-2c3cf3774613");
            var Q607;
            Q607=sQuery(id+"F10.wireOp",EDGE,"c82f811d-b417-4457-afb4-9d9e04ee573b");
            var Q608;
            Q608=sQuery(id+"F10.wireOp",EDGE,"0bbd1056-e8d5-45ad-bbea-654589e728ec");
            var Q609;
            Q609=sQuery(id+"F10.wireOp",EDGE,"88ab3a17-bd98-4fbd-b168-0e461d3a4448");
            var Q610;
            Q610=sQuery(id+"F10.wireOp",EDGE,"4b125ce8-a39d-4422-b4f9-aa242a39e791");
            var Q611;
            Q611=sQuery(id+"F10.wireOp",EDGE,"74eaf0ba-dbe2-4924-a515-84332f5c4ed0");
            var Q612;
            Q612=sQuery(id+"F10.wireOp",EDGE,"9bc2b86e-a0be-4b4c-8800-bb69cf561b87");
            var Q613;
            Q613=sQuery(id+"F10.wireOp",EDGE,"1bc92242-104a-4b63-a43d-c56939ecd048");
            var Q614;
            Q614=sQuery(id+"F10.wireOp",EDGE,"24f53942-0f46-48d9-a73e-ef73e9ff167a");
            var Q615;
            Q615=sQuery(id+"F10.wireOp",EDGE,"040c1b01-ea62-4d25-be8b-c169f78f6378");
            var Q616;
            Q616=sQuery(id+"F10.wireOp",EDGE,"af5a196a-7f5f-4108-a850-06f899b06d08");
            var Q617;
            Q617=sQuery(id+"F10.wireOp",EDGE,"f6cf86f1-4ad7-496f-b4d6-5f9d740e5f7a");
            var Q618;
            Q618=sQuery(id+"F10.wireOp",EDGE,"9eae25cc-e313-4862-8853-0889c06a4e04");
            var Q619;
            Q619=sQuery(id+"F10.wireOp",EDGE,"a506daac-e723-4e37-989b-3120eebdca83");
            var Q620;
            Q620=sQuery(id+"F10.wireOp",EDGE,"79b1ddc3-1727-4944-8a9e-a54853188ad7");
            var Q621;
            Q621=sQuery(id+"F10.wireOp",EDGE,"c9b18f79-721a-4bdf-87bf-9f420bd96ad6");
            var Q622;
            Q622=sQuery(id+"F10.wireOp",EDGE,"83790366-64b8-412c-b066-0b596fb9788c");
            var Q623;
            Q623=sQuery(id+"F10.wireOp",EDGE,"d9e774d6-1915-4b86-86ec-2992e92f4b17");
            var Q624;
            Q624=sQuery(id+"F10.wireOp",EDGE,"201056a3-ed5a-4f5f-be90-1b09a4cbc16d");
            var Q625;
            Q625=sQuery(id+"F10.wireOp",EDGE,"0a523b58-d9e5-47b2-82c2-84ab27932798");
            var Q626;
            Q626=sQuery(id+"F10.wireOp",EDGE,"50b4f2f9-f226-40f7-950a-a64186ed3350");
            var Q627;
            Q627=sQuery(id+"F10.wireOp",EDGE,"3aa7ed1f-b082-4335-aee1-d8a597cf9d96");
            var Q628;
            Q628=sQuery(id+"F10.wireOp",EDGE,"f87bcafe-7b06-4bbe-8436-5f428702bada");
            var Q629;
            Q629=sQuery(id+"F10.wireOp",EDGE,"fe03edd4-f6fc-4a15-a976-26c608b05cb5");
            var Q630;
            Q630=sQuery(id+"F10.wireOp",EDGE,"869b04c0-8eab-422a-a197-ba55ad701703");
            var Q631;
            Q631=sQuery(id+"F10.wireOp",EDGE,"98dc3855-9473-44e7-bce0-82354ee94d12");
            var Q632;
            Q632=sQuery(id+"F10.wireOp",EDGE,"d72e6831-109b-40ae-bb63-d663042155cc");
            var Q633;
            Q633=sQuery(id+"F10.wireOp",EDGE,"afe8fdf1-3fe3-489a-ae7c-af1a9927f62a");
            var Q634;
            Q634=sQuery(id+"F10.wireOp",EDGE,"f7065258-febc-4bd8-bcd1-307e4cb8ddf4");
            var Q635;
            Q635=sQuery(id+"F10.wireOp",EDGE,"59b774da-2540-4e5c-8ed4-c4c5224f162d");
            var Q636;
            Q636=sQuery(id+"F10.wireOp",EDGE,"ce1e4446-9156-416f-82d1-cc129ad81397");
            var Q637;
            Q637=sQuery(id+"F10.wireOp",EDGE,"7e54cffd-fcc7-4e61-aac5-f23fea5c5dd3");
            var Q638;
            Q638=sQuery(id+"F10.wireOp",EDGE,"557d9a6d-f419-480e-9b47-d5fdd0a42acb");
            var Q639;
            Q639=sQuery(id+"F10.wireOp",EDGE,"0190174e-ffc6-4214-9e13-c55068246998");
            var Q640;
            Q640=sQuery(id+"F10.wireOp",EDGE,"b4d32629-b171-41e5-a0aa-b9aac2110c3f");
            var Q641;
            Q641=sQuery(id+"F10.wireOp",EDGE,"48aca40d-2e8d-4187-94af-222d04c49e01");
            var Q642;
            Q642=sQuery(id+"F10.wireOp",EDGE,"0763da1a-3f1f-4b9e-b66e-ff8f62c7b329");
            var Q643;
            Q643=sQuery(id+"F10.wireOp",EDGE,"eb259d8c-d0da-49ec-a231-cdc9b770ed77");
            var Q644;
            Q644=sQuery(id+"F10.wireOp",EDGE,"fcc3a9eb-1d04-4de0-9882-23cbfcccde66");
            var Q645;
            Q645=sQuery(id+"F10.wireOp",EDGE,"0426d5a1-80ab-49f4-b37c-92dca4aafd2b");
            var Q646;
            Q646=sQuery(id+"F10.wireOp",EDGE,"abc1e03a-f4fc-4144-891c-3ccb6aec2aa7");
            var Q647;
            Q647=sQuery(id+"F10.wireOp",EDGE,"44043914-f16a-4356-bbb7-d7822177774e");
            var Q648;
            Q648=sQuery(id+"F10.wireOp",EDGE,"d0ba4a71-fa5e-4eb9-9774-a53dbb295978");
            var Q649;
            Q649=sQuery(id+"F10.wireOp",EDGE,"9f95eca2-562b-4da2-890c-4caf79218da0");
            var Q650;
            Q650=sQuery(id+"F10.wireOp",EDGE,"d60811cb-f337-4f61-bdc0-c714be9995b8");
            var Q651;
            Q651=sQuery(id+"F10.wireOp",EDGE,"dfaa4db5-2bdd-4d60-9934-ac1cf5ef5d5e");
            var Q652;
            Q652=sQuery(id+"F10.wireOp",EDGE,"b00814e6-dc09-460c-a92b-da13017529d0");
            var Q653;
            Q653=sQuery(id+"F10.wireOp",EDGE,"aeeb5ec9-f68c-4305-80c0-001b4b398eff");
            var Q654;
            Q654=sQuery(id+"F10.wireOp",EDGE,"02b5c322-ecd1-4b8e-8c58-04e51fbe0b82");
            var Q655;
            Q655=sQuery(id+"F10.wireOp",EDGE,"2dbda03d-b9c5-4708-98d5-15e9bfd45f9a");
            var Q656;
            Q656=sQuery(id+"F10.wireOp",EDGE,"0a43f70f-d989-4217-b193-b51e5947e8c4");
            var Q657;
            Q657=sQuery(id+"F10.wireOp",EDGE,"f1477380-edb8-493f-9476-9947ab6def53");
            var Q658;
            Q658=sQuery(id+"F10.wireOp",EDGE,"8b1a8c16-adfa-496b-aa10-f1d27f9e5beb");
            var Q659;
            Q659=sQuery(id+"F10.wireOp",EDGE,"99a4fe12-eb5c-4a89-b1b3-bce6dda23c50");
            var Q660;
            Q660=sQuery(id+"F10.wireOp",EDGE,"cde1e237-9b53-4578-afb0-29086b48f8a5");
            var Q661;
            Q661=sQuery(id+"F10.wireOp",EDGE,"00ba8242-a404-4703-a94e-fd68024a20a2");
            var Q662;
            Q662=sQuery(id+"F10.wireOp",EDGE,"40ccc2c5-8a7a-4474-9917-32f887254265");
            var Q663;
            Q663=sQuery(id+"F10.wireOp",EDGE,"1d0f23bd-020a-4e66-a545-a5fd9e4eea1d");
            var Q664;
            Q664=sQuery(id+"F10.wireOp",EDGE,"9db5eeda-aac5-485e-bee9-77ded7a6443c");
            var Q665;
            Q665=sQuery(id+"F10.wireOp",EDGE,"7317ffad-5181-405b-b3c9-eb89e6e2bcdc");
            var Q666;
            Q666=sQuery(id+"F10.wireOp",EDGE,"11d01625-97b7-4c5a-80d2-4fb4072cec42");
            var Q667;
            Q667=sQuery(id+"F10.wireOp",EDGE,"10000ff5-f190-41c0-b9aa-85c6c2873210");
            var Q668;
            Q668=sQuery(id+"F10.wireOp",EDGE,"b4310660-9dac-4abd-a9ff-cb2c5743c29c");
            var Q669;
            Q669=sQuery(id+"F10.wireOp",EDGE,"59401c97-4776-4081-8dd2-6cc958e5148b");
            var Q670;
            Q670=sQuery(id+"F10.wireOp",EDGE,"b760032c-5a5f-4058-98d2-ef7682d01b15");
            var Q671;
            Q671=sQuery(id+"F10.wireOp",EDGE,"fbcdcadd-5eab-4dba-84ea-66b61a4fd927");
            var Q672;
            Q672=sQuery(id+"F10.wireOp",EDGE,"f7f994b5-eb07-4a1f-afcb-f5bf1dead2ba");
            var Q673;
            Q673=sQuery(id+"F10.wireOp",EDGE,"b6414431-a1de-4aee-a25e-d006765afe8a");
            var Q674;
            Q674=sQuery(id+"F10.wireOp",EDGE,"6841b4fa-1832-4a8c-919e-4d62eb994190");
            var Q675;
            Q675=sQuery(id+"F10.wireOp",EDGE,"b123606b-72e7-4be3-8985-bbe08a60f177");
            var Q676;
            Q676=sQuery(id+"F10.wireOp",EDGE,"e52a5df8-810f-4d78-83fd-5de77f256eaf");
            var Q677;
            Q677=sQuery(id+"F10.wireOp",EDGE,"dc97acc3-b88a-42e0-a35b-16b358490be5");
            var Q678;
            Q678=sQuery(id+"F10.wireOp",EDGE,"e5e2eedf-1172-4fec-a6cc-e5c11baa2625");
            var Q679;
            Q679=sQuery(id+"F10.wireOp",EDGE,"84e3eee3-7393-4752-82d5-f061ffafe555");
            var Q680;
            Q680=sQuery(id+"F10.wireOp",EDGE,"1dec27cc-9cf0-4b58-92a2-452e67580bfd");
            var Q681;
            Q681=sQuery(id+"F10.wireOp",EDGE,"2de385b1-43b7-4200-b0b5-dcfa45d08b7c");
            var Q682;
            Q682=sQuery(id+"F10.wireOp",EDGE,"f583b172-b9a1-4eee-bd9b-4248ced61cfc");
            var Q683;
            Q683=sQuery(id+"F10.wireOp",EDGE,"06420daf-c24c-4fbf-afed-b5a35298995c");
            var Q684;
            Q684=sQuery(id+"F10.wireOp",EDGE,"571e3cca-4761-44c6-8771-b711589dac50");
            var Q685;
            Q685=sQuery(id+"F10.wireOp",EDGE,"cb929f30-245f-419e-b0a2-edb4e9506464");
            var Q686;
            Q686=sQuery(id+"F10.wireOp",EDGE,"7954f87d-454a-4d7b-bed6-987efc4ed60f");
            var Q687;
            Q687=sQuery(id+"F10.wireOp",EDGE,"a42950e5-0200-4e02-b720-2160b32915e8");
            var Q688;
            Q688=sQuery(id+"F10.wireOp",EDGE,"dcd0bd3e-a386-467e-8d6b-e0504750c1a1");
            var Q689;
            Q689=sQuery(id+"F10.wireOp",EDGE,"e890fb0a-1c77-49a2-972f-cb8267d17dec");
            var Q690;
            Q690=sQuery(id+"F10.wireOp",EDGE,"0cd8581b-37ae-45a3-9c61-032d8aca090c");
            var Q691;
            Q691=sQuery(id+"F10.wireOp",EDGE,"26c1634a-ff35-4a62-9635-aafc24fcb041");
            var Q692;
            Q692=sQuery(id+"F10.wireOp",EDGE,"70a8fe1c-ca42-4959-82a0-1aa74cb7a0cb");
            var Q693;
            Q693=sQuery(id+"F10.wireOp",EDGE,"941f02de-4edc-4a2e-baae-623d524d6e3c");
            var Q694;
            Q694=sQuery(id+"F10.wireOp",EDGE,"37f1f15f-5a6d-4ef4-a42e-d85257482abd");
            var Q695;
            Q695=sQuery(id+"F10.wireOp",EDGE,"de081b95-e80c-486d-b4d4-35d0a5bc39f8");
            var Q696;
            Q696=sQuery(id+"F10.wireOp",EDGE,"45f49674-92fa-4585-b953-2bfbd9db2803");
            var Q697;
            Q697=sQuery(id+"F10.wireOp",EDGE,"2a44a31c-d3f0-45a5-b2b3-eb03c91287a1");
            var Q698;
            Q698=sQuery(id+"F10.wireOp",EDGE,"dd99ec9c-cd8c-40d9-9b8c-5978413b28fc");
            var Q699;
            Q699=sQuery(id+"F10.wireOp",EDGE,"17f914e3-4b79-4fec-947a-d15388ec81a7");
            var Q700;
            Q700=sQuery(id+"F10.wireOp",EDGE,"3c24f8a1-dba0-4e7e-9b77-146e7f0a7a78");
            var Q701;
            Q701=sQuery(id+"F10.wireOp",EDGE,"aa98c953-b158-4556-95af-5c997f1152f5");
            var Q702;
            Q702=sQuery(id+"F10.wireOp",EDGE,"49d1f04a-36cc-44b6-bdac-bfc8589ca1b3");
            var Q703;
            Q703=sQuery(id+"F10.wireOp",EDGE,"445e65b7-378d-4601-a66d-4065a3d7ac7b");
            var Q704;
            Q704=sQuery(id+"F10.wireOp",EDGE,"b4ff5a68-5963-4edd-a012-f7eeacf899f0");
            var Q705;
            Q705=sQuery(id+"F10.wireOp",EDGE,"46efc8ff-f59b-4567-8205-43ed82f1d883");
            var Q706;
            Q706=sQuery(id+"F10.wireOp",EDGE,"34f8377c-5d1c-4109-988e-f89e8b386fbd");
            var Q707;
            Q707=sQuery(id+"F10.wireOp",EDGE,"fd903d7b-4124-4d53-952c-850e25eed5e0");
            var Q708;
            Q708=sQuery(id+"F10.wireOp",EDGE,"2ffda740-f1bd-4d53-909b-0cd3fc5b5efd");
            var Q709;
            Q709=sQuery(id+"F10.wireOp",EDGE,"a13184f2-28f5-44c1-96f1-05083820a2a4");
            var Q710;
            Q710=sQuery(id+"F10.wireOp",EDGE,"dd677c1f-3530-46a1-93b8-530ed0b433ba");
            var Q711;
            Q711=sQuery(id+"F10.wireOp",EDGE,"600df196-3a9d-41ad-aae3-30c9d6bfe2aa");
            var Q712;
            Q712=sQuery(id+"F10.wireOp",EDGE,"9e836f8d-3084-4cbb-9a11-16aa5a907b2d");
            var Q713;
            Q713=sQuery(id+"F10.wireOp",EDGE,"1ee6c918-9d4c-403d-b84d-1de33b1fddc8");
            var Q714;
            Q714=sQuery(id+"F10.wireOp",EDGE,"baadea27-8d21-4c31-bd84-d1ea78cf6f4c");
            var Q715;
            Q715=sQuery(id+"F10.wireOp",EDGE,"3c4940cd-5865-42cf-a9b5-d733725b2162");
            var Q716;
            Q716=sQuery(id+"F10.wireOp",EDGE,"926bfdb3-386e-4abd-ada9-99f17c760468");
            var Q717;
            Q717=sQuery(id+"F10.wireOp",EDGE,"72fc0f1f-25be-4b73-adac-ff88f7ba281b");
            var Q718;
            Q718=sQuery(id+"F10.wireOp",EDGE,"646ec5af-00c3-49a8-bad7-b5e0a1042eac");
            var Q719;
            Q719=sQuery(id+"F10.wireOp",EDGE,"d3749ecc-8263-4788-be87-55490e761b1e");
            var Q720;
            Q720=sQuery(id+"F10.wireOp",EDGE,"69d5a1eb-db67-447d-9a1f-7921f2010f26");
            var Q721;
            Q721=sQuery(id+"F10.wireOp",EDGE,"6a212f7a-a383-4559-b983-02d427b24793");
            var Q722;
            Q722=sQuery(id+"F10.wireOp",EDGE,"490555d1-202d-4275-a4af-6ee0672a1d2a");
            var Q723;
            Q723=sQuery(id+"F10.wireOp",EDGE,"49039694-6e73-43c7-b017-bd7d21434d11");
            var Q724;
            Q724=sQuery(id+"F10.wireOp",EDGE,"7a5210be-af8c-4df9-884e-78419e6b401e");
            var Q725;
            Q725=sQuery(id+"F10.wireOp",EDGE,"56765ac7-47d0-40dd-9f58-eac9772c0a44");
            var Q726;
            Q726=sQuery(id+"F10.wireOp",EDGE,"1ca62a38-39e4-4e11-bcb7-4d4f90f1c729");
            var Q727;
            Q727=sQuery(id+"F10.wireOp",EDGE,"e9f8f089-2ed4-4eb4-b3d7-2fdcbf117ba1");
            var Q728;
            Q728=sQuery(id+"F10.wireOp",EDGE,"1da6940b-ca3d-44d5-b97e-0431ff501804");
            var Q729;
            Q729=sQuery(id+"F10.wireOp",EDGE,"8e6da988-3f99-4f31-930a-b69611fd64f7");
            var Q730;
            Q730=sQuery(id+"F10.wireOp",EDGE,"fe9e220c-677e-4b3b-88c2-2093aa1e90b0");
            var Q731;
            Q731=sQuery(id+"F10.wireOp",EDGE,"f9403c01-6459-459b-9595-76623918a665");
            var Q732;
            Q732=sQuery(id+"F10.wireOp",EDGE,"bc9e100e-76f8-4c82-8c00-8fe9f0177e65");
            var Q733;
            Q733=sQuery(id+"F10.wireOp",EDGE,"cacede21-8b77-43e5-a2e3-833f74abe2ad");
            var Q734;
            Q734=sQuery(id+"F10.wireOp",EDGE,"725cff87-7dd6-463c-b289-3d1007735660");
            var Q735;
            Q735=sQuery(id+"F10.wireOp",EDGE,"119323b1-f408-40e7-9636-9f51fceaa5c8");
            var Q736;
            Q736=sQuery(id+"F10.wireOp",EDGE,"22c4e707-2c22-4665-abb8-305abdf5674c");
            var Q737;
            Q737=sQuery(id+"F10.wireOp",EDGE,"2a624c43-757c-44e7-b64b-885bfd1f6fb1");
            var Q738;
            Q738=sQuery(id+"F10.wireOp",EDGE,"8ccc39ec-6d21-4792-b3f1-4267164cf68d");
            var Q739;
            Q739=sQuery(id+"F10.wireOp",EDGE,"e3d092b1-154a-4588-ad4a-2084285067e5");
            var Q740;
            Q740=sQuery(id+"F10.wireOp",EDGE,"f232982f-6cb3-4010-8c95-fac9050e99a9");
            var Q741;
            Q741=sQuery(id+"F10.wireOp",EDGE,"632d57c4-459f-459c-86cd-4f11f503a09c");
            var Q742;
            Q742=sQuery(id+"F10.wireOp",EDGE,"17d49e17-9ebc-4c9d-bee9-cad3d3ba797e");
            var Q743;
            Q743=sQuery(id+"F10.wireOp",EDGE,"650a58ed-e56e-4eff-a3bf-77fa6083a7f9");
            var Q744;
            Q744=sQuery(id+"F10.wireOp",EDGE,"8eba25e4-1cc8-496d-97a8-6cee5f62a8e5");
            var Q745;
            Q745=sQuery(id+"F10.wireOp",EDGE,"341e7885-60a8-4d7d-9e2c-f9a0d6ad32a6");
            var Q746;
            Q746=sQuery(id+"F10.wireOp",EDGE,"8864fe9c-cb63-42fb-aa65-6cb294b58472");
            var Q747;
            Q747=sQuery(id+"F10.wireOp",EDGE,"df150109-02cb-4ed6-a482-44997fc127af");
            var Q748;
            Q748=sQuery(id+"F10.wireOp",EDGE,"51c9575f-8e8a-42b4-bfb4-ed131f65ac21");
            var Q749;
            Q749=sQuery(id+"F10.wireOp",EDGE,"ba27da9f-f57e-43cd-9ef7-818eb539ecda");
            var Q750;
            Q750=sQuery(id+"F10.wireOp",EDGE,"2ef582d3-457e-46b8-b0d2-8e7bf534beb5");
            var Q751;
            Q751=sQuery(id+"F10.wireOp",EDGE,"f4e71c4f-584c-4876-893e-fc94e384602a");
            var Q752;
            Q752=sQuery(id+"F10.wireOp",EDGE,"4b260c45-91eb-413f-86fd-7b1846311688");
            var Q753;
            Q753=sQuery(id+"F10.wireOp",EDGE,"2b1bc188-5572-4955-8c0e-fbc34d6a749f");
            var Q754;
            Q754=sQuery(id+"F10.wireOp",EDGE,"2b3924cc-e5f2-4e34-b20e-3a1453064fc9");
            var Q755;
            Q755=sQuery(id+"F10.wireOp",EDGE,"e76ca23f-2134-4c28-978d-da9c496db45e");
            var Q756;
            Q756=sQuery(id+"F10.wireOp",EDGE,"a83c66d4-ddb2-401f-8ab8-430d56aaebc8");
            var Q757;
            Q757=sQuery(id+"F10.wireOp",EDGE,"e92029c8-17ce-472f-ac6d-063fda6b0f17");
            var Q758;
            Q758=sQuery(id+"F10.wireOp",EDGE,"8a8b4b13-ae68-4d44-b60a-1df739cab3a5");
            var Q759;
            Q759=sQuery(id+"F10.wireOp",EDGE,"575d7558-6b01-415c-a0bd-0362845a3543");
            var Q760;
            Q760=sQuery(id+"F10.wireOp",EDGE,"5f626950-cda3-479a-a60b-31341ad80c05");
            var Q761;
            Q761=sQuery(id+"F10.wireOp",EDGE,"c205f472-4dd6-43ba-9f23-9f3285f512e7");
            var Q762;
            Q762=sQuery(id+"F10.wireOp",EDGE,"3948a463-911b-4231-9762-0f67ca8625f5");
            var Q763;
            Q763=sQuery(id+"F10.wireOp",EDGE,"024842ff-5882-4262-9294-5ee3e414b498");
            var Q764;
            Q764=sQuery(id+"F10.wireOp",EDGE,"3d87652b-5ad1-4d7c-b317-f7c961a75782");
            var Q765;
            Q765=sQuery(id+"F10.wireOp",EDGE,"b083b74b-fc15-4798-8155-b9702577c14c");
            var Q766;
            Q766=sQuery(id+"F10.wireOp",EDGE,"3fe5ac16-b663-4502-b127-989193ca997b");
            var Q767;
            Q767=sQuery(id+"F10.wireOp",EDGE,"ac0e8499-5222-4669-ae9f-ae078ffc3f8f");
            var Q768;
            Q768=sQuery(id+"F10.wireOp",EDGE,"d36a0df4-7197-423e-9c72-d419e0c6372a");
            var Q769;
            Q769=sQuery(id+"F10.wireOp",EDGE,"cb39c1a6-b177-4b0b-9995-48f4ce787678");
            var Q770;
            Q770=sQuery(id+"F10.wireOp",EDGE,"553e6714-2197-41cc-9c57-fee89ba9631b");
            var Q771;
            Q771=sQuery(id+"F10.wireOp",EDGE,"2a7a1632-4315-45ac-9e7f-c4d6498371b7");
            var Q772;
            Q772=sQuery(id+"F10.wireOp",EDGE,"55196108-f79c-467b-910e-212d0d1a5c7c");
            var Q773;
            Q773=sQuery(id+"F10.wireOp",EDGE,"7ed16e28-1216-47c3-9b20-52b6a642ea0c");
            var Q774;
            Q774=sQuery(id+"F10.wireOp",EDGE,"f190588e-edd7-48c9-be91-2f5ac3922a97");
            var Q775;
            Q775=sQuery(id+"F10.wireOp",EDGE,"c71ccd24-2858-4b4b-9304-2200b94db335");
            var Q776;
            Q776=sQuery(id+"F10.wireOp",EDGE,"8284c83a-31e0-40af-b570-c4bb88bf7053");
            var Q777;
            Q777=sQuery(id+"F10.wireOp",EDGE,"4e6820d9-757b-450f-9d92-0a2a92f483d2");
            var Q778;
            Q778=sQuery(id+"F10.wireOp",EDGE,"71986c4f-4e72-4177-993d-ba7b74dd3c34");
            var Q779;
            Q779=sQuery(id+"F10.wireOp",EDGE,"4f5bbd12-bc41-4d38-bbbf-b30344aa69c2");
            var Q780;
            Q780=sQuery(id+"F10.wireOp",EDGE,"127bcb12-255a-42e4-bfc6-ee745b36b71b");
            var Q781;
            Q781=sQuery(id+"F10.wireOp",EDGE,"7293dd18-e83c-462f-9f49-bbc658903ee2");
            var Q782;
            Q782=sQuery(id+"F10.wireOp",EDGE,"78b398a8-c523-43ce-93b3-3ef81809a34e");
            var Q783;
            Q783=sQuery(id+"F10.wireOp",EDGE,"61ba6dbf-a9a5-4a54-8fe2-30cf40c58671");
            var Q784;
            Q784=sQuery(id+"F10.wireOp",EDGE,"695eab80-5778-4d2a-a967-95523590a93e");
            var Q785;
            Q785=sQuery(id+"F10.wireOp",EDGE,"ae4d1a7f-0e74-4bf6-8cad-73eb52bad58a");
            var Q786;
            Q786=sQuery(id+"F10.wireOp",EDGE,"879a9216-5869-419c-af57-40de632e4132");
            var Q787;
            Q787=sQuery(id+"F10.wireOp",EDGE,"63a217a4-18da-46e8-a14d-03ac1a1e6fa0");
            var Q788;
            Q788=sQuery(id+"F10.wireOp",EDGE,"b281b34d-dbb6-452e-8f1c-f498c81c1bc6");
            var Q789;
            Q789=sQuery(id+"F10.wireOp",EDGE,"acfbcfc5-b91b-421a-9e93-35cf17925930");
            var Q790;
            Q790=sQuery(id+"F10.wireOp",EDGE,"93cfac16-54a2-4fae-b436-835ee711443f");
            var Q791;
            Q791=sQuery(id+"F10.wireOp",EDGE,"218c1cbe-9206-4df0-813e-08e15e900286");
            var Q792;
            Q792=sQuery(id+"F10.wireOp",EDGE,"dc310287-a3dd-4497-b22d-72e7f38f1f6a");
            var Q793;
            Q793=sQuery(id+"F10.wireOp",EDGE,"b1b6c562-46b0-4d14-97ec-c868f13a889e");
            var Q794;
            Q794=sQuery(id+"F10.wireOp",EDGE,"fae338e1-0c2f-4f04-85fe-31596224c69f");
            var Q795;
            Q795=sQuery(id+"F10.wireOp",EDGE,"8920b0ec-28cc-4893-b7c4-2823d81c9b85");
            var Q796;
            Q796=sQuery(id+"F10.wireOp",EDGE,"db835516-2307-454a-a96f-2360decccc89");
            var Q797;
            Q797=sQuery(id+"F10.wireOp",EDGE,"a3897c3d-702c-40ab-8d5b-2253d07af62e");
            var Q798;
            Q798=sQuery(id+"F10.wireOp",EDGE,"45b27f51-6b1e-404c-b150-621b550cda29");
            var Q799;
            Q799=sQuery(id+"F10.wireOp",EDGE,"96527514-c6e5-457f-9dfb-cad305be7053");
            var Q800;
            Q800=sQuery(id+"F10.wireOp",EDGE,"551ca599-edf1-4d23-8f71-c8b516ef5e45");
            var Q801;
            Q801=sQuery(id+"F10.wireOp",EDGE,"60a2ce45-7ebd-4a0b-b696-20892b6b5fd4");
            var Q802;
            Q802=sQuery(id+"F10.wireOp",EDGE,"bb082601-0429-4a69-8aaf-748cf0a3bd51");
            var Q803;
            Q803=sQuery(id+"F10.wireOp",EDGE,"50de8e21-afe2-493a-8b9e-9c526c753117");
            var Q804;
            Q804=sQuery(id+"F10.wireOp",EDGE,"8e039c31-beaf-44f1-930d-3d5490723162");
            var Q805;
            Q805=sQuery(id+"F10.wireOp",EDGE,"a05c8136-cafa-4d90-8c10-5896799cabc1");
            var Q806;
            Q806=sQuery(id+"F10.wireOp",EDGE,"fced8d16-917b-4030-8be9-21e574ea9019");
            var Q807;
            Q807=sQuery(id+"F10.wireOp",EDGE,"5b921327-11cc-4c6a-9d3e-da7a60b70371");
            var Q808;
            Q808=sQuery(id+"F10.wireOp",EDGE,"c15b9b6b-ebf0-4485-a630-54014f60e526");
            var Q809;
            Q809=sQuery(id+"F10.wireOp",EDGE,"611f2b3e-25fb-43f5-ad49-401821710d4c");
            var Q810;
            Q810=sQuery(id+"F10.wireOp",EDGE,"71f813f2-0618-4063-bb58-9bf66633cfd6");
            var Q811;
            Q811=sQuery(id+"F10.wireOp",EDGE,"7c929200-35d5-4618-aa15-37006a409bba");
            var Q812;
            Q812=sQuery(id+"F10.wireOp",EDGE,"4fc3ca63-8b23-420c-bc18-3922111fb3fc");
            var Q813;
            Q813=sQuery(id+"F10.wireOp",EDGE,"cea6f84f-d5b7-46e6-9830-4cbe38dc4d58");
            var Q814;
            Q814=sQuery(id+"F10.wireOp",EDGE,"287fcaac-5730-4bea-978b-d4bbdf2b1102");
            var Q815;
            Q815=sQuery(id+"F10.wireOp",EDGE,"22ee65ac-b55b-446a-a2bc-23851f2e1bb4");
            var Q816;
            Q816=sQuery(id+"F10.wireOp",EDGE,"6a97c10e-a195-4429-b93b-3efe1af8a6de");
            var Q817;
            Q817=sQuery(id+"F10.wireOp",EDGE,"d1c184ba-523a-41fb-ab76-16cafddd2cb5");
            var Q818;
            Q818=sQuery(id+"F10.wireOp",EDGE,"e2a2078e-b58b-48d9-b99d-ccb217915808");
            var Q819;
            Q819=sQuery(id+"F10.wireOp",EDGE,"2d13811f-f201-4c47-8eda-440955a9e1b1");
            var Q820;
            Q820=sQuery(id+"F10.wireOp",EDGE,"f6dd1332-526b-40e6-b306-b2ae93608b30");
            var Q821;
            Q821=sQuery(id+"F10.wireOp",EDGE,"cbdda709-ba47-41fb-8ef2-dbc91847c792");
            var Q822;
            Q822=sQuery(id+"F10.wireOp",EDGE,"6c63193d-1b55-4b07-b7b1-5980b4fb4bd0");
            var Q823;
            Q823=sQuery(id+"F10.wireOp",EDGE,"f4f17ff0-e866-47f5-9298-625cd33e876f");
            var Q824;
            Q824=sQuery(id+"F10.wireOp",EDGE,"7425a041-5782-4df6-96c5-af4ff3f307bf");
            var Q825;
            Q825=sQuery(id+"F10.wireOp",EDGE,"37983c59-b627-482d-9f38-51c90f7e243b");
            var Q826;
            Q826=sQuery(id+"F10.wireOp",EDGE,"5c314d8b-3c91-42fb-9015-ce34fee0e4a8");
            var Q827;
            Q827=sQuery(id+"F10.wireOp",EDGE,"d06b672b-0916-4dbe-9dee-fe19a629fd41");
            var Q828;
            Q828=sQuery(id+"F10.wireOp",EDGE,"085b4253-ad53-4362-ba2b-767319cc0111");
            var Q829;
            Q829=sQuery(id+"F10.wireOp",EDGE,"57e044f1-bfb5-4b47-ac7e-89acb179fc94");
            var Q830;
            Q830=sQuery(id+"F10.wireOp",EDGE,"71cccca2-aae3-4fd1-8191-36b7d2c93926");
            var Q831;
            Q831=sQuery(id+"F10.wireOp",EDGE,"2c47a1e8-6b3e-4b4a-bddb-50330a4bac8f");
            var Q832;
            Q832=sQuery(id+"F10.wireOp",EDGE,"9056641e-57e8-4778-81a1-f2b00cde10e8");
            var Q833;
            Q833=sQuery(id+"F10.wireOp",EDGE,"551fb1e5-fbc9-441b-8f08-21985df6095a");
            var Q834;
            Q834=sQuery(id+"F10.wireOp",EDGE,"1ddcd1b6-d665-4571-b79f-133877dbe056");
            var Q835;
            Q835=sQuery(id+"F10.wireOp",EDGE,"2bf8e20f-403e-45e2-b6f2-ba23583b9e72");
            var Q836;
            Q836=sQuery(id+"F10.wireOp",EDGE,"ac16a70b-69ae-4965-a064-6c572f792793");
            var Q837;
            Q837=sQuery(id+"F10.wireOp",EDGE,"11213b20-abf7-4519-84f8-1867946fc5d7");
            var Q838;
            Q838=sQuery(id+"F10.wireOp",EDGE,"8fae5e85-6f66-43f3-a6aa-2c40098a9bb9");
            var Q839;
            Q839=sQuery(id+"F10.wireOp",EDGE,"ce084aa8-a230-453c-8cd0-966a4217af2d");
            var Q840;
            Q840=sQuery(id+"F10.wireOp",EDGE,"581c583a-3e5e-4347-969a-ab18ae64eedf");
            var Q841;
            Q841=sQuery(id+"F10.wireOp",EDGE,"ba095cea-f083-4679-8295-354ca7e5c0e4");
            var Q842;
            Q842=sQuery(id+"F10.wireOp",EDGE,"01101b61-10ae-4f0c-a21b-8ec3301d18bc");
            var Q843;
            Q843=sQuery(id+"F10.wireOp",EDGE,"9e10d4c9-e960-4195-99e8-8230bd788068");
            var Q844;
            Q844=sQuery(id+"F10.wireOp",EDGE,"7cbf1c63-8381-4e84-a359-4eeb30618729");
            var Q845;
            Q845=sQuery(id+"F10.wireOp",EDGE,"0c643472-d364-48b6-859d-aa409598de17");
            var Q846;
            Q846=sQuery(id+"F10.wireOp",EDGE,"f668e986-cc60-4608-a4e4-87970213da46");
            var Q847;
            Q847=sQuery(id+"F10.wireOp",EDGE,"d8467427-fe48-4211-85f5-5c1f0787b150");
            var Q848;
            Q848=sQuery(id+"F10.wireOp",EDGE,"16e07579-3509-4051-ba64-ee0d1b4963ff");
            var Q849;
            Q849=sQuery(id+"F10.wireOp",EDGE,"4930c49e-1c15-4394-8bac-e8dcf702f323");
            var Q850;
            Q850=sQuery(id+"F10.wireOp",EDGE,"69821b9c-5174-4ee7-bb3a-e375ea1d9856");
            var Q851;
            Q851=sQuery(id+"F10.wireOp",EDGE,"7de7d614-9c49-47d5-82a0-68dab3429fb3");
            var Q852;
            Q852=sQuery(id+"F10.wireOp",EDGE,"53db86ce-774c-46eb-a0f4-0b48025cf0c7");
            var Q853;
            Q853=sQuery(id+"F10.wireOp",EDGE,"448c591c-2a62-41b1-b4e8-c613203e7d71");
            var Q854;
            Q854=sQuery(id+"F10.wireOp",EDGE,"11a6b6ad-a40a-4a19-8548-6f17a74157de");
            var Q855;
            Q855=sQuery(id+"F10.wireOp",EDGE,"4a35c531-2c09-458f-9363-499a8fbc5367");
            var Q856;
            Q856=sQuery(id+"F10.wireOp",EDGE,"8079931e-130f-4feb-ae8a-48eca2562e02");
            var Q857;
            Q857=sQuery(id+"F10.wireOp",EDGE,"138eb38f-0d40-425b-bd77-9b21f3172b4d");
            var Q858;
            Q858=sQuery(id+"F10.wireOp",EDGE,"b559b075-9ab5-4e4c-ab4a-6ad23a492250");
            var Q859;
            Q859=sQuery(id+"F10.wireOp",EDGE,"2c72a2c6-3887-4f1c-b4cd-7706f891f14c");
            var Q860;
            Q860=sQuery(id+"F10.wireOp",EDGE,"ee21947f-a335-43a8-b740-e90df95ee613");
            var Q861;
            Q861=sQuery(id+"F10.wireOp",EDGE,"95bf51cd-767c-4dd9-92e5-5a932eece85c");
            var Q862;
            Q862=sQuery(id+"F10.wireOp",EDGE,"9e3eef52-e49e-4f33-9e23-8fc7ad4d75c1");
            var Q863;
            Q863=sQuery(id+"F10.wireOp",EDGE,"a0b4f158-25e0-4ee6-933d-8f9c69eee0e6");
            var Q864;
            Q864=sQuery(id+"F10.wireOp",EDGE,"f1c65bcf-8dec-4a5c-bf4c-174761d6d386");
            var Q865;
            Q865=sQuery(id+"F10.wireOp",EDGE,"d72df36d-5568-4ca9-8223-2eb2799fa47b");
            var Q866;
            Q866=sQuery(id+"F10.wireOp",EDGE,"2a8da681-543d-4116-a782-924a6a2b2371");
            var Q867;
            Q867=sQuery(id+"F10.wireOp",EDGE,"0fbf85dd-a3d1-4e42-834d-72db65db2f2e");
            var Q868;
            Q868=sQuery(id+"F10.wireOp",EDGE,"43a1b8bd-04a0-4417-98cc-e4eeadc24754");
            var Q869;
            Q869=sQuery(id+"F10.wireOp",EDGE,"7e011562-93c8-4803-b8ed-5ce684e261e1");
            var Q870;
            Q870=sQuery(id+"F10.wireOp",EDGE,"033470c6-4480-4d57-8aba-70e388395d37");
            var Q871;
            Q871=sQuery(id+"F10.wireOp",EDGE,"ef8fa2e8-2cdd-4118-8f54-7312f988146c");
            var Q872;
            Q872=sQuery(id+"F10.wireOp",EDGE,"36f436ea-a38d-4d94-ba7c-9c1397ca890f");
            var Q873;
            Q873=sQuery(id+"F10.wireOp",EDGE,"fd768a38-a60c-4c2c-ab3b-f106dae49ecd");
            var Q874;
            Q874=sQuery(id+"F10.wireOp",EDGE,"9e7773a6-6906-44a1-9d29-1ec59e216594");
            var Q875;
            Q875=sQuery(id+"F10.wireOp",EDGE,"04bcb646-3db9-411e-905c-dfb0ee131602");
            var Q876;
            Q876=sQuery(id+"F10.wireOp",EDGE,"1f12585a-3178-4466-a818-74a244fe94e4");
            var Q877;
            Q877=sQuery(id+"F10.wireOp",EDGE,"565e05ce-1c92-4425-aa9b-046d5ed4ab59");
            var Q878;
            Q878=sQuery(id+"F10.wireOp",EDGE,"7c3b3c52-b6ba-49f7-be96-0c7c2cf2bd5b");
            var Q879;
            Q879=sQuery(id+"F10.wireOp",EDGE,"74508dc7-0c4e-4169-bd3f-7e638f431194");
            var Q880;
            Q880=sQuery(id+"F10.wireOp",EDGE,"48c19228-68d7-4af6-a781-27060581a3ad");
            var Q881;
            Q881=sQuery(id+"F10.wireOp",EDGE,"52eb839f-e950-4c1a-9b40-55dec6b52157");
            var Q882;
            Q882=sQuery(id+"F10.wireOp",EDGE,"ecec25be-73c6-4fc0-84a6-f05937f4a223");
            var Q883;
            Q883=sQuery(id+"F10.wireOp",EDGE,"b9ea02e6-316d-455a-af45-2781b9d31915");
            var Q884;
            Q884=sQuery(id+"F10.wireOp",EDGE,"04fdbb56-6b68-40e6-8c51-24c3eea9ef33");
            var Q885;
            Q885=sQuery(id+"F10.wireOp",EDGE,"eeb587d9-596e-46ec-b652-df7ca6794dc3");
            var Q886;
            Q886=sQuery(id+"F10.wireOp",EDGE,"bbba5548-a7eb-4958-84f5-e26f8a076a07");
            var Q887;
            Q887=sQuery(id+"F10.wireOp",EDGE,"879460d0-fe4c-4c11-b1ed-f27c5ec2843e");
            var Q888;
            Q888=sQuery(id+"F10.wireOp",EDGE,"258c2882-9d44-4086-9b9a-913e2704099e");
            var Q889;
            Q889=sQuery(id+"F10.wireOp",EDGE,"5d28341b-a339-490f-81d4-6a5ab095302b");
            var Q890;
            Q890=sQuery(id+"F10.wireOp",EDGE,"c408a19b-5490-4da5-949c-3e3285422494");
            var Q891;
            Q891=sQuery(id+"F10.wireOp",EDGE,"d0cc5e58-e66f-4716-8427-659fd53f3325");
            var Q892;
            Q892=sQuery(id+"F10.wireOp",EDGE,"59c11dd6-d048-4f03-9485-3e330385221a");
            var Q893;
            Q893=sQuery(id+"F10.wireOp",EDGE,"e33a1413-4816-4190-9b91-91d526f3e3d5");
            var Q894;
            Q894=sQuery(id+"F10.wireOp",EDGE,"e9288e44-1aa2-4aca-a78c-7a1023f462d9");
            var Q895;
            Q895=sQuery(id+"F10.wireOp",EDGE,"6cf10332-5ddd-46ca-b011-52e26539eed6");
            var Q896;
            Q896=sQuery(id+"F10.wireOp",EDGE,"102bcf15-ff46-4b1c-9d0c-dff027766b44");
            var Q897;
            Q897=sQuery(id+"F10.wireOp",EDGE,"8cfe30df-2920-41de-baf6-efc2ff3869d4");
            var Q898;
            Q898=sQuery(id+"F10.wireOp",EDGE,"f3fd987a-9e56-4334-8b37-da7d8d07eeaa");
            var Q899;
            Q899=sQuery(id+"F10.wireOp",EDGE,"f9338bd1-3307-4afc-a5fa-0e7ea8e58af9");
            var Q900;
            Q900=sQuery(id+"F10.wireOp",EDGE,"6de65f83-c72e-4c32-a8c5-d22833155ca8");
            var Q901;
            Q901=sQuery(id+"F10.wireOp",EDGE,"a1acb76c-4928-464b-a1ee-77745dcdb5e8");
            var Q902;
            Q902=sQuery(id+"F10.wireOp",EDGE,"180b0184-b978-4a42-adad-da565bf110e9");
            var Q903;
            Q903=sQuery(id+"F10.wireOp",EDGE,"74063b9e-bb67-447c-a245-fc630ae9f890");
            var Q904;
            Q904=sQuery(id+"F10.wireOp",EDGE,"a8d127ad-dc7c-4586-9ab0-c2b86006ffa2");
            var Q905;
            Q905=sQuery(id+"F10.wireOp",EDGE,"e1a1d20e-e778-4c3b-b955-cfd1a8560add");
            var Q906;
            Q906=sQuery(id+"F10.wireOp",EDGE,"35e80c1d-bb2a-4532-b48e-7146fb818780");
            var Q907;
            Q907=sQuery(id+"F10.wireOp",EDGE,"002497d1-135d-453d-a4e5-4130f3e8ab46");
            var Q908;
            Q908=sQuery(id+"F10.wireOp",EDGE,"25125acf-d809-4590-b7e1-a50de8fe56a7");
            var Q909;
            Q909=sQuery(id+"F10.wireOp",EDGE,"fb3a741e-fb2d-4734-9a19-2c88fbb04f7d");
            var Q910;
            Q910=sQuery(id+"F10.wireOp",EDGE,"78b2f7bc-f8a7-438d-a506-c232fd7c45a0");
            var Q911;
            Q911=sQuery(id+"F10.wireOp",EDGE,"1aa81e51-a325-4772-a354-33ed3d533186");
            var Q912;
            Q912=sQuery(id+"F10.wireOp",EDGE,"d944c109-3ec7-48cd-b3f7-71457e030849");
            var Q913;
            Q913=sQuery(id+"F10.wireOp",EDGE,"d897f5d4-e7b3-4473-bc3f-504fc4968f62");
            var Q914;
            Q914=sQuery(id+"F10.wireOp",EDGE,"8e6e95aa-0688-4743-974c-a340879e40ea");
            var Q915;
            Q915=sQuery(id+"F10.wireOp",EDGE,"bb43f774-085a-48c4-b83c-3f0f8f263d1d");
            var Q916;
            Q916=sQuery(id+"F10.wireOp",EDGE,"2dcd3690-5400-467d-a630-013fa5b2dce5");
            var Q917;
            Q917=sQuery(id+"F10.wireOp",EDGE,"5389df34-4bc9-42b5-9918-5090ab8c3bf7");
            var Q918;
            Q918=sQuery(id+"F10.wireOp",EDGE,"3bd95929-379b-4957-8739-cd6fafc00583");
            var Q919;
            Q919=sQuery(id+"F10.wireOp",EDGE,"5a21de9e-2fb8-4e9c-918e-5ce0def3846d");
            var Q920;
            Q920=sQuery(id+"F10.wireOp",EDGE,"c3ddcc0a-e294-4ca4-8fa5-77631c4917fc");
            var Q921;
            Q921=sQuery(id+"F10.wireOp",EDGE,"afbf21d0-5bf9-4b52-8f18-61eca8c102b7");
            var Q922;
            Q922=sQuery(id+"F10.wireOp",EDGE,"782e3a3f-cdd7-4ea9-aa1e-5b20b1929614");
            var Q923;
            Q923=sQuery(id+"F10.wireOp",EDGE,"d02508a8-633a-432c-9c5b-63ff88bb7686");
            var Q924;
            Q924=sQuery(id+"F10.wireOp",EDGE,"31495c9e-600b-4ba5-99d7-c0b17d01b757");
            var Q925;
            Q925=sQuery(id+"F10.wireOp",EDGE,"d62d6ac3-6938-419a-84e0-0530087f6683");
            var Q926;
            Q926=sQuery(id+"F10.wireOp",EDGE,"d23190de-9627-41ec-9f2f-9448cb933988");
            var Q927;
            Q927=sQuery(id+"F10.wireOp",EDGE,"3f106ead-49f1-42c4-814e-f19610026bce");
            var Q928;
            Q928=sQuery(id+"F10.wireOp",EDGE,"1e4668a6-85c8-49a8-8c2a-62525bdaf7e1");
            var Q929;
            Q929=sQuery(id+"F10.wireOp",EDGE,"be6b7f65-9a7e-42dc-bca0-4ae79f772c3e");
            var Q930;
            Q930=sQuery(id+"F10.wireOp",EDGE,"d236af05-9539-485d-880b-9f7c6fc2af1d");
            var Q931;
            Q931=sQuery(id+"F10.wireOp",EDGE,"580c7986-a753-486b-8a11-33e38285aafb");
            var Q932;
            Q932=sQuery(id+"F10.wireOp",EDGE,"dca793ab-743f-422a-94cd-814b3434b956");
            var Q933;
            Q933=sQuery(id+"F10.wireOp",EDGE,"60a64488-1f14-407f-bfd4-4a9bfacc3a0c");
            var Q934;
            Q934=sQuery(id+"F10.wireOp",EDGE,"441cd9f9-9aa6-48e5-89a0-53599ea7bc89");
            var Q935;
            Q935=sQuery(id+"F10.wireOp",EDGE,"8e9550df-59b8-4800-a3f6-e9f7a6e69d4e");
            var Q936;
            Q936=sQuery(id+"F10.wireOp",EDGE,"b8373585-b0e5-437b-ac25-e23f75799152");
            var Q937;
            Q937=sQuery(id+"F10.wireOp",EDGE,"0b65a080-7eff-44be-8db5-b305ca868c2f");
            var Q938;
            Q938=sQuery(id+"F10.wireOp",EDGE,"919cbadf-d5de-40a1-a8b2-a71e6fce0c1d");
            var Q939;
            Q939=sQuery(id+"F10.wireOp",EDGE,"bbc11532-89b4-411d-aac6-6476c1a2c1bf");
            var Q940;
            Q940=sQuery(id+"F10.wireOp",EDGE,"fd96674d-0d67-42b7-bda0-c011b8249262");
            var Q941;
            Q941=sQuery(id+"F10.wireOp",EDGE,"ca86035d-19c1-4da0-b1bf-ba010d9e4275");
            var Q942;
            Q942=sQuery(id+"F10.wireOp",EDGE,"52d84926-258d-4e3e-bd3c-e3a0b3163d12");
            var Q943;
            Q943=sQuery(id+"F10.wireOp",EDGE,"87e535c5-c248-4d5d-bcc9-c9b74aaeb2a7");
            var Q944;
            Q944=sQuery(id+"F10.wireOp",EDGE,"bb863649-f605-4a72-a32f-7d6e9b9d8468");
            var Q945;
            Q945=sQuery(id+"F10.wireOp",EDGE,"b7a7718e-c308-424a-9bcb-0193b8a7c1ec");
            var Q946;
            Q946=sQuery(id+"F10.wireOp",EDGE,"447f6979-9669-48d3-85c3-44d484e5ae47");
            var Q947;
            Q947=sQuery(id+"F10.wireOp",EDGE,"7c829029-49c7-42d1-8519-f2cb15d41752");
            var Q948;
            Q948=sQuery(id+"F10.wireOp",EDGE,"5f316f7e-31db-4ca3-ba52-4726bb697af1");
            var Q949;
            Q949=sQuery(id+"F10.wireOp",EDGE,"fb45c3e0-c46d-461b-83e9-39699c6948dd");
            var Q950;
            Q950=sQuery(id+"F10.wireOp",EDGE,"0db5f9aa-361b-482f-a553-5c2bd1f9ff00");
            var Q951;
            Q951=sQuery(id+"F10.wireOp",EDGE,"54cabdf9-1714-4aed-b7f9-568be1ddc942");
            var Q952;
            Q952=sQuery(id+"F10.wireOp",EDGE,"8fdabfbd-768e-48ef-93d4-0a76c2a7848d");
            var Q953;
            Q953=sQuery(id+"F10.wireOp",EDGE,"d857d7ea-90c3-4f64-883f-ad4b3b420a4a");
            var Q954;
            Q954=sQuery(id+"F10.wireOp",EDGE,"53a2d658-34f8-4dd8-af2a-7f5f038784d1");
            var Q955;
            Q955=sQuery(id+"F10.wireOp",EDGE,"d1e3ada4-d222-4832-a16d-fb18d1d147f4");
            var Q956;
            Q956=sQuery(id+"F10.wireOp",EDGE,"50924a8c-bf73-4132-ae90-b459dba42a6e");
            var Q957;
            Q957=sQuery(id+"F10.wireOp",EDGE,"e57c4b97-ddb4-4db2-8aa6-0124b5905929");
            var Q958;
            Q958=sQuery(id+"F10.wireOp",EDGE,"703f85e9-bc2f-4dc4-8d66-1b2e08679416");
            var Q959;
            Q959=sQuery(id+"F10.wireOp",EDGE,"c4d50b70-14d0-40de-be54-de9fa38885e8");
            var Q960;
            Q960=sQuery(id+"F10.wireOp",EDGE,"5df17430-6f51-4c52-bf25-a00630315d3e");
            var Q961;
            Q961=sQuery(id+"F10.wireOp",EDGE,"5ee55a4f-f7f2-433e-91e0-c937eb7e6380");
            var Q962;
            Q962=sQuery(id+"F10.wireOp",EDGE,"76d1e230-9763-4300-aff6-83dbd136e6bd");
            var Q963;
            Q963=sQuery(id+"F10.wireOp",EDGE,"9d599d31-b9ee-4c1b-ad40-c25f00806795");
            var Q964;
            Q964=sQuery(id+"F10.wireOp",EDGE,"6830ec72-f611-44ac-a58c-29f8ffcf1ece");
            var Q965;
            Q965=sQuery(id+"F10.wireOp",EDGE,"f6d2bd8b-a518-4eb8-a9d0-0bc6c5734600");
            var Q966;
            Q966=sQuery(id+"F10.wireOp",EDGE,"ecad1160-8141-4311-ba55-a12c3d478ec1");
            var Q967;
            Q967=sQuery(id+"F10.wireOp",EDGE,"e38c6188-b188-4976-8dd7-6a11708f44cd");
            var Q968;
            Q968=sQuery(id+"F10.wireOp",EDGE,"ec9e7b21-d8d0-4454-83c2-8de0186171fd");
            var Q969;
            Q969=sQuery(id+"F10.wireOp",EDGE,"aeb7c18b-dadb-41c5-9770-d3131b08832e");
            var Q970;
            Q970=sQuery(id+"F10.wireOp",EDGE,"27f3ce3a-ccf5-47c9-a59f-4b118efab28e");
            var Q971;
            Q971=sQuery(id+"F10.wireOp",EDGE,"49048e96-4b8f-4706-9a6f-cb3a4119221e");
            var Q972;
            Q972=sQuery(id+"F10.wireOp",EDGE,"f14d3df0-9540-4187-982b-eb9193105db2");
            var Q973;
            Q973=sQuery(id+"F10.wireOp",EDGE,"be31c577-bd91-4bfe-9078-476712839680");
            var Q974;
            Q974=sQuery(id+"F10.wireOp",EDGE,"5672febc-8222-4f06-b111-185b921584a0");
            var Q975;
            Q975=sQuery(id+"F10.wireOp",EDGE,"c84d264e-1747-4d5f-a119-df86a7f580cf");
            var Q976;
            Q976=sQuery(id+"F10.wireOp",EDGE,"91551187-263d-4e7f-a86f-cfbc2bba3564");
            var Q977;
            Q977=sQuery(id+"F10.wireOp",EDGE,"6ad6aa39-0424-40c8-bafd-233d7a74e04c");
            var Q978;
            Q978=sQuery(id+"F10.wireOp",EDGE,"4a3ef99f-7394-429d-8cf8-3ab27e096603");
            var Q979;
            Q979=sQuery(id+"F10.wireOp",EDGE,"7dbfa60d-7cb3-4bfd-b9c1-ebe0fae399c7");
            var Q980;
            Q980=sQuery(id+"F10.wireOp",EDGE,"5bb411f7-8756-4c20-9275-dcc6b7295b54");
            var Q981;
            Q981=sQuery(id+"F10.wireOp",EDGE,"502c5748-ada2-4362-9aee-e20d66887432");
            var Q982;
            Q982=sQuery(id+"F10.wireOp",EDGE,"579fe276-e4ae-43f8-947e-b2845f8a9e78");
            var Q983;
            Q983=sQuery(id+"F10.wireOp",EDGE,"f4d36491-bf7e-44b1-823b-477a7ba1bdc8");
            var Q984;
            Q984=sQuery(id+"F10.wireOp",EDGE,"490d5625-ebe3-432e-b00b-32892341e328");
            var Q985;
            Q985=sQuery(id+"F10.wireOp",EDGE,"d1455dd9-543d-4019-bff0-3c0fddd5ea84");
            var Q986;
            Q986=sQuery(id+"F10.wireOp",EDGE,"503190eb-5d47-4888-8c07-7ce83efdc22b");
            var Q987;
            Q987=sQuery(id+"F10.wireOp",EDGE,"76ec5762-d2ee-4546-a951-279f69ed4ed2");
            var Q988;
            Q988=sQuery(id+"F10.wireOp",EDGE,"26538df8-d110-4685-8000-c85eeba40ea8");
            var Q989;
            Q989=sQuery(id+"F10.wireOp",EDGE,"aad27d6c-4a27-44d1-90e0-3734809bf21f");
            var Q990;
            Q990=sQuery(id+"F10.wireOp",EDGE,"1ad501ff-50a5-4c08-823b-f1d8f476402d");
            var Q991;
            Q991=sQuery(id+"F10.wireOp",EDGE,"31c83349-a921-481b-b67d-754c6903c50d");
            var Q992;
            Q992=sQuery(id+"F10.wireOp",EDGE,"d67b67a3-4cce-42d1-b24b-1a9b3ddcbbe3");
            var Q993;
            Q993=sQuery(id+"F10.wireOp",EDGE,"bf806f78-7579-436c-9876-7284feae8356");
            var Q994;
            Q994=sQuery(id+"F10.wireOp",EDGE,"c2e51e00-5746-469d-ba13-b30d29f38af5");
            var Q995;
            Q995=sQuery(id+"F10.wireOp",EDGE,"ed4ab63d-8236-47bf-8d8d-dc8040fe36fd");
            var Q996;
            Q996=sQuery(id+"F10.wireOp",EDGE,"0a700f0e-ce43-4cf1-9a21-08e839956be3");
            var Q997;
            Q997=sQuery(id+"F10.wireOp",EDGE,"687b1a0a-e611-46a4-a2e3-8c3b38cb73e5");
            var Q998;
            Q998=sQuery(id+"F10.wireOp",EDGE,"0fb81446-cf65-4ed9-a492-65f65083df9c");
            var Q999;
            Q999=sQuery(id+"F10.wireOp",EDGE,"b2543269-2f43-4b6e-a64e-77cef182f79e");
            var Q1000;
            Q1000=sQuery(id+"F10.wireOp",EDGE,"77b2ee3b-1233-4cae-8b65-95ad98971051");
            var Q1001;
            Q1001=sQuery(id+"F10.wireOp",EDGE,"61eca9fa-4d5c-42f0-a6b5-79c419b13868");
            var Q1002;
            Q1002=sQuery(id+"F10.wireOp",EDGE,"e1ba6f61-d67a-4be5-9356-575ced2accbf");
            var Q1003;
            Q1003=sQuery(id+"F10.wireOp",EDGE,"c3e0c6c4-49f2-4427-bcf6-94f884720fdf");
            var Q1004;
            Q1004=sQuery(id+"F10.wireOp",EDGE,"d8dde592-ed1c-4cdc-ad1f-1d7832a6bc0b");
            var Q1005;
            Q1005=sQuery(id+"F10.wireOp",EDGE,"1ae7295e-1204-49f7-985a-80980fb7c1bd");
            var Q1006;
            Q1006=sQuery(id+"F10.wireOp",EDGE,"04abe12d-2b0d-46ed-8ecb-257bda12d3f0");
            var Q1007;
            Q1007=sQuery(id+"F10.wireOp",EDGE,"648b8fd1-5fe0-4ea8-b39a-e9db4555a3ef");
            var Q1008;
            Q1008=sQuery(id+"F10.wireOp",EDGE,"e66ffb64-5222-408d-b004-2d592a1aeb08");
            var Q1009;
            Q1009=sQuery(id+"F10.wireOp",EDGE,"2b520310-ddd6-4df8-a092-d716017fa113");
            var Q1010;
            Q1010=sQuery(id+"F10.wireOp",EDGE,"8ab31891-8c6b-4773-aca7-e64ea8d210eb");
            var Q1011;
            Q1011=sQuery(id+"F10.wireOp",EDGE,"bd03f752-7df9-451b-b0f5-a6e9fe20a9f8");
            var Q1012;
            Q1012=sQuery(id+"F10.wireOp",EDGE,"a85022a2-70c4-4b96-9e7f-3d76c4c561f4");
            var Q1013;
            Q1013=sQuery(id+"F10.wireOp",EDGE,"a16fd48e-bfb3-4784-ab72-94a059bb9086");
            var Q1014;
            Q1014=sQuery(id+"F10.wireOp",EDGE,"bccd108d-d884-4459-8ce2-ea3cf637a6b0");
            var Q1015;
            Q1015=sQuery(id+"F10.wireOp",EDGE,"23f884f0-d834-4929-a185-90caa658f6f2");
            var Q1016;
            Q1016=sQuery(id+"F10.wireOp",EDGE,"7fa3dfe7-1f46-4fbf-8b8d-e8a02827bbb1");
            var Q1017;
            Q1017=sQuery(id+"F10.wireOp",EDGE,"968f4710-aea2-4707-b414-566d45cd5cb7");
            var Q1018;
            Q1018=sQuery(id+"F10.wireOp",EDGE,"fc71b90b-256c-47cb-8c53-e02bf22232c5");
            var Q1019;
            Q1019=sQuery(id+"F10.wireOp",EDGE,"6cf5618a-a06e-43ae-b911-34dd4b386bd0");
            var Q1020;
            Q1020=sQuery(id+"F10.wireOp",EDGE,"2af066ef-3542-424b-adcb-ed9315638d95");
            var Q1021;
            Q1021=sQuery(id+"F10.wireOp",EDGE,"2d988f3e-511f-463b-b342-860d1006a3b1");
            var Q1022;
            Q1022=sQuery(id+"F10.wireOp",EDGE,"a057a765-0090-42d3-a590-33ae782c4be5");
            var Q1023;
            Q1023=sQuery(id+"F10.wireOp",EDGE,"14c789fd-fc62-4f00-982f-fdb0fb99d8cd");
            var Q1024;
            Q1024=sQuery(id+"F10.wireOp",EDGE,"c7451080-b120-4845-953a-e16fd9055645");
            var Q1025;
            Q1025=sQuery(id+"F10.wireOp",EDGE,"60cf24e4-a785-4e96-bae4-fc8f718d8c2f");
            var Q1026;
            Q1026=sQuery(id+"F10.wireOp",EDGE,"3daa96fe-6ff9-4e48-863f-24d2091f7e8f");
            var Q1027;
            Q1027=sQuery(id+"F10.wireOp",EDGE,"fccc54d7-dfb1-423c-9e83-6d7189085ce3");
            var Q1028;
            Q1028=sQuery(id+"F10.wireOp",EDGE,"ef0b99b9-fb42-453b-95a8-c1aa6b349f7b");
            var Q1029;
            Q1029=sQuery(id+"F10.wireOp",EDGE,"36f405bf-4185-4406-bf6e-0b748405ecfa");
            var Q1030;
            Q1030=sQuery(id+"F10.wireOp",EDGE,"65d23145-7639-4a02-a13d-94aa3fd39c08");
            var Q1031;
            Q1031=sQuery(id+"F10.wireOp",EDGE,"97589f1b-b23b-4959-9231-7f2591eeb8db");
            var Q1032;
            Q1032=sQuery(id+"F10.wireOp",EDGE,"e71d632a-2d6a-4d29-bb15-522372e0441b");
            var Q1033;
            Q1033=sQuery(id+"F10.wireOp",EDGE,"dc173140-66df-40fc-b4ec-2aebd8b5dbcf");
            var Q1034;
            Q1034=sQuery(id+"F10.wireOp",EDGE,"c82bc687-342d-4b93-b0ec-02efa38038ee");
            var Q1035;
            Q1035=sQuery(id+"F10.wireOp",EDGE,"573c77e3-566f-4d73-8302-f9af43e3f813");
            var Q1036;
            Q1036=sQuery(id+"F10.wireOp",EDGE,"421860c8-2b7f-48bb-b318-84374684f511");
            var Q1037;
            Q1037=sQuery(id+"F10.wireOp",EDGE,"af09ca0e-884b-42d1-8924-c50661593dda");
            var Q1038;
            Q1038=sQuery(id+"F10.wireOp",EDGE,"080cca05-5745-4666-a0bc-ba321d72b0b8");
            var Q1039;
            Q1039=sQuery(id+"F10.wireOp",EDGE,"99a8c1f2-7e34-49a9-a560-69af8f903be9");
            var Q1040;
            Q1040=sQuery(id+"F10.wireOp",EDGE,"8d855e45-79fc-4666-ab64-cd0855dda1df");
            var Q1041;
            Q1041=sQuery(id+"F10.wireOp",EDGE,"11a01b1b-bec1-4a3a-b36a-533aad55627b");
            var Q1042;
            Q1042=sQuery(id+"F10.wireOp",EDGE,"c95cd802-fbdd-4be8-88c0-31a4b257896d");
            var Q1043;
            Q1043=sQuery(id+"F10.wireOp",EDGE,"97390ccd-7361-4338-8946-e4617d01b299");
            var Q1044;
            Q1044=sQuery(id+"F10.wireOp",EDGE,"c7f83f3b-95d3-4663-bb89-0913535e9d08");
            var Q1045;
            Q1045=sQuery(id+"F10.wireOp",EDGE,"42bf10a5-c81d-413b-af96-3a0a748827a9");
            var Q1046;
            Q1046=sQuery(id+"F10.wireOp",EDGE,"6853bac2-0357-4c83-b1c3-0efd1a4f7382");
            var Q1047;
            Q1047=sQuery(id+"F10.wireOp",EDGE,"1bfd9fe1-e734-41a6-aa35-ec2fc254223d");
            var Q1048;
            Q1048=sQuery(id+"F10.wireOp",EDGE,"e10e50ca-828a-471a-b803-b293f42eb262");
            var Q1049;
            Q1049=sQuery(id+"F10.wireOp",EDGE,"93a074f1-acc5-4fef-9ea7-0a19a0bd6e9a");
            var Q1050;
            Q1050=sQuery(id+"F10.wireOp",EDGE,"e31f8a8f-03a6-4327-975b-fb0eb8e48624");
            var Q1051;
            Q1051=sQuery(id+"F10.wireOp",EDGE,"d3f11c5a-8708-4e9e-afd5-53f622a8c5f1");
            var Q1052;
            Q1052=sQuery(id+"F10.wireOp",EDGE,"79529fe8-67fc-4bc8-a2c2-f606280341f0");
            var Q1053;
            Q1053=sQuery(id+"F10.wireOp",EDGE,"2500285c-fdf5-45ea-8cda-267ba3ac2826");
            var Q1054;
            Q1054=sQuery(id+"F10.wireOp",EDGE,"30858f91-7910-4495-8166-94848e4778e0");
            var Q1055;
            Q1055=sQuery(id+"F10.wireOp",EDGE,"7953152b-b199-49b6-b936-5e87683a4b1b");
            var Q1056;
            Q1056=sQuery(id+"F10.wireOp",EDGE,"9deb1da1-544e-49e4-93f2-fd2a9773ba36");
            var Q1057;
            Q1057=sQuery(id+"F10.wireOp",EDGE,"ab94ff9f-bf98-4fa2-b06c-f8e1a1e83ab6");
            var Q1058;
            Q1058=sQuery(id+"F10.wireOp",EDGE,"0f1e6da2-90d4-4da2-b365-4e4451d85227");
            var Q1059;
            Q1059=sQuery(id+"F10.wireOp",EDGE,"c29255bd-c01b-4d6b-b8aa-cc56afcd8f85");
            var Q1060;
            Q1060=sQuery(id+"F10.wireOp",EDGE,"0a1e9212-a8c9-4f14-993d-adb8c4c7b132");
            var Q1061;
            Q1061=sQuery(id+"F10.wireOp",EDGE,"db36ab59-a9de-4dbf-870a-0b0034753b7e");
            var Q1062;
            Q1062=sQuery(id+"F10.wireOp",EDGE,"75613657-2ed1-4e35-b664-5905ba237684");
            var Q1063;
            Q1063=sQuery(id+"F10.wireOp",EDGE,"60653a51-a6fc-4107-a2e2-02c6e3a71644");
            var Q1064;
            Q1064=sQuery(id+"F10.wireOp",EDGE,"69a528cf-3e59-4e15-b5f8-0c334ec103f7");
            var Q1065;
            Q1065=sQuery(id+"F10.wireOp",EDGE,"5f4510df-9061-4b20-84b0-620c6dd7bfaf");
            var Q1066;
            Q1066=sQuery(id+"F10.wireOp",EDGE,"2b01cd44-11bc-47ef-bdad-b8336ede22a1");
            var Q1067;
            Q1067=sQuery(id+"F10.wireOp",EDGE,"a531f2fb-baa3-4dfc-afe0-232b0afc91ca");
            var Q1068;
            Q1068=sQuery(id+"F10.wireOp",EDGE,"41038112-24bf-4262-aa3b-2e87b70629df");
            var Q1069;
            Q1069=sQuery(id+"F10.wireOp",EDGE,"b5e7914f-7e81-406c-9b64-3d1b507139a3");
            var Q1070;
            Q1070=sQuery(id+"F10.wireOp",EDGE,"fc555144-9ab0-45ce-9d11-595174710f94");
            var Q1071;
            Q1071=sQuery(id+"F10.wireOp",EDGE,"fb1c18fd-068e-4932-b34a-fe20a2d655fa");
            var Q1072;
            Q1072=sQuery(id+"F10.wireOp",EDGE,"59c53d00-7583-4c10-9312-2056714a44fd");
            var Q1073;
            Q1073=sQuery(id+"F10.wireOp",EDGE,"12337d02-8f34-4050-a343-d751dc1e3296");
            var Q1074;
            Q1074=sQuery(id+"F10.wireOp",EDGE,"6d3048eb-751c-42bb-94a5-add11232d8ce");
            var Q1075;
            Q1075=sQuery(id+"F10.wireOp",EDGE,"1d311574-a07f-4181-bef2-0dc157f2763a");
            var Q1076;
            Q1076=sQuery(id+"F10.wireOp",EDGE,"cef2cd71-015f-4a61-93b1-4385e914fd41");
            var Q1077;
            Q1077=sQuery(id+"F10.wireOp",EDGE,"ef587da8-678a-4d3b-a280-013754d19b8a");
            var Q1078;
            Q1078=sQuery(id+"F10.wireOp",EDGE,"25e40fae-4a9a-4277-9b49-534f539c1884");
            var Q1079;
            Q1079=sQuery(id+"F10.wireOp",EDGE,"2db5eab5-019b-4abe-87e4-67c87419b4ab");
            var Q1080;
            Q1080=sQuery(id+"F10.wireOp",EDGE,"92655147-0868-4397-ba47-ee1f42c5b0ae");
            var Q1081;
            Q1081=sQuery(id+"F10.wireOp",EDGE,"14390121-a484-447c-9b66-6382d6c2575b");
            var Q1082;
            Q1082=sQuery(id+"F10.wireOp",EDGE,"43e1fe62-e0cb-4abb-9143-c9a982482d4b");
            var Q1083;
            Q1083=sQuery(id+"F10.wireOp",EDGE,"ba5a51ff-d36c-4109-9c03-bdab360778e0");
            var Q1084;
            Q1084=sQuery(id+"F10.wireOp",EDGE,"c590cd46-0da8-425d-9c61-e3a74c223b2b");
            var Q1085;
            Q1085=sQuery(id+"F10.wireOp",EDGE,"a5f6f79a-c614-41b1-9442-f92ff011dc0e");
            var Q1086;
            Q1086=sQuery(id+"F10.wireOp",EDGE,"17beaeb0-eb5e-49e4-b622-ad0571b23e1d");
            var Q1087;
            Q1087=sQuery(id+"F10.wireOp",EDGE,"653fcfaf-9ab2-4eb0-af75-bbeeef08ba8c");
            var Q1088;
            Q1088=sQuery(id+"F10.wireOp",EDGE,"df2237c3-bd7a-48b6-9a52-27309ea3b3fb");
            var Q1089;
            Q1089=sQuery(id+"F10.wireOp",EDGE,"eb15f40d-6fba-4a06-85e1-16032853b58d");
            var Q1090;
            Q1090=sQuery(id+"F10.wireOp",EDGE,"b613a198-2193-4b93-827f-27ee86809bf7");
            var Q1091;
            Q1091=sQuery(id+"F10.wireOp",EDGE,"037f128e-7018-496c-8d91-9a45d7a2fde9");
            var Q1092;
            Q1092=sQuery(id+"F10.wireOp",EDGE,"e42d9364-7654-4161-85b2-1a14e178b949");
            var Q1093;
            Q1093=sQuery(id+"F10.wireOp",EDGE,"e62fac19-c98d-4b81-97fb-559e24f24912");
            var Q1094;
            Q1094=sQuery(id+"F10.wireOp",EDGE,"52dc05bd-83e6-48ba-a8b5-afc7228a70b4");
            var Q1095;
            Q1095=sQuery(id+"F10.wireOp",EDGE,"b6bea4a2-15fd-4be0-81e0-cb40c7a4b893");
            var Q1096;
            Q1096=sQuery(id+"F10.wireOp",EDGE,"aeb34c85-e8b5-4f95-9112-5a2370d232d7");
            var Q1097;
            Q1097=sQuery(id+"F10.wireOp",EDGE,"9fc1d92d-ca00-4c6b-b85e-fc51d4546497");
            var Q1098;
            Q1098=sQuery(id+"F10.wireOp",EDGE,"67de09c5-8955-4650-81ba-c3687358b8d8");
            var Q1099;
            Q1099=sQuery(id+"F10.wireOp",EDGE,"5e73fc4c-11cf-474a-a33b-02d6d4faae32");
            var Q1100;
            Q1100=sQuery(id+"F10.wireOp",EDGE,"72a57a92-6ac5-4203-a6f8-6af0a656f757");
            var Q1101;
            Q1101=sQuery(id+"F10.wireOp",EDGE,"40fca3b0-f25e-43b7-9da2-c61c7db1e78b");
            var Q1102;
            Q1102=sQuery(id+"F10.wireOp",EDGE,"ff1eac29-df5a-4479-9a23-7b359756768b");
            var Q1103;
            Q1103=sQuery(id+"F10.wireOp",EDGE,"928c80d3-0668-439d-9135-ee399805ffc7");
            var Q1104;
            Q1104=sQuery(id+"F10.wireOp",EDGE,"6c3b38a4-8ef2-4646-bbac-122a21406e6f");
            var Q1105;
            Q1105=sQuery(id+"F10.wireOp",EDGE,"fc2eb367-b4ea-44d0-89e1-3c615a9f5c89");
            var Q1106;
            Q1106=sQuery(id+"F10.wireOp",EDGE,"1dcaf0ed-dbc6-406d-b289-75a2637ac752");
            var Q1107;
            Q1107=sQuery(id+"F10.wireOp",EDGE,"37fff00c-dbad-44ee-9646-05fd0b9e2bce");
            var Q1108;
            Q1108=sQuery(id+"F10.wireOp",EDGE,"56876a0c-7ae3-4e9c-a3ec-2eb47f378fb8");
            var Q1109;
            Q1109=sQuery(id+"F10.wireOp",EDGE,"20878c05-6671-44e4-a44f-770548d19c5a");
            var Q1110;
            Q1110=sQuery(id+"F10.wireOp",EDGE,"32b00d5c-03d2-4d25-8040-3d6249ccafd7");
            var Q1111;
            Q1111=sQuery(id+"F10.wireOp",EDGE,"f494c8f7-26c9-4657-8c21-c251318b2781");
            var Q1112;
            Q1112=sQuery(id+"F10.wireOp",EDGE,"066b4709-9dd8-4903-8a38-e1866eed5943");
            var Q1113;
            Q1113=sQuery(id+"F10.wireOp",EDGE,"2b0d7837-1525-4464-8f59-1cfbd55e5fa4");
            var Q1114;
            Q1114=sQuery(id+"F10.wireOp",EDGE,"6efb60fb-a251-41d9-940c-b7a5b35bc81d");
            var Q1115;
            Q1115=sQuery(id+"F10.wireOp",EDGE,"77209fd1-9a94-4aae-a35b-7f40b22f4409");
            var Q1116;
            Q1116=sQuery(id+"F10.wireOp",EDGE,"502b5f28-3afd-44f7-9c50-9e51fe995f96");
            var Q1117;
            Q1117=sQuery(id+"F10.wireOp",EDGE,"80f3f99c-edb0-43da-8ff0-b57e6cb10fea");
            var Q1118;
            Q1118=sQuery(id+"F10.wireOp",EDGE,"b2db9679-2e1b-4367-bd87-4564ffaa350c");
            var Q1119;
            Q1119=sQuery(id+"F10.wireOp",EDGE,"301b55a2-c06a-4f20-9aa6-d755e736ed30");
            var Q1120;
            Q1120=sQuery(id+"F10.wireOp",EDGE,"60f377a0-8c4f-4d1b-941f-357757494933");
            var Q1121;
            Q1121=sQuery(id+"F10.wireOp",EDGE,"f63eef77-4c3a-4897-a048-ba3b7860ada7");
            var Q1122;
            Q1122=sQuery(id+"F10.wireOp",EDGE,"121c4b29-35e0-4f2d-959a-59c61fc1635a");
            var Q1123;
            Q1123=sQuery(id+"F10.wireOp",EDGE,"6b8b1dfb-7a3e-4d93-8888-fbc66846c8c1");
            var Q1124;
            Q1124=sQuery(id+"F10.wireOp",EDGE,"c27baf3e-ac3f-42e1-97d4-6f741296f126");
            var Q1125;
            Q1125=sQuery(id+"F10.wireOp",EDGE,"211977c3-5444-4629-acf5-4488854e912a");
            var Q1126;
            Q1126=sQuery(id+"F10.wireOp",EDGE,"c6f91d2b-5658-4bf9-a49b-749846824e2b");
            var Q1127;
            Q1127=sQuery(id+"F10.wireOp",EDGE,"e277f0f1-f261-448d-ad68-25c6bb6a8742");
            var Q1128;
            Q1128=sQuery(id+"F10.wireOp",EDGE,"883cbfab-03ec-4f0e-b2d8-772750d2a4f6");
            var Q1129;
            Q1129=sQuery(id+"F10.wireOp",EDGE,"ac32bfbe-72b4-4cef-871e-6f12e70325b1");
            var Q1130;
            Q1130=sQuery(id+"F10.wireOp",EDGE,"6ab41d87-82a3-4d8b-b06c-4456e701e789");
            var Q1131;
            Q1131=sQuery(id+"F10.wireOp",EDGE,"975eb82c-3e30-41fb-9d8b-326082c62bbf");
            var Q1132;
            Q1132=sQuery(id+"F10.wireOp",EDGE,"c9bea173-429f-42bf-a961-22c43593cb3d");
            var Q1133;
            Q1133=sQuery(id+"F10.wireOp",EDGE,"8684db84-e8ba-4cb2-b9d5-918e6c0598dc");
            var Q1134;
            Q1134=sQuery(id+"F10.wireOp",EDGE,"da1829e1-37ad-4c3c-b1c7-0163e75de641");
            var Q1135;
            Q1135=sQuery(id+"F10.wireOp",EDGE,"def0a8e1-1675-4c62-a242-ec1eba2adf24");
            var Q1136;
            Q1136=sQuery(id+"F10.wireOp",EDGE,"6287fa2f-3292-42fc-9185-fa8ef5476a5d");
            var Q1137;
            Q1137=sQuery(id+"F10.wireOp",EDGE,"2decdbfd-75fc-4eec-91af-a365ef87e32c");
            var Q1138;
            Q1138=sQuery(id+"F10.wireOp",EDGE,"4b1b77fb-b132-4a66-a010-48b1f357afbe");
            var Q1139;
            Q1139=sQuery(id+"F10.wireOp",EDGE,"2ad9eee4-1169-4365-af09-be64226df21c");
            var Q1140;
            Q1140=sQuery(id+"F10.wireOp",EDGE,"bc3bc171-2781-419c-bf0e-8294b64f5bf5");
            var Q1141;
            Q1141=sQuery(id+"F10.wireOp",EDGE,"3c390451-1733-4497-a789-1ed2383b3cbb");
            var Q1142;
            Q1142=sQuery(id+"F10.wireOp",EDGE,"9a03b4d6-2da1-4576-ba1f-e2b716c8c28f");
            var Q1143;
            Q1143=sQuery(id+"F10.wireOp",EDGE,"550ebace-696d-48d9-9b8e-ea3d93e1aa71");
            var Q1144;
            Q1144=sQuery(id+"F10.wireOp",EDGE,"8b594863-2d37-4537-9d78-7c03217dde3e");
            var Q1145;
            Q1145=sQuery(id+"F10.wireOp",EDGE,"a2045cbe-be98-4277-a760-34ad57bd256e");
            var Q1146;
            Q1146=sQuery(id+"F10.wireOp",EDGE,"21905816-d3a4-4da5-9a10-87f9b73fb407");
            var Q1147;
            Q1147=sQuery(id+"F10.wireOp",EDGE,"2ad0765b-e9bd-4c83-bf0e-44c922962f7c");
            var Q1148;
            Q1148=sQuery(id+"F10.wireOp",EDGE,"dea4ba20-3b2f-4c42-9374-c5ad99856cb4");
            var Q1149;
            Q1149=sQuery(id+"F10.wireOp",EDGE,"6d71a01a-d503-4128-af9e-0dbdc4e20322");
            var Q1150;
            Q1150=sQuery(id+"F10.wireOp",EDGE,"00e55dda-8a89-4a7d-bb42-7afcb3402236");
            var Q1151;
            Q1151=sQuery(id+"F10.wireOp",EDGE,"0f1929bd-4974-47b9-ad56-4957432e4176");
            var Q1152;
            Q1152=sQuery(id+"F10.wireOp",EDGE,"e2ee465c-14be-4f3c-aa46-9b1e1816b0fa");
            var Q1153;
            Q1153=sQuery(id+"F10.wireOp",EDGE,"6b89d6c5-fd2d-424a-a7d9-52e8871dae6c");
            var Q1154;
            Q1154=sQuery(id+"F10.wireOp",EDGE,"05303f76-9163-4156-89c1-2753b601cff6");
            var Q1155;
            Q1155=sQuery(id+"F10.wireOp",EDGE,"9ae3a0fa-5542-49c9-b308-e78ddfe26d64");
            var Q1156;
            Q1156=sQuery(id+"F10.wireOp",EDGE,"c3565729-2dcf-4010-8a90-f6b8a45dbf7b");
            var Q1157;
            Q1157=sQuery(id+"F10.wireOp",EDGE,"560dab94-ecd5-4966-9794-afc65ee9e9ab");
            var Q1158;
            Q1158=sQuery(id+"F10.wireOp",EDGE,"cebe7770-efe0-4ba4-99c6-9d88e548b78e");
            var Q1159;
            Q1159=sQuery(id+"F10.wireOp",EDGE,"58f94763-8d21-4ae5-ac6e-bf4376f1c1d6");
            var Q1160;
            Q1160=sQuery(id+"F10.wireOp",EDGE,"f4ead4d6-a9e2-4cfc-a6a4-e678095ac621");
            var Q1161;
            Q1161=sQuery(id+"F10.wireOp",EDGE,"0f829247-f684-4929-853a-811134011897");
            var Q1162;
            Q1162=sQuery(id+"F10.wireOp",EDGE,"94af2c4c-5b81-402a-ae0e-ad799da594f6");
            var Q1163;
            Q1163=sQuery(id+"F10.wireOp",EDGE,"7156b697-1acc-4ce2-83b3-dec75dbb9631");
            var Q1164;
            Q1164=sQuery(id+"F10.wireOp",EDGE,"dc6146ab-0cd7-48ab-b095-0c614a676d90");
            var Q1165;
            Q1165=sQuery(id+"F10.wireOp",EDGE,"53265639-c90c-4cac-a8f3-4f62dbc34e8e");
            var Q1166;
            Q1166=sQuery(id+"F10.wireOp",EDGE,"04e2ac39-6f3d-4cef-bd8d-98bceaa70134");
            var Q1167;
            Q1167=sQuery(id+"F10.wireOp",EDGE,"c1880633-82c1-47f2-ba7e-95c4a1e14db9");
            var Q1168;
            Q1168=sQuery(id+"F10.wireOp",EDGE,"80f77150-c504-4c13-aef2-a22e7079cbf1");
            var Q1169;
            Q1169=sQuery(id+"F10.wireOp",EDGE,"8aee3056-c56f-421e-95b7-d589ce9ca49d");
            var Q1170;
            Q1170=sQuery(id+"F10.wireOp",EDGE,"8e72946b-4d83-45c5-99cf-fee3acf7da90");
            var Q1171;
            Q1171=sQuery(id+"F10.wireOp",EDGE,"21e42d33-a613-4fdc-9864-fa641750efa1");
            var Q1172;
            Q1172=sQuery(id+"F10.wireOp",EDGE,"626f7c6c-b593-4af9-8070-73d7a0c3677a");
            var Q1173;
            Q1173=sQuery(id+"F10.wireOp",EDGE,"90c401b8-ae0d-4380-ab4f-d436420c4878");
            var Q1174;
            Q1174=sQuery(id+"F10.wireOp",EDGE,"8e0d67cc-9ea7-4be5-818f-e1f5d92dbcf0");
            var Q1175;
            Q1175=sQuery(id+"F10.wireOp",EDGE,"1ece4ed6-b6e9-4060-893b-31c58822afbf");
            var Q1176;
            Q1176=sQuery(id+"F10.wireOp",EDGE,"92008fd2-024d-4085-988f-f495075a9dfc");
            var Q1177;
            Q1177=sQuery(id+"F10.wireOp",EDGE,"2793c376-d6df-404a-9209-29e2350c96a7");
            var Q1178;
            Q1178=sQuery(id+"F10.wireOp",EDGE,"e90a7463-31ae-4250-9053-f740142703be");
            var Q1179;
            Q1179=sQuery(id+"F10.wireOp",EDGE,"381defab-7cce-439a-84c0-cd96164a691f");
            var Q1180;
            Q1180=sQuery(id+"F10.wireOp",EDGE,"dd8bff9a-4102-4013-8ade-7e2695caaeb8");
            var Q1181;
            Q1181=sQuery(id+"F10.wireOp",EDGE,"bc16e3e3-eb1f-4fe3-8f78-1d34846583a7");
            var Q1182;
            Q1182=sQuery(id+"F10.wireOp",EDGE,"25aed68c-8bc2-4979-aefb-9e33b24a729e");
            var Q1183;
            Q1183=sQuery(id+"F10.wireOp",EDGE,"442fbf7c-eb8e-4360-9537-69056897ec5d");
            var Q1184;
            Q1184=sQuery(id+"F10.wireOp",EDGE,"508023d0-cd33-4536-9c91-15686cb88835");
            var Q1185;
            Q1185=sQuery(id+"F10.wireOp",EDGE,"cf5f2d4f-e89b-4942-b845-f1664fe66ef2");
            var Q1186;
            Q1186=sQuery(id+"F10.wireOp",EDGE,"1d8ee4d3-c6cb-4cd3-9eba-b9d8f50b748d");
            var Q1187;
            Q1187=sQuery(id+"F10.wireOp",EDGE,"a0b8339d-4b76-44b8-9208-b4e9781e6c2b");
            var Q1188;
            Q1188=sQuery(id+"F10.wireOp",EDGE,"100d7e67-9a94-48a0-80d6-fd2663244cb1");
            var Q1189;
            Q1189=sQuery(id+"F10.wireOp",EDGE,"2cbdecb0-2622-4679-9816-9bc278716ad3");
            var Q1190;
            Q1190=sQuery(id+"F10.wireOp",EDGE,"fd6e741c-0ec2-4293-b38b-374edee2046f");
            var Q1191;
            Q1191=sQuery(id+"F10.wireOp",EDGE,"9a31814e-08b2-4d9f-a91a-cb7a6c6d52f5");
            var Q1192;
            Q1192=sQuery(id+"F10.wireOp",EDGE,"de4014eb-7ae0-4a72-891c-b905beffc086");
            var Q1193;
            Q1193=sQuery(id+"F10.wireOp",EDGE,"dba12be2-7661-42b5-93a6-40488ca2d688");
            var Q1194;
            Q1194=sQuery(id+"F10.wireOp",EDGE,"686534ce-7e3d-46bc-b7ea-347f9ac5656c");
            var Q1195;
            Q1195=sQuery(id+"F10.wireOp",EDGE,"cca323f1-2402-45ed-9835-99a2702e10f7");
            var Q1196;
            Q1196=sQuery(id+"F10.wireOp",EDGE,"e89997ff-303d-4e8a-9c36-bec8bc47f2bf");
            var Q1197;
            Q1197=sQuery(id+"F10.wireOp",EDGE,"8f288f3b-1416-4878-ad59-207d3d151395");
            var Q1198;
            Q1198=sQuery(id+"F10.wireOp",EDGE,"3caaeb87-4980-4f18-b302-bd9908f0d9f7");
            var Q1199;
            Q1199=sQuery(id+"F10.wireOp",EDGE,"4abd7f14-033c-423d-83ed-a22c73c90d01");
            var Q1200;
            Q1200=sQuery(id+"F10.wireOp",EDGE,"f8a0bfca-25c8-4ac2-9508-b7ec481bb55c");
            var Q1201;
            Q1201=sQuery(id+"F10.wireOp",EDGE,"05cc5df0-2c07-4e7e-a2bd-177000a29e61");
            var Q1202;
            Q1202=sQuery(id+"F10.wireOp",EDGE,"35399c2e-301e-4e53-9fb3-e8cf49f2c4da");
            var Q1203;
            Q1203=sQuery(id+"F10.wireOp",EDGE,"1e7f6c81-1864-437c-9407-bd8fa81fc505");
            var Q1204;
            Q1204=sQuery(id+"F10.wireOp",EDGE,"c5bf7496-d01a-4c6f-8e95-d178e2e54a8c");
            var Q1205;
            Q1205=sQuery(id+"F10.wireOp",EDGE,"a3a413df-9a9a-43d9-a697-c29e8ea17de4");
            var Q1206;
            Q1206=sQuery(id+"F10.wireOp",EDGE,"84e2e0bf-7ed9-402a-86b3-56d30f3c6159");
            var Q1207;
            Q1207=sQuery(id+"F10.wireOp",EDGE,"3ce984ff-438f-4e06-b15b-ae711a47b225");
            var Q1208;
            Q1208=sQuery(id+"F10.wireOp",EDGE,"4f504844-e2d9-4f41-b447-006f55ba14c7");
            var Q1209;
            Q1209=sQuery(id+"F10.wireOp",EDGE,"4ebdda0c-8c1a-4dba-a7ed-c0973c0501c3");
            var Q1210;
            Q1210=sQuery(id+"F10.wireOp",EDGE,"76cf9365-5e31-40f0-949b-e2cccbcd371f");
            var Q1211;
            Q1211=sQuery(id+"F10.wireOp",EDGE,"5b8b1422-c49a-4450-ab2c-a6dc167bc0f3");
            var Q1212;
            Q1212=sQuery(id+"F10.wireOp",EDGE,"6a474797-eddc-4e08-bed0-ca00bb435f69");
            var Q1213;
            Q1213=sQuery(id+"F10.wireOp",EDGE,"3b912c2a-c862-42d4-b3db-7545a4f1b888");
            var Q1214;
            Q1214=sQuery(id+"F10.wireOp",EDGE,"d31ab71f-6ef7-4d5f-bebd-1563d0c05dd6");
            var Q1215;
            Q1215=sQuery(id+"F10.wireOp",EDGE,"579393b7-7ab3-41c5-abed-391a3d4ad3c0");
            var Q1216;
            Q1216=sQuery(id+"F10.wireOp",EDGE,"310a9586-4be1-4b59-8bce-993c376db7fe");
            var Q1217;
            Q1217=sQuery(id+"F10.wireOp",EDGE,"f37d8fee-16cc-42a2-9833-e79b1aeecdc3");
            var Q1218;
            Q1218=sQuery(id+"F10.wireOp",EDGE,"d1a1741b-138c-4341-b344-0899c8034552");
            var Q1219;
            Q1219=sQuery(id+"F10.wireOp",EDGE,"d9f65638-8fd6-4366-99f7-1058b5feae83");
            var Q1220;
            Q1220=sQuery(id+"F10.wireOp",EDGE,"fc1cae11-eb91-4bf1-953d-b8003facc091");
            var Q1221;
            Q1221=sQuery(id+"F10.wireOp",EDGE,"37c451ae-65af-4bf3-97c5-b73d9085cb24");
            var Q1222;
            Q1222=sQuery(id+"F10.wireOp",EDGE,"7c953cd1-171d-4712-83e0-039585e0f38a");
            var Q1223;
            Q1223=sQuery(id+"F10.wireOp",EDGE,"c4400dde-2025-4f4a-bed6-01c4722f5221");
            var Q1224;
            Q1224=sQuery(id+"F10.wireOp",EDGE,"9ec65669-508c-4449-89e7-8e2ac90b87ae");
            var Q1225;
            Q1225=sQuery(id+"F10.wireOp",EDGE,"5035cbc5-16df-4aef-ba55-268944d2c294");
            var Q1226;
            Q1226=sQuery(id+"F10.wireOp",EDGE,"7b6cd58e-0e70-40dd-8b94-9cf8f4ac2eb6");
            var Q1227;
            Q1227=sQuery(id+"F10.wireOp",EDGE,"a90465b7-641b-4459-82ad-251c57199cc8");
            var Q1228;
            Q1228=sQuery(id+"F10.wireOp",EDGE,"7dfb6357-4596-4837-87bd-25d90689bb5b");
            var Q1229;
            Q1229=sQuery(id+"F10.wireOp",EDGE,"d89bd3f9-4aa9-4d2f-98c1-357382059b9a");
            var Q1230;
            Q1230=sQuery(id+"F10.wireOp",EDGE,"d395c617-7400-4ad4-b42f-e5222fca6856");
            var Q1231;
            Q1231=sQuery(id+"F10.wireOp",EDGE,"7ee2b93e-69d7-42ab-99c7-72bc47cc5c53");
            var Q1232;
            Q1232=sQuery(id+"F10.wireOp",EDGE,"6d3a5827-3156-4503-b9ea-38f3bce63ff0");
            var Q1233;
            Q1233=sQuery(id+"F10.wireOp",EDGE,"71cfe705-c275-4c25-b04f-1f9e31b362cf");
            var Q1234;
            Q1234=sQuery(id+"F10.wireOp",EDGE,"1779e6ad-fadd-4118-b1c2-1568c0747882");
            var Q1235;
            Q1235=sQuery(id+"F10.wireOp",EDGE,"be8ab711-7a78-4612-bee1-47acd2bff5be");
            var Q1236;
            Q1236=sQuery(id+"F10.wireOp",EDGE,"52c54a6f-a2f9-4b26-b6ca-02f03923160c");
            var Q1237;
            Q1237=sQuery(id+"F10.wireOp",EDGE,"2a1a7b0e-f2d9-4cd0-b28f-49ed0ee3fe9e");
            var Q1238;
            Q1238=sQuery(id+"F10.wireOp",EDGE,"49b8b9ab-49f7-475d-9c0e-5d52f12c8b54");
            var Q1239;
            Q1239=sQuery(id+"F10.wireOp",EDGE,"a4a2193a-6cdf-40ef-b243-1c230439750c");
            var Q1240;
            Q1240=sQuery(id+"F10.wireOp",EDGE,"da1c2b7b-617f-4b99-a836-fdeceaccb6a9");
            var Q1241;
            Q1241=sQuery(id+"F10.wireOp",EDGE,"30ce0072-5827-463c-be31-f7b81d4b690a");
            var Q1242;
            Q1242=sQuery(id+"F10.wireOp",EDGE,"c1a4ddae-6086-46b2-b5a2-5f7464e47719");
            var Q1243;
            Q1243=sQuery(id+"F10.wireOp",EDGE,"08e98d71-7a59-4659-8618-39a39b82c008");
            var Q1244;
            Q1244=sQuery(id+"F10.wireOp",EDGE,"c201a1d9-21bc-4ee6-b359-25833694d027");
            var Q1245;
            Q1245=sQuery(id+"F10.wireOp",EDGE,"052b34cc-69bd-4df5-81c7-ff7a67f20088");
            var Q1246;
            Q1246=sQuery(id+"F10.wireOp",EDGE,"9050d8b9-5318-4925-b766-effc5692b182");
            var Q1247;
            Q1247=sQuery(id+"F10.wireOp",EDGE,"22d7d1ae-1d17-4ea5-bd9b-3b7616ea2e4a");
            var Q1248;
            Q1248=sQuery(id+"F10.wireOp",EDGE,"cc74f9c2-ad41-4e06-86ca-8a5087dfc668");
            var Q1249;
            Q1249=sQuery(id+"F10.wireOp",EDGE,"735b7b66-5617-4315-9c65-b090699b54de");
            var Q1250;
            Q1250=sQuery(id+"F10.wireOp",EDGE,"c6d3d972-ab4c-434a-a08b-1e55096544f9");
            var Q1251;
            Q1251=sQuery(id+"F10.wireOp",EDGE,"7cccb9a4-b7ca-4240-964f-029d8959a6f8");
            var Q1252;
            Q1252=sQuery(id+"F10.wireOp",EDGE,"28dd9326-ee41-451f-bef1-49ba5f1b1686");
            var Q1253;
            Q1253=sQuery(id+"F10.wireOp",EDGE,"a9839461-6a8b-426c-b9a5-2c66586fed17");
            var Q1254;
            Q1254=sQuery(id+"F10.wireOp",EDGE,"a8ecd74d-c5b2-4fab-84a9-0b3f6e659b71");
            var Q1255;
            Q1255=sQuery(id+"F10.wireOp",EDGE,"ad5c30b6-5eb4-4b19-b5d1-5d2a7979f751");
            var Q1256;
            Q1256=sQuery(id+"F10.wireOp",EDGE,"e875fa24-d373-484c-82b9-35844c50e0d6");
            var Q1257;
            Q1257=sQuery(id+"F10.wireOp",EDGE,"49389a31-9cb1-4954-9be7-a48a280ed3a4");
            var Q1258;
            Q1258=sQuery(id+"F10.wireOp",EDGE,"d04b3772-6f4c-41ef-a9d5-cd44059ea669");
            var Q1259;
            Q1259=sQuery(id+"F10.wireOp",EDGE,"010a70f1-30d2-4300-8ad6-45fb3068be75");
            var Q1260;
            Q1260=sQuery(id+"F10.wireOp",EDGE,"31232fb4-fb2d-4df6-9497-a0738076fda1");
            var Q1261;
            Q1261=sQuery(id+"F10.wireOp",EDGE,"9025893f-acea-46e0-90e9-54d847001855");
            var Q1262;
            Q1262=sQuery(id+"F10.wireOp",EDGE,"2a3af6ca-ef81-4152-9015-92483a1b62f2");
            var Q1263;
            Q1263=sQuery(id+"F10.wireOp",EDGE,"989b5974-73f8-4a13-abaa-20a6f9335394");
            var Q1264;
            Q1264=sQuery(id+"F10.wireOp",EDGE,"a602cccd-7b48-4322-b648-12e7406f9a74");
            var Q1265;
            Q1265=sQuery(id+"F10.wireOp",EDGE,"8744da84-3e4e-41f1-bc75-7d9ade50b154");
            var Q1266;
            Q1266=sQuery(id+"F10.wireOp",EDGE,"79477af3-2e65-493d-9a45-5f16932519aa");
            var Q1267;
            Q1267=sQuery(id+"F10.wireOp",EDGE,"a190790c-680d-4b0e-a222-33b6bd7a5d73");
            var Q1268;
            Q1268=sQuery(id+"F10.wireOp",EDGE,"3a6a4515-d178-4f8a-ba23-b881c999193f");
            var Q1269;
            Q1269=sQuery(id+"F10.wireOp",EDGE,"f77ee2b2-ede7-4ed3-a745-89cc3c0c6065");
            var Q1270;
            Q1270=sQuery(id+"F10.wireOp",EDGE,"94581643-bc38-430f-8c31-6467b1bfff9a");
            var Q1271;
            Q1271=sQuery(id+"F10.wireOp",EDGE,"268c7afb-3f26-447f-888f-2b6d2eb016cf");
            var Q1272;
            Q1272=sQuery(id+"F10.wireOp",EDGE,"20475b9b-c317-4992-ae87-8fad5d5c7763");
            var Q1273;
            Q1273=sQuery(id+"F10.wireOp",EDGE,"3b18a934-5d9d-4624-933d-469af25e0eec");
            var Q1274;
            Q1274=sQuery(id+"F10.wireOp",EDGE,"a9722576-33b8-47b5-85eb-cc579d0ae1e4");
            var Q1275;
            Q1275=sQuery(id+"F10.wireOp",EDGE,"73aa5485-2a1a-450e-98b0-4c471b29de4c");
            var Q1276;
            Q1276=sQuery(id+"F10.wireOp",EDGE,"52934aa5-1eba-479b-aabe-3d4dcb37085a");
            var Q1277;
            Q1277=sQuery(id+"F10.wireOp",EDGE,"b7da4f0b-54b7-4f50-b4fe-b450d687ab43");
            var Q1278;
            Q1278=sQuery(id+"F10.wireOp",EDGE,"33fce140-29b8-426c-853d-03ae0c3141e1");
            var Q1279;
            Q1279=sQuery(id+"F10.wireOp",EDGE,"bc26cf05-32bd-41a1-97df-a01d2469143c");
            var Q1280;
            Q1280=sQuery(id+"F10.wireOp",EDGE,"11a760b2-e8d8-4867-8cc0-b4922cf2a0b3");
            var Q1281;
            Q1281=sQuery(id+"F10.wireOp",EDGE,"eb96bae4-77e1-48ba-8c7c-ddc68505cd1f");
            var Q1282;
            Q1282=sQuery(id+"F10.wireOp",EDGE,"4bf02295-85a8-45be-a610-6e1eff98150e");
            var Q1283;
            Q1283=sQuery(id+"F10.wireOp",EDGE,"62376fe8-781b-4879-98f5-36ae7becb2f5");
            var Q1284;
            Q1284=sQuery(id+"F10.wireOp",EDGE,"13b40611-4e8a-4907-bde9-b6659556aa63");
            var Q1285;
            Q1285=sQuery(id+"F10.wireOp",EDGE,"8cabce52-d11c-49ea-af6d-8ee15c6ba3b7");
            var Q1286;
            Q1286=sQuery(id+"F10.wireOp",EDGE,"ecb8e27f-a8d5-4945-a48a-b941acb7a388");
            var Q1287;
            Q1287=sQuery(id+"F10.wireOp",EDGE,"0163ce46-5472-41ec-bf07-4aaf694efa39");
            var Q1288;
            Q1288=sQuery(id+"F10.wireOp",EDGE,"88706100-851b-48bc-ab79-94fffd2a60bb");
            var Q1289;
            Q1289=sQuery(id+"F10.wireOp",EDGE,"c0d03cd0-80cc-4393-88ef-cd97e10d6ace");
            var Q1290;
            Q1290=sQuery(id+"F10.wireOp",EDGE,"7280b20a-bd56-486c-aa67-e6bb6b520560");
            var Q1291;
            Q1291=sQuery(id+"F10.wireOp",EDGE,"dd6ae8ed-c35d-4dc2-8065-942fed6b8166");
            var Q1292;
            Q1292=sQuery(id+"F10.wireOp",EDGE,"6937fe1a-7181-427f-ad7c-9285235a9cbc");
            var Q1293;
            Q1293=sQuery(id+"F10.wireOp",EDGE,"23a338f8-70f2-4ff1-803f-59db19e80257");
            var Q1294;
            Q1294=sQuery(id+"F10.wireOp",EDGE,"e5228ab1-712b-4a6b-a5bc-28cd31240beb");
            var Q1295;
            Q1295=sQuery(id+"F10.wireOp",EDGE,"3fa15a43-6c4e-4304-a13b-7bc12ef890ad");
            var Q1296;
            Q1296=sQuery(id+"F10.wireOp",EDGE,"05dd640e-d589-4562-8da1-03334e5a3536");
            var Q1297;
            Q1297=sQuery(id+"F10.wireOp",EDGE,"f9657bc5-4a4f-441c-b297-7775e8769b9b");
            var Q1298;
            Q1298=sQuery(id+"F10.wireOp",EDGE,"8dfcbb54-199a-432c-9450-9aa8fb3dffff");
            var Q1299;
            Q1299=sQuery(id+"F10.wireOp",EDGE,"ba19fd75-e4c5-452f-a684-f6d83dfdfb8d");
            var Q1300;
            Q1300=sQuery(id+"F10.wireOp",EDGE,"baa2a382-4053-4a73-9f55-34c801ee5ba3");
            var Q1301;
            Q1301=sQuery(id+"F10.wireOp",EDGE,"bdb55bb9-bf7d-44ce-8234-a9af4a79f6ce");
            var Q1302;
            Q1302=sQuery(id+"F10.wireOp",EDGE,"25112f9b-be91-4ea5-84aa-1b7bededb43a");
            var Q1303;
            Q1303=sQuery(id+"F10.wireOp",EDGE,"c6ab3b7e-f6c0-4799-b4ce-73c49c837f59");
            var Q1304;
            Q1304=sQuery(id+"F10.wireOp",EDGE,"e27610b6-0180-439e-9548-4ef2153230d7");
            var Q1305;
            Q1305=sQuery(id+"F10.wireOp",EDGE,"8b76ce5e-0542-4d9b-b57e-4fdd4a31aa0b");
            var Q1306;
            Q1306=sQuery(id+"F10.wireOp",EDGE,"e18c744f-7ce9-43f2-84de-baf6d945cf0a");
            var Q1307;
            Q1307=sQuery(id+"F10.wireOp",EDGE,"2eb48e24-b53f-4cb1-bc02-91fc3f7a7200");
            var Q1308;
            Q1308=sQuery(id+"F10.wireOp",EDGE,"3c2b9de6-ebba-493a-80d1-6a7b02f20ff7");
            var Q1309;
            Q1309=sQuery(id+"F10.wireOp",EDGE,"d7945952-c906-4be7-9bea-4d59b4dd7ecd");
            var Q1310;
            Q1310=sQuery(id+"F10.wireOp",EDGE,"0a5b0137-dbf9-4dcf-95c6-6b8b34f10ccf");
            var Q1311;
            Q1311=sQuery(id+"F10.wireOp",EDGE,"cd810fb8-16b6-46af-983c-9c2b5858b823");
            var Q1312;
            Q1312=sQuery(id+"F10.wireOp",EDGE,"1caaa69c-4d40-4bfd-836f-dbc92b5d687a");
            var Q1313;
            Q1313=sQuery(id+"F10.wireOp",EDGE,"4846c2e2-3115-4b5f-b55d-ce966588f205");
            var Q1314;
            Q1314=sQuery(id+"F10.wireOp",EDGE,"eeb5d0af-b285-41e4-ae19-f46e99b8446b");
            var Q1315;
            Q1315=sQuery(id+"F10.wireOp",EDGE,"2605362f-077d-4a99-a273-2cb63845e6df");
            var Q1316;
            Q1316=sQuery(id+"F10.wireOp",EDGE,"1714824e-00f4-409d-8cd6-17081708fc52");
            var Q1317;
            Q1317=sQuery(id+"F10.wireOp",EDGE,"2b5ef472-4180-47a9-b61e-c229ce930287");
            var Q1318;
            Q1318=sQuery(id+"F10.wireOp",EDGE,"c391077e-1203-4244-999d-753a1f530b3e");
            var Q1319;
            Q1319=sQuery(id+"F10.wireOp",EDGE,"327ffa5b-ce52-4841-8789-027e38b3d3ff");
            var Q1320;
            Q1320=sQuery(id+"F10.wireOp",EDGE,"a7fb1884-6aab-431e-a7b7-212726122c62");
            var Q1321;
            Q1321=sQuery(id+"F10.wireOp",EDGE,"c8e9ff6f-6682-4a1b-aba1-fdbdaa62dd31");
            var Q1322;
            Q1322=sQuery(id+"F10.wireOp",EDGE,"ab1e6125-3630-4551-b966-9093ab54bc92");
            var Q1323;
            Q1323=sQuery(id+"F10.wireOp",EDGE,"b668f39c-0a68-4957-8ca5-7e83a348b74d");
            var Q1324;
            Q1324=sQuery(id+"F10.wireOp",EDGE,"b14b87df-3fad-4934-8c0b-a18a68fd66e7");
            var Q1325;
            Q1325=sQuery(id+"F10.wireOp",EDGE,"bff5b4e6-91f8-4b1e-83b7-dd32fe15ca8a");
            var Q1326;
            Q1326=sQuery(id+"F10.wireOp",EDGE,"0b30b794-eadb-47cf-bae8-383fa0815c5d");
            var Q1327;
            Q1327=sQuery(id+"F10.wireOp",EDGE,"e879aa28-b88a-471c-a5b1-6fbfcba6533a");
            var Q1328;
            Q1328=sQuery(id+"F10.wireOp",EDGE,"cafeb9a1-3c58-42dc-a9da-45a317dee184");
            var Q1329;
            Q1329=sQuery(id+"F10.wireOp",EDGE,"93b47a91-ac29-4ca5-9a9d-bee78b5b4cd9");
            var Q1330;
            Q1330=sQuery(id+"F10.wireOp",EDGE,"e82ee927-09b9-4b35-92f1-05e2fd322cef");
            var Q1331;
            Q1331=sQuery(id+"F10.wireOp",EDGE,"f3d5bb83-d26d-457e-8674-ed8dc3021da5");
            var Q1332;
            Q1332=sQuery(id+"F10.wireOp",EDGE,"d75d6706-b375-4307-8dc9-f20371d2e43b");
            var Q1333;
            Q1333=sQuery(id+"F10.wireOp",EDGE,"a29503f5-c4a9-4a58-bb2d-9848ca9fbfd6");
            var Q1334;
            Q1334=sQuery(id+"F10.wireOp",EDGE,"8955832a-1e65-4a30-b384-0c99f27876f4");
            var Q1335;
            Q1335=sQuery(id+"F10.wireOp",EDGE,"a8e310ee-befe-4aba-af5c-b33de6693e86");
            var Q1336;
            Q1336=sQuery(id+"F10.wireOp",EDGE,"a8dfdd2d-b25e-4d5a-b4d4-2df8ce6b7974");
            var Q1337;
            Q1337=sQuery(id+"F10.wireOp",EDGE,"265deeea-2d23-4421-884e-82f0baeb4f68");
            var Q1338;
            Q1338=sQuery(id+"F10.wireOp",EDGE,"21c07e25-4c4e-479e-bea2-3cdee6066599");
            var Q1339;
            Q1339=sQuery(id+"F10.wireOp",EDGE,"78cab8da-8c31-470f-a15c-d646aa22a147");
            var Q1340;
            Q1340=sQuery(id+"F10.wireOp",EDGE,"a9e11274-67b4-470d-8010-acff8c164c38");
            var Q1341;
            Q1341=sQuery(id+"F10.wireOp",EDGE,"4ce1bedb-8a2e-4788-a22f-686333e55fd0");
            var Q1342;
            Q1342=sQuery(id+"F10.wireOp",EDGE,"8136bdcf-1c33-4486-ad3c-ad71db63017b");
            var Q1343;
            Q1343=sQuery(id+"F10.wireOp",EDGE,"86641a2b-de5f-49c0-bd9f-07c193a37c45");
            var Q1344;
            Q1344=sQuery(id+"F10.wireOp",EDGE,"6fdc5335-5f2f-498b-8354-ce8825a4b62d");
            var Q1345;
            Q1345=sQuery(id+"F10.wireOp",EDGE,"13eb7726-67c4-41d3-a24a-906990c8087d");
            var Q1346;
            Q1346=sQuery(id+"F10.wireOp",EDGE,"1fbd9253-d748-488c-ba15-0807cc248621");
            var Q1347;
            Q1347=sQuery(id+"F10.wireOp",EDGE,"6b285c90-989b-4f4b-ae36-db88323ff26c");
            var Q1348;
            Q1348=sQuery(id+"F10.wireOp",EDGE,"a9052483-e7bf-4171-af67-ba9a9e19ae88");
            var Q1349;
            Q1349=sQuery(id+"F10.wireOp",EDGE,"a65d7347-0cc7-425e-a818-c3772f284cff");
            var Q1350;
            Q1350=sQuery(id+"F10.wireOp",EDGE,"5fff3833-3e15-4db8-a547-c5bc4f65fab6");
            var Q1351;
            Q1351=sQuery(id+"F10.wireOp",EDGE,"62980af1-d3c4-471b-97cf-aea386c3934c");
            var Q1352;
            Q1352=sQuery(id+"F10.wireOp",EDGE,"8299140a-a347-4401-8f45-01b84a7432e5");
            var Q1353;
            Q1353=sQuery(id+"F10.wireOp",EDGE,"904e67e5-bb3a-4ce2-9093-c92d616fef2d");
            var Q1354;
            Q1354=sQuery(id+"F10.wireOp",EDGE,"298af51d-fc33-4b10-a11a-5449465a3d95");
            var Q1355;
            Q1355=sQuery(id+"F10.wireOp",EDGE,"ba1b40a3-a768-48f3-87c0-e945839a9ff5");
            var Q1356;
            Q1356=sQuery(id+"F10.wireOp",EDGE,"fcda26df-38c4-4630-b428-9cbf6be5ae1f");
            var Q1357;
            Q1357=sQuery(id+"F10.wireOp",EDGE,"5a62a9a4-8371-4f0f-9f1c-78680e70e3b4");
            var Q1358;
            Q1358=sQuery(id+"F10.wireOp",EDGE,"a850de2e-2385-40ba-9912-462cbd9947a1");
            var Q1359;
            Q1359=sQuery(id+"F10.wireOp",EDGE,"fcc785e0-7207-4062-a61e-42063c65316b");
            var Q1360;
            Q1360=sQuery(id+"F10.wireOp",EDGE,"265097f6-b6b2-4212-9b14-c78232ac78da");
            var Q1361;
            Q1361=sQuery(id+"F10.wireOp",EDGE,"f0f049d8-c44b-49a7-a005-bcbfeb118de6");
            var Q1362;
            Q1362=sQuery(id+"F10.wireOp",EDGE,"4c6b69f0-c68c-42eb-a6a0-ab411584f18c");
            var Q1363;
            Q1363=sQuery(id+"F10.wireOp",EDGE,"858d467f-132b-4287-bb10-77ee181df361");
            var Q1364;
            Q1364=sQuery(id+"F10.wireOp",EDGE,"095efb27-79fa-4572-9566-90ff11d34d82");
            var Q1365;
            Q1365=sQuery(id+"F10.wireOp",EDGE,"e453b1c1-1e4c-41d3-a55e-fbbf540fbee4");
            var Q1366;
            Q1366=sQuery(id+"F10.wireOp",EDGE,"88702b6f-90f4-4ea0-a2b2-8f439e37d807");
            var Q1367;
            Q1367=sQuery(id+"F10.wireOp",EDGE,"46a7f4ba-fce8-499e-b433-e2504293e202");
            var Q1368;
            Q1368=sQuery(id+"F10.wireOp",EDGE,"b57df71b-8d98-48f5-bc51-07e011c029a4");
            var Q1369;
            Q1369=sQuery(id+"F10.wireOp",EDGE,"2e7d10a5-59fd-4401-912b-3a4101dc1b5b");
            var Q1370;
            Q1370=sQuery(id+"F10.wireOp",EDGE,"3e49a653-a3a9-4d3d-b1fd-843ea32e6efd");
            var Q1371;
            Q1371=sQuery(id+"F10.wireOp",EDGE,"665d51ba-c137-4dbd-a1b7-03f36f8286f9");
            var Q1372;
            Q1372=sQuery(id+"F10.wireOp",EDGE,"e6cd6c84-4315-4556-b316-e7242d732fc0");
            var Q1373;
            Q1373=sQuery(id+"F10.wireOp",EDGE,"ea7fa55f-01ed-46da-826c-83572bbfe06c");
            var Q1374;
            Q1374=sQuery(id+"F10.wireOp",EDGE,"b2e87019-ffc1-402b-b82c-c696aedf7829");
            var Q1375;
            Q1375=sQuery(id+"F10.wireOp",EDGE,"67d3c388-b98b-4544-beb1-32861dc05394");
            var Q1376;
            Q1376=sQuery(id+"F10.wireOp",EDGE,"f7209e18-1250-466d-8cfe-28c9f1cf4efd");
            var Q1377;
            Q1377=sQuery(id+"F10.wireOp",EDGE,"f88eadd6-fb7b-4c07-9882-642046c9fefa");
            var Q1378;
            Q1378=sQuery(id+"F10.wireOp",EDGE,"94a244e5-bdd5-4fad-9412-e58b6ee94790");
            var Q1379;
            Q1379=sQuery(id+"F10.wireOp",EDGE,"134c9f13-ba7c-4f26-a8b9-b554042b0308");
            var Q1380;
            Q1380=sQuery(id+"F10.wireOp",EDGE,"565c871e-a66e-4ca2-8904-be324d3ee31b");
            var Q1381;
            Q1381=sQuery(id+"F10.wireOp",EDGE,"6f99def8-c5f3-4203-b2b7-204e1e69a1a4");
            var Q1382;
            Q1382=sQuery(id+"F10.wireOp",EDGE,"182d5a0b-4ceb-4145-bd4f-d09a2e3a4c03");
            var Q1383;
            Q1383=sQuery(id+"F10.wireOp",EDGE,"138556ae-127c-41a5-bde3-7df75f3df05c");
            var Q1384;
            Q1384=sQuery(id+"F10.wireOp",EDGE,"c5c2027d-240b-4ed2-a469-854e481eb173");
            var Q1385;
            Q1385=sQuery(id+"F10.wireOp",EDGE,"0dbf20ac-e090-415e-8f2a-584fa5695cc0");
            var Q1386;
            Q1386=sQuery(id+"F10.wireOp",EDGE,"40e8bb92-1fa4-4b64-a5fd-278300086698");
            var Q1387;
            Q1387=sQuery(id+"F10.wireOp",EDGE,"d04d030b-6e57-4015-a0a1-a413c6bbea65");
            var Q1388;
            Q1388=sQuery(id+"F10.wireOp",EDGE,"c20aa829-8a03-43fc-a23c-3f91ceb69ecf");
            var Q1389;
            Q1389=sQuery(id+"F10.wireOp",EDGE,"00f36ef8-a0d0-4658-8a5e-1c9a33825d7b");
            var Q1390;
            Q1390=sQuery(id+"F10.wireOp",EDGE,"52fcb52c-2d95-4d1c-8676-c4de6b298121");
            var Q1391;
            Q1391=sQuery(id+"F10.wireOp",EDGE,"2eda7eee-5215-4be2-91f8-95eb056c1cbe");
            var Q1392;
            Q1392=sQuery(id+"F10.wireOp",EDGE,"f54df4b6-40fd-489d-bc73-05d1f3668d34");
            var Q1393;
            Q1393=sQuery(id+"F10.wireOp",EDGE,"a8bf09c8-8c7a-4861-ba61-10413f53c5d2");
            var Q1394;
            Q1394=sQuery(id+"F10.wireOp",EDGE,"15e742a5-ef71-4305-9c97-5236bb409508");
            var Q1395;
            Q1395=sQuery(id+"F10.wireOp",EDGE,"06c76014-8723-472a-8851-391461e52b64");
            var Q1396;
            Q1396=sQuery(id+"F10.wireOp",EDGE,"c58b8338-0703-40ed-81fe-16334ba8c56e");
            var Q1397;
            Q1397=sQuery(id+"F10.wireOp",EDGE,"389b1d28-f23a-4ea6-9a4c-85afd8b2ea41");
            var Q1398;
            Q1398=sQuery(id+"F10.wireOp",EDGE,"8cdf0ebc-fa4f-4d62-83d6-92c309009988");
            var Q1399;
            Q1399=sQuery(id+"F10.wireOp",EDGE,"9da5696e-7882-4fa9-b72a-c6d82128e760");
            var Q1400;
            Q1400=sQuery(id+"F10.wireOp",EDGE,"81be821c-bdef-464a-b192-f7b228b2846a");
            var Q1401;
            Q1401=sQuery(id+"F10.wireOp",EDGE,"32b6a14d-05d7-4d42-994a-5d02efd646e2");
            var Q1402;
            Q1402=sQuery(id+"F10.wireOp",EDGE,"2f9db55d-2467-4c54-ba8f-51334e02babf");
            var Q1403;
            Q1403=sQuery(id+"F10.wireOp",EDGE,"d846f1af-af93-49e8-ad58-d98e462368c3");
            var Q1404;
            Q1404=sQuery(id+"F10.wireOp",EDGE,"ab68624e-7c00-47c5-b4fe-1950081a715b");
            var Q1405;
            Q1405=sQuery(id+"F10.wireOp",EDGE,"e921f830-91ef-450c-beb9-ce71e7268fc9");
            var Q1406;
            Q1406=sQuery(id+"F10.wireOp",EDGE,"861a7872-bacb-4ad4-b2c1-e773042e9e78");
            var Q1407;
            Q1407=sQuery(id+"F10.wireOp",EDGE,"a855102f-7649-4b8f-94b2-26575991adbd");
            var Q1408;
            Q1408=sQuery(id+"F10.wireOp",EDGE,"74ffa285-615c-41b2-b198-e924d8837e6a");
            var Q1409;
            Q1409=sQuery(id+"F10.wireOp",EDGE,"8aaffafe-235a-4cbe-8062-fb99b41305de");
            var Q1410;
            Q1410=sQuery(id+"F10.wireOp",EDGE,"20e6e3f0-bbfc-406b-bd75-8f9a3f97d6b7");
            var Q1411;
            Q1411=sQuery(id+"F10.wireOp",EDGE,"4f9912e0-5cd9-445f-9b7c-ac104497ba90");
            var Q1412;
            Q1412=sQuery(id+"F10.wireOp",EDGE,"428c221e-d2bf-4eff-8e16-2c0ebf4b4dfe");
            var Q1413;
            Q1413=sQuery(id+"F10.wireOp",EDGE,"c49e65ae-b424-40fe-a02d-9bcf809730ec");
            var Q1414;
            Q1414=sQuery(id+"F10.wireOp",EDGE,"d03debb8-ad8a-4611-96cf-440111ca9a66");
            var Q1415;
            Q1415=sQuery(id+"F10.wireOp",EDGE,"b6d1861f-fcab-477a-b321-2b5ba42e2809");
            var Q1416;
            Q1416=sQuery(id+"F10.wireOp",EDGE,"07af377a-fc01-479a-b267-3d23829b2b29");
            var Q1417;
            Q1417=sQuery(id+"F10.wireOp",EDGE,"c8f8d298-f623-4f60-89c1-c892568a177b");
            var Q1418;
            Q1418=sQuery(id+"F10.wireOp",EDGE,"4fb5141c-ee76-4d96-a10c-40b67161808f");
            var Q1419;
            Q1419=sQuery(id+"F10.wireOp",EDGE,"e4fc0f87-19ef-4acd-a730-3b070decff4a");
            var Q1420;
            Q1420=sQuery(id+"F10.wireOp",EDGE,"38206742-b92e-458a-931e-e5f900043319");
            var Q1421;
            Q1421=sQuery(id+"F10.wireOp",EDGE,"1dddb744-80d8-4549-91b1-5e7fb63c5c70");
            var Q1422;
            Q1422=sQuery(id+"F10.wireOp",EDGE,"c17738ec-e57f-4d25-8e4a-611051ca0112");
            var Q1423;
            Q1423=sQuery(id+"F10.wireOp",EDGE,"90036a44-6cc1-4b7f-9b21-07bc6a34e740");
            var Q1424;
            Q1424=sQuery(id+"F10.wireOp",EDGE,"0999872e-530f-4fa6-84ae-fa633aa4f408");
            var Q1425;
            Q1425=sQuery(id+"F10.wireOp",EDGE,"58b31e4e-2fa2-410a-af6d-e3c1ceb6f6a3");
            var Q1426;
            Q1426=sQuery(id+"F10.wireOp",EDGE,"234d9fcc-7be2-4683-9f87-3d44d3c82700");
            var Q1427;
            Q1427=sQuery(id+"F10.wireOp",EDGE,"9b411389-0146-4ac7-90e0-329556b22198");
            var Q1428;
            Q1428=sQuery(id+"F10.wireOp",EDGE,"7355e120-25e6-4eba-b937-339ed84e0824");
            var Q1429;
            Q1429=sQuery(id+"F10.wireOp",EDGE,"3f164601-1514-4631-a023-aaca31129525");
            var Q1430;
            Q1430=sQuery(id+"F10.wireOp",EDGE,"5e58de61-a3ec-42b2-9fac-dc309ab60d1c");
            var Q1431;
            Q1431=sQuery(id+"F10.wireOp",EDGE,"542f62ab-3f0e-47c6-9ed1-4c848e61a9e0");
            var Q1432;
            Q1432=sQuery(id+"F10.wireOp",EDGE,"05978755-4523-4438-ad10-fbb8f9873ec3");
            var Q1433;
            Q1433=sQuery(id+"F10.wireOp",EDGE,"518ea409-f17a-48c2-a9c6-5a089935952b");
            var Q1434;
            Q1434=sQuery(id+"F10.wireOp",EDGE,"8979ba8a-64c0-4edf-8be1-3b0cd299a0d3");
            var Q1435;
            Q1435=sQuery(id+"F10.wireOp",EDGE,"dc793e20-b6ec-4767-a851-dfe6f24ef898");
            var Q1436;
            Q1436=sQuery(id+"F10.wireOp",EDGE,"8c7905e9-54d9-433c-a0f5-81abda80e68e");
            var Q1437;
            Q1437=sQuery(id+"F10.wireOp",EDGE,"2a4e87d3-db89-4213-acc6-6cef92357c84");
            var Q1438;
            Q1438=sQuery(id+"F10.wireOp",EDGE,"73c77a9b-ed02-499b-a2d8-f308abde06c4");
            var Q1439;
            Q1439=sQuery(id+"F10.wireOp",EDGE,"14785ed0-41a0-4d32-ad4e-ce13aca980b3");
            var Q1440;
            Q1440=sQuery(id+"F10.wireOp",EDGE,"d1973d0e-7b6f-4ffe-8a54-1b031f67c237");
            var Q1441;
            Q1441=sQuery(id+"F10.wireOp",EDGE,"ef950c08-c45a-4b7b-a862-1bdb262c0259");
            var Q1442;
            Q1442=sQuery(id+"F10.wireOp",EDGE,"d824bc7b-39cb-478b-995e-33eb04871471");
            var Q1443;
            Q1443=sQuery(id+"F10.wireOp",EDGE,"4fe8d838-a2cb-48f8-a2e5-e02c3314f283");
            var Q1444;
            Q1444=sQuery(id+"F10.wireOp",EDGE,"c54316e2-869c-4313-8789-e105341d3460");
            var Q1445;
            Q1445=sQuery(id+"F10.wireOp",EDGE,"98b91726-29eb-46b0-a881-bfb9de7ae8ba");
            var Q1446;
            Q1446=sQuery(id+"F10.wireOp",EDGE,"675cb37a-db42-4ae6-af7f-fec44ed189ed");
            var Q1447;
            Q1447=sQuery(id+"F10.wireOp",EDGE,"27981050-2c1e-4ec0-bf17-3c422cad7183");
            var Q1448;
            Q1448=sQuery(id+"F10.wireOp",EDGE,"9024da83-8bb5-4a60-b4c0-63581a1c4de3");
            var Q1449;
            Q1449=sQuery(id+"F10.wireOp",EDGE,"3b514ca0-233d-483c-8c3c-c8f03706a73f");
            var Q1450;
            Q1450=sQuery(id+"F10.wireOp",EDGE,"2a89d369-b4f8-4c19-ae81-250b5665433c");
            var Q1451;
            Q1451=sQuery(id+"F10.wireOp",EDGE,"461b6467-f06f-4a73-ac96-cb1f47278830");
            var Q1452;
            Q1452=sQuery(id+"F10.wireOp",EDGE,"5dd31b3a-c663-437e-aca1-c3efad34b51c");
            var Q1453;
            Q1453=sQuery(id+"F10.wireOp",EDGE,"b63d0583-d4f6-4217-9439-326f09cd1ac0");
            var Q1454;
            Q1454=sQuery(id+"F10.wireOp",EDGE,"698c8325-2910-45ae-9523-8401e9e01593");
            var Q1455;
            Q1455=sQuery(id+"F10.wireOp",EDGE,"61e133d6-cdec-4d74-854e-16922be70a7a");
            var Q1456;
            Q1456=sQuery(id+"F10.wireOp",EDGE,"115a9d70-ec0b-4b13-aeb9-86e231907e00");
            var Q1457;
            Q1457=sQuery(id+"F10.wireOp",EDGE,"316dc446-5b5b-4d69-81d5-86d8cc70754d");
            var Q1458;
            Q1458=sQuery(id+"F10.wireOp",EDGE,"7d776fec-192e-4b03-b042-0d7575469db1");
            var Q1459;
            Q1459=sQuery(id+"F10.wireOp",EDGE,"c17a952f-2c94-463e-b961-cbb7cb4a6333");
            var Q1460;
            Q1460=sQuery(id+"F10.wireOp",EDGE,"1119209f-0934-4074-9964-683119b5013e");
            var Q1461;
            Q1461=sQuery(id+"F10.wireOp",EDGE,"8ab183ed-9b4c-404a-bba9-4d5d88354ba3");
            var Q1462;
            Q1462=sQuery(id+"F10.wireOp",EDGE,"2ae3015f-f3b2-4224-8f47-8118b70754d0");
            var Q1463;
            Q1463=sQuery(id+"F10.wireOp",EDGE,"954555fb-dd9e-4a50-be8c-966a5d8e705c");
            var Q1464;
            Q1464=sQuery(id+"F10.wireOp",EDGE,"a8102801-e483-4aaf-b30b-f5d579ccf269");
            var Q1465;
            Q1465=sQuery(id+"F10.wireOp",EDGE,"46995c4d-977a-42a0-b42f-e73105135846");
            var Q1466;
            Q1466=sQuery(id+"F10.wireOp",EDGE,"f36ba64a-beda-43bd-a7fd-ac5f8489eabd");
            var Q1467;
            Q1467=sQuery(id+"F10.wireOp",EDGE,"d1ffd503-1814-45ac-b081-e611d6d8c32e");
            var Q1468;
            Q1468=sQuery(id+"F10.wireOp",EDGE,"55d06765-893a-4215-8375-fa8a2d4e4c54");
            var Q1469;
            Q1469=sQuery(id+"F10.wireOp",EDGE,"d35db7d0-4976-4a98-8617-eeae02454905");
            var Q1470;
            Q1470=sQuery(id+"F10.wireOp",EDGE,"cc9e398e-3ce9-45eb-96ab-a66f3b6b22d2");
            var Q1471;
            Q1471=sQuery(id+"F10.wireOp",EDGE,"82bf89ea-98db-494d-9f3c-7908d1c35b9f");
            var Q1472;
            Q1472=sQuery(id+"F10.wireOp",EDGE,"7c70217b-4268-4b0e-865d-fd2661a22796");
            var Q1473;
            Q1473=sQuery(id+"F10.wireOp",EDGE,"340b3ca7-fddf-4f9a-a064-8fba032e8baa");
            var Q1474;
            Q1474=sQuery(id+"F10.wireOp",EDGE,"2e1d1d20-7248-481f-94dd-0467b8567738");
            var Q1475;
            Q1475=sQuery(id+"F10.wireOp",EDGE,"8e33d786-14f3-435a-9c7c-72063e025557");
            var Q1476;
            Q1476=sQuery(id+"F10.wireOp",EDGE,"46fa48ad-7515-4112-a180-8c0873a88895");
            var Q1477;
            Q1477=sQuery(id+"F10.wireOp",EDGE,"be207e62-cd04-4ac1-84b5-923b3855b47a");
            var Q1478;
            Q1478=sQuery(id+"F10.wireOp",EDGE,"512b3646-7d7c-4471-90f2-f900cac7e054");
            var Q1479;
            Q1479=sQuery(id+"F10.wireOp",EDGE,"7c423559-504d-40c6-b4bb-2d1bdaad808e");
            var Q1480;
            Q1480=sQuery(id+"F10.wireOp",EDGE,"ba22d4ef-4adc-4792-b44d-f13d227e05fe");
            var Q1481;
            Q1481=sQuery(id+"F10.wireOp",EDGE,"11cc3d6d-7967-4d47-947c-0ee4fd438a9b");
            var Q1482;
            Q1482=sQuery(id+"F10.wireOp",EDGE,"0d37fd51-5ba3-4607-99eb-0e924a97f03c");
            var Q1483;
            Q1483=sQuery(id+"F10.wireOp",EDGE,"7e4c7b27-2f23-42c9-a870-57a779b68c48");
            var Q1484;
            Q1484=sQuery(id+"F10.wireOp",EDGE,"4ae8d518-ac08-47ab-9348-5acb43989b1f");
            var Q1485;
            Q1485=sQuery(id+"F10.wireOp",EDGE,"a657132b-63bc-4897-a1ee-7fca75a4ebd8");
            var Q1486;
            Q1486=sQuery(id+"F10.wireOp",EDGE,"a0260403-0c12-4ab4-9584-4ca444b81e75");
            var Q1487;
            Q1487=sQuery(id+"F10.wireOp",EDGE,"5a54da23-30dc-4103-871e-16c1addcb86f");
            var Q1488;
            Q1488=sQuery(id+"F10.wireOp",EDGE,"d88898e5-ed4a-440f-98c7-dbdd3b70fc9d");
            var Q1489;
            Q1489=sQuery(id+"F10.wireOp",EDGE,"b9314492-2bf7-4434-89c8-fa4ac35cf888");
            var Q1490;
            Q1490=sQuery(id+"F10.wireOp",EDGE,"f9471471-4b56-4f8a-87b4-9c28149c10cf");
            var Q1491;
            Q1491=sQuery(id+"F10.wireOp",EDGE,"b6556c1c-63c9-4dd6-97a4-f7658738a1c8");
            var Q1492;
            Q1492=sQuery(id+"F10.wireOp",EDGE,"51d212d5-894b-418c-ae31-bd57a10590ff");
            var Q1493;
            Q1493=sQuery(id+"F10.wireOp",EDGE,"568f6ebb-a778-4e29-ae61-b8bba1056a5b");
            var Q1494;
            Q1494=sQuery(id+"F10.wireOp",EDGE,"f751a186-8061-476f-a5e3-177acace88d3");
            var Q1495;
            Q1495=sQuery(id+"F10.wireOp",EDGE,"96f312b2-3322-47df-8dd0-8c2283ea866b");
            var Q1496;
            Q1496=sQuery(id+"F10.wireOp",EDGE,"872ee612-7230-43d3-ad0a-b55ed2fe2822");
            var Q1497;
            Q1497=sQuery(id+"F10.wireOp",EDGE,"972aad64-2134-43c5-9f74-0311e80eb365");
            var Q1498;
            Q1498=sQuery(id+"F10.wireOp",EDGE,"cfacae74-d9bf-4a3c-ae79-d5cf4c1278d8");
            var Q1499;
            Q1499=sQuery(id+"F10.wireOp",EDGE,"dbe1aca4-7255-404a-a2c3-3d1326c58f80");
            var Q1500;
            Q1500=sQuery(id+"F10.wireOp",EDGE,"169fed54-be5b-4c7c-bf19-023a4caee8a0");
            var Q1501;
            Q1501=sQuery(id+"F10.wireOp",EDGE,"a07b4ffd-c802-4b9d-aa27-4454946f62af");
            var Q1502;
            Q1502=sQuery(id+"F10.wireOp",EDGE,"006da924-4cea-4d12-ac5c-133e8273b5a7");
            var Q1503;
            Q1503=sQuery(id+"F10.wireOp",EDGE,"e2b14911-abfa-4e96-bfa7-82fdfcc81af8");
            var Q1504;
            Q1504=sQuery(id+"F10.wireOp",EDGE,"f3d753dd-e05d-4126-8e05-750c82c4568b");
            var Q1505;
            Q1505=sQuery(id+"F10.wireOp",EDGE,"7cdb2221-eede-4ddc-8050-b9fd64b6e910");
            var Q1506;
            Q1506=sQuery(id+"F10.wireOp",EDGE,"fbf128aa-b3a4-46a1-9862-b98a44ad668a");
            var Q1507;
            Q1507=sQuery(id+"F10.wireOp",EDGE,"6313cad0-8006-45a7-a39a-34a16d95b47d");
            var Q1508;
            Q1508=sQuery(id+"F10.wireOp",EDGE,"70093910-282b-465c-80f1-89bbd0949f5a");
            var Q1509;
            Q1509=sQuery(id+"F10.wireOp",EDGE,"d768df20-9e2a-447d-b569-5915ac061415");
            var Q1510;
            Q1510=sQuery(id+"F10.wireOp",EDGE,"05a8e7bd-9beb-4351-8027-743e8ca6a55e");
            var Q1511;
            Q1511=sQuery(id+"F10.wireOp",EDGE,"9635aace-5b90-48b6-ac50-d5b12027d954");
            var Q1512;
            Q1512=sQuery(id+"F10.wireOp",EDGE,"5d9874b8-f522-434a-a833-fedaa89fc459");
            var Q1513;
            Q1513=sQuery(id+"F10.wireOp",EDGE,"354a30a3-a57e-4679-9c31-363052e3bc6b");
            var Q1514;
            Q1514=sQuery(id+"F10.wireOp",EDGE,"526668ce-bd4b-4d44-90f7-1d93e9f0d7c7");
            var Q1515;
            Q1515=sQuery(id+"F10.wireOp",EDGE,"2b0e2d82-e755-4e6c-a245-a2975c918e8b");
            var Q1516;
            Q1516=sQuery(id+"F10.wireOp",EDGE,"a4d9ede8-e3da-4357-821c-1c82869a954a");
            var Q1517;
            Q1517=sQuery(id+"F10.wireOp",EDGE,"a359ab4e-861c-4739-8a1e-da342154333a");
            var Q1518;
            Q1518=sQuery(id+"F10.wireOp",EDGE,"76e0365f-571d-4b14-a1dd-dd90f3a9896f");
            var Q1519;
            Q1519=sQuery(id+"F10.wireOp",EDGE,"f3ddb232-e4c9-463d-9710-bdcd5dadb102");
            var Q1520;
            Q1520=sQuery(id+"F10.wireOp",EDGE,"5745adc7-73d4-4fd6-a03e-c027a058ea52");
            var Q1521;
            Q1521=sQuery(id+"F10.wireOp",EDGE,"4d4eea92-69de-4c88-9d0e-c65e62fd38cd");
            var Q1522;
            Q1522=sQuery(id+"F10.wireOp",EDGE,"70c5e961-eb52-4c84-8580-f9be63dfb42b");
            var Q1523;
            Q1523=sQuery(id+"F10.wireOp",EDGE,"4c2b1b37-5339-4f18-8ebf-60fde22dce8c");
            var Q1524;
            Q1524=sQuery(id+"F10.wireOp",EDGE,"9157ebeb-1211-4724-9fcd-26f9d88605b3");
            var Q1525;
            Q1525=sQuery(id+"F10.wireOp",EDGE,"4ffe8f05-f35c-429e-84ee-f8369b3862dd");
            var Q1526;
            Q1526=sQuery(id+"F10.wireOp",EDGE,"970ed1d6-e84a-4fb6-9d07-0a05fa349de5");
            var Q1527;
            Q1527=sQuery(id+"F10.wireOp",EDGE,"3177935d-8fb0-49b1-b2fb-bea8257ef5b1");
            var Q1528;
            Q1528=sQuery(id+"F10.wireOp",EDGE,"5e7ebd1a-e00e-4b24-a8d4-ee2142ab69c3");
            var Q1529;
            Q1529=sQuery(id+"F10.wireOp",EDGE,"a5ba36a5-8a79-4852-a1b6-96bd2252048a");
            var Q1530;
            Q1530=sQuery(id+"F10.wireOp",EDGE,"7abd959b-baec-412b-85bf-f57070535a54");
            var Q1531;
            Q1531=sQuery(id+"F10.wireOp",EDGE,"3a67becc-76c4-4597-8ac3-ecc2c8ec0504");
            var Q1532;
            Q1532=sQuery(id+"F10.wireOp",EDGE,"bec1b42a-6a30-4721-868e-ef417959d95b");
            var Q1533;
            Q1533=sQuery(id+"F10.wireOp",EDGE,"6ce89769-a69c-49b2-9bd5-43bec337c8b6");
            var Q1534;
            Q1534=sQuery(id+"F10.wireOp",EDGE,"9fd29dc9-7c32-441c-864d-ccbe288feb0d");
            var Q1535;
            Q1535=sQuery(id+"F10.wireOp",EDGE,"aa86ef8b-5a40-48a9-93da-f942f0996cd6");
            var Q1536;
            Q1536=sQuery(id+"F10.wireOp",EDGE,"036b8f04-45a9-4e05-8534-816cabe4a69a");
            var Q1537;
            Q1537=sQuery(id+"F10.wireOp",EDGE,"a9564e75-7df2-4190-bffb-e8fba762462e");
            var Q1538;
            Q1538=sQuery(id+"F10.wireOp",EDGE,"a777da60-5538-4f6b-9f91-6be391bd3162");
            var Q1539;
            Q1539=sQuery(id+"F10.wireOp",EDGE,"8eaf8020-d403-4b57-a48d-4e3949df32fd");
            var Q1540;
            Q1540=sQuery(id+"F10.wireOp",EDGE,"95797e03-702d-4efd-97b6-dd2fbb0bce4a");
            var Q1541;
            Q1541=sQuery(id+"F10.wireOp",EDGE,"ef7c99c0-e2a4-4994-a572-d3414ae558e8");
            var Q1542;
            Q1542=sQuery(id+"F10.wireOp",EDGE,"1aaa2472-f161-48be-86a9-7f3f7a1ec1dc");
            var Q1543;
            Q1543=sQuery(id+"F10.wireOp",EDGE,"874889ac-3ea3-4146-ad25-5d1199d748ef");
            var Q1544;
            Q1544=sQuery(id+"F10.wireOp",EDGE,"066df633-216a-46af-8a77-dab70c3642c7");
            var Q1545;
            Q1545=sQuery(id+"F10.wireOp",EDGE,"d5010102-5312-4bed-bc63-101d1c522f96");
            var Q1546;
            Q1546=sQuery(id+"F10.wireOp",EDGE,"51211631-8a4b-4eef-b9cf-c3fd6ea0ba73");
            var Q1547;
            Q1547=sQuery(id+"F10.wireOp",EDGE,"701987e0-4814-450f-9985-56268bd12bf7");
            var Q1548;
            Q1548=sQuery(id+"F10.wireOp",EDGE,"36b05464-ecf4-4a57-a67e-301a8f2d8a33");
            var Q1549;
            Q1549=sQuery(id+"F10.wireOp",EDGE,"fe50aa5d-ddd8-42c8-9725-ddc6ae36e570");
            var Q1550;
            Q1550=sQuery(id+"F10.wireOp",EDGE,"c2f5e099-4ad6-47b1-891c-ece025434bc5");
            var Q1551;
            Q1551=sQuery(id+"F10.wireOp",EDGE,"a6bd0e56-16a9-40ea-ae90-756fa9a7951e");
            var Q1552;
            Q1552=sQuery(id+"F10.wireOp",EDGE,"f87958af-3b9c-4fdf-8149-a7f8b2f087da");
            var Q1553;
            Q1553=sQuery(id+"F10.wireOp",EDGE,"855ecb89-86cf-4848-927e-39cababe6467");
            var Q1554;
            Q1554=sQuery(id+"F10.wireOp",EDGE,"d7bd1036-f5bf-4069-a008-ebc277b40a53");
            var Q1555;
            Q1555=sQuery(id+"F10.wireOp",EDGE,"1de2d15f-ad5c-4a4d-982e-9e985bcf79b8");
            var Q1556;
            Q1556=sQuery(id+"F10.wireOp",EDGE,"935b80e7-8588-42ab-9f68-0fae790d9c43");
            var Q1557;
            Q1557=sQuery(id+"F10.wireOp",EDGE,"83b0e1ac-bf1b-4997-848e-ec3449fbda38");
            var Q1558;
            Q1558=sQuery(id+"F10.wireOp",EDGE,"bb975e88-a1d8-4221-88fb-093c46761cdc");
            var Q1559;
            Q1559=sQuery(id+"F10.wireOp",EDGE,"0c9930c8-daf2-400a-abbd-61f701cac0bc");
            var Q1560;
            Q1560=sQuery(id+"F10.wireOp",EDGE,"dca5d196-3129-4635-b93d-cb818bc2682b");
            var Q1561;
            Q1561=sQuery(id+"F10.wireOp",EDGE,"0ff40bbf-e49f-4918-be7a-66a2f8025a9b");
            var Q1562;
            Q1562=sQuery(id+"F10.wireOp",EDGE,"159812cb-4240-43f0-8f7b-169bdf926de2");
            var Q1563;
            Q1563=sQuery(id+"F10.wireOp",EDGE,"875f59ce-6333-4731-aeb1-211f74ef38f8");
            var Q1564;
            Q1564=sQuery(id+"F10.wireOp",EDGE,"f722df0f-240b-43cc-95e4-5fd41f9a58f2");
            var Q1565;
            Q1565=sQuery(id+"F10.wireOp",EDGE,"41606cc4-44d9-47c2-9ec3-c15da28ec91f");
            var Q1566;
            Q1566=sQuery(id+"F10.wireOp",EDGE,"5b877085-c569-431f-a232-0193555a28e2");
            var Q1567;
            Q1567=sQuery(id+"F10.wireOp",EDGE,"a1c5beb5-45d5-4dfc-bd9f-530224769e0c");
            var Q1568;
            Q1568=sQuery(id+"F10.wireOp",EDGE,"a17369db-5ee5-4187-a1d5-656a4d41ce7f");
            var Q1569;
            Q1569=sQuery(id+"F10.wireOp",EDGE,"e8e7d0c5-964a-426e-8eaf-7a61dae73f91");
            var Q1570;
            Q1570=sQuery(id+"F10.wireOp",EDGE,"7a7ca846-a01b-4d18-9c53-c2b27d0894d9");
            var Q1571;
            Q1571=sQuery(id+"F10.wireOp",EDGE,"c4c57dcb-62fd-4282-a158-d7917ed8fa46");
            var Q1572;
            Q1572=sQuery(id+"F10.wireOp",EDGE,"47eb9a11-1dd2-4788-8be0-0437d5e95c7e");
            var Q1573;
            Q1573=sQuery(id+"F10.wireOp",EDGE,"2227200d-e1ff-44d8-a515-57abf2abd7a0");
            var Q1574;
            Q1574=sQuery(id+"F10.wireOp",EDGE,"7b292f5c-3cc6-44b1-bcfb-8713ea5ddda4");
            var Q1575;
            Q1575=sQuery(id+"F10.wireOp",EDGE,"70303eff-417e-4dd1-ad6e-f285f15360dc");
            var Q1576;
            Q1576=sQuery(id+"F10.wireOp",EDGE,"62bed24e-bbb4-41cc-9600-f217c27de104");
            var Q1577;
            Q1577=sQuery(id+"F10.wireOp",EDGE,"5fb01994-4f75-46d4-9c99-b91b54068d99");
            var Q1578;
            Q1578=sQuery(id+"F10.wireOp",EDGE,"e8de8496-7cd0-40c5-a8da-0405098e44bb");
            var Q1579;
            Q1579=sQuery(id+"F10.wireOp",EDGE,"0331374b-12da-4d9a-8114-fc0243becddc");
            var Q1580;
            Q1580=sQuery(id+"F10.wireOp",EDGE,"f8ef9fba-f514-4d39-8754-fd3ba1c0706d");
            var Q1581;
            Q1581=sQuery(id+"F10.wireOp",EDGE,"9308c284-bde3-4740-828d-4787544fd684");
            var Q1582;
            Q1582=sQuery(id+"F10.wireOp",EDGE,"a52c5e48-da1f-4e86-80a7-d2511946f297");
            var Q1583;
            Q1583=sQuery(id+"F10.wireOp",EDGE,"89676319-c01d-4bd1-9a07-74b952f16691");
            var Q1584;
            Q1584=sQuery(id+"F10.wireOp",EDGE,"a70875a9-fbde-4e53-b299-e4b1779b5be2");
            var Q1585;
            Q1585=sQuery(id+"F10.wireOp",EDGE,"15638edc-8506-42e2-ae2a-97e69741103d");
            var Q1586;
            Q1586=sQuery(id+"F10.wireOp",EDGE,"aad2dfed-ba8c-4d85-83de-1219a2f8efea");
            var Q1587;
            Q1587=sQuery(id+"F10.wireOp",EDGE,"68bedd21-4bfe-4007-9780-8ab67643f58e");
            var Q1588;
            Q1588=sQuery(id+"F10.wireOp",EDGE,"5ed881b6-c9f8-4642-8300-80f8653c925a");
            var Q1589;
            Q1589=sQuery(id+"F10.wireOp",EDGE,"6f8ef1f4-29c2-4c01-84ec-86a14daaa52f");
            var Q1590;
            Q1590=sQuery(id+"F10.wireOp",EDGE,"da0e961e-7cbf-487c-9cdf-45c28f62fa66");
            var Q1591;
            Q1591=sQuery(id+"F10.wireOp",EDGE,"17982832-84fe-4362-aa9f-5d76951fca7c");
            var Q1592;
            Q1592=sQuery(id+"F10.wireOp",EDGE,"aaddbe43-6a86-4970-b725-0ba66dd9c3dd");
            var Q1593;
            Q1593=sQuery(id+"F10.wireOp",EDGE,"ca20e7bc-50fb-41bd-9f9e-8aa5635bd5c7");
            var Q1594;
            Q1594=sQuery(id+"F10.wireOp",EDGE,"c83638de-c063-4df6-8ffd-7e9b353b8067");
            var Q1595;
            Q1595=sQuery(id+"F10.wireOp",EDGE,"22d70b48-fb39-4444-aadf-9436f7afa3ab");
            var Q1596;
            Q1596=sQuery(id+"F10.wireOp",EDGE,"088d1791-04a7-475f-9512-3f226d9d0d8e");
            var Q1597;
            Q1597=sQuery(id+"F10.wireOp",EDGE,"2902fab2-373f-4e05-83b0-60b07d25aea8");
            var Q1598;
            Q1598=sQuery(id+"F10.wireOp",EDGE,"d0def636-ff7e-4027-a01c-40f05abd657d");
            var Q1599;
            Q1599=sQuery(id+"F10.wireOp",EDGE,"3c72fe21-0024-4ce2-9f5b-81bcd854cfd0");
            var Q1600;
            Q1600=sQuery(id+"F10.wireOp",EDGE,"4e1a7ba0-05a7-400c-b5b4-4ecffe60ef03");
            var Q1601;
            Q1601=sQuery(id+"F10.wireOp",EDGE,"14d6bfc1-26c3-4417-9b45-2a5ed59d9bde");
            var Q1602;
            Q1602=sQuery(id+"F10.wireOp",EDGE,"7d7430c5-8867-4669-b55c-73f8d02aabc8");
            var Q1603;
            Q1603=sQuery(id+"F10.wireOp",EDGE,"ae2dc30b-d4d7-4851-88f5-f96f25262f90");
            var Q1604;
            Q1604=sQuery(id+"F10.wireOp",EDGE,"d90060f1-b034-4431-a4a8-c732d086df92");
            var Q1605;
            Q1605=sQuery(id+"F10.wireOp",EDGE,"cfae87f6-3acd-4b15-9833-410bc9cc2d11");
            var Q1606;
            Q1606=sQuery(id+"F10.wireOp",EDGE,"2ad778b3-7137-4546-b956-de64cf252efa");
            var Q1607;
            Q1607=sQuery(id+"F10.wireOp",EDGE,"516c0f6d-0afd-4965-8de7-c31da46ca51a");
            var Q1608;
            Q1608=sQuery(id+"F10.wireOp",EDGE,"5b51d4df-3d8f-41d4-963e-b50c666ef08e");
            var Q1609;
            Q1609=sQuery(id+"F10.wireOp",EDGE,"5b172e6b-58ae-44e9-80de-3628377f505e");
            var Q1610;
            Q1610=sQuery(id+"F10.wireOp",EDGE,"4cb53e9e-67ab-4be2-a290-26c270870a8f");
            var Q1611;
            Q1611=sQuery(id+"F10.wireOp",EDGE,"97c9ed15-8a86-4747-97c3-e56f35e7ea7b");
            var Q1612;
            Q1612=sQuery(id+"F10.wireOp",EDGE,"93d7b6ac-51ff-4f04-89d8-9da5d165cfcb");
            var Q1613;
            Q1613=sQuery(id+"F10.wireOp",EDGE,"fcd5743c-3a2c-4b1c-9906-7118e22040ff");
            var Q1614;
            Q1614=sQuery(id+"F10.wireOp",EDGE,"2da977e1-5471-41ed-a0d5-501534912b7f");
            var Q1615;
            Q1615=sQuery(id+"F10.wireOp",EDGE,"11f6f13f-69ee-4a8c-87a6-e81c5a67bc07");
            var Q1616;
            Q1616=sQuery(id+"F10.wireOp",EDGE,"218ab241-3c70-4c22-ad9d-b6aea85e576a");
            var Q1617;
            Q1617=sQuery(id+"F10.wireOp",EDGE,"f8e48ed0-18d7-45c1-97a1-5bc29ec5ca1d");
            var Q1618;
            Q1618=sQuery(id+"F10.wireOp",EDGE,"36242636-472c-4369-ab85-d12aa211ee69");
            var Q1619;
            Q1619=sQuery(id+"F10.wireOp",EDGE,"732352e8-6478-4d5d-9510-310157b3a3be");
            var Q1620;
            Q1620=sQuery(id+"F10.wireOp",EDGE,"5ab49154-54ec-420b-a09f-c2320fadfeec");
            var Q1621;
            Q1621=sQuery(id+"F10.wireOp",EDGE,"8a9410fc-8b5f-4b01-b204-eb08e8f7e01a");
            var Q1622;
            Q1622=sQuery(id+"F10.wireOp",EDGE,"165bed89-fa57-4cea-b305-706e20d37cab");
            var Q1623;
            Q1623=sQuery(id+"F10.wireOp",EDGE,"a50db57a-b7af-4193-ae95-ec16021f6948");
            var Q1624;
            Q1624=sQuery(id+"F10.wireOp",EDGE,"6fc46035-b9da-4705-a7ab-94a5585650b2");
            var Q1625;
            Q1625=sQuery(id+"F10.wireOp",EDGE,"d8c848c5-70f8-48b3-a62c-3835fd45a5b0");
            var Q1626;
            Q1626=sQuery(id+"F10.wireOp",EDGE,"8e56d7cd-bd07-4ca7-8c30-6ef4b9e9dcb4");
            var Q1627;
            Q1627=sQuery(id+"F10.wireOp",EDGE,"c358497a-3515-4ee9-b1ed-635cbdac17dd");
            var Q1628;
            Q1628=sQuery(id+"F10.wireOp",EDGE,"5e6b5363-8292-4c6c-8214-ee32900bbca8");
            var Q1629;
            Q1629=sQuery(id+"F10.wireOp",EDGE,"8e9a30bc-5624-4b95-add3-e53abfe187dd");
            var Q1630;
            Q1630=sQuery(id+"F10.wireOp",EDGE,"2e374513-c559-4775-9688-24c58a476136");
            var Q1631;
            Q1631=sQuery(id+"F10.wireOp",EDGE,"764657e9-2a42-42cc-b7ee-8f10bc33975e");
            var Q1632;
            Q1632=sQuery(id+"F10.wireOp",EDGE,"c7e399eb-e7d1-477c-ba72-5b677a116334");
            var Q1633;
            Q1633=sQuery(id+"F10.wireOp",EDGE,"69e8ad43-e485-46e3-86e4-bd56f7b0e45c");
            var Q1634;
            Q1634=sQuery(id+"F10.wireOp",EDGE,"5ae462d8-e1df-4585-9ceb-f2943e0a36a7");
            var Q1635;
            Q1635=sQuery(id+"F10.wireOp",EDGE,"f6d4be00-b35e-4fd8-9a2f-43e16fa3c9ef");
            var Q1636;
            Q1636=sQuery(id+"F10.wireOp",EDGE,"7ce57ff7-1d16-450e-b23e-ce72ed57d64e");
            var Q1637;
            Q1637=sQuery(id+"F10.wireOp",EDGE,"8b641419-6be3-4e72-90ff-8b4092e089d7");
            var Q1638;
            Q1638=sQuery(id+"F10.wireOp",EDGE,"4ed7f211-1ed0-43b9-8f1a-5aca18164cb2");
            var Q1639;
            Q1639=sQuery(id+"F10.wireOp",EDGE,"f38e1548-1851-4501-894d-8a82377f481e");
            var Q1640;
            Q1640=sQuery(id+"F10.wireOp",EDGE,"fdd988e0-d954-4c27-8221-55b778684f07");
            var Q1641;
            Q1641=sQuery(id+"F10.wireOp",EDGE,"b86aa493-2da8-4415-b635-acce5e080168");
            var Q1642;
            Q1642=sQuery(id+"F10.wireOp",EDGE,"4f377070-872b-4062-a112-cf90def15188");
            extrude(context, id + "F11", {"entities" : qUnion([Q0]), "operationType" : NewBodyOperationType.ADD, "surfaceOperationType" : NewSurfaceOperationType.ADD, "surfaceEntities" : qUnion([Q1, Q2, Q3, Q4, Q5, Q6, Q7, Q8, Q9, Q10, Q11, Q12, Q13, Q14, Q15, Q16, Q17, Q18, Q19, Q20, Q21, Q22, Q23, Q24, Q25, Q26, Q27, Q28, Q29, Q30, Q31, Q32, Q33, Q34, Q35, Q36, Q37, Q38, Q39, Q40, Q41, Q42, Q43, Q44, Q45, Q46, Q47, Q48, Q49, Q50, Q51, Q52, Q53, Q54, Q55, Q56, Q57, Q58, Q59, Q60, Q61, Q62, Q63, Q64, Q65, Q66, Q67, Q68, Q69, Q70, Q71, Q72, Q73, Q74, Q75, Q76, Q77, Q78, Q79, Q80, Q81, Q82, Q83, Q84, Q85, Q86, Q87, Q88, Q89, Q90, Q91, Q92, Q93, Q94, Q95, Q96, Q97, Q98, Q99, Q100, Q101, Q102, Q103, Q104, Q105, Q106, Q107, Q108, Q109, Q110, Q111, Q112, Q113, Q114, Q115, Q116, Q117, Q118, Q119, Q120, Q121, Q122, Q123, Q124, Q125, Q126, Q127, Q128, Q129, Q130, Q131, Q132, Q133, Q134, Q135, Q136, Q137, Q138, Q139, Q140, Q141, Q142, Q143, Q144, Q145, Q146, Q147, Q148, Q149, Q150, Q151, Q152, Q153, Q154, Q155, Q156, Q157, Q158, Q159, Q160, Q161, Q162, Q163, Q164, Q165, Q166, Q167, Q168, Q169, Q170, Q171, Q172, Q173, Q174, Q175, Q176, Q177, Q178, Q179, Q180, Q181, Q182, Q183, Q184, Q185, Q186, Q187, Q188, Q189, Q190, Q191, Q192, Q193, Q194, Q195, Q196, Q197, Q198, Q199, Q200, Q201, Q202, Q203, Q204, Q205, Q206, Q207, Q208, Q209, Q210, Q211, Q212, Q213, Q214, Q215, Q216, Q217, Q218, Q219, Q220, Q221, Q222, Q223, Q224, Q225, Q226, Q227, Q228, Q229, Q230, Q231, Q232, Q233, Q234, Q235, Q236, Q237, Q238, Q239, Q240, Q241, Q242, Q243, Q244, Q245, Q246, Q247, Q248, Q249, Q250, Q251, Q252, Q253, Q254, Q255, Q256, Q257, Q258, Q259, Q260, Q261, Q262, Q263, Q264, Q265, Q266, Q267, Q268, Q269, Q270, Q271, Q272, Q273, Q274, Q275, Q276, Q277, Q278, Q279, Q280, Q281, Q282, Q283, Q284, Q285, Q286, Q287, Q288, Q289, Q290, Q291, Q292, Q293, Q294, Q295, Q296, Q297, Q298, Q299, Q300, Q301, Q302, Q303, Q304, Q305, Q306, Q307, Q308, Q309, Q310, Q311, Q312, Q313, Q314, Q315, Q316, Q317, Q318, Q319, Q320, Q321, Q322, Q323, Q324, Q325, Q326, Q327, Q328, Q329, Q330, Q331, Q332, Q333, Q334, Q335, Q336, Q337, Q338, Q339, Q340, Q341, Q342, Q343, Q344, Q345, Q346, Q347, Q348, Q349, Q350, Q351, Q352, Q353, Q354, Q355, Q356, Q357, Q358, Q359, Q360, Q361, Q362, Q363, Q364, Q365, Q366, Q367, Q368, Q369, Q370, Q371, Q372, Q373, Q374, Q375, Q376, Q377, Q378, Q379, Q380, Q381, Q382, Q383, Q384, Q385, Q386, Q387, Q388, Q389, Q390, Q391, Q392, Q393, Q394, Q395, Q396, Q397, Q398, Q399, Q400, Q401, Q402, Q403, Q404, Q405, Q406, Q407, Q408, Q409, Q410, Q411, Q412, Q413, Q414, Q415, Q416, Q417, Q418, Q419, Q420, Q421, Q422, Q423, Q424, Q425, Q426, Q427, Q428, Q429, Q430, Q431, Q432, Q433, Q434, Q435, Q436, Q437, Q438, Q439, Q440, Q441, Q442, Q443, Q444, Q445, Q446, Q447, Q448, Q449, Q450, Q451, Q452, Q453, Q454, Q455, Q456, Q457, Q458, Q459, Q460, Q461, Q462, Q463, Q464, Q465, Q466, Q467, Q468, Q469, Q470, Q471, Q472, Q473, Q474, Q475, Q476, Q477, Q478, Q479, Q480, Q481, Q482, Q483, Q484, Q485, Q486, Q487, Q488, Q489, Q490, Q491, Q492, Q493, Q494, Q495, Q496, Q497, Q498, Q499, Q500, Q501, Q502, Q503, Q504, Q505, Q506, Q507, Q508, Q509, Q510, Q511, Q512, Q513, Q514, Q515, Q516, Q517, Q518, Q519, Q520, Q521, Q522, Q523, Q524, Q525, Q526, Q527, Q528, Q529, Q530, Q531, Q532, Q533, Q534, Q535, Q536, Q537, Q538, Q539, Q540, Q541, Q542, Q543, Q544, Q545, Q546, Q547, Q548, Q549, Q550, Q551, Q552, Q553, Q554, Q555, Q556, Q557, Q558, Q559, Q560, Q561, Q562, Q563, Q564, Q565, Q566, Q567, Q568, Q569, Q570, Q571, Q572, Q573, Q574, Q575, Q576, Q577, Q578, Q579, Q580, Q581, Q582, Q583, Q584, Q585, Q586, Q587, Q588, Q589, Q590, Q591, Q592, Q593, Q594, Q595, Q596, Q597, Q598, Q599, Q600, Q601, Q602, Q603, Q604, Q605, Q606, Q607, Q608, Q609, Q610, Q611, Q612, Q613, Q614, Q615, Q616, Q617, Q618, Q619, Q620, Q621, Q622, Q623, Q624, Q625, Q626, Q627, Q628, Q629, Q630, Q631, Q632, Q633, Q634, Q635, Q636, Q637, Q638, Q639, Q640, Q641, Q642, Q643, Q644, Q645, Q646, Q647, Q648, Q649, Q650, Q651, Q652, Q653, Q654, Q655, Q656, Q657, Q658, Q659, Q660, Q661, Q662, Q663, Q664, Q665, Q666, Q667, Q668, Q669, Q670, Q671, Q672, Q673, Q674, Q675, Q676, Q677, Q678, Q679, Q680, Q681, Q682, Q683, Q684, Q685, Q686, Q687, Q688, Q689, Q690, Q691, Q692, Q693, Q694, Q695, Q696, Q697, Q698, Q699, Q700, Q701, Q702, Q703, Q704, Q705, Q706, Q707, Q708, Q709, Q710, Q711, Q712, Q713, Q714, Q715, Q716, Q717, Q718, Q719, Q720, Q721, Q722, Q723, Q724, Q725, Q726, Q727, Q728, Q729, Q730, Q731, Q732, Q733, Q734, Q735, Q736, Q737, Q738, Q739, Q740, Q741, Q742, Q743, Q744, Q745, Q746, Q747, Q748, Q749, Q750, Q751, Q752, Q753, Q754, Q755, Q756, Q757, Q758, Q759, Q760, Q761, Q762, Q763, Q764, Q765, Q766, Q767, Q768, Q769, Q770, Q771, Q772, Q773, Q774, Q775, Q776, Q777, Q778, Q779, Q780, Q781, Q782, Q783, Q784, Q785, Q786, Q787, Q788, Q789, Q790, Q791, Q792, Q793, Q794, Q795, Q796, Q797, Q798, Q799, Q800, Q801, Q802, Q803, Q804, Q805, Q806, Q807, Q808, Q809, Q810, Q811, Q812, Q813, Q814, Q815, Q816, Q817, Q818, Q819, Q820, Q821, Q822, Q823, Q824, Q825, Q826, Q827, Q828, Q829, Q830, Q831, Q832, Q833, Q834, Q835, Q836, Q837, Q838, Q839, Q840, Q841, Q842, Q843, Q844, Q845, Q846, Q847, Q848, Q849, Q850, Q851, Q852, Q853, Q854, Q855, Q856, Q857, Q858, Q859, Q860, Q861, Q862, Q863, Q864, Q865, Q866, Q867, Q868, Q869, Q870, Q871, Q872, Q873, Q874, Q875, Q876, Q877, Q878, Q879, Q880, Q881, Q882, Q883, Q884, Q885, Q886, Q887, Q888, Q889, Q890, Q891, Q892, Q893, Q894, Q895, Q896, Q897, Q898, Q899, Q900, Q901, Q902, Q903, Q904, Q905, Q906, Q907, Q908, Q909, Q910, Q911, Q912, Q913, Q914, Q915, Q916, Q917, Q918, Q919, Q920, Q921, Q922, Q923, Q924, Q925, Q926, Q927, Q928, Q929, Q930, Q931, Q932, Q933, Q934, Q935, Q936, Q937, Q938, Q939, Q940, Q941, Q942, Q943, Q944, Q945, Q946, Q947, Q948, Q949, Q950, Q951, Q952, Q953, Q954, Q955, Q956, Q957, Q958, Q959, Q960, Q961, Q962, Q963, Q964, Q965, Q966, Q967, Q968, Q969, Q970, Q971, Q972, Q973, Q974, Q975, Q976, Q977, Q978, Q979, Q980, Q981, Q982, Q983, Q984, Q985, Q986, Q987, Q988, Q989, Q990, Q991, Q992, Q993, Q994, Q995, Q996, Q997, Q998, Q999, Q1000, Q1001, Q1002, Q1003, Q1004, Q1005, Q1006, Q1007, Q1008, Q1009, Q1010, Q1011, Q1012, Q1013, Q1014, Q1015, Q1016, Q1017, Q1018, Q1019, Q1020, Q1021, Q1022, Q1023, Q1024, Q1025, Q1026, Q1027, Q1028, Q1029, Q1030, Q1031, Q1032, Q1033, Q1034, Q1035, Q1036, Q1037, Q1038, Q1039, Q1040, Q1041, Q1042, Q1043, Q1044, Q1045, Q1046, Q1047, Q1048, Q1049, Q1050, Q1051, Q1052, Q1053, Q1054, Q1055, Q1056, Q1057, Q1058, Q1059, Q1060, Q1061, Q1062, Q1063, Q1064, Q1065, Q1066, Q1067, Q1068, Q1069, Q1070, Q1071, Q1072, Q1073, Q1074, Q1075, Q1076, Q1077, Q1078, Q1079, Q1080, Q1081, Q1082, Q1083, Q1084, Q1085, Q1086, Q1087, Q1088, Q1089, Q1090, Q1091, Q1092, Q1093, Q1094, Q1095, Q1096, Q1097, Q1098, Q1099, Q1100, Q1101, Q1102, Q1103, Q1104, Q1105, Q1106, Q1107, Q1108, Q1109, Q1110, Q1111, Q1112, Q1113, Q1114, Q1115, Q1116, Q1117, Q1118, Q1119, Q1120, Q1121, Q1122, Q1123, Q1124, Q1125, Q1126, Q1127, Q1128, Q1129, Q1130, Q1131, Q1132, Q1133, Q1134, Q1135, Q1136, Q1137, Q1138, Q1139, Q1140, Q1141, Q1142, Q1143, Q1144, Q1145, Q1146, Q1147, Q1148, Q1149, Q1150, Q1151, Q1152, Q1153, Q1154, Q1155, Q1156, Q1157, Q1158, Q1159, Q1160, Q1161, Q1162, Q1163, Q1164, Q1165, Q1166, Q1167, Q1168, Q1169, Q1170, Q1171, Q1172, Q1173, Q1174, Q1175, Q1176, Q1177, Q1178, Q1179, Q1180, Q1181, Q1182, Q1183, Q1184, Q1185, Q1186, Q1187, Q1188, Q1189, Q1190, Q1191, Q1192, Q1193, Q1194, Q1195, Q1196, Q1197, Q1198, Q1199, Q1200, Q1201, Q1202, Q1203, Q1204, Q1205, Q1206, Q1207, Q1208, Q1209, Q1210, Q1211, Q1212, Q1213, Q1214, Q1215, Q1216, Q1217, Q1218, Q1219, Q1220, Q1221, Q1222, Q1223, Q1224, Q1225, Q1226, Q1227, Q1228, Q1229, Q1230, Q1231, Q1232, Q1233, Q1234, Q1235, Q1236, Q1237, Q1238, Q1239, Q1240, Q1241, Q1242, Q1243, Q1244, Q1245, Q1246, Q1247, Q1248, Q1249, Q1250, Q1251, Q1252, Q1253, Q1254, Q1255, Q1256, Q1257, Q1258, Q1259, Q1260, Q1261, Q1262, Q1263, Q1264, Q1265, Q1266, Q1267, Q1268, Q1269, Q1270, Q1271, Q1272, Q1273, Q1274, Q1275, Q1276, Q1277, Q1278, Q1279, Q1280, Q1281, Q1282, Q1283, Q1284, Q1285, Q1286, Q1287, Q1288, Q1289, Q1290, Q1291, Q1292, Q1293, Q1294, Q1295, Q1296, Q1297, Q1298, Q1299, Q1300, Q1301, Q1302, Q1303, Q1304, Q1305, Q1306, Q1307, Q1308, Q1309, Q1310, Q1311, Q1312, Q1313, Q1314, Q1315, Q1316, Q1317, Q1318, Q1319, Q1320, Q1321, Q1322, Q1323, Q1324, Q1325, Q1326, Q1327, Q1328, Q1329, Q1330, Q1331, Q1332, Q1333, Q1334, Q1335, Q1336, Q1337, Q1338, Q1339, Q1340, Q1341, Q1342, Q1343, Q1344, Q1345, Q1346, Q1347, Q1348, Q1349, Q1350, Q1351, Q1352, Q1353, Q1354, Q1355, Q1356, Q1357, Q1358, Q1359, Q1360, Q1361, Q1362, Q1363, Q1364, Q1365, Q1366, Q1367, Q1368, Q1369, Q1370, Q1371, Q1372, Q1373, Q1374, Q1375, Q1376, Q1377, Q1378, Q1379, Q1380, Q1381, Q1382, Q1383, Q1384, Q1385, Q1386, Q1387, Q1388, Q1389, Q1390, Q1391, Q1392, Q1393, Q1394, Q1395, Q1396, Q1397, Q1398, Q1399, Q1400, Q1401, Q1402, Q1403, Q1404, Q1405, Q1406, Q1407, Q1408, Q1409, Q1410, Q1411, Q1412, Q1413, Q1414, Q1415, Q1416, Q1417, Q1418, Q1419, Q1420, Q1421, Q1422, Q1423, Q1424, Q1425, Q1426, Q1427, Q1428, Q1429, Q1430, Q1431, Q1432, Q1433, Q1434, Q1435, Q1436, Q1437, Q1438, Q1439, Q1440, Q1441, Q1442, Q1443, Q1444, Q1445, Q1446, Q1447, Q1448, Q1449, Q1450, Q1451, Q1452, Q1453, Q1454, Q1455, Q1456, Q1457, Q1458, Q1459, Q1460, Q1461, Q1462, Q1463, Q1464, Q1465, Q1466, Q1467, Q1468, Q1469, Q1470, Q1471, Q1472, Q1473, Q1474, Q1475, Q1476, Q1477, Q1478, Q1479, Q1480, Q1481, Q1482, Q1483, Q1484, Q1485, Q1486, Q1487, Q1488, Q1489, Q1490, Q1491, Q1492, Q1493, Q1494, Q1495, Q1496, Q1497, Q1498, Q1499, Q1500, Q1501, Q1502, Q1503, Q1504, Q1505, Q1506, Q1507, Q1508, Q1509, Q1510, Q1511, Q1512, Q1513, Q1514, Q1515, Q1516, Q1517, Q1518, Q1519, Q1520, Q1521, Q1522, Q1523, Q1524, Q1525, Q1526, Q1527, Q1528, Q1529, Q1530, Q1531, Q1532, Q1533, Q1534, Q1535, Q1536, Q1537, Q1538, Q1539, Q1540, Q1541, Q1542, Q1543, Q1544, Q1545, Q1546, Q1547, Q1548, Q1549, Q1550, Q1551, Q1552, Q1553, Q1554, Q1555, Q1556, Q1557, Q1558, Q1559, Q1560, Q1561, Q1562, Q1563, Q1564, Q1565, Q1566, Q1567, Q1568, Q1569, Q1570, Q1571, Q1572, Q1573, Q1574, Q1575, Q1576, Q1577, Q1578, Q1579, Q1580, Q1581, Q1582, Q1583, Q1584, Q1585, Q1586, Q1587, Q1588, Q1589, Q1590, Q1591, Q1592, Q1593, Q1594, Q1595, Q1596, Q1597, Q1598, Q1599, Q1600, Q1601, Q1602, Q1603, Q1604, Q1605, Q1606, Q1607, Q1608, Q1609, Q1610, Q1611, Q1612, Q1613, Q1614, Q1615, Q1616, Q1617, Q1618, Q1619, Q1620, Q1621, Q1622, Q1623, Q1624, Q1625, Q1626, Q1627, Q1628, Q1629, Q1630, Q1631, Q1632, Q1633, Q1634, Q1635, Q1636, Q1637, Q1638, Q1639, Q1640, Q1641, Q1642]), "depth" : 3 * mm, "offsetDistance" : 25 * mm});
        }
        {
            var Q0;
            Q0=makeQuery(id+"F1.opExtrude","CAP_EDGE",EDGE,{"disambiguationData":[OSD([sQuery(id+"F0.wireOp",EDGE,"E1.top")])],"isStart":false});
            fillet(context, id + "F12", {"entities" : qUnion([Q0]), "radius" : 3 * mm, "tangentPropagation" : true, "allowEdgeOverflow" : false});
        }
    });